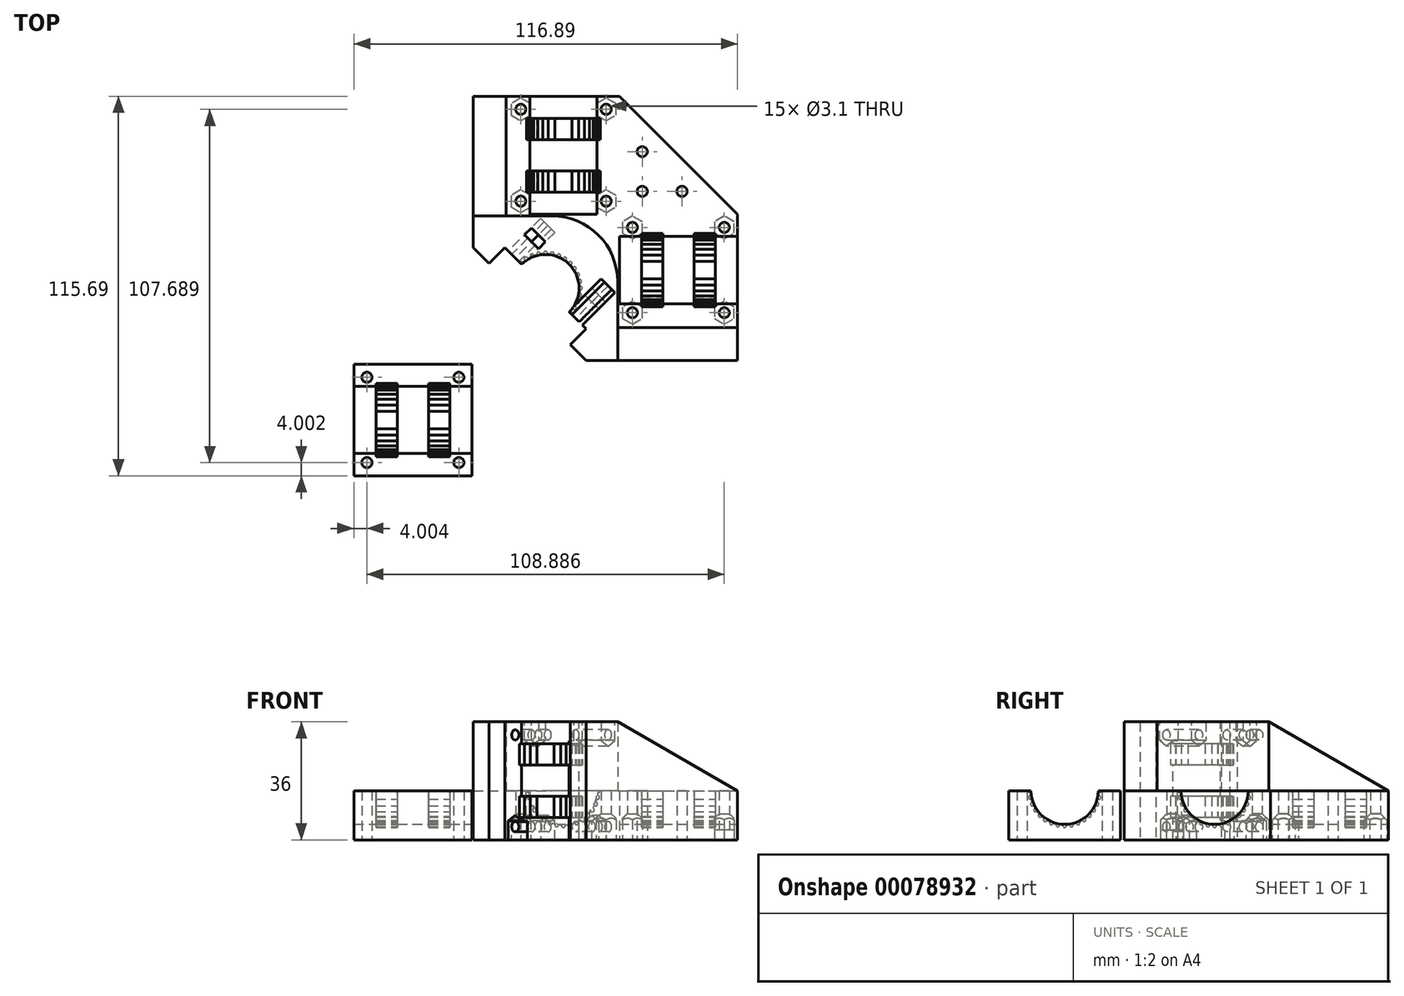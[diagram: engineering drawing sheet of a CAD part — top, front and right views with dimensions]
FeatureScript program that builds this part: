
annotation { "Feature Type Name" : "Feature", "Feature Type Description" : "" }
export const myFeature = defineFeature(function(context is Context, id is Id, definition is map)
    precondition{}
    {
        {
            var Q0;
            Q0=qCreatedBy(makeId("Top.planeOp"),FACE);
            var sketch = newSketch(context, id + "F0", { "sketchPlane" : qUnion([Q0])});
            skLineSegment(sketch, "E0.bottom", {"start": v(34, 0) * mm, "end": v(70, 0) * mm});
            skLineSegment(sketch, "E0.top", {"start": v(34, 34) * mm, "end": v(70, 34) * mm});
            skLineSegment(sketch, "E0.left", {"start": v(34, 0) * mm, "end": v(34, 34) * mm});
            skLineSegment(sketch, "E0.right", {"start": v(70, 0) * mm, "end": v(70, 34) * mm});
            skLineSegment(sketch, "E1", {"start": v(52, 34) * mm, "end": v(52, 0) * mm, "construction": true});
            skLineSegment(sketch, "E2", {"start": v(34, 17) * mm, "end": v(70, 17) * mm, "construction": true});
            skLineSegment(sketch, "E3", {"start": v(34, 34) * mm, "end": v(34, 70) * mm});
            skLineSegment(sketch, "E4", {"start": v(34, 70) * mm, "end": v(0, 70) * mm});
            skLineSegment(sketch, "E5", {"start": v(0, 70) * mm, "end": v(0, 34) * mm});
            skLineSegment(sketch, "E6", {"start": v(0, 34) * mm, "end": v(34, 34) * mm});
            skLineSegment(sketch, "E7", {"start": v(17, 70) * mm, "end": v(17, 34) * mm, "construction": true});
            skLineSegment(sketch, "E8", {"start": v(0, 52) * mm, "end": v(34, 52) * mm, "construction": true});
            skCircle(sketch, "E9", {"center": v(66, 30) * mm, "radius": 1.55 * mm});
            skPoint(sketch, "E10", {"position": v(60, 17) * mm});
            skCircle(sketch, "E11.MirrorC", {"center": v(38, 30) * mm, "radius": 1.55 * mm});
            skPoint(sketch, "E12.MirrorP", {"position": v(44, 17) * mm});
            skCircle(sketch, "E13.MirrorC", {"center": v(38, 4) * mm, "radius": 1.55 * mm});
            skCircle(sketch, "E14.MirrorC", {"center": v(66, 4) * mm, "radius": 1.55 * mm});
            skCircle(sketch, "E15", {"center": v(30, 66) * mm, "radius": 1.55 * mm});
            skPoint(sketch, "E16", {"position": v(17, 60) * mm});
            skCircle(sketch, "E17.MirrorC", {"center": v(4, 66) * mm, "radius": 1.55 * mm});
            skCircle(sketch, "E18.MirrorC", {"center": v(30, 38) * mm, "radius": 1.55 * mm});
            skPoint(sketch, "E19.MirrorP", {"position": v(17, 44) * mm});
            skCircle(sketch, "E20.MirrorC", {"center": v(4, 38) * mm, "radius": 1.55 * mm});
            skLineSegment(sketch, "E21", {"start": v(34, 70) * mm, "end": v(70, 34) * mm});
            skLineSegment(sketch, "E22", {"start": v(0, 70) * mm, "end": v(-0.5, 70) * mm});
            skLineSegment(sketch, "E23", {"start": v(-0.5, 70) * mm, "end": v(-0.5, 34) * mm});
            skLineSegment(sketch, "E24", {"start": v(33.5, -0.5) * mm, "end": v(70, -0.5) * mm});
            skLineSegment(sketch, "E25", {"start": v(70, -0.5) * mm, "end": v(70, 0) * mm});
            skLineSegment(sketch, "E26", {"start": v(-0.5, 34) * mm, "end": v(-0.5, 33.5) * mm});
            skLineSegment(sketch, "E27", {"start": v(-0.5, 33.5) * mm, "end": v(33.5, 33.5) * mm});
            skLineSegment(sketch, "E28", {"start": v(33.5, 33.5) * mm, "end": v(33.5, -0.5) * mm});
            skLineSegment(sketch, "E29", {"start": v(-0.5, 33.5) * mm, "end": v(33.5, -0.5) * mm});
            skLineSegment(sketch, "E30.0", {"start": v(41, 41) * mm, "end": v(41, 53.1) * mm, "construction": true});
            skLineSegment(sketch, "E30.1", {"start": v(41, 41) * mm, "end": v(53.1, 41) * mm, "construction": true});
            skLineSegment(sketch, "E30.2", {"start": v(41, 53.1) * mm, "end": v(53.1, 41) * mm, "construction": true});
            skLineSegment(sketch, "E31", {"start": v(70, -0.5) * mm, "end": v(70, -10.5) * mm});
            skLineSegment(sketch, "E32", {"start": v(70, -10.5) * mm, "end": v(33.5, -10.5) * mm});
            skLineSegment(sketch, "E33", {"start": v(33.5, -10.5) * mm, "end": v(-10.5, 33.5) * mm});
            skLineSegment(sketch, "E34", {"start": v(-10.5, 33.5) * mm, "end": v(-10.5, 70) * mm});
            skLineSegment(sketch, "E35", {"start": v(-10.5, 70) * mm, "end": v(-0.5, 70) * mm});
            skLineSegment(sketch, "E36", {"start": v(34, 34) * mm, "end": v(0, 0) * mm, "construction": true});
            skPoint(sketch, "E37", {"position": v(-0.87, 23.87) * mm});
            skPoint(sketch, "E38.MirrorP", {"position": v(23.87, -0.87) * mm});
            skLineSegment(sketch, "E39", {"start": v(33.5, -10.5) * mm, "end": v(23.87, -10.5) * mm});
            skLineSegment(sketch, "E40", {"start": v(23.87, -10.5) * mm, "end": v(23.87, -0.87) * mm});
            skLineSegment(sketch, "E41", {"start": v(-10.5, 33.5) * mm, "end": v(-10.5, 23.87) * mm});
            skLineSegment(sketch, "E42", {"start": v(-10.5, 23.87) * mm, "end": v(-0.87, 23.87) * mm});
            skLineSegment(sketch, "E43", {"start": v(23.87, -10.5) * mm, "end": v(19.06, -5.69) * mm});
            skLineSegment(sketch, "E44", {"start": v(19.06, -5.69) * mm, "end": v(23.87, -0.87) * mm});
            skLineSegment(sketch, "E45", {"start": v(-10.5, 23.87) * mm, "end": v(-5.69, 19.06) * mm});
            skLineSegment(sketch, "E46", {"start": v(-5.69, 19.06) * mm, "end": v(-0.87, 23.87) * mm});
            skCircle(sketch, "E47", {"center": v(41, 41) * mm, "radius": 1.55 * mm});
            skCircle(sketch, "E48", {"center": v(53.1, 41) * mm, "radius": 1.55 * mm});
            skCircle(sketch, "E49", {"center": v(41, 53.1) * mm, "radius": 1.55 * mm});
            skSolve(sketch);
        }
        {
            var Q0;
            Q0=makeQuery(id+"F0.imprint","IMPRINT",FACE,{"disambiguationData":[TD([[makeQuery(id+"F0.imprint","IMPRINT",EDGE,{"derivedFrom":sQuery(id+"F0.wireOp",EDGE,"E3")}),1.0]])]});
            var Q1;
            Q1=makeQuery(id+"F0.imprint","IMPRINT",FACE,{"disambiguationData":[TD([[makeQuery(id+"F0.imprint","IMPRINT",EDGE,{"derivedFrom":sQuery(id+"F0.wireOp",EDGE,"E0.bottom")}),1.0]])]});
            var Q2;
            Q2=makeQuery(id+"F0.imprint","IMPRINT",FACE,{"disambiguationData":[TD([[makeQuery(id+"F0.imprint","IMPRINT",EDGE,{"derivedFrom":sQuery(id+"F0.wireOp",EDGE,"E0.top")}),1.0]])]});
            var Q3;
            Q3=makeQuery(id+"F0.imprint","IMPRINT",FACE,{"disambiguationData":[TD([[makeQuery(id+"F0.imprint","IMPRINT",EDGE,{"derivedFrom":sQuery(id+"F0.wireOp",EDGE,"E0.bottom")}),-1.0]])]});
            extrude(context, id + "F1", {"entities" : qUnion([Q0, Q1, Q2, Q3]), "depth" : 15 * mm});
        }
        {
            var Q0;
            Q0=makeQuery(id+"F0.imprint","IMPRINT",FACE,{"disambiguationData":[TD([[makeQuery(id+"F0.imprint","IMPRINT",EDGE,{"derivedFrom":sQuery(id+"F0.wireOp",EDGE,"E27")}),-1.0]])]});
            var Q1;
            Q1=makeQuery(id+"F0.imprint","IMPRINT",FACE,{"disambiguationData":[TD([[makeQuery(id+"F0.imprint","IMPRINT",EDGE,{"derivedFrom":sQuery(id+"F0.wireOp",EDGE,"E23")}),-1.0]])]});
            var Q2;
            {var subQ0=sQuery(id+"F0.wireOp",EDGE,"E41");Q2=makeQuery(id+"F0.imprint","IMPRINT",FACE,{"disambiguationData":[TD([[makeQuery(id+"F0.imprint","IMPRINT",EDGE,{"derivedFrom":subQ0}),1.0]])]});}
            var Q3;
            {var subQ0=sQuery(id+"F0.wireOp",EDGE,"E39");Q3=makeQuery(id+"F0.imprint","IMPRINT",FACE,{"disambiguationData":[TD([[makeQuery(id+"F0.imprint","IMPRINT",EDGE,{"derivedFrom":subQ0}),-1.0]])]});}
            var Q4;
            Q4=makeQuery(id+"F0.imprint","IMPRINT",FACE,{"disambiguationData":[TD([[makeQuery(id+"F0.imprint","IMPRINT",EDGE,{"derivedFrom":sQuery(id+"F0.wireOp",EDGE,"E40")}),1.0]])]});
            var Q5;
            Q5=makeQuery(id+"F0.imprint","IMPRINT",FACE,{"disambiguationData":[TD([[makeQuery(id+"F0.imprint","IMPRINT",EDGE,{"derivedFrom":sQuery(id+"F0.wireOp",EDGE,"E42")}),-1.0]])]});
            extrude(context, id + "F2", {"entities" : qUnion([Q0, Q1, Q2, Q3, Q4, Q5]), "operationType" : NewBodyOperationType.ADD, "depth" : 36 * mm});
        }
        {
            var Q0;
            Q0=makeQuery(id+"F1.opExtrude","SWEPT_FACE",FACE,{"disambiguationData":[OSD([sQuery(id+"F0.wireOp",EDGE,"E0.right"),sQuery(id+"F0.wireOp",EDGE,"E25")])]});
            var sketch = newSketch(context, id + "F3", { "sketchPlane" : qUnion([Q0])});
            skLineSegment(sketch, "E50.0", {"start": v(5.55, 15) * mm, "end": v(2.45, 15) * mm});
            skLineSegment(sketch, "E51.0", {"start": v(28.45, 15) * mm, "end": v(31.55, 15) * mm});
            skLineSegment(sketch, "E52", {"start": v(5.55, 15) * mm, "end": v(28.45, 15) * mm});
            skPoint(sketch, "E53", {"position": v(17, 15) * mm});
            skArc(sketch, "E54", {"start": v(6.75, 15) * mm, "mid": v(17, 4.75) * mm, "end": v(27.25, 15) * mm});
            skSolve(sketch);
        }
        {
            var Q0;
            Q0=qSketchRegion(id+"F3",true);
            var Q1;
            Q1=makeQuery(id+"F2.opExtrude","SWEPT_FACE",FACE,{"disambiguationData":[OSD([sQuery(id+"F0.wireOp",EDGE,"E28")])]});
            extrude(context, id + "F4", {"entities" : qUnion([Q0]), "operationType" : NewBodyOperationType.REMOVE, "oppositeDirection" : true, "endBoundEntityFace" : qUnion([Q1]), "depth" : 36 * mm});
        }
        {
            var Q0;
            Q0=makeQuery(id+"F1.opExtrude","SWEPT_FACE",FACE,{"disambiguationData":[OSD([sQuery(id+"F0.wireOp",EDGE,"E4"),sQuery(id+"F0.wireOp",EDGE,"E22")])]});
            var sketch = newSketch(context, id + "F5", { "sketchPlane" : qUnion([Q0])});
            skLineSegment(sketch, "E55", {"start": v(-28.45, 15) * mm, "end": v(-5.55, 15) * mm});
            skPoint(sketch, "E56.0.start.orphan", {"position": v(-31.55, 15) * mm});
            skPoint(sketch, "E57.0.start.orphan", {"position": v(-2.45, 15) * mm});
            skPoint(sketch, "E58", {"position": v(-17, 15) * mm});
            skArc(sketch, "E59", {"start": v(-27.25, 15) * mm, "mid": v(-17, 4.75) * mm, "end": v(-6.75, 15) * mm});
            skSolve(sketch);
        }
        {
            var Q0;
            Q0=qSketchRegion(id+"F5",true);
            var Q1;
            Q1=makeQuery(id+"F2.opExtrude","SWEPT_FACE",FACE,{"disambiguationData":[OSD([sQuery(id+"F0.wireOp",EDGE,"E27")])]});
            extrude(context, id + "F6", {"entities" : qUnion([Q0]), "operationType" : NewBodyOperationType.REMOVE, "oppositeDirection" : true, "endBoundEntityFace" : qUnion([Q1]), "depth" : 36 * mm});
        }
        {
            var Q0;
            Q0=makeQuery(id+"F2.opExtrude","CAP_FACE",FACE,{"disambiguationData":[OSD([sQuery(id+"F0.wireOp",EDGE,"E23"),sQuery(id+"F0.wireOp",EDGE,"E24"),sQuery(id+"F0.wireOp",EDGE,"E26"),sQuery(id+"F0.wireOp",EDGE,"E27"),sQuery(id+"F0.wireOp",EDGE,"E28"),sQuery(id+"F0.wireOp",EDGE,"E31"),sQuery(id+"F0.wireOp",EDGE,"E32"),sQuery(id+"F0.wireOp",EDGE,"E33"),sQuery(id+"F0.wireOp",EDGE,"E34"),sQuery(id+"F0.wireOp",EDGE,"E35")])],"isStart":false});
            var sketch = newSketch(context, id + "F7", { "sketchPlane" : qUnion([Q0])});
            skLineSegment(sketch, "E60.0", {"start": v(-0.87, 23.87) * mm, "end": v(23.87, -0.87) * mm});
            skArc(sketch, "E61", {"start": v(18.75, 4.25) * mm, "mid": v(18.75, 18.75) * mm, "end": v(4.25, 18.75) * mm});
            skSolve(sketch);
        }
        {
            var Q0;
            Q0=qSketchRegion(id+"F7",true);
            var Q1;
            Q1=makeQuery(id+"F2.opExtrude","CAP_FACE",FACE,{"disambiguationData":[OSD([sQuery(id+"F0.wireOp",EDGE,"E27"),sQuery(id+"F0.wireOp",EDGE,"E28"),sQuery(id+"F0.wireOp",EDGE,"E29")])],"isStart":true});
            extrude(context, id + "F8", {"entities" : qUnion([Q0]), "operationType" : NewBodyOperationType.REMOVE, "endBound" : BoundingType.UP_TO_SURFACE, "oppositeDirection" : true, "endBoundEntityFace" : qUnion([Q1]), "depth" : 25 * mm});
        }
        {
            var Q0;
            {var subQ0=sQuery(id+"F0.wireOp",EDGE,"E44");var subQ8=sQuery(id+"F0.wireOp",EDGE,"E33");Q0=makeQuery(id+"F8.boolean.opBoolean","SPLIT",FACE,{"disambiguationData":[TD([makeQuery(id+"F2.opExtrude","SWEPT_FACE",FACE,{"disambiguationData":[OSD([subQ0])]})])],"derivedFrom":makeQuery(id+"F2.opExtrude","SWEPT_FACE",FACE,{"disambiguationData":[OSD([subQ8])]})});}
            cPlane(context, id + "F9", {"entities" : qUnion([Q0]), "cplaneType" : CPlaneType.OFFSET, "offset" : 7 * mm, "oppositeDirection" : true, "width" : 150 * mm, "height" : 150 * mm});
        }
        {
            var Q0;
            Q0=qCreatedBy(id+"F9.planeOp",FACE);
            var sketch = newSketch(context, id + "F10", { "sketchPlane" : qUnion([Q0])});
            skPoint(sketch, "E62.0", {"position": v(-24.04, 36) * mm});
            skPoint(sketch, "E63.0", {"position": v(24.04, 36) * mm});
            skPoint(sketch, "E64.0", {"position": v(24.04, 0) * mm});
            skPoint(sketch, "E65.0", {"position": v(-24.04, 0) * mm});
            skLineSegment(sketch, "E66", {"start": v(-24.04, 0) * mm, "end": v(-24.04, 36) * mm, "construction": true});
            skLineSegment(sketch, "E67", {"start": v(-24.04, 36) * mm, "end": v(24.04, 36) * mm, "construction": true});
            skLineSegment(sketch, "E68", {"start": v(24.04, 36) * mm, "end": v(24.04, 0) * mm, "construction": true});
            skLineSegment(sketch, "E69", {"start": v(24.04, 0) * mm, "end": v(-24.04, 0) * mm, "construction": true});
            skLineSegment(sketch, "E70", {"start": v(0, 0) * mm, "end": v(0, 36) * mm, "construction": true});
            skLineSegment(sketch, "E71", {"start": v(-24.04, 18) * mm, "end": v(24.04, 18) * mm, "construction": true});
            skCircle(sketch, "E72", {"center": v(-13, 32) * mm, "radius": 1.55 * mm});
            skCircle(sketch, "E73.cCircle", {"center": v(-13, 32) * mm, "radius": 3 * mm, "construction": true});
            skLineSegment(sketch, "E73.0", {"start": v(-10, 33.73) * mm, "end": v(-10, 30.27) * mm});
            skLineSegment(sketch, "E73.1", {"start": v(-10, 30.27) * mm, "end": v(-13, 28.54) * mm});
            skLineSegment(sketch, "E73.2", {"start": v(-13, 28.54) * mm, "end": v(-16, 30.27) * mm});
            skLineSegment(sketch, "E73.3", {"start": v(-16, 30.27) * mm, "end": v(-16, 33.73) * mm});
            skLineSegment(sketch, "E73.4", {"start": v(-16, 33.73) * mm, "end": v(-13, 35.46) * mm, "construction": true});
            skLineSegment(sketch, "E73.5", {"start": v(-13, 35.46) * mm, "end": v(-10, 33.73) * mm, "construction": true});
            skPoint(sketch, "E73.0.midPoint", {"position": v(-10, 32) * mm});
            skLineSegment(sketch, "E74", {"start": v(-16, 33.73) * mm, "end": v(-16, 36) * mm});
            skLineSegment(sketch, "E75", {"start": v(-16, 36) * mm, "end": v(-10, 36) * mm});
            skLineSegment(sketch, "E76", {"start": v(-10, 36) * mm, "end": v(-10, 33.73) * mm});
            skCircle(sketch, "E77.MirrorC", {"center": v(-13, 4) * mm, "radius": 1.55 * mm});
            skLineSegment(sketch, "E78.MirrorCS", {"start": v(-16, 2.27) * mm, "end": v(-16, 0) * mm});
            skLineSegment(sketch, "E79.MirrorCS", {"start": v(-16, 5.73) * mm, "end": v(-16, 2.27) * mm});
            skLineSegment(sketch, "E80.MirrorCS", {"start": v(-13, 7.46) * mm, "end": v(-16, 5.73) * mm});
            skLineSegment(sketch, "E81.MirrorCS", {"start": v(-10, 5.73) * mm, "end": v(-13, 7.46) * mm});
            skLineSegment(sketch, "E82.MirrorCS", {"start": v(-10, 2.27) * mm, "end": v(-10, 5.73) * mm});
            skLineSegment(sketch, "E83.MirrorCS", {"start": v(-10, 0) * mm, "end": v(-10, 2.27) * mm});
            skLineSegment(sketch, "E84.MirrorCS", {"start": v(10, 36) * mm, "end": v(10, 33.73) * mm});
            skLineSegment(sketch, "E85.MirrorCS", {"start": v(10, 33.73) * mm, "end": v(10, 30.27) * mm});
            skLineSegment(sketch, "E86.MirrorCS", {"start": v(10, 30.27) * mm, "end": v(13, 28.54) * mm});
            skLineSegment(sketch, "E87.MirrorCS", {"start": v(13, 28.54) * mm, "end": v(16, 30.27) * mm});
            skLineSegment(sketch, "E88.MirrorCS", {"start": v(16, 30.27) * mm, "end": v(16, 33.73) * mm});
            skLineSegment(sketch, "E89.MirrorCS", {"start": v(16, 33.73) * mm, "end": v(16, 36) * mm});
            skCircle(sketch, "E90.MirrorC", {"center": v(13, 32) * mm, "radius": 1.55 * mm});
            skLineSegment(sketch, "E91.MirrorCS", {"start": v(16, 2.27) * mm, "end": v(16, 0) * mm});
            skLineSegment(sketch, "E92.MirrorCS", {"start": v(16, 5.73) * mm, "end": v(16, 2.27) * mm});
            skLineSegment(sketch, "E93.MirrorCS", {"start": v(13, 7.46) * mm, "end": v(16, 5.73) * mm});
            skLineSegment(sketch, "E94.MirrorCS", {"start": v(10, 5.73) * mm, "end": v(13, 7.46) * mm});
            skLineSegment(sketch, "E95.MirrorCS", {"start": v(10, 2.27) * mm, "end": v(10, 5.73) * mm});
            skLineSegment(sketch, "E96.MirrorCS", {"start": v(10, 0) * mm, "end": v(10, 2.27) * mm});
            skCircle(sketch, "E97.MirrorC", {"center": v(13, 4) * mm, "radius": 1.55 * mm});
            skLineSegment(sketch, "E98", {"start": v(-16, 0) * mm, "end": v(-10, 0) * mm});
            skLineSegment(sketch, "E99", {"start": v(10, 0) * mm, "end": v(16, 0) * mm});
            skLineSegment(sketch, "E100", {"start": v(16, 36) * mm, "end": v(10, 36) * mm});
            skLineSegment(sketch, "E101", {"start": v(-13, 32) * mm, "end": v(-13, 36) * mm, "construction": true});
            skLineSegment(sketch, "E102.0", {"start": v(-10.25, 0) * mm, "end": v(-10.25, 36) * mm, "construction": true});
            skLineSegment(sketch, "E103.0", {"start": v(10.25, 0) * mm, "end": v(10.25, 36) * mm, "construction": true});
            skPoint(sketch, "E104", {"position": v(0, 18) * mm});
            skPoint(sketch, "E105", {"position": v(0, 26) * mm});
            skPoint(sketch, "E106.MirrorP", {"position": v(0, 10) * mm});
            skSolve(sketch);
        }
        {
            var Q0;
            Q0=makeQuery(id+"F10.imprint","IMPRINT",FACE,{"disambiguationData":[TD([[makeQuery(id+"F10.imprint","IMPRINT",EDGE,{"derivedFrom":sQuery(id+"F10.wireOp",EDGE,"E72")}),1.0]])]});
            var Q1;
            Q1=makeQuery(id+"F10.imprint","IMPRINT",FACE,{"disambiguationData":[TD([[makeQuery(id+"F10.imprint","IMPRINT",EDGE,{"derivedFrom":sQuery(id+"F10.wireOp",EDGE,"E77.MirrorC")}),-1.0]])]});
            var Q2;
            Q2=makeQuery(id+"F10.imprint","IMPRINT",FACE,{"disambiguationData":[TD([[makeQuery(id+"F10.imprint","IMPRINT",EDGE,{"derivedFrom":sQuery(id+"F10.wireOp",EDGE,"E97.MirrorC")}),1.0]])]});
            var Q3;
            Q3=makeQuery(id+"F10.imprint","IMPRINT",FACE,{"disambiguationData":[TD([[makeQuery(id+"F10.imprint","IMPRINT",EDGE,{"derivedFrom":sQuery(id+"F10.wireOp",EDGE,"E90.MirrorC")}),-1.0]])]});
            extrude(context, id + "F11", {"entities" : qUnion([Q0, Q1, Q2, Q3]), "operationType" : NewBodyOperationType.REMOVE, "oppositeDirection" : true, "depth" : 7 * mm, "hasSecondDirection" : true, "secondDirectionOppositeDirection" : false, "secondDirectionDepth" : 25 * mm});
        }
        {
            var Q0;
            Q0=makeQuery(id+"F10.imprint","IMPRINT",FACE,{"disambiguationData":[TD([[makeQuery(id+"F10.imprint","IMPRINT",EDGE,{"derivedFrom":sQuery(id+"F10.wireOp",EDGE,"E72")}),-1.0]])]});
            var Q1;
            Q1=makeQuery(id+"F10.imprint","IMPRINT",FACE,{"disambiguationData":[TD([[makeQuery(id+"F10.imprint","IMPRINT",EDGE,{"derivedFrom":sQuery(id+"F10.wireOp",EDGE,"E77.MirrorC")}),1.0]])]});
            var Q2;
            Q2=makeQuery(id+"F10.imprint","IMPRINT",FACE,{"disambiguationData":[TD([[makeQuery(id+"F10.imprint","IMPRINT",EDGE,{"derivedFrom":sQuery(id+"F10.wireOp",EDGE,"E91.MirrorCS")}),-1.0]])]});
            var Q3;
            Q3=makeQuery(id+"F10.imprint","IMPRINT",FACE,{"disambiguationData":[TD([[makeQuery(id+"F10.imprint","IMPRINT",EDGE,{"derivedFrom":sQuery(id+"F10.wireOp",EDGE,"E84.MirrorCS")}),1.0]])]});
            extrude(context, id + "F12", {"entities" : qUnion([Q0, Q1, Q2, Q3]), "operationType" : NewBodyOperationType.REMOVE, "oppositeDirection" : true, "depth" : 3 * mm});
        }
        {
            var Q0;
            Q0=makeQuery(id+"F2.opExtrude","SWEPT_FACE",FACE,{"disambiguationData":[OSD([sQuery(id+"F0.wireOp",EDGE,"E24")])]});
            var sketch = newSketch(context, id + "F13", { "sketchPlane" : qUnion([Q0])});
            skLineSegment(sketch, "E107", {"start": v(-33.5, 36) * mm, "end": v(-70, 15) * mm});
            skLineSegment(sketch, "E108.0", {"start": v(-33.5, 36) * mm, "end": v(-70, 36) * mm});
            skLineSegment(sketch, "E109.0", {"start": v(-70, 36) * mm, "end": v(-70, 15) * mm});
            skSolve(sketch);
        }
        {
            var Q0;
            Q0=qSketchRegion(id+"F13",true);
            var Q1;
            Q1=makeQuery(id+"F2.opExtrude","SWEPT_FACE",FACE,{"disambiguationData":[OSD([sQuery(id+"F0.wireOp",EDGE,"E32"),sQuery(id+"F0.wireOp",EDGE,"E39")])]});
            extrude(context, id + "F14", {"entities" : qUnion([Q0]), "operationType" : NewBodyOperationType.REMOVE, "endBound" : BoundingType.UP_TO_SURFACE, "oppositeDirection" : true, "endBoundEntityFace" : qUnion([Q1]), "depth" : 25 * mm});
        }
        {
            var Q0;
            Q0=makeQuery(id+"F2.opExtrude","SWEPT_FACE",FACE,{"disambiguationData":[OSD([sQuery(id+"F0.wireOp",EDGE,"E23"),sQuery(id+"F0.wireOp",EDGE,"E26")])]});
            var sketch = newSketch(context, id + "F15", { "sketchPlane" : qUnion([Q0])});
            skLineSegment(sketch, "E110.0", {"start": v(70, 36) * mm, "end": v(33.5, 36) * mm});
            skLineSegment(sketch, "E111.0", {"start": v(70, 36) * mm, "end": v(70, 15) * mm});
            skLineSegment(sketch, "E112", {"start": v(33.5, 36) * mm, "end": v(70, 15) * mm});
            skSolve(sketch);
        }
        {
            var Q0;
            Q0=qSketchRegion(id+"F15",true);
            var Q1;
            Q1=makeQuery(id+"F2.opExtrude","SWEPT_FACE",FACE,{"disambiguationData":[OSD([sQuery(id+"F0.wireOp",EDGE,"E34"),sQuery(id+"F0.wireOp",EDGE,"E41")])]});
            extrude(context, id + "F16", {"entities" : qUnion([Q0]), "operationType" : NewBodyOperationType.REMOVE, "endBound" : BoundingType.UP_TO_SURFACE, "oppositeDirection" : true, "endBoundEntityFace" : qUnion([Q1]), "depth" : 25 * mm});
        }
        {
            var Q0;
            Q0=makeQuery(id+"F2.opExtrude","SWEPT_EDGE",EDGE,{"disambiguationData":[OSD([sQuery(id+"F0.wireOp",EDGE,"E27"),sQuery(id+"F0.wireOp",EDGE,"E28")])]});
            fillet(context, id + "F17", {"entities" : qUnion([Q0]), "radius" : 20 * mm, "tangentPropagation" : true, "allowEdgeOverflow" : false});
        }
        {
            var Q0;
            {var subQ0=sQuery(id+"F0.wireOp",EDGE,"E28");var subQ1=sQuery(id+"F0.wireOp",EDGE,"E27");var subQ2=sQuery(id+"F0.wireOp",EDGE,"E26");var subQ3=sQuery(id+"F0.wireOp",EDGE,"E24");var subQ4=sQuery(id+"F0.wireOp",EDGE,"E23");Q0=makeQuery(id+"F2.boolean.opBoolean","MERGE",FACE,{"derivedFrom":[makeQuery(id+"F1.opExtrude","CAP_FACE",FACE,{"disambiguationData":[OSD([sQuery(id+"F0.wireOp",EDGE,"E0.right"),sQuery(id+"F0.wireOp",EDGE,"E4"),sQuery(id+"F0.wireOp",EDGE,"E9"),sQuery(id+"F0.wireOp",EDGE,"E11.MirrorC"),sQuery(id+"F0.wireOp",EDGE,"E13.MirrorC"),sQuery(id+"F0.wireOp",EDGE,"E14.MirrorC"),sQuery(id+"F0.wireOp",EDGE,"E15"),sQuery(id+"F0.wireOp",EDGE,"E17.MirrorC"),sQuery(id+"F0.wireOp",EDGE,"E18.MirrorC"),sQuery(id+"F0.wireOp",EDGE,"E20.MirrorC"),sQuery(id+"F0.wireOp",EDGE,"E21"),sQuery(id+"F0.wireOp",EDGE,"E22"),subQ4,subQ3,sQuery(id+"F0.wireOp",EDGE,"E25"),subQ2,subQ1,subQ0,sQuery(id+"F0.wireOp",EDGE,"E30.0"),sQuery(id+"F0.wireOp",EDGE,"E30.1"),sQuery(id+"F0.wireOp",EDGE,"E30.2")])],"isStart":true}),makeQuery(id+"F2.opExtrude","CAP_FACE",FACE,{"disambiguationData":[OSD([subQ4,subQ3,subQ2,subQ1,subQ0,sQuery(id+"F0.wireOp",EDGE,"E31"),sQuery(id+"F0.wireOp",EDGE,"E32"),sQuery(id+"F0.wireOp",EDGE,"E33"),sQuery(id+"F0.wireOp",EDGE,"E34"),sQuery(id+"F0.wireOp",EDGE,"E35"),sQuery(id+"F0.wireOp",EDGE,"E39"),sQuery(id+"F0.wireOp",EDGE,"E41"),sQuery(id+"F0.wireOp",EDGE,"E43"),sQuery(id+"F0.wireOp",EDGE,"E44"),sQuery(id+"F0.wireOp",EDGE,"E45"),sQuery(id+"F0.wireOp",EDGE,"E46")])],"isStart":true})]});}
            var sketch = newSketch(context, id + "F18", { "sketchPlane" : qUnion([Q0])});
            skCircle(sketch, "E113.0", {"center": v(66, -4) * mm, "radius": 1.55 * mm});
            skCircle(sketch, "E114.0", {"center": v(66, -30) * mm, "radius": 1.55 * mm, "construction": true});
            skCircle(sketch, "E115.0", {"center": v(38, -4) * mm, "radius": 1.55 * mm, "construction": true});
            skCircle(sketch, "E116.0", {"center": v(38, -30) * mm, "radius": 1.55 * mm, "construction": true});
            skCircle(sketch, "E117.0", {"center": v(30, -38) * mm, "radius": 1.55 * mm, "construction": true});
            skCircle(sketch, "E118.0", {"center": v(30, -66) * mm, "radius": 1.55 * mm, "construction": true});
            skCircle(sketch, "E119.0", {"center": v(4, -66) * mm, "radius": 1.55 * mm, "construction": true});
            skCircle(sketch, "E120.0", {"center": v(4, -38) * mm, "radius": 1.55 * mm, "construction": true});
            skCircle(sketch, "E121.cCircle", {"center": v(66, -4) * mm, "radius": 3 * mm, "construction": true});
            skLineSegment(sketch, "E121.0", {"start": v(66, -7.46) * mm, "end": v(63, -5.73) * mm});
            skLineSegment(sketch, "E121.1", {"start": v(63, -5.73) * mm, "end": v(63, -2.27) * mm});
            skLineSegment(sketch, "E121.2", {"start": v(63, -2.27) * mm, "end": v(66, -0.54) * mm});
            skLineSegment(sketch, "E121.3", {"start": v(66, -0.54) * mm, "end": v(69, -2.27) * mm});
            skLineSegment(sketch, "E121.4", {"start": v(69, -2.27) * mm, "end": v(69, -5.73) * mm});
            skLineSegment(sketch, "E121.5", {"start": v(69, -5.73) * mm, "end": v(66, -7.46) * mm});
            skPoint(sketch, "E121.0.midPoint", {"position": v(64.5, -6.6) * mm});
            skCircle(sketch, "E122.cCircle", {"center": v(66, -30) * mm, "radius": 3 * mm, "construction": true});
            skLineSegment(sketch, "E122.0", {"start": v(63, -31.73) * mm, "end": v(63, -28.27) * mm});
            skLineSegment(sketch, "E122.1", {"start": v(63, -28.27) * mm, "end": v(66, -26.54) * mm});
            skLineSegment(sketch, "E122.2", {"start": v(66, -26.54) * mm, "end": v(69, -28.27) * mm});
            skLineSegment(sketch, "E122.3", {"start": v(69, -28.27) * mm, "end": v(69, -31.73) * mm});
            skLineSegment(sketch, "E122.4", {"start": v(69, -31.73) * mm, "end": v(66, -33.46) * mm});
            skLineSegment(sketch, "E122.5", {"start": v(66, -33.46) * mm, "end": v(63, -31.73) * mm});
            skPoint(sketch, "E122.0.midPoint", {"position": v(63, -30) * mm});
            skCircle(sketch, "E123.cCircle", {"center": v(38, -4) * mm, "radius": 3 * mm, "construction": true});
            skLineSegment(sketch, "E123.0", {"start": v(35, -5.73) * mm, "end": v(35, -2.27) * mm});
            skLineSegment(sketch, "E123.1", {"start": v(35, -2.27) * mm, "end": v(38, -0.54) * mm});
            skLineSegment(sketch, "E123.2", {"start": v(38, -0.54) * mm, "end": v(41, -2.27) * mm});
            skLineSegment(sketch, "E123.3", {"start": v(41, -2.27) * mm, "end": v(41, -5.73) * mm});
            skLineSegment(sketch, "E123.4", {"start": v(41, -5.73) * mm, "end": v(38, -7.46) * mm});
            skLineSegment(sketch, "E123.5", {"start": v(38, -7.46) * mm, "end": v(35, -5.73) * mm});
            skPoint(sketch, "E123.0.midPoint", {"position": v(35, -4) * mm});
            skCircle(sketch, "E124.cCircle", {"center": v(38, -30) * mm, "radius": 3 * mm, "construction": true});
            skLineSegment(sketch, "E124.0", {"start": v(35, -31.73) * mm, "end": v(35, -28.27) * mm});
            skLineSegment(sketch, "E124.1", {"start": v(35, -28.27) * mm, "end": v(38, -26.54) * mm});
            skLineSegment(sketch, "E124.2", {"start": v(38, -26.54) * mm, "end": v(41, -28.27) * mm});
            skLineSegment(sketch, "E124.3", {"start": v(41, -28.27) * mm, "end": v(41, -31.73) * mm});
            skLineSegment(sketch, "E124.4", {"start": v(41, -31.73) * mm, "end": v(38, -33.46) * mm});
            skLineSegment(sketch, "E124.5", {"start": v(38, -33.46) * mm, "end": v(35, -31.73) * mm});
            skPoint(sketch, "E124.0.midPoint", {"position": v(35, -30) * mm});
            skCircle(sketch, "E125.cCircle", {"center": v(30, -38) * mm, "radius": 3 * mm, "construction": true});
            skLineSegment(sketch, "E125.0", {"start": v(27, -39.73) * mm, "end": v(27, -36.27) * mm});
            skLineSegment(sketch, "E125.1", {"start": v(27, -36.27) * mm, "end": v(30, -34.54) * mm});
            skLineSegment(sketch, "E125.2", {"start": v(30, -34.54) * mm, "end": v(33, -36.27) * mm});
            skLineSegment(sketch, "E125.3", {"start": v(33, -36.27) * mm, "end": v(33, -39.73) * mm});
            skLineSegment(sketch, "E125.4", {"start": v(33, -39.73) * mm, "end": v(30, -41.46) * mm});
            skLineSegment(sketch, "E125.5", {"start": v(30, -41.46) * mm, "end": v(27, -39.73) * mm});
            skPoint(sketch, "E125.0.midPoint", {"position": v(27, -38) * mm});
            skCircle(sketch, "E126.cCircle", {"center": v(4, -38) * mm, "radius": 3 * mm, "construction": true});
            skLineSegment(sketch, "E126.0", {"start": v(1, -39.73) * mm, "end": v(1, -36.27) * mm});
            skLineSegment(sketch, "E126.1", {"start": v(1, -36.27) * mm, "end": v(4, -34.54) * mm});
            skLineSegment(sketch, "E126.2", {"start": v(4, -34.54) * mm, "end": v(7, -36.27) * mm});
            skLineSegment(sketch, "E126.3", {"start": v(7, -36.27) * mm, "end": v(7, -39.73) * mm});
            skLineSegment(sketch, "E126.4", {"start": v(7, -39.73) * mm, "end": v(4, -41.46) * mm});
            skLineSegment(sketch, "E126.5", {"start": v(4, -41.46) * mm, "end": v(1, -39.73) * mm});
            skPoint(sketch, "E126.0.midPoint", {"position": v(1, -38) * mm});
            skCircle(sketch, "E127.cCircle", {"center": v(4, -66) * mm, "radius": 3 * mm, "construction": true});
            skLineSegment(sketch, "E127.0", {"start": v(1, -67.73) * mm, "end": v(1, -64.27) * mm});
            skLineSegment(sketch, "E127.1", {"start": v(1, -64.27) * mm, "end": v(4, -62.54) * mm});
            skLineSegment(sketch, "E127.2", {"start": v(4, -62.54) * mm, "end": v(7, -64.27) * mm});
            skLineSegment(sketch, "E127.3", {"start": v(7, -64.27) * mm, "end": v(7, -67.73) * mm});
            skLineSegment(sketch, "E127.4", {"start": v(7, -67.73) * mm, "end": v(4, -69.46) * mm});
            skLineSegment(sketch, "E127.5", {"start": v(4, -69.46) * mm, "end": v(1, -67.73) * mm});
            skPoint(sketch, "E127.0.midPoint", {"position": v(1, -66) * mm});
            skCircle(sketch, "E128.cCircle", {"center": v(30, -66) * mm, "radius": 3 * mm, "construction": true});
            skLineSegment(sketch, "E128.0", {"start": v(27, -67.73) * mm, "end": v(27, -64.27) * mm});
            skLineSegment(sketch, "E128.1", {"start": v(27, -64.27) * mm, "end": v(30, -62.54) * mm});
            skLineSegment(sketch, "E128.2", {"start": v(30, -62.54) * mm, "end": v(33, -64.27) * mm});
            skLineSegment(sketch, "E128.3", {"start": v(33, -64.27) * mm, "end": v(33, -67.73) * mm});
            skLineSegment(sketch, "E128.4", {"start": v(33, -67.73) * mm, "end": v(30, -69.46) * mm});
            skLineSegment(sketch, "E128.5", {"start": v(30, -69.46) * mm, "end": v(27, -67.73) * mm});
            skPoint(sketch, "E128.0.midPoint", {"position": v(27, -66) * mm});
            skSolve(sketch);
        }
        {
            var Q0;
            Q0=qSketchRegion(id+"F18",true);
            extrude(context, id + "F19", {"entities" : qUnion([Q0]), "operationType" : NewBodyOperationType.REMOVE, "oppositeDirection" : true, "depth" : 3 * mm});
        }
        {
            var Q0;
            Q0=makeQuery(id+"F19.boolean.opBoolean","COPY",EDGE,{"derivedFrom":makeQuery(id+"F19.opExtrude","CAP_EDGE",EDGE,{"disambiguationData":[OSD([sQuery(id+"F18.wireOp",EDGE,"E113.0")])],"isStart":false})});
            var Q1;
            Q1=makeQuery(id+"F19.boolean.opBoolean","INTERSECT",EDGE,{"derivedFrom":[makeQuery(id+"F1.opExtrude","SWEPT_FACE",FACE,{"disambiguationData":[OSD([sQuery(id+"F0.wireOp",EDGE,"E9")])]}),makeQuery(id+"F19.opExtrude","CAP_FACE",FACE,{"disambiguationData":[OSD([sQuery(id+"F18.wireOp",EDGE,"E122.0"),sQuery(id+"F18.wireOp",EDGE,"E122.1"),sQuery(id+"F18.wireOp",EDGE,"E122.2"),sQuery(id+"F18.wireOp",EDGE,"E122.3"),sQuery(id+"F18.wireOp",EDGE,"E122.4"),sQuery(id+"F18.wireOp",EDGE,"E122.5")])],"isStart":false})]});
            var Q2;
            Q2=makeQuery(id+"F19.boolean.opBoolean","INTERSECT",EDGE,{"derivedFrom":[makeQuery(id+"F1.opExtrude","SWEPT_FACE",FACE,{"disambiguationData":[OSD([sQuery(id+"F0.wireOp",EDGE,"E13.MirrorC")])]}),makeQuery(id+"F19.opExtrude","CAP_FACE",FACE,{"disambiguationData":[OSD([sQuery(id+"F18.wireOp",EDGE,"E123.0"),sQuery(id+"F18.wireOp",EDGE,"E123.1"),sQuery(id+"F18.wireOp",EDGE,"E123.2"),sQuery(id+"F18.wireOp",EDGE,"E123.3"),sQuery(id+"F18.wireOp",EDGE,"E123.4"),sQuery(id+"F18.wireOp",EDGE,"E123.5")])],"isStart":false})]});
            var Q3;
            Q3=makeQuery(id+"F19.boolean.opBoolean","INTERSECT",EDGE,{"derivedFrom":[makeQuery(id+"F1.opExtrude","SWEPT_FACE",FACE,{"disambiguationData":[OSD([sQuery(id+"F0.wireOp",EDGE,"E11.MirrorC")])]}),makeQuery(id+"F19.opExtrude","CAP_FACE",FACE,{"disambiguationData":[OSD([sQuery(id+"F18.wireOp",EDGE,"E124.0"),sQuery(id+"F18.wireOp",EDGE,"E124.1"),sQuery(id+"F18.wireOp",EDGE,"E124.2"),sQuery(id+"F18.wireOp",EDGE,"E124.3"),sQuery(id+"F18.wireOp",EDGE,"E124.4"),sQuery(id+"F18.wireOp",EDGE,"E124.5")])],"isStart":false})]});
            var Q4;
            Q4=makeQuery(id+"F19.boolean.opBoolean","INTERSECT",EDGE,{"derivedFrom":[makeQuery(id+"F1.opExtrude","SWEPT_FACE",FACE,{"disambiguationData":[OSD([sQuery(id+"F0.wireOp",EDGE,"E18.MirrorC")])]}),makeQuery(id+"F19.opExtrude","CAP_FACE",FACE,{"disambiguationData":[OSD([sQuery(id+"F18.wireOp",EDGE,"E125.0"),sQuery(id+"F18.wireOp",EDGE,"E125.1"),sQuery(id+"F18.wireOp",EDGE,"E125.2"),sQuery(id+"F18.wireOp",EDGE,"E125.3"),sQuery(id+"F18.wireOp",EDGE,"E125.4"),sQuery(id+"F18.wireOp",EDGE,"E125.5")])],"isStart":false})]});
            var Q5;
            Q5=makeQuery(id+"F19.boolean.opBoolean","INTERSECT",EDGE,{"derivedFrom":[makeQuery(id+"F1.opExtrude","SWEPT_FACE",FACE,{"disambiguationData":[OSD([sQuery(id+"F0.wireOp",EDGE,"E15")])]}),makeQuery(id+"F19.opExtrude","CAP_FACE",FACE,{"disambiguationData":[OSD([sQuery(id+"F18.wireOp",EDGE,"E128.0"),sQuery(id+"F18.wireOp",EDGE,"E128.1"),sQuery(id+"F18.wireOp",EDGE,"E128.2"),sQuery(id+"F18.wireOp",EDGE,"E128.3"),sQuery(id+"F18.wireOp",EDGE,"E128.4"),sQuery(id+"F18.wireOp",EDGE,"E128.5")])],"isStart":false})]});
            var Q6;
            Q6=makeQuery(id+"F19.boolean.opBoolean","INTERSECT",EDGE,{"derivedFrom":[makeQuery(id+"F1.opExtrude","SWEPT_FACE",FACE,{"disambiguationData":[OSD([sQuery(id+"F0.wireOp",EDGE,"E17.MirrorC")])]}),makeQuery(id+"F19.opExtrude","CAP_FACE",FACE,{"disambiguationData":[OSD([sQuery(id+"F18.wireOp",EDGE,"E127.0"),sQuery(id+"F18.wireOp",EDGE,"E127.1"),sQuery(id+"F18.wireOp",EDGE,"E127.2"),sQuery(id+"F18.wireOp",EDGE,"E127.3"),sQuery(id+"F18.wireOp",EDGE,"E127.4"),sQuery(id+"F18.wireOp",EDGE,"E127.5")])],"isStart":false})]});
            var Q7;
            Q7=makeQuery(id+"F19.boolean.opBoolean","INTERSECT",EDGE,{"derivedFrom":[makeQuery(id+"F1.opExtrude","SWEPT_FACE",FACE,{"disambiguationData":[OSD([sQuery(id+"F0.wireOp",EDGE,"E20.MirrorC")])]}),makeQuery(id+"F19.opExtrude","CAP_FACE",FACE,{"disambiguationData":[OSD([sQuery(id+"F18.wireOp",EDGE,"E126.0"),sQuery(id+"F18.wireOp",EDGE,"E126.1"),sQuery(id+"F18.wireOp",EDGE,"E126.2"),sQuery(id+"F18.wireOp",EDGE,"E126.3"),sQuery(id+"F18.wireOp",EDGE,"E126.4"),sQuery(id+"F18.wireOp",EDGE,"E126.5")])],"isStart":false})]});
            chamfer(context, id + "F20", {"entities" : qUnion([Q0, Q1, Q2, Q3, Q4, Q5, Q6, Q7]), "width" : 5 * mm, "tangentPropagation" : true});
        }
        {
            var Q0;
            Q0=qCreatedBy(makeId("Right.planeOp"),FACE);
            var Q1;
            Q1=sQuery(id+"F0.wireOp",VERTEX,"E10");
            cPlane(context, id + "F21", {"entities" : qUnion([Q0, Q1]), "cplaneType" : CPlaneType.PLANE_POINT, "offset" : 150 * mm, "width" : 150 * mm, "height" : 150 * mm});
        }
        {
            var Q0;
            Q0=qCreatedBy(id+"F21.planeOp",FACE);
            var sketch = newSketch(context, id + "F22", { "sketchPlane" : qUnion([Q0])});
            skLineSegment(sketch, "E129", {"start": v(17, 12.16) * mm, "end": v(17, 9.53) * mm, "construction": true});
            skArc(sketch, "E130", {"start": v(17, 26.2) * mm, "mid": v(17.3, 26.12) * mm, "end": v(17.5, 25.9) * mm});
            skArc(sketch, "E131", {"start": v(17.5, 25.9) * mm, "mid": v(17.56, 25.74) * mm, "end": v(17.6, 25.58) * mm});
            skArc(sketch, "E132", {"start": v(17.6, 25.58) * mm, "mid": v(17.64, 25.5) * mm, "end": v(17.73, 25.45) * mm});
            skPoint(sketch, "E133", {"position": v(17, 24.82) * mm});
            skPoint(sketch, "E134", {"position": v(17, 25.45) * mm});
            skPoint(sketch, "E135", {"position": v(17, 25.2) * mm});
            skArc(sketch, "E136", {"start": v(17, 25.2) * mm, "mid": v(17.5, 25.19) * mm, "end": v(18, 25.15) * mm, "construction": true});
            skLineSegment(sketch, "E137", {"start": v(17.96, 24.78) * mm, "end": v(18.03, 25.43) * mm});
            skArc(sketch, "E138", {"start": v(17.73, 25.45) * mm, "mid": v(17.88, 25.44) * mm, "end": v(18.03, 25.43) * mm});
            skArc(sketch, "E139", {"start": v(17, 24.82) * mm, "mid": v(17.48, 24.81) * mm, "end": v(17.96, 24.78) * mm});
            skArc(sketch, "E140.MirrorCS", {"start": v(17, 26.2) * mm, "mid": v(16.7, 26.12) * mm, "end": v(16.5, 25.9) * mm});
            skArc(sketch, "E141.MirrorCS", {"start": v(16.5, 25.9) * mm, "mid": v(16.44, 25.74) * mm, "end": v(16.4, 25.58) * mm});
            skArc(sketch, "E142.MirrorCS", {"start": v(16.4, 25.58) * mm, "mid": v(16.36, 25.5) * mm, "end": v(16.27, 25.45) * mm});
            skArc(sketch, "E143.MirrorCS", {"start": v(16.27, 25.45) * mm, "mid": v(16.12, 25.44) * mm, "end": v(15.97, 25.43) * mm});
            skLineSegment(sketch, "E144.MirrorCS", {"start": v(16.04, 24.78) * mm, "end": v(15.97, 25.43) * mm});
            skArc(sketch, "E145.MirrorCS", {"start": v(17, 24.82) * mm, "mid": v(16.52, 24.81) * mm, "end": v(16.04, 24.78) * mm});
            skArc(sketch, "E146.1.0", {"start": v(14.39, 25.59) * mm, "mid": v(14.36, 25.43) * mm, "end": v(14.36, 25.27) * mm});
            skArc(sketch, "E146.1.1", {"start": v(14.81, 25.99) * mm, "mid": v(14.54, 25.85) * mm, "end": v(14.39, 25.59) * mm});
            skArc(sketch, "E146.1.2", {"start": v(15.08, 24.64) * mm, "mid": v(15.56, 24.72) * mm, "end": v(16.04, 24.78) * mm});
            skPoint(sketch, "E146.1.3", {"position": v(14.96, 25.25) * mm});
            skArc(sketch, "E146.1.4", {"start": v(15.36, 25.78) * mm, "mid": v(15.45, 25.64) * mm, "end": v(15.52, 25.5) * mm});
            skLineSegment(sketch, "E146.1.5", {"start": v(14.15, 24.4) * mm, "end": v(13.96, 25.03) * mm});
            skArc(sketch, "E146.1.6", {"start": v(15.68, 25.4) * mm, "mid": v(15.82, 25.41) * mm, "end": v(15.97, 25.43) * mm});
            skArc(sketch, "E146.1.8", {"start": v(14.81, 25.99) * mm, "mid": v(15.12, 25.96) * mm, "end": v(15.36, 25.78) * mm});
            skPoint(sketch, "E146.1.9", {"position": v(15.08, 24.64) * mm});
            skArc(sketch, "E146.1.10", {"start": v(15.01, 25) * mm, "mid": v(15.5, 25.09) * mm, "end": v(16, 25.15) * mm, "construction": true});
            skArc(sketch, "E146.1.11", {"start": v(15.08, 24.64) * mm, "mid": v(14.61, 24.53) * mm, "end": v(14.15, 24.4) * mm});
            skPoint(sketch, "E146.1.12", {"position": v(15.01, 25) * mm});
            skArc(sketch, "E146.1.13", {"start": v(14.24, 25.11) * mm, "mid": v(14.1, 25.07) * mm, "end": v(13.96, 25.03) * mm});
            skArc(sketch, "E146.1.14", {"start": v(15.52, 25.5) * mm, "mid": v(15.58, 25.42) * mm, "end": v(15.68, 25.4) * mm});
            skArc(sketch, "E146.1.15", {"start": v(14.36, 25.27) * mm, "mid": v(14.33, 25.17) * mm, "end": v(14.24, 25.11) * mm});
            skArc(sketch, "E146.2.0", {"start": v(12.37, 24.87) * mm, "mid": v(12.37, 24.71) * mm, "end": v(12.4, 24.55) * mm});
            skArc(sketch, "E146.2.1", {"start": v(12.71, 25.35) * mm, "mid": v(12.47, 25.16) * mm, "end": v(12.37, 24.87) * mm});
            skArc(sketch, "E146.2.2", {"start": v(13.24, 24.08) * mm, "mid": v(13.7, 24.25) * mm, "end": v(14.15, 24.4) * mm});
            skPoint(sketch, "E146.2.3", {"position": v(13, 24.66) * mm});
            skArc(sketch, "E146.2.4", {"start": v(13.3, 25.25) * mm, "mid": v(13.4, 25.14) * mm, "end": v(13.5, 25) * mm});
            skLineSegment(sketch, "E146.2.5", {"start": v(12.37, 23.66) * mm, "end": v(12.06, 24.24) * mm});
            skArc(sketch, "E146.2.6", {"start": v(13.67, 24.94) * mm, "mid": v(13.82, 24.98) * mm, "end": v(13.96, 25.03) * mm});
            skLineSegment(sketch, "E146.2.7", {"start": v(14.15, 24.4) * mm, "end": v(13.96, 25.03) * mm});
            skArc(sketch, "E146.2.8", {"start": v(12.71, 25.35) * mm, "mid": v(13.02, 25.39) * mm, "end": v(13.3, 25.25) * mm});
            skPoint(sketch, "E146.2.9", {"position": v(13.24, 24.08) * mm});
            skArc(sketch, "E146.2.10", {"start": v(13.1, 24.42) * mm, "mid": v(13.56, 24.6) * mm, "end": v(14.04, 24.76) * mm, "construction": true});
            skArc(sketch, "E146.2.11", {"start": v(13.24, 24.08) * mm, "mid": v(12.8, 23.88) * mm, "end": v(12.37, 23.66) * mm});
            skPoint(sketch, "E146.2.12", {"position": v(13.1, 24.42) * mm});
            skArc(sketch, "E146.2.13", {"start": v(12.33, 24.38) * mm, "mid": v(12.2, 24.31) * mm, "end": v(12.06, 24.24) * mm});
            skArc(sketch, "E146.2.14", {"start": v(13.5, 25) * mm, "mid": v(13.57, 24.94) * mm, "end": v(13.67, 24.94) * mm});
            skArc(sketch, "E146.2.15", {"start": v(12.4, 24.55) * mm, "mid": v(12.4, 24.45) * mm, "end": v(12.33, 24.38) * mm});
            skArc(sketch, "E146.3.0", {"start": v(10.53, 23.78) * mm, "mid": v(10.57, 23.62) * mm, "end": v(10.63, 23.47) * mm});
            skArc(sketch, "E146.3.1", {"start": v(10.78, 24.32) * mm, "mid": v(10.58, 24.08) * mm, "end": v(10.53, 23.78) * mm});
            skArc(sketch, "E146.3.2", {"start": v(11.54, 23.17) * mm, "mid": v(11.95, 23.43) * mm, "end": v(12.37, 23.66) * mm});
            skPoint(sketch, "E146.3.3", {"position": v(11.2, 23.7) * mm});
            skArc(sketch, "E146.3.4", {"start": v(11.36, 24.33) * mm, "mid": v(11.5, 24.24) * mm, "end": v(11.61, 24.13) * mm});
            skLineSegment(sketch, "E146.3.5", {"start": v(10.77, 22.6) * mm, "end": v(10.35, 23.1) * mm});
            skArc(sketch, "E146.3.6", {"start": v(11.8, 24.1) * mm, "mid": v(11.93, 24.17) * mm, "end": v(12.06, 24.24) * mm});
            skLineSegment(sketch, "E146.3.7", {"start": v(12.37, 23.66) * mm, "end": v(12.06, 24.24) * mm});
            skArc(sketch, "E146.3.8", {"start": v(10.78, 24.32) * mm, "mid": v(11.07, 24.4) * mm, "end": v(11.36, 24.33) * mm});
            skPoint(sketch, "E146.3.9", {"position": v(11.54, 23.17) * mm});
            skArc(sketch, "E146.3.10", {"start": v(11.33, 23.48) * mm, "mid": v(11.76, 23.75) * mm, "end": v(12.2, 24) * mm, "construction": true});
            skArc(sketch, "E146.3.11", {"start": v(11.54, 23.17) * mm, "mid": v(11.15, 22.9) * mm, "end": v(10.77, 22.6) * mm});
            skPoint(sketch, "E146.3.12", {"position": v(11.33, 23.48) * mm});
            skArc(sketch, "E146.3.13", {"start": v(10.59, 23.29) * mm, "mid": v(10.47, 23.2) * mm, "end": v(10.35, 23.1) * mm});
            skArc(sketch, "E146.3.14", {"start": v(11.61, 24.13) * mm, "mid": v(11.7, 24.08) * mm, "end": v(11.8, 24.1) * mm});
            skArc(sketch, "E146.3.15", {"start": v(10.63, 23.47) * mm, "mid": v(10.64, 23.37) * mm, "end": v(10.59, 23.29) * mm});
            skArc(sketch, "E146.4.0", {"start": v(8.95, 22.35) * mm, "mid": v(9, 22.2) * mm, "end": v(9.1, 22.07) * mm});
            skArc(sketch, "E146.4.1", {"start": v(9.08, 22.92) * mm, "mid": v(8.93, 22.65) * mm, "end": v(8.95, 22.35) * mm});
            skArc(sketch, "E146.4.2", {"start": v(10.05, 21.95) * mm, "mid": v(10.4, 22.28) * mm, "end": v(10.77, 22.6) * mm});
            skPoint(sketch, "E146.4.3", {"position": v(9.6, 22.4) * mm});
            skArc(sketch, "E146.4.4", {"start": v(9.65, 23.05) * mm, "mid": v(9.8, 23) * mm, "end": v(9.93, 22.9) * mm});
            skLineSegment(sketch, "E146.4.5", {"start": v(9.4, 21.23) * mm, "end": v(8.9, 21.65) * mm});
            skArc(sketch, "E146.4.6", {"start": v(10.12, 22.9) * mm, "mid": v(10.24, 23) * mm, "end": v(10.35, 23.1) * mm});
            skLineSegment(sketch, "E146.4.7", {"start": v(10.77, 22.6) * mm, "end": v(10.35, 23.1) * mm});
            skArc(sketch, "E146.4.8", {"start": v(9.08, 22.92) * mm, "mid": v(9.35, 23.07) * mm, "end": v(9.65, 23.05) * mm});
            skPoint(sketch, "E146.4.9", {"position": v(10.05, 21.95) * mm});
            skArc(sketch, "E146.4.10", {"start": v(9.79, 22.21) * mm, "mid": v(10.15, 22.56) * mm, "end": v(10.53, 22.88) * mm, "construction": true});
            skArc(sketch, "E146.4.11", {"start": v(10.05, 21.95) * mm, "mid": v(9.72, 21.6) * mm, "end": v(9.4, 21.23) * mm});
            skPoint(sketch, "E146.4.12", {"position": v(9.79, 22.21) * mm});
            skArc(sketch, "E146.4.13", {"start": v(9.1, 21.88) * mm, "mid": v(9, 21.76) * mm, "end": v(8.9, 21.65) * mm});
            skArc(sketch, "E146.4.14", {"start": v(9.93, 22.9) * mm, "mid": v(10.03, 22.87) * mm, "end": v(10.12, 22.9) * mm});
            skArc(sketch, "E146.4.15", {"start": v(9.1, 22.07) * mm, "mid": v(9.13, 21.97) * mm, "end": v(9.1, 21.88) * mm});
            skArc(sketch, "E146.5.0", {"start": v(7.67, 20.64) * mm, "mid": v(7.76, 20.5) * mm, "end": v(7.87, 20.39) * mm});
            skArc(sketch, "E146.5.1", {"start": v(7.68, 21.22) * mm, "mid": v(7.6, 20.93) * mm, "end": v(7.67, 20.64) * mm});
            skArc(sketch, "E146.5.2", {"start": v(8.83, 20.46) * mm, "mid": v(9.1, 20.85) * mm, "end": v(9.4, 21.23) * mm});
            skPoint(sketch, "E146.5.3", {"position": v(8.3, 20.8) * mm});
            skArc(sketch, "E146.5.4", {"start": v(8.22, 21.47) * mm, "mid": v(8.38, 21.43) * mm, "end": v(8.53, 21.37) * mm});
            skLineSegment(sketch, "E146.5.5", {"start": v(8.34, 19.63) * mm, "end": v(7.76, 19.94) * mm});
            skArc(sketch, "E146.5.6", {"start": v(8.71, 21.41) * mm, "mid": v(8.8, 21.53) * mm, "end": v(8.9, 21.65) * mm});
            skLineSegment(sketch, "E146.5.7", {"start": v(9.4, 21.23) * mm, "end": v(8.9, 21.65) * mm});
            skArc(sketch, "E146.5.8", {"start": v(7.68, 21.22) * mm, "mid": v(7.92, 21.42) * mm, "end": v(8.22, 21.47) * mm});
            skPoint(sketch, "E146.5.9", {"position": v(8.83, 20.46) * mm});
            skArc(sketch, "E146.5.10", {"start": v(8.52, 20.67) * mm, "mid": v(8.8, 21.08) * mm, "end": v(9.12, 21.47) * mm, "construction": true});
            skArc(sketch, "E146.5.11", {"start": v(8.83, 20.46) * mm, "mid": v(8.57, 20.05) * mm, "end": v(8.34, 19.63) * mm});
            skPoint(sketch, "E146.5.12", {"position": v(8.52, 20.67) * mm});
            skArc(sketch, "E146.5.13", {"start": v(7.9, 20.2) * mm, "mid": v(7.83, 20.07) * mm, "end": v(7.76, 19.94) * mm});
            skArc(sketch, "E146.5.14", {"start": v(8.53, 21.37) * mm, "mid": v(8.63, 21.36) * mm, "end": v(8.71, 21.41) * mm});
            skArc(sketch, "E146.5.15", {"start": v(7.87, 20.39) * mm, "mid": v(7.92, 20.3) * mm, "end": v(7.9, 20.2) * mm});
            skArc(sketch, "E146.6.0", {"start": v(6.75, 18.7) * mm, "mid": v(6.86, 18.6) * mm, "end": v(7, 18.5) * mm});
            skArc(sketch, "E146.6.1", {"start": v(6.65, 19.29) * mm, "mid": v(6.61, 18.98) * mm, "end": v(6.75, 18.7) * mm});
            skArc(sketch, "E146.6.2", {"start": v(7.92, 18.76) * mm, "mid": v(8.12, 19.2) * mm, "end": v(8.34, 19.63) * mm});
            skPoint(sketch, "E146.6.3", {"position": v(7.34, 19) * mm});
            skArc(sketch, "E146.6.4", {"start": v(7.13, 19.63) * mm, "mid": v(7.29, 19.63) * mm, "end": v(7.45, 19.6) * mm});
            skLineSegment(sketch, "E146.6.5", {"start": v(7.6, 17.85) * mm, "end": v(6.97, 18.04) * mm});
            skArc(sketch, "E146.6.6", {"start": v(7.62, 19.67) * mm, "mid": v(7.69, 19.8) * mm, "end": v(7.76, 19.94) * mm});
            skLineSegment(sketch, "E146.6.7", {"start": v(8.34, 19.63) * mm, "end": v(7.76, 19.94) * mm});
            skArc(sketch, "E146.6.8", {"start": v(6.65, 19.29) * mm, "mid": v(6.84, 19.53) * mm, "end": v(7.13, 19.63) * mm});
            skPoint(sketch, "E146.6.9", {"position": v(7.92, 18.76) * mm});
            skArc(sketch, "E146.6.10", {"start": v(7.58, 18.9) * mm, "mid": v(7.78, 19.36) * mm, "end": v(8, 19.8) * mm, "construction": true});
            skArc(sketch, "E146.6.11", {"start": v(7.92, 18.76) * mm, "mid": v(7.75, 18.3) * mm, "end": v(7.6, 17.85) * mm});
            skPoint(sketch, "E146.6.12", {"position": v(7.58, 18.9) * mm});
            skArc(sketch, "E146.6.13", {"start": v(7.06, 18.33) * mm, "mid": v(7.02, 18.18) * mm, "end": v(6.97, 18.04) * mm});
            skArc(sketch, "E146.6.14", {"start": v(7.45, 19.6) * mm, "mid": v(7.55, 19.6) * mm, "end": v(7.62, 19.67) * mm});
            skArc(sketch, "E146.6.15", {"start": v(7, 18.5) * mm, "mid": v(7.06, 18.43) * mm, "end": v(7.06, 18.33) * mm});
            skArc(sketch, "E146.7.0", {"start": v(6.22, 16.64) * mm, "mid": v(6.36, 16.55) * mm, "end": v(6.5, 16.48) * mm});
            skArc(sketch, "E146.7.1", {"start": v(6.01, 17.19) * mm, "mid": v(6.04, 16.88) * mm, "end": v(6.22, 16.64) * mm});
            skArc(sketch, "E146.7.2", {"start": v(7.36, 16.92) * mm, "mid": v(7.47, 17.39) * mm, "end": v(7.6, 17.85) * mm});
            skPoint(sketch, "E146.7.3", {"position": v(6.75, 17.04) * mm});
            skArc(sketch, "E146.7.4", {"start": v(6.41, 17.61) * mm, "mid": v(6.57, 17.64) * mm, "end": v(6.73, 17.64) * mm});
            skLineSegment(sketch, "E146.7.5", {"start": v(7.22, 15.96) * mm, "end": v(6.57, 16.03) * mm});
            skArc(sketch, "E146.7.6", {"start": v(6.89, 17.76) * mm, "mid": v(6.93, 17.9) * mm, "end": v(6.97, 18.04) * mm});
            skLineSegment(sketch, "E146.7.7", {"start": v(7.6, 17.85) * mm, "end": v(6.97, 18.04) * mm});
            skArc(sketch, "E146.7.8", {"start": v(6.01, 17.19) * mm, "mid": v(6.15, 17.46) * mm, "end": v(6.41, 17.61) * mm});
            skPoint(sketch, "E146.7.9", {"position": v(7.36, 16.92) * mm});
            skArc(sketch, "E146.7.10", {"start": v(7, 16.99) * mm, "mid": v(7.1, 17.48) * mm, "end": v(7.24, 17.96) * mm, "construction": true});
            skArc(sketch, "E146.7.11", {"start": v(7.36, 16.92) * mm, "mid": v(7.28, 16.44) * mm, "end": v(7.22, 15.96) * mm});
            skPoint(sketch, "E146.7.12", {"position": v(7, 16.99) * mm});
            skArc(sketch, "E146.7.13", {"start": v(6.6, 16.32) * mm, "mid": v(6.59, 16.18) * mm, "end": v(6.57, 16.03) * mm});
            skArc(sketch, "E146.7.14", {"start": v(6.73, 17.64) * mm, "mid": v(6.83, 17.67) * mm, "end": v(6.89, 17.76) * mm});
            skArc(sketch, "E146.7.15", {"start": v(6.5, 16.48) * mm, "mid": v(6.58, 16.42) * mm, "end": v(6.6, 16.32) * mm});
            skArc(sketch, "E146.8.0", {"start": v(6.1, 14.5) * mm, "mid": v(6.26, 14.44) * mm, "end": v(6.42, 14.4) * mm});
            skArc(sketch, "E146.8.1", {"start": v(5.8, 15) * mm, "mid": v(5.88, 14.7) * mm, "end": v(6.1, 14.5) * mm});
            skArc(sketch, "E146.8.2", {"start": v(7.18, 15) * mm, "mid": v(7.19, 15.48) * mm, "end": v(7.22, 15.96) * mm});
            skPoint(sketch, "E146.8.3", {"position": v(6.55, 15) * mm});
            skArc(sketch, "E146.8.4", {"start": v(6.1, 15.5) * mm, "mid": v(6.26, 15.56) * mm, "end": v(6.42, 15.6) * mm});
            skLineSegment(sketch, "E146.8.5", {"start": v(7.22, 14.04) * mm, "end": v(6.57, 13.97) * mm});
            skArc(sketch, "E146.8.6", {"start": v(6.55, 15.73) * mm, "mid": v(6.56, 15.88) * mm, "end": v(6.57, 16.03) * mm});
            skLineSegment(sketch, "E146.8.7", {"start": v(7.22, 15.96) * mm, "end": v(6.57, 16.03) * mm});
            skArc(sketch, "E146.8.8", {"start": v(5.8, 15) * mm, "mid": v(5.88, 15.3) * mm, "end": v(6.1, 15.5) * mm});
            skPoint(sketch, "E146.8.9", {"position": v(7.18, 15) * mm});
            skArc(sketch, "E146.8.10", {"start": v(6.8, 15) * mm, "mid": v(6.81, 15.5) * mm, "end": v(6.85, 16) * mm, "construction": true});
            skArc(sketch, "E146.8.11", {"start": v(7.18, 15) * mm, "mid": v(7.19, 14.52) * mm, "end": v(7.22, 14.04) * mm});
            skPoint(sketch, "E146.8.12", {"position": v(6.8, 15) * mm});
            skArc(sketch, "E146.8.13", {"start": v(6.55, 14.27) * mm, "mid": v(6.56, 14.12) * mm, "end": v(6.57, 13.97) * mm});
            skArc(sketch, "E146.8.14", {"start": v(6.42, 15.6) * mm, "mid": v(6.5, 15.64) * mm, "end": v(6.55, 15.73) * mm});
            skArc(sketch, "E146.8.15", {"start": v(6.42, 14.4) * mm, "mid": v(6.5, 14.36) * mm, "end": v(6.55, 14.27) * mm});
            skArc(sketch, "E146.9.0", {"start": v(6.41, 12.39) * mm, "mid": v(6.57, 12.36) * mm, "end": v(6.73, 12.36) * mm});
            skArc(sketch, "E146.9.1", {"start": v(6.01, 12.81) * mm, "mid": v(6.15, 12.54) * mm, "end": v(6.41, 12.39) * mm});
            skArc(sketch, "E146.9.2", {"start": v(7.36, 13.08) * mm, "mid": v(7.28, 13.56) * mm, "end": v(7.22, 14.04) * mm});
            skPoint(sketch, "E146.9.3", {"position": v(6.75, 12.96) * mm});
            skArc(sketch, "E146.9.4", {"start": v(6.22, 13.36) * mm, "mid": v(6.36, 13.45) * mm, "end": v(6.5, 13.52) * mm});
            skLineSegment(sketch, "E146.9.5", {"start": v(7.6, 12.15) * mm, "end": v(6.97, 11.96) * mm});
            skArc(sketch, "E146.9.6", {"start": v(6.6, 13.68) * mm, "mid": v(6.59, 13.82) * mm, "end": v(6.57, 13.97) * mm});
            skLineSegment(sketch, "E146.9.7", {"start": v(7.22, 14.04) * mm, "end": v(6.57, 13.97) * mm});
            skArc(sketch, "E146.9.8", {"start": v(6.01, 12.81) * mm, "mid": v(6.04, 13.12) * mm, "end": v(6.22, 13.36) * mm});
            skPoint(sketch, "E146.9.9", {"position": v(7.36, 13.08) * mm});
            skArc(sketch, "E146.9.10", {"start": v(7, 13.01) * mm, "mid": v(6.91, 13.5) * mm, "end": v(6.85, 14) * mm, "construction": true});
            skArc(sketch, "E146.9.11", {"start": v(7.36, 13.08) * mm, "mid": v(7.47, 12.61) * mm, "end": v(7.6, 12.15) * mm});
            skPoint(sketch, "E146.9.12", {"position": v(7, 13.01) * mm});
            skArc(sketch, "E146.9.13", {"start": v(6.89, 12.24) * mm, "mid": v(6.93, 12.1) * mm, "end": v(6.97, 11.96) * mm});
            skArc(sketch, "E146.9.14", {"start": v(6.5, 13.52) * mm, "mid": v(6.58, 13.58) * mm, "end": v(6.6, 13.68) * mm});
            skArc(sketch, "E146.9.15", {"start": v(6.73, 12.36) * mm, "mid": v(6.83, 12.33) * mm, "end": v(6.89, 12.24) * mm});
            skArc(sketch, "E146.10.0", {"start": v(7.13, 10.37) * mm, "mid": v(7.29, 10.37) * mm, "end": v(7.45, 10.4) * mm});
            skArc(sketch, "E146.10.1", {"start": v(6.65, 10.71) * mm, "mid": v(6.84, 10.47) * mm, "end": v(7.13, 10.37) * mm});
            skArc(sketch, "E146.10.2", {"start": v(7.92, 11.24) * mm, "mid": v(7.75, 11.7) * mm, "end": v(7.6, 12.15) * mm});
            skPoint(sketch, "E146.10.3", {"position": v(7.34, 11) * mm});
            skArc(sketch, "E146.10.4", {"start": v(6.75, 11.3) * mm, "mid": v(6.86, 11.4) * mm, "end": v(7, 11.5) * mm});
            skLineSegment(sketch, "E146.10.5", {"start": v(8.34, 10.37) * mm, "end": v(7.76, 10.06) * mm});
            skArc(sketch, "E146.10.6", {"start": v(7.06, 11.67) * mm, "mid": v(7.02, 11.82) * mm, "end": v(6.97, 11.96) * mm});
            skLineSegment(sketch, "E146.10.7", {"start": v(7.6, 12.15) * mm, "end": v(6.97, 11.96) * mm});
            skArc(sketch, "E146.10.8", {"start": v(6.65, 10.71) * mm, "mid": v(6.61, 11.02) * mm, "end": v(6.75, 11.3) * mm});
            skPoint(sketch, "E146.10.9", {"position": v(7.92, 11.24) * mm});
            skArc(sketch, "E146.10.10", {"start": v(7.58, 11.1) * mm, "mid": v(7.4, 11.56) * mm, "end": v(7.24, 12.04) * mm, "construction": true});
            skArc(sketch, "E146.10.11", {"start": v(7.92, 11.24) * mm, "mid": v(8.12, 10.8) * mm, "end": v(8.34, 10.37) * mm});
            skPoint(sketch, "E146.10.12", {"position": v(7.58, 11.1) * mm});
            skArc(sketch, "E146.10.13", {"start": v(7.62, 10.33) * mm, "mid": v(7.69, 10.2) * mm, "end": v(7.76, 10.06) * mm});
            skArc(sketch, "E146.10.14", {"start": v(7, 11.5) * mm, "mid": v(7.06, 11.57) * mm, "end": v(7.06, 11.67) * mm});
            skArc(sketch, "E146.10.15", {"start": v(7.45, 10.4) * mm, "mid": v(7.55, 10.4) * mm, "end": v(7.62, 10.33) * mm});
            skArc(sketch, "E146.11.0", {"start": v(8.22, 8.53) * mm, "mid": v(8.38, 8.57) * mm, "end": v(8.53, 8.63) * mm});
            skArc(sketch, "E146.11.1", {"start": v(7.68, 8.78) * mm, "mid": v(7.92, 8.58) * mm, "end": v(8.22, 8.53) * mm});
            skArc(sketch, "E146.11.2", {"start": v(8.83, 9.54) * mm, "mid": v(8.57, 9.95) * mm, "end": v(8.34, 10.37) * mm});
            skPoint(sketch, "E146.11.3", {"position": v(8.3, 9.2) * mm});
            skArc(sketch, "E146.11.4", {"start": v(7.67, 9.36) * mm, "mid": v(7.76, 9.5) * mm, "end": v(7.87, 9.61) * mm});
            skLineSegment(sketch, "E146.11.5", {"start": v(9.4, 8.77) * mm, "end": v(8.9, 8.35) * mm});
            skArc(sketch, "E146.11.6", {"start": v(7.9, 9.8) * mm, "mid": v(7.83, 9.93) * mm, "end": v(7.76, 10.06) * mm});
            skLineSegment(sketch, "E146.11.7", {"start": v(8.34, 10.37) * mm, "end": v(7.76, 10.06) * mm});
            skArc(sketch, "E146.11.8", {"start": v(7.68, 8.78) * mm, "mid": v(7.6, 9.07) * mm, "end": v(7.67, 9.36) * mm});
            skPoint(sketch, "E146.11.9", {"position": v(8.83, 9.54) * mm});
            skArc(sketch, "E146.11.10", {"start": v(8.52, 9.33) * mm, "mid": v(8.25, 9.76) * mm, "end": v(8, 10.2) * mm, "construction": true});
            skArc(sketch, "E146.11.11", {"start": v(8.83, 9.54) * mm, "mid": v(9.1, 9.15) * mm, "end": v(9.4, 8.77) * mm});
            skPoint(sketch, "E146.11.12", {"position": v(8.52, 9.33) * mm});
            skArc(sketch, "E146.11.13", {"start": v(8.71, 8.59) * mm, "mid": v(8.8, 8.47) * mm, "end": v(8.9, 8.35) * mm});
            skArc(sketch, "E146.11.14", {"start": v(7.87, 9.61) * mm, "mid": v(7.92, 9.7) * mm, "end": v(7.9, 9.8) * mm});
            skArc(sketch, "E146.11.15", {"start": v(8.53, 8.63) * mm, "mid": v(8.63, 8.64) * mm, "end": v(8.71, 8.59) * mm});
            skArc(sketch, "E146.12.0", {"start": v(9.65, 6.95) * mm, "mid": v(9.8, 7) * mm, "end": v(9.93, 7.1) * mm});
            skArc(sketch, "E146.12.1", {"start": v(9.08, 7.08) * mm, "mid": v(9.35, 6.93) * mm, "end": v(9.65, 6.95) * mm});
            skArc(sketch, "E146.12.2", {"start": v(10.05, 8.05) * mm, "mid": v(9.72, 8.4) * mm, "end": v(9.4, 8.77) * mm});
            skPoint(sketch, "E146.12.3", {"position": v(9.6, 7.6) * mm});
            skArc(sketch, "E146.12.4", {"start": v(8.95, 7.65) * mm, "mid": v(9, 7.8) * mm, "end": v(9.1, 7.93) * mm});
            skLineSegment(sketch, "E146.12.5", {"start": v(10.77, 7.4) * mm, "end": v(10.35, 6.9) * mm});
            skArc(sketch, "E146.12.6", {"start": v(9.1, 8.12) * mm, "mid": v(9, 8.24) * mm, "end": v(8.9, 8.35) * mm});
            skLineSegment(sketch, "E146.12.7", {"start": v(9.4, 8.77) * mm, "end": v(8.9, 8.35) * mm});
            skArc(sketch, "E146.12.8", {"start": v(9.08, 7.08) * mm, "mid": v(8.93, 7.35) * mm, "end": v(8.95, 7.65) * mm});
            skPoint(sketch, "E146.12.9", {"position": v(10.05, 8.05) * mm});
            skArc(sketch, "E146.12.10", {"start": v(9.79, 7.79) * mm, "mid": v(9.44, 8.15) * mm, "end": v(9.12, 8.53) * mm, "construction": true});
            skArc(sketch, "E146.12.11", {"start": v(10.05, 8.05) * mm, "mid": v(10.4, 7.72) * mm, "end": v(10.77, 7.4) * mm});
            skPoint(sketch, "E146.12.12", {"position": v(9.79, 7.79) * mm});
            skArc(sketch, "E146.12.13", {"start": v(10.12, 7.1) * mm, "mid": v(10.24, 7) * mm, "end": v(10.35, 6.9) * mm});
            skArc(sketch, "E146.12.14", {"start": v(9.1, 7.93) * mm, "mid": v(9.13, 8.03) * mm, "end": v(9.1, 8.12) * mm});
            skArc(sketch, "E146.12.15", {"start": v(9.93, 7.1) * mm, "mid": v(10.03, 7.13) * mm, "end": v(10.12, 7.1) * mm});
            skArc(sketch, "E146.13.0", {"start": v(11.36, 5.67) * mm, "mid": v(11.5, 5.76) * mm, "end": v(11.61, 5.87) * mm});
            skArc(sketch, "E146.13.1", {"start": v(10.78, 5.68) * mm, "mid": v(11.07, 5.6) * mm, "end": v(11.36, 5.67) * mm});
            skArc(sketch, "E146.13.2", {"start": v(11.54, 6.83) * mm, "mid": v(11.15, 7.1) * mm, "end": v(10.77, 7.4) * mm});
            skPoint(sketch, "E146.13.3", {"position": v(11.2, 6.3) * mm});
            skArc(sketch, "E146.13.4", {"start": v(10.53, 6.22) * mm, "mid": v(10.57, 6.38) * mm, "end": v(10.63, 6.53) * mm});
            skLineSegment(sketch, "E146.13.5", {"start": v(12.37, 6.34) * mm, "end": v(12.06, 5.76) * mm});
            skArc(sketch, "E146.13.6", {"start": v(10.59, 6.71) * mm, "mid": v(10.47, 6.8) * mm, "end": v(10.35, 6.9) * mm});
            skLineSegment(sketch, "E146.13.7", {"start": v(10.77, 7.4) * mm, "end": v(10.35, 6.9) * mm});
            skArc(sketch, "E146.13.8", {"start": v(10.78, 5.68) * mm, "mid": v(10.58, 5.92) * mm, "end": v(10.53, 6.22) * mm});
            skPoint(sketch, "E146.13.9", {"position": v(11.54, 6.83) * mm});
            skArc(sketch, "E146.13.10", {"start": v(11.33, 6.52) * mm, "mid": v(10.92, 6.8) * mm, "end": v(10.53, 7.12) * mm, "construction": true});
            skArc(sketch, "E146.13.11", {"start": v(11.54, 6.83) * mm, "mid": v(11.95, 6.57) * mm, "end": v(12.37, 6.34) * mm});
            skPoint(sketch, "E146.13.12", {"position": v(11.33, 6.52) * mm});
            skArc(sketch, "E146.13.13", {"start": v(11.8, 5.9) * mm, "mid": v(11.93, 5.83) * mm, "end": v(12.06, 5.76) * mm});
            skArc(sketch, "E146.13.14", {"start": v(10.63, 6.53) * mm, "mid": v(10.64, 6.63) * mm, "end": v(10.59, 6.71) * mm});
            skArc(sketch, "E146.13.15", {"start": v(11.61, 5.87) * mm, "mid": v(11.7, 5.92) * mm, "end": v(11.8, 5.9) * mm});
            skArc(sketch, "E146.14.0", {"start": v(13.3, 4.75) * mm, "mid": v(13.4, 4.86) * mm, "end": v(13.5, 5) * mm});
            skArc(sketch, "E146.14.1", {"start": v(12.71, 4.65) * mm, "mid": v(13.02, 4.61) * mm, "end": v(13.3, 4.75) * mm});
            skArc(sketch, "E146.14.2", {"start": v(13.24, 5.92) * mm, "mid": v(12.8, 6.12) * mm, "end": v(12.37, 6.34) * mm});
            skPoint(sketch, "E146.14.3", {"position": v(13, 5.34) * mm});
            skArc(sketch, "E146.14.4", {"start": v(12.37, 5.13) * mm, "mid": v(12.37, 5.29) * mm, "end": v(12.4, 5.45) * mm});
            skLineSegment(sketch, "E146.14.5", {"start": v(14.15, 5.6) * mm, "end": v(13.96, 4.97) * mm});
            skArc(sketch, "E146.14.6", {"start": v(12.33, 5.62) * mm, "mid": v(12.2, 5.69) * mm, "end": v(12.06, 5.76) * mm});
            skLineSegment(sketch, "E146.14.7", {"start": v(12.37, 6.34) * mm, "end": v(12.06, 5.76) * mm});
            skArc(sketch, "E146.14.8", {"start": v(12.71, 4.65) * mm, "mid": v(12.47, 4.84) * mm, "end": v(12.37, 5.13) * mm});
            skPoint(sketch, "E146.14.9", {"position": v(13.24, 5.92) * mm});
            skArc(sketch, "E146.14.10", {"start": v(13.1, 5.58) * mm, "mid": v(12.64, 5.78) * mm, "end": v(12.2, 6) * mm, "construction": true});
            skArc(sketch, "E146.14.11", {"start": v(13.24, 5.92) * mm, "mid": v(13.7, 5.75) * mm, "end": v(14.15, 5.6) * mm});
            skPoint(sketch, "E146.14.12", {"position": v(13.1, 5.58) * mm});
            skArc(sketch, "E146.14.13", {"start": v(13.67, 5.06) * mm, "mid": v(13.82, 5.02) * mm, "end": v(13.96, 4.97) * mm});
            skArc(sketch, "E146.14.14", {"start": v(12.4, 5.45) * mm, "mid": v(12.4, 5.55) * mm, "end": v(12.33, 5.62) * mm});
            skArc(sketch, "E146.14.15", {"start": v(13.5, 5) * mm, "mid": v(13.57, 5.06) * mm, "end": v(13.67, 5.06) * mm});
            skArc(sketch, "E146.15.0", {"start": v(15.36, 4.22) * mm, "mid": v(15.45, 4.36) * mm, "end": v(15.52, 4.5) * mm});
            skArc(sketch, "E146.15.1", {"start": v(14.81, 4.01) * mm, "mid": v(15.12, 4.04) * mm, "end": v(15.36, 4.22) * mm});
            skArc(sketch, "E146.15.2", {"start": v(15.08, 5.36) * mm, "mid": v(14.61, 5.47) * mm, "end": v(14.15, 5.6) * mm});
            skPoint(sketch, "E146.15.3", {"position": v(14.96, 4.75) * mm});
            skArc(sketch, "E146.15.4", {"start": v(14.39, 4.41) * mm, "mid": v(14.36, 4.57) * mm, "end": v(14.36, 4.73) * mm});
            skLineSegment(sketch, "E146.15.5", {"start": v(16.04, 5.22) * mm, "end": v(15.97, 4.57) * mm});
            skArc(sketch, "E146.15.6", {"start": v(14.24, 4.89) * mm, "mid": v(14.1, 4.93) * mm, "end": v(13.96, 4.97) * mm});
            skLineSegment(sketch, "E146.15.7", {"start": v(14.15, 5.6) * mm, "end": v(13.96, 4.97) * mm});
            skArc(sketch, "E146.15.8", {"start": v(14.81, 4.01) * mm, "mid": v(14.54, 4.15) * mm, "end": v(14.39, 4.41) * mm});
            skPoint(sketch, "E146.15.9", {"position": v(15.08, 5.36) * mm});
            skArc(sketch, "E146.15.10", {"start": v(15.01, 5) * mm, "mid": v(14.52, 5.1) * mm, "end": v(14.04, 5.24) * mm, "construction": true});
            skArc(sketch, "E146.15.11", {"start": v(15.08, 5.36) * mm, "mid": v(15.56, 5.28) * mm, "end": v(16.04, 5.22) * mm});
            skPoint(sketch, "E146.15.12", {"position": v(15.01, 5) * mm});
            skArc(sketch, "E146.15.13", {"start": v(15.68, 4.6) * mm, "mid": v(15.82, 4.59) * mm, "end": v(15.97, 4.57) * mm});
            skArc(sketch, "E146.15.14", {"start": v(14.36, 4.73) * mm, "mid": v(14.33, 4.83) * mm, "end": v(14.24, 4.89) * mm});
            skArc(sketch, "E146.15.15", {"start": v(15.52, 4.5) * mm, "mid": v(15.58, 4.58) * mm, "end": v(15.68, 4.6) * mm});
            skArc(sketch, "E146.16.0", {"start": v(17.5, 4.1) * mm, "mid": v(17.56, 4.26) * mm, "end": v(17.6, 4.42) * mm});
            skArc(sketch, "E146.16.1", {"start": v(17, 3.8) * mm, "mid": v(17.3, 3.88) * mm, "end": v(17.5, 4.1) * mm});
            skArc(sketch, "E146.16.2", {"start": v(17, 5.18) * mm, "mid": v(16.52, 5.19) * mm, "end": v(16.04, 5.22) * mm});
            skPoint(sketch, "E146.16.3", {"position": v(17, 4.55) * mm});
            skArc(sketch, "E146.16.4", {"start": v(16.5, 4.1) * mm, "mid": v(16.44, 4.26) * mm, "end": v(16.4, 4.42) * mm});
            skLineSegment(sketch, "E146.16.5", {"start": v(17.96, 5.22) * mm, "end": v(18.03, 4.57) * mm});
            skArc(sketch, "E146.16.6", {"start": v(16.27, 4.55) * mm, "mid": v(16.12, 4.56) * mm, "end": v(15.97, 4.57) * mm});
            skLineSegment(sketch, "E146.16.7", {"start": v(16.04, 5.22) * mm, "end": v(15.97, 4.57) * mm});
            skArc(sketch, "E146.16.8", {"start": v(17, 3.8) * mm, "mid": v(16.7, 3.88) * mm, "end": v(16.5, 4.1) * mm});
            skPoint(sketch, "E146.16.9", {"position": v(17, 5.18) * mm});
            skArc(sketch, "E146.16.10", {"start": v(17, 4.8) * mm, "mid": v(16.5, 4.81) * mm, "end": v(16, 4.85) * mm, "construction": true});
            skArc(sketch, "E146.16.11", {"start": v(17, 5.18) * mm, "mid": v(17.48, 5.19) * mm, "end": v(17.96, 5.22) * mm});
            skPoint(sketch, "E146.16.12", {"position": v(17, 4.8) * mm});
            skArc(sketch, "E146.16.13", {"start": v(17.73, 4.55) * mm, "mid": v(17.88, 4.56) * mm, "end": v(18.03, 4.57) * mm});
            skArc(sketch, "E146.16.14", {"start": v(16.4, 4.42) * mm, "mid": v(16.36, 4.5) * mm, "end": v(16.27, 4.55) * mm});
            skArc(sketch, "E146.16.15", {"start": v(17.6, 4.42) * mm, "mid": v(17.64, 4.5) * mm, "end": v(17.73, 4.55) * mm});
            skArc(sketch, "E146.17.0", {"start": v(19.61, 4.41) * mm, "mid": v(19.64, 4.57) * mm, "end": v(19.64, 4.73) * mm});
            skArc(sketch, "E146.17.1", {"start": v(19.19, 4.01) * mm, "mid": v(19.46, 4.15) * mm, "end": v(19.61, 4.41) * mm});
            skArc(sketch, "E146.17.2", {"start": v(18.92, 5.36) * mm, "mid": v(18.44, 5.28) * mm, "end": v(17.96, 5.22) * mm});
            skPoint(sketch, "E146.17.3", {"position": v(19.04, 4.75) * mm});
            skArc(sketch, "E146.17.4", {"start": v(18.64, 4.22) * mm, "mid": v(18.55, 4.36) * mm, "end": v(18.48, 4.5) * mm});
            skLineSegment(sketch, "E146.17.5", {"start": v(19.85, 5.6) * mm, "end": v(20.04, 4.97) * mm});
            skArc(sketch, "E146.17.6", {"start": v(18.32, 4.6) * mm, "mid": v(18.18, 4.59) * mm, "end": v(18.03, 4.57) * mm});
            skLineSegment(sketch, "E146.17.7", {"start": v(17.96, 5.22) * mm, "end": v(18.03, 4.57) * mm});
            skArc(sketch, "E146.17.8", {"start": v(19.19, 4.01) * mm, "mid": v(18.88, 4.04) * mm, "end": v(18.64, 4.22) * mm});
            skPoint(sketch, "E146.17.9", {"position": v(18.92, 5.36) * mm});
            skArc(sketch, "E146.17.10", {"start": v(18.99, 5) * mm, "mid": v(18.5, 4.91) * mm, "end": v(18, 4.85) * mm, "construction": true});
            skArc(sketch, "E146.17.11", {"start": v(18.92, 5.36) * mm, "mid": v(19.39, 5.47) * mm, "end": v(19.85, 5.6) * mm});
            skPoint(sketch, "E146.17.12", {"position": v(18.99, 5) * mm});
            skArc(sketch, "E146.17.13", {"start": v(19.76, 4.89) * mm, "mid": v(19.9, 4.93) * mm, "end": v(20.04, 4.97) * mm});
            skArc(sketch, "E146.17.14", {"start": v(18.48, 4.5) * mm, "mid": v(18.42, 4.58) * mm, "end": v(18.32, 4.6) * mm});
            skArc(sketch, "E146.17.15", {"start": v(19.64, 4.73) * mm, "mid": v(19.67, 4.83) * mm, "end": v(19.76, 4.89) * mm});
            skArc(sketch, "E146.18.0", {"start": v(21.63, 5.13) * mm, "mid": v(21.63, 5.29) * mm, "end": v(21.6, 5.45) * mm});
            skArc(sketch, "E146.18.1", {"start": v(21.29, 4.65) * mm, "mid": v(21.53, 4.84) * mm, "end": v(21.63, 5.13) * mm});
            skArc(sketch, "E146.18.2", {"start": v(20.76, 5.92) * mm, "mid": v(20.3, 5.75) * mm, "end": v(19.85, 5.6) * mm});
            skPoint(sketch, "E146.18.3", {"position": v(21, 5.34) * mm});
            skArc(sketch, "E146.18.4", {"start": v(20.7, 4.75) * mm, "mid": v(20.6, 4.86) * mm, "end": v(20.5, 5) * mm});
            skLineSegment(sketch, "E146.18.5", {"start": v(21.63, 6.34) * mm, "end": v(21.94, 5.76) * mm});
            skArc(sketch, "E146.18.6", {"start": v(20.33, 5.06) * mm, "mid": v(20.18, 5.02) * mm, "end": v(20.04, 4.97) * mm});
            skLineSegment(sketch, "E146.18.7", {"start": v(19.85, 5.6) * mm, "end": v(20.04, 4.97) * mm});
            skArc(sketch, "E146.18.8", {"start": v(21.29, 4.65) * mm, "mid": v(20.98, 4.61) * mm, "end": v(20.7, 4.75) * mm});
            skPoint(sketch, "E146.18.9", {"position": v(20.76, 5.92) * mm});
            skArc(sketch, "E146.18.10", {"start": v(20.9, 5.58) * mm, "mid": v(20.44, 5.4) * mm, "end": v(19.96, 5.24) * mm, "construction": true});
            skArc(sketch, "E146.18.11", {"start": v(20.76, 5.92) * mm, "mid": v(21.2, 6.12) * mm, "end": v(21.63, 6.34) * mm});
            skPoint(sketch, "E146.18.12", {"position": v(20.9, 5.58) * mm});
            skArc(sketch, "E146.18.13", {"start": v(21.67, 5.62) * mm, "mid": v(21.8, 5.69) * mm, "end": v(21.94, 5.76) * mm});
            skArc(sketch, "E146.18.14", {"start": v(20.5, 5) * mm, "mid": v(20.43, 5.06) * mm, "end": v(20.33, 5.06) * mm});
            skArc(sketch, "E146.18.15", {"start": v(21.6, 5.45) * mm, "mid": v(21.6, 5.55) * mm, "end": v(21.67, 5.62) * mm});
            skArc(sketch, "E146.19.0", {"start": v(23.47, 6.22) * mm, "mid": v(23.43, 6.38) * mm, "end": v(23.37, 6.53) * mm});
            skArc(sketch, "E146.19.1", {"start": v(23.22, 5.68) * mm, "mid": v(23.42, 5.92) * mm, "end": v(23.47, 6.22) * mm});
            skArc(sketch, "E146.19.2", {"start": v(22.46, 6.83) * mm, "mid": v(22.05, 6.57) * mm, "end": v(21.63, 6.34) * mm});
            skPoint(sketch, "E146.19.3", {"position": v(22.8, 6.3) * mm});
            skArc(sketch, "E146.19.4", {"start": v(22.64, 5.67) * mm, "mid": v(22.5, 5.76) * mm, "end": v(22.39, 5.87) * mm});
            skLineSegment(sketch, "E146.19.5", {"start": v(23.23, 7.4) * mm, "end": v(23.65, 6.9) * mm});
            skArc(sketch, "E146.19.6", {"start": v(22.2, 5.9) * mm, "mid": v(22.07, 5.83) * mm, "end": v(21.94, 5.76) * mm});
            skLineSegment(sketch, "E146.19.7", {"start": v(21.63, 6.34) * mm, "end": v(21.94, 5.76) * mm});
            skArc(sketch, "E146.19.8", {"start": v(23.22, 5.68) * mm, "mid": v(22.93, 5.6) * mm, "end": v(22.64, 5.67) * mm});
            skPoint(sketch, "E146.19.9", {"position": v(22.46, 6.83) * mm});
            skArc(sketch, "E146.19.10", {"start": v(22.67, 6.52) * mm, "mid": v(22.24, 6.25) * mm, "end": v(21.8, 6) * mm, "construction": true});
            skArc(sketch, "E146.19.11", {"start": v(22.46, 6.83) * mm, "mid": v(22.85, 7.1) * mm, "end": v(23.23, 7.4) * mm});
            skPoint(sketch, "E146.19.12", {"position": v(22.67, 6.52) * mm});
            skArc(sketch, "E146.19.13", {"start": v(23.41, 6.71) * mm, "mid": v(23.53, 6.8) * mm, "end": v(23.65, 6.9) * mm});
            skArc(sketch, "E146.19.14", {"start": v(22.39, 5.87) * mm, "mid": v(22.3, 5.92) * mm, "end": v(22.2, 5.9) * mm});
            skArc(sketch, "E146.19.15", {"start": v(23.37, 6.53) * mm, "mid": v(23.36, 6.63) * mm, "end": v(23.41, 6.71) * mm});
            skArc(sketch, "E146.20.0", {"start": v(25.05, 7.65) * mm, "mid": v(25, 7.8) * mm, "end": v(24.9, 7.93) * mm});
            skArc(sketch, "E146.20.1", {"start": v(24.92, 7.08) * mm, "mid": v(25.07, 7.35) * mm, "end": v(25.05, 7.65) * mm});
            skArc(sketch, "E146.20.2", {"start": v(23.95, 8.05) * mm, "mid": v(23.6, 7.72) * mm, "end": v(23.23, 7.4) * mm});
            skPoint(sketch, "E146.20.3", {"position": v(24.4, 7.6) * mm});
            skArc(sketch, "E146.20.4", {"start": v(24.35, 6.95) * mm, "mid": v(24.2, 7) * mm, "end": v(24.07, 7.1) * mm});
            skLineSegment(sketch, "E146.20.5", {"start": v(24.6, 8.77) * mm, "end": v(25.1, 8.35) * mm});
            skArc(sketch, "E146.20.6", {"start": v(23.88, 7.1) * mm, "mid": v(23.76, 7) * mm, "end": v(23.65, 6.9) * mm});
            skLineSegment(sketch, "E146.20.7", {"start": v(23.23, 7.4) * mm, "end": v(23.65, 6.9) * mm});
            skArc(sketch, "E146.20.8", {"start": v(24.92, 7.08) * mm, "mid": v(24.65, 6.93) * mm, "end": v(24.35, 6.95) * mm});
            skPoint(sketch, "E146.20.9", {"position": v(23.95, 8.05) * mm});
            skArc(sketch, "E146.20.10", {"start": v(24.21, 7.79) * mm, "mid": v(23.85, 7.44) * mm, "end": v(23.47, 7.12) * mm, "construction": true});
            skArc(sketch, "E146.20.11", {"start": v(23.95, 8.05) * mm, "mid": v(24.28, 8.4) * mm, "end": v(24.6, 8.77) * mm});
            skPoint(sketch, "E146.20.12", {"position": v(24.21, 7.79) * mm});
            skArc(sketch, "E146.20.13", {"start": v(24.9, 8.12) * mm, "mid": v(25, 8.24) * mm, "end": v(25.1, 8.35) * mm});
            skArc(sketch, "E146.20.14", {"start": v(24.07, 7.1) * mm, "mid": v(23.97, 7.13) * mm, "end": v(23.88, 7.1) * mm});
            skArc(sketch, "E146.20.15", {"start": v(24.9, 7.93) * mm, "mid": v(24.87, 8.03) * mm, "end": v(24.9, 8.12) * mm});
            skArc(sketch, "E146.21.0", {"start": v(26.33, 9.36) * mm, "mid": v(26.24, 9.5) * mm, "end": v(26.13, 9.61) * mm});
            skArc(sketch, "E146.21.1", {"start": v(26.32, 8.78) * mm, "mid": v(26.4, 9.07) * mm, "end": v(26.33, 9.36) * mm});
            skArc(sketch, "E146.21.2", {"start": v(25.17, 9.54) * mm, "mid": v(24.9, 9.15) * mm, "end": v(24.6, 8.77) * mm});
            skPoint(sketch, "E146.21.3", {"position": v(25.7, 9.2) * mm});
            skArc(sketch, "E146.21.4", {"start": v(25.78, 8.53) * mm, "mid": v(25.62, 8.57) * mm, "end": v(25.47, 8.63) * mm});
            skLineSegment(sketch, "E146.21.5", {"start": v(25.66, 10.37) * mm, "end": v(26.24, 10.06) * mm});
            skArc(sketch, "E146.21.6", {"start": v(25.29, 8.59) * mm, "mid": v(25.2, 8.47) * mm, "end": v(25.1, 8.35) * mm});
            skLineSegment(sketch, "E146.21.7", {"start": v(24.6, 8.77) * mm, "end": v(25.1, 8.35) * mm});
            skArc(sketch, "E146.21.8", {"start": v(26.32, 8.78) * mm, "mid": v(26.08, 8.58) * mm, "end": v(25.78, 8.53) * mm});
            skPoint(sketch, "E146.21.9", {"position": v(25.17, 9.54) * mm});
            skArc(sketch, "E146.21.10", {"start": v(25.48, 9.33) * mm, "mid": v(25.2, 8.92) * mm, "end": v(24.88, 8.53) * mm, "construction": true});
            skArc(sketch, "E146.21.11", {"start": v(25.17, 9.54) * mm, "mid": v(25.43, 9.95) * mm, "end": v(25.66, 10.37) * mm});
            skPoint(sketch, "E146.21.12", {"position": v(25.48, 9.33) * mm});
            skArc(sketch, "E146.21.13", {"start": v(26.1, 9.8) * mm, "mid": v(26.17, 9.93) * mm, "end": v(26.24, 10.06) * mm});
            skArc(sketch, "E146.21.14", {"start": v(25.47, 8.63) * mm, "mid": v(25.37, 8.64) * mm, "end": v(25.29, 8.59) * mm});
            skArc(sketch, "E146.21.15", {"start": v(26.13, 9.61) * mm, "mid": v(26.08, 9.7) * mm, "end": v(26.1, 9.8) * mm});
            skArc(sketch, "E146.22.0", {"start": v(27.25, 11.3) * mm, "mid": v(27.14, 11.4) * mm, "end": v(27, 11.5) * mm});
            skArc(sketch, "E146.22.1", {"start": v(27.35, 10.71) * mm, "mid": v(27.39, 11.02) * mm, "end": v(27.25, 11.3) * mm});
            skArc(sketch, "E146.22.2", {"start": v(26.08, 11.24) * mm, "mid": v(25.88, 10.8) * mm, "end": v(25.66, 10.37) * mm});
            skPoint(sketch, "E146.22.3", {"position": v(26.66, 11) * mm});
            skArc(sketch, "E146.22.4", {"start": v(26.87, 10.37) * mm, "mid": v(26.71, 10.37) * mm, "end": v(26.55, 10.4) * mm});
            skLineSegment(sketch, "E146.22.5", {"start": v(26.4, 12.15) * mm, "end": v(27.03, 11.96) * mm});
            skArc(sketch, "E146.22.6", {"start": v(26.38, 10.33) * mm, "mid": v(26.31, 10.2) * mm, "end": v(26.24, 10.06) * mm});
            skLineSegment(sketch, "E146.22.7", {"start": v(25.66, 10.37) * mm, "end": v(26.24, 10.06) * mm});
            skArc(sketch, "E146.22.8", {"start": v(27.35, 10.71) * mm, "mid": v(27.16, 10.47) * mm, "end": v(26.87, 10.37) * mm});
            skPoint(sketch, "E146.22.9", {"position": v(26.08, 11.24) * mm});
            skArc(sketch, "E146.22.10", {"start": v(26.42, 11.1) * mm, "mid": v(26.22, 10.64) * mm, "end": v(26, 10.2) * mm, "construction": true});
            skArc(sketch, "E146.22.11", {"start": v(26.08, 11.24) * mm, "mid": v(26.25, 11.7) * mm, "end": v(26.4, 12.15) * mm});
            skPoint(sketch, "E146.22.12", {"position": v(26.42, 11.1) * mm});
            skArc(sketch, "E146.22.13", {"start": v(26.94, 11.67) * mm, "mid": v(26.98, 11.82) * mm, "end": v(27.03, 11.96) * mm});
            skArc(sketch, "E146.22.14", {"start": v(26.55, 10.4) * mm, "mid": v(26.45, 10.4) * mm, "end": v(26.38, 10.33) * mm});
            skArc(sketch, "E146.22.15", {"start": v(27, 11.5) * mm, "mid": v(26.94, 11.57) * mm, "end": v(26.94, 11.67) * mm});
            skArc(sketch, "E146.23.0", {"start": v(27.78, 13.36) * mm, "mid": v(27.64, 13.45) * mm, "end": v(27.5, 13.52) * mm});
            skArc(sketch, "E146.23.1", {"start": v(27.99, 12.81) * mm, "mid": v(27.96, 13.12) * mm, "end": v(27.78, 13.36) * mm});
            skArc(sketch, "E146.23.2", {"start": v(26.64, 13.08) * mm, "mid": v(26.53, 12.61) * mm, "end": v(26.4, 12.15) * mm});
            skPoint(sketch, "E146.23.3", {"position": v(27.25, 12.96) * mm});
            skArc(sketch, "E146.23.4", {"start": v(27.59, 12.39) * mm, "mid": v(27.43, 12.36) * mm, "end": v(27.27, 12.36) * mm});
            skLineSegment(sketch, "E146.23.5", {"start": v(26.78, 14.04) * mm, "end": v(27.43, 13.97) * mm});
            skArc(sketch, "E146.23.6", {"start": v(27.11, 12.24) * mm, "mid": v(27.07, 12.1) * mm, "end": v(27.03, 11.96) * mm});
            skLineSegment(sketch, "E146.23.7", {"start": v(26.4, 12.15) * mm, "end": v(27.03, 11.96) * mm});
            skArc(sketch, "E146.23.8", {"start": v(27.99, 12.81) * mm, "mid": v(27.85, 12.54) * mm, "end": v(27.59, 12.39) * mm});
            skPoint(sketch, "E146.23.9", {"position": v(26.64, 13.08) * mm});
            skArc(sketch, "E146.23.10", {"start": v(27, 13.01) * mm, "mid": v(26.9, 12.52) * mm, "end": v(26.76, 12.04) * mm, "construction": true});
            skArc(sketch, "E146.23.11", {"start": v(26.64, 13.08) * mm, "mid": v(26.72, 13.56) * mm, "end": v(26.78, 14.04) * mm});
            skPoint(sketch, "E146.23.12", {"position": v(27, 13.01) * mm});
            skArc(sketch, "E146.23.13", {"start": v(27.4, 13.68) * mm, "mid": v(27.41, 13.82) * mm, "end": v(27.43, 13.97) * mm});
            skArc(sketch, "E146.23.14", {"start": v(27.27, 12.36) * mm, "mid": v(27.17, 12.33) * mm, "end": v(27.11, 12.24) * mm});
            skArc(sketch, "E146.23.15", {"start": v(27.5, 13.52) * mm, "mid": v(27.42, 13.58) * mm, "end": v(27.4, 13.68) * mm});
            skArc(sketch, "E146.24.0", {"start": v(27.9, 15.5) * mm, "mid": v(27.74, 15.56) * mm, "end": v(27.58, 15.6) * mm});
            skArc(sketch, "E146.24.1", {"start": v(28.2, 15) * mm, "mid": v(28.12, 15.3) * mm, "end": v(27.9, 15.5) * mm});
            skArc(sketch, "E146.24.2", {"start": v(26.82, 15) * mm, "mid": v(26.81, 14.52) * mm, "end": v(26.78, 14.04) * mm});
            skPoint(sketch, "E146.24.3", {"position": v(27.45, 15) * mm});
            skArc(sketch, "E146.24.4", {"start": v(27.9, 14.5) * mm, "mid": v(27.74, 14.44) * mm, "end": v(27.58, 14.4) * mm});
            skLineSegment(sketch, "E146.24.5", {"start": v(26.78, 15.96) * mm, "end": v(27.43, 16.03) * mm});
            skArc(sketch, "E146.24.6", {"start": v(27.45, 14.27) * mm, "mid": v(27.44, 14.12) * mm, "end": v(27.43, 13.97) * mm});
            skLineSegment(sketch, "E146.24.7", {"start": v(26.78, 14.04) * mm, "end": v(27.43, 13.97) * mm});
            skArc(sketch, "E146.24.8", {"start": v(28.2, 15) * mm, "mid": v(28.12, 14.7) * mm, "end": v(27.9, 14.5) * mm});
            skPoint(sketch, "E146.24.9", {"position": v(26.82, 15) * mm});
            skArc(sketch, "E146.24.10", {"start": v(27.2, 15) * mm, "mid": v(27.19, 14.5) * mm, "end": v(27.15, 14) * mm, "construction": true});
            skArc(sketch, "E146.24.11", {"start": v(26.82, 15) * mm, "mid": v(26.81, 15.48) * mm, "end": v(26.78, 15.96) * mm});
            skPoint(sketch, "E146.24.12", {"position": v(27.2, 15) * mm});
            skArc(sketch, "E146.24.13", {"start": v(27.45, 15.73) * mm, "mid": v(27.44, 15.88) * mm, "end": v(27.43, 16.03) * mm});
            skArc(sketch, "E146.24.14", {"start": v(27.58, 14.4) * mm, "mid": v(27.5, 14.36) * mm, "end": v(27.45, 14.27) * mm});
            skArc(sketch, "E146.24.15", {"start": v(27.58, 15.6) * mm, "mid": v(27.5, 15.64) * mm, "end": v(27.45, 15.73) * mm});
            skArc(sketch, "E146.25.0", {"start": v(27.59, 17.61) * mm, "mid": v(27.43, 17.64) * mm, "end": v(27.27, 17.64) * mm});
            skArc(sketch, "E146.25.1", {"start": v(27.99, 17.19) * mm, "mid": v(27.85, 17.46) * mm, "end": v(27.59, 17.61) * mm});
            skArc(sketch, "E146.25.2", {"start": v(26.64, 16.92) * mm, "mid": v(26.72, 16.44) * mm, "end": v(26.78, 15.96) * mm});
            skPoint(sketch, "E146.25.3", {"position": v(27.25, 17.04) * mm});
            skArc(sketch, "E146.25.4", {"start": v(27.78, 16.64) * mm, "mid": v(27.64, 16.55) * mm, "end": v(27.5, 16.48) * mm});
            skLineSegment(sketch, "E146.25.5", {"start": v(26.4, 17.85) * mm, "end": v(27.03, 18.04) * mm});
            skArc(sketch, "E146.25.6", {"start": v(27.4, 16.32) * mm, "mid": v(27.41, 16.18) * mm, "end": v(27.43, 16.03) * mm});
            skLineSegment(sketch, "E146.25.7", {"start": v(26.78, 15.96) * mm, "end": v(27.43, 16.03) * mm});
            skArc(sketch, "E146.25.8", {"start": v(27.99, 17.19) * mm, "mid": v(27.96, 16.88) * mm, "end": v(27.78, 16.64) * mm});
            skPoint(sketch, "E146.25.9", {"position": v(26.64, 16.92) * mm});
            skArc(sketch, "E146.25.10", {"start": v(27, 16.99) * mm, "mid": v(27.09, 16.5) * mm, "end": v(27.15, 16) * mm, "construction": true});
            skArc(sketch, "E146.25.11", {"start": v(26.64, 16.92) * mm, "mid": v(26.53, 17.39) * mm, "end": v(26.4, 17.85) * mm});
            skPoint(sketch, "E146.25.12", {"position": v(27, 16.99) * mm});
            skArc(sketch, "E146.25.13", {"start": v(27.11, 17.76) * mm, "mid": v(27.07, 17.9) * mm, "end": v(27.03, 18.04) * mm});
            skArc(sketch, "E146.25.14", {"start": v(27.5, 16.48) * mm, "mid": v(27.42, 16.42) * mm, "end": v(27.4, 16.32) * mm});
            skArc(sketch, "E146.25.15", {"start": v(27.27, 17.64) * mm, "mid": v(27.17, 17.67) * mm, "end": v(27.11, 17.76) * mm});
            skArc(sketch, "E146.26.0", {"start": v(26.87, 19.63) * mm, "mid": v(26.71, 19.63) * mm, "end": v(26.55, 19.6) * mm});
            skArc(sketch, "E146.26.1", {"start": v(27.35, 19.29) * mm, "mid": v(27.16, 19.53) * mm, "end": v(26.87, 19.63) * mm});
            skArc(sketch, "E146.26.2", {"start": v(26.08, 18.76) * mm, "mid": v(26.25, 18.3) * mm, "end": v(26.4, 17.85) * mm});
            skPoint(sketch, "E146.26.3", {"position": v(26.66, 19) * mm});
            skArc(sketch, "E146.26.4", {"start": v(27.25, 18.7) * mm, "mid": v(27.14, 18.6) * mm, "end": v(27, 18.5) * mm});
            skLineSegment(sketch, "E146.26.5", {"start": v(25.66, 19.63) * mm, "end": v(26.24, 19.94) * mm});
            skArc(sketch, "E146.26.6", {"start": v(26.94, 18.33) * mm, "mid": v(26.98, 18.18) * mm, "end": v(27.03, 18.04) * mm});
            skLineSegment(sketch, "E146.26.7", {"start": v(26.4, 17.85) * mm, "end": v(27.03, 18.04) * mm});
            skArc(sketch, "E146.26.8", {"start": v(27.35, 19.29) * mm, "mid": v(27.39, 18.98) * mm, "end": v(27.25, 18.7) * mm});
            skPoint(sketch, "E146.26.9", {"position": v(26.08, 18.76) * mm});
            skArc(sketch, "E146.26.10", {"start": v(26.42, 18.9) * mm, "mid": v(26.6, 18.44) * mm, "end": v(26.76, 17.96) * mm, "construction": true});
            skArc(sketch, "E146.26.11", {"start": v(26.08, 18.76) * mm, "mid": v(25.88, 19.2) * mm, "end": v(25.66, 19.63) * mm});
            skPoint(sketch, "E146.26.12", {"position": v(26.42, 18.9) * mm});
            skArc(sketch, "E146.26.13", {"start": v(26.38, 19.67) * mm, "mid": v(26.31, 19.8) * mm, "end": v(26.24, 19.94) * mm});
            skArc(sketch, "E146.26.14", {"start": v(27, 18.5) * mm, "mid": v(26.94, 18.43) * mm, "end": v(26.94, 18.33) * mm});
            skArc(sketch, "E146.26.15", {"start": v(26.55, 19.6) * mm, "mid": v(26.45, 19.6) * mm, "end": v(26.38, 19.67) * mm});
            skArc(sketch, "E146.27.0", {"start": v(25.78, 21.47) * mm, "mid": v(25.62, 21.43) * mm, "end": v(25.47, 21.37) * mm});
            skArc(sketch, "E146.27.1", {"start": v(26.32, 21.22) * mm, "mid": v(26.08, 21.42) * mm, "end": v(25.78, 21.47) * mm});
            skArc(sketch, "E146.27.2", {"start": v(25.17, 20.46) * mm, "mid": v(25.43, 20.05) * mm, "end": v(25.66, 19.63) * mm});
            skPoint(sketch, "E146.27.3", {"position": v(25.7, 20.8) * mm});
            skArc(sketch, "E146.27.4", {"start": v(26.33, 20.64) * mm, "mid": v(26.24, 20.5) * mm, "end": v(26.13, 20.39) * mm});
            skLineSegment(sketch, "E146.27.5", {"start": v(24.6, 21.23) * mm, "end": v(25.1, 21.65) * mm});
            skArc(sketch, "E146.27.6", {"start": v(26.1, 20.2) * mm, "mid": v(26.17, 20.07) * mm, "end": v(26.24, 19.94) * mm});
            skLineSegment(sketch, "E146.27.7", {"start": v(25.66, 19.63) * mm, "end": v(26.24, 19.94) * mm});
            skArc(sketch, "E146.27.8", {"start": v(26.32, 21.22) * mm, "mid": v(26.4, 20.93) * mm, "end": v(26.33, 20.64) * mm});
            skPoint(sketch, "E146.27.9", {"position": v(25.17, 20.46) * mm});
            skArc(sketch, "E146.27.10", {"start": v(25.48, 20.67) * mm, "mid": v(25.75, 20.24) * mm, "end": v(26, 19.8) * mm, "construction": true});
            skArc(sketch, "E146.27.11", {"start": v(25.17, 20.46) * mm, "mid": v(24.9, 20.85) * mm, "end": v(24.6, 21.23) * mm});
            skPoint(sketch, "E146.27.12", {"position": v(25.48, 20.67) * mm});
            skArc(sketch, "E146.27.13", {"start": v(25.29, 21.41) * mm, "mid": v(25.2, 21.53) * mm, "end": v(25.1, 21.65) * mm});
            skArc(sketch, "E146.27.14", {"start": v(26.13, 20.39) * mm, "mid": v(26.08, 20.3) * mm, "end": v(26.1, 20.2) * mm});
            skArc(sketch, "E146.27.15", {"start": v(25.47, 21.37) * mm, "mid": v(25.37, 21.36) * mm, "end": v(25.29, 21.41) * mm});
            skArc(sketch, "E146.28.0", {"start": v(24.35, 23.05) * mm, "mid": v(24.2, 23) * mm, "end": v(24.07, 22.9) * mm});
            skArc(sketch, "E146.28.1", {"start": v(24.92, 22.92) * mm, "mid": v(24.65, 23.07) * mm, "end": v(24.35, 23.05) * mm});
            skArc(sketch, "E146.28.2", {"start": v(23.95, 21.95) * mm, "mid": v(24.28, 21.6) * mm, "end": v(24.6, 21.23) * mm});
            skPoint(sketch, "E146.28.3", {"position": v(24.4, 22.4) * mm});
            skArc(sketch, "E146.28.4", {"start": v(25.05, 22.35) * mm, "mid": v(25, 22.2) * mm, "end": v(24.9, 22.07) * mm});
            skLineSegment(sketch, "E146.28.5", {"start": v(23.23, 22.6) * mm, "end": v(23.65, 23.1) * mm});
            skArc(sketch, "E146.28.6", {"start": v(24.9, 21.88) * mm, "mid": v(25, 21.76) * mm, "end": v(25.1, 21.65) * mm});
            skLineSegment(sketch, "E146.28.7", {"start": v(24.6, 21.23) * mm, "end": v(25.1, 21.65) * mm});
            skArc(sketch, "E146.28.8", {"start": v(24.92, 22.92) * mm, "mid": v(25.07, 22.65) * mm, "end": v(25.05, 22.35) * mm});
            skPoint(sketch, "E146.28.9", {"position": v(23.95, 21.95) * mm});
            skArc(sketch, "E146.28.10", {"start": v(24.21, 22.21) * mm, "mid": v(24.56, 21.85) * mm, "end": v(24.88, 21.47) * mm, "construction": true});
            skArc(sketch, "E146.28.11", {"start": v(23.95, 21.95) * mm, "mid": v(23.6, 22.28) * mm, "end": v(23.23, 22.6) * mm});
            skPoint(sketch, "E146.28.12", {"position": v(24.21, 22.21) * mm});
            skArc(sketch, "E146.28.13", {"start": v(23.88, 22.9) * mm, "mid": v(23.76, 23) * mm, "end": v(23.65, 23.1) * mm});
            skArc(sketch, "E146.28.14", {"start": v(24.9, 22.07) * mm, "mid": v(24.87, 21.97) * mm, "end": v(24.9, 21.88) * mm});
            skArc(sketch, "E146.28.15", {"start": v(24.07, 22.9) * mm, "mid": v(23.97, 22.87) * mm, "end": v(23.88, 22.9) * mm});
            skArc(sketch, "E146.29.0", {"start": v(22.64, 24.33) * mm, "mid": v(22.5, 24.24) * mm, "end": v(22.39, 24.13) * mm});
            skArc(sketch, "E146.29.1", {"start": v(23.22, 24.32) * mm, "mid": v(22.93, 24.4) * mm, "end": v(22.64, 24.33) * mm});
            skArc(sketch, "E146.29.2", {"start": v(22.46, 23.17) * mm, "mid": v(22.85, 22.9) * mm, "end": v(23.23, 22.6) * mm});
            skPoint(sketch, "E146.29.3", {"position": v(22.8, 23.7) * mm});
            skArc(sketch, "E146.29.4", {"start": v(23.47, 23.78) * mm, "mid": v(23.43, 23.62) * mm, "end": v(23.37, 23.47) * mm});
            skLineSegment(sketch, "E146.29.5", {"start": v(21.63, 23.66) * mm, "end": v(21.94, 24.24) * mm});
            skArc(sketch, "E146.29.6", {"start": v(23.41, 23.29) * mm, "mid": v(23.53, 23.2) * mm, "end": v(23.65, 23.1) * mm});
            skLineSegment(sketch, "E146.29.7", {"start": v(23.23, 22.6) * mm, "end": v(23.65, 23.1) * mm});
            skArc(sketch, "E146.29.8", {"start": v(23.22, 24.32) * mm, "mid": v(23.42, 24.08) * mm, "end": v(23.47, 23.78) * mm});
            skPoint(sketch, "E146.29.9", {"position": v(22.46, 23.17) * mm});
            skArc(sketch, "E146.29.10", {"start": v(22.67, 23.48) * mm, "mid": v(23.08, 23.2) * mm, "end": v(23.47, 22.88) * mm, "construction": true});
            skArc(sketch, "E146.29.11", {"start": v(22.46, 23.17) * mm, "mid": v(22.05, 23.43) * mm, "end": v(21.63, 23.66) * mm});
            skPoint(sketch, "E146.29.12", {"position": v(22.67, 23.48) * mm});
            skArc(sketch, "E146.29.13", {"start": v(22.2, 24.1) * mm, "mid": v(22.07, 24.17) * mm, "end": v(21.94, 24.24) * mm});
            skArc(sketch, "E146.29.14", {"start": v(23.37, 23.47) * mm, "mid": v(23.36, 23.37) * mm, "end": v(23.41, 23.29) * mm});
            skArc(sketch, "E146.29.15", {"start": v(22.39, 24.13) * mm, "mid": v(22.3, 24.08) * mm, "end": v(22.2, 24.1) * mm});
            skArc(sketch, "E146.30.0", {"start": v(20.7, 25.25) * mm, "mid": v(20.6, 25.14) * mm, "end": v(20.5, 25) * mm});
            skArc(sketch, "E146.30.1", {"start": v(21.29, 25.35) * mm, "mid": v(20.98, 25.39) * mm, "end": v(20.7, 25.25) * mm});
            skArc(sketch, "E146.30.2", {"start": v(20.76, 24.08) * mm, "mid": v(21.2, 23.88) * mm, "end": v(21.63, 23.66) * mm});
            skPoint(sketch, "E146.30.3", {"position": v(21, 24.66) * mm});
            skArc(sketch, "E146.30.4", {"start": v(21.63, 24.87) * mm, "mid": v(21.63, 24.71) * mm, "end": v(21.6, 24.55) * mm});
            skLineSegment(sketch, "E146.30.5", {"start": v(19.85, 24.4) * mm, "end": v(20.04, 25.03) * mm});
            skArc(sketch, "E146.30.6", {"start": v(21.67, 24.38) * mm, "mid": v(21.8, 24.31) * mm, "end": v(21.94, 24.24) * mm});
            skLineSegment(sketch, "E146.30.7", {"start": v(21.63, 23.66) * mm, "end": v(21.94, 24.24) * mm});
            skArc(sketch, "E146.30.8", {"start": v(21.29, 25.35) * mm, "mid": v(21.53, 25.16) * mm, "end": v(21.63, 24.87) * mm});
            skPoint(sketch, "E146.30.9", {"position": v(20.76, 24.08) * mm});
            skArc(sketch, "E146.30.10", {"start": v(20.9, 24.42) * mm, "mid": v(21.36, 24.22) * mm, "end": v(21.8, 24) * mm, "construction": true});
            skArc(sketch, "E146.30.11", {"start": v(20.76, 24.08) * mm, "mid": v(20.3, 24.25) * mm, "end": v(19.85, 24.4) * mm});
            skPoint(sketch, "E146.30.12", {"position": v(20.9, 24.42) * mm});
            skArc(sketch, "E146.30.13", {"start": v(20.33, 24.94) * mm, "mid": v(20.18, 24.98) * mm, "end": v(20.04, 25.03) * mm});
            skArc(sketch, "E146.30.14", {"start": v(21.6, 24.55) * mm, "mid": v(21.6, 24.45) * mm, "end": v(21.67, 24.38) * mm});
            skArc(sketch, "E146.30.15", {"start": v(20.5, 25) * mm, "mid": v(20.43, 24.94) * mm, "end": v(20.33, 24.94) * mm});
            skArc(sketch, "E146.31.0", {"start": v(18.64, 25.78) * mm, "mid": v(18.55, 25.64) * mm, "end": v(18.48, 25.5) * mm});
            skArc(sketch, "E146.31.1", {"start": v(19.19, 25.99) * mm, "mid": v(18.88, 25.96) * mm, "end": v(18.64, 25.78) * mm});
            skArc(sketch, "E146.31.2", {"start": v(18.92, 24.64) * mm, "mid": v(19.39, 24.53) * mm, "end": v(19.85, 24.4) * mm});
            skPoint(sketch, "E146.31.3", {"position": v(19.04, 25.25) * mm});
            skArc(sketch, "E146.31.4", {"start": v(19.61, 25.59) * mm, "mid": v(19.64, 25.43) * mm, "end": v(19.64, 25.27) * mm});
            skArc(sketch, "E146.31.6", {"start": v(19.76, 25.11) * mm, "mid": v(19.9, 25.07) * mm, "end": v(20.04, 25.03) * mm});
            skLineSegment(sketch, "E146.31.7", {"start": v(19.85, 24.4) * mm, "end": v(20.04, 25.03) * mm});
            skArc(sketch, "E146.31.8", {"start": v(19.19, 25.99) * mm, "mid": v(19.46, 25.85) * mm, "end": v(19.61, 25.59) * mm});
            skPoint(sketch, "E146.31.9", {"position": v(18.92, 24.64) * mm});
            skArc(sketch, "E146.31.10", {"start": v(18.99, 25) * mm, "mid": v(19.48, 24.9) * mm, "end": v(19.96, 24.76) * mm, "construction": true});
            skArc(sketch, "E146.31.11", {"start": v(18.92, 24.64) * mm, "mid": v(18.44, 24.72) * mm, "end": v(17.96, 24.78) * mm});
            skPoint(sketch, "E146.31.12", {"position": v(18.99, 25) * mm});
            skArc(sketch, "E146.31.13", {"start": v(18.32, 25.4) * mm, "mid": v(18.18, 25.41) * mm, "end": v(18.03, 25.43) * mm});
            skArc(sketch, "E146.31.14", {"start": v(19.64, 25.27) * mm, "mid": v(19.67, 25.17) * mm, "end": v(19.76, 25.11) * mm});
            skArc(sketch, "E146.31.15", {"start": v(18.48, 25.5) * mm, "mid": v(18.42, 25.42) * mm, "end": v(18.32, 25.4) * mm});
            skLineSegment(sketch, "E147.0", {"start": v(6.75, 15) * mm, "end": v(27.25, 15) * mm, "construction": true});
            skSolve(sketch);
        }
        {
            var Q0;
            Q0=qSketchRegion(id+"F22",true);
            extrude(context, id + "F23", {"entities" : qUnion([Q0]), "operationType" : NewBodyOperationType.REMOVE, "endBound" : BoundingType.SYMMETRIC, "oppositeDirection" : true, "depth" : 6.5 * mm});
        }
        {
            var Q0;
            Q0=makeQuery(id+"F2.boolean.opBoolean","MERGE",FACE,{"derivedFrom":[makeQuery(id+"F1.opExtrude","SWEPT_FACE",FACE,{"disambiguationData":[OSD([sQuery(id+"F0.wireOp",EDGE,"E0.right"),sQuery(id+"F0.wireOp",EDGE,"E25")])]}),makeQuery(id+"F2.opExtrude","SWEPT_FACE",FACE,{"disambiguationData":[OSD([sQuery(id+"F0.wireOp",EDGE,"E31")])]})]});
            var Q1;
            Q1=sQuery(id+"F0.wireOp",VERTEX,"E12.MirrorP");
            cPlane(context, id + "F24", {"entities" : qUnion([Q0, Q1]), "cplaneType" : CPlaneType.PLANE_POINT, "offset" : 150 * mm, "width" : 150 * mm, "height" : 150 * mm});
        }
        {
            var Q0;
            Q0=qCreatedBy(id+"F24.planeOp",FACE);
            var sketch = newSketch(context, id + "F25", { "sketchPlane" : qUnion([Q0])});
            skLineSegment(sketch, "E148", {"start": v(17, 12.16) * mm, "end": v(17, 9.53) * mm, "construction": true});
            skArc(sketch, "E149", {"start": v(17, 26.2) * mm, "mid": v(17.3, 26.12) * mm, "end": v(17.5, 25.9) * mm});
            skArc(sketch, "E150", {"start": v(17.5, 25.9) * mm, "mid": v(17.56, 25.74) * mm, "end": v(17.6, 25.58) * mm});
            skArc(sketch, "E151", {"start": v(17.6, 25.58) * mm, "mid": v(17.64, 25.5) * mm, "end": v(17.73, 25.45) * mm});
            skPoint(sketch, "E152", {"position": v(17, 24.82) * mm});
            skPoint(sketch, "E153", {"position": v(17, 25.45) * mm});
            skPoint(sketch, "E154", {"position": v(17, 25.2) * mm});
            skArc(sketch, "E155", {"start": v(17, 25.2) * mm, "mid": v(17.5, 25.19) * mm, "end": v(18, 25.15) * mm, "construction": true});
            skLineSegment(sketch, "E156", {"start": v(17.96, 24.78) * mm, "end": v(18.03, 25.43) * mm});
            skArc(sketch, "E157", {"start": v(17.73, 25.45) * mm, "mid": v(17.88, 25.44) * mm, "end": v(18.03, 25.43) * mm});
            skArc(sketch, "E158", {"start": v(17, 24.82) * mm, "mid": v(17.48, 24.81) * mm, "end": v(17.96, 24.78) * mm});
            skArc(sketch, "E159.MirrorCS", {"start": v(17, 26.2) * mm, "mid": v(16.7, 26.12) * mm, "end": v(16.5, 25.9) * mm});
            skArc(sketch, "E160.MirrorCS", {"start": v(16.5, 25.9) * mm, "mid": v(16.44, 25.74) * mm, "end": v(16.4, 25.58) * mm});
            skArc(sketch, "E161.MirrorCS", {"start": v(16.4, 25.58) * mm, "mid": v(16.36, 25.5) * mm, "end": v(16.27, 25.45) * mm});
            skArc(sketch, "E162.MirrorCS", {"start": v(16.27, 25.45) * mm, "mid": v(16.12, 25.44) * mm, "end": v(15.97, 25.43) * mm});
            skLineSegment(sketch, "E163.MirrorCS", {"start": v(16.04, 24.78) * mm, "end": v(15.97, 25.43) * mm});
            skArc(sketch, "E164.MirrorCS", {"start": v(17, 24.82) * mm, "mid": v(16.52, 24.81) * mm, "end": v(16.04, 24.78) * mm});
            skArc(sketch, "E165.1.0", {"start": v(14.39, 25.59) * mm, "mid": v(14.36, 25.43) * mm, "end": v(14.36, 25.27) * mm});
            skArc(sketch, "E165.1.1", {"start": v(14.81, 25.99) * mm, "mid": v(14.54, 25.85) * mm, "end": v(14.39, 25.59) * mm});
            skArc(sketch, "E165.1.2", {"start": v(15.08, 24.64) * mm, "mid": v(15.56, 24.72) * mm, "end": v(16.04, 24.78) * mm});
            skPoint(sketch, "E165.1.3", {"position": v(14.96, 25.25) * mm});
            skArc(sketch, "E165.1.4", {"start": v(15.36, 25.78) * mm, "mid": v(15.45, 25.64) * mm, "end": v(15.52, 25.5) * mm});
            skLineSegment(sketch, "E165.1.5", {"start": v(14.15, 24.4) * mm, "end": v(13.96, 25.03) * mm});
            skArc(sketch, "E165.1.6", {"start": v(15.68, 25.4) * mm, "mid": v(15.82, 25.41) * mm, "end": v(15.97, 25.43) * mm});
            skArc(sketch, "E165.1.8", {"start": v(14.81, 25.99) * mm, "mid": v(15.12, 25.96) * mm, "end": v(15.36, 25.78) * mm});
            skPoint(sketch, "E165.1.9", {"position": v(15.08, 24.64) * mm});
            skArc(sketch, "E165.1.10", {"start": v(15.01, 25) * mm, "mid": v(15.5, 25.09) * mm, "end": v(16, 25.15) * mm, "construction": true});
            skArc(sketch, "E165.1.11", {"start": v(15.08, 24.64) * mm, "mid": v(14.61, 24.53) * mm, "end": v(14.15, 24.4) * mm});
            skPoint(sketch, "E165.1.12", {"position": v(15.01, 25) * mm});
            skArc(sketch, "E165.1.13", {"start": v(14.24, 25.11) * mm, "mid": v(14.1, 25.07) * mm, "end": v(13.96, 25.03) * mm});
            skArc(sketch, "E165.1.14", {"start": v(15.52, 25.5) * mm, "mid": v(15.58, 25.42) * mm, "end": v(15.68, 25.4) * mm});
            skArc(sketch, "E165.1.15", {"start": v(14.36, 25.27) * mm, "mid": v(14.33, 25.17) * mm, "end": v(14.24, 25.11) * mm});
            skArc(sketch, "E165.2.0", {"start": v(12.37, 24.87) * mm, "mid": v(12.37, 24.71) * mm, "end": v(12.4, 24.55) * mm});
            skArc(sketch, "E165.2.1", {"start": v(12.71, 25.35) * mm, "mid": v(12.47, 25.16) * mm, "end": v(12.37, 24.87) * mm});
            skArc(sketch, "E165.2.2", {"start": v(13.24, 24.08) * mm, "mid": v(13.7, 24.25) * mm, "end": v(14.15, 24.4) * mm});
            skPoint(sketch, "E165.2.3", {"position": v(13, 24.66) * mm});
            skArc(sketch, "E165.2.4", {"start": v(13.3, 25.25) * mm, "mid": v(13.4, 25.14) * mm, "end": v(13.5, 25) * mm});
            skLineSegment(sketch, "E165.2.5", {"start": v(12.37, 23.66) * mm, "end": v(12.06, 24.24) * mm});
            skArc(sketch, "E165.2.6", {"start": v(13.67, 24.94) * mm, "mid": v(13.82, 24.98) * mm, "end": v(13.96, 25.03) * mm});
            skLineSegment(sketch, "E165.2.7", {"start": v(14.15, 24.4) * mm, "end": v(13.96, 25.03) * mm});
            skArc(sketch, "E165.2.8", {"start": v(12.71, 25.35) * mm, "mid": v(13.02, 25.39) * mm, "end": v(13.3, 25.25) * mm});
            skPoint(sketch, "E165.2.9", {"position": v(13.24, 24.08) * mm});
            skArc(sketch, "E165.2.10", {"start": v(13.1, 24.42) * mm, "mid": v(13.56, 24.6) * mm, "end": v(14.04, 24.76) * mm, "construction": true});
            skArc(sketch, "E165.2.11", {"start": v(13.24, 24.08) * mm, "mid": v(12.8, 23.88) * mm, "end": v(12.37, 23.66) * mm});
            skPoint(sketch, "E165.2.12", {"position": v(13.1, 24.42) * mm});
            skArc(sketch, "E165.2.13", {"start": v(12.33, 24.38) * mm, "mid": v(12.2, 24.31) * mm, "end": v(12.06, 24.24) * mm});
            skArc(sketch, "E165.2.14", {"start": v(13.5, 25) * mm, "mid": v(13.57, 24.94) * mm, "end": v(13.67, 24.94) * mm});
            skArc(sketch, "E165.2.15", {"start": v(12.4, 24.55) * mm, "mid": v(12.4, 24.45) * mm, "end": v(12.33, 24.38) * mm});
            skArc(sketch, "E165.3.0", {"start": v(10.53, 23.78) * mm, "mid": v(10.57, 23.62) * mm, "end": v(10.63, 23.47) * mm});
            skArc(sketch, "E165.3.1", {"start": v(10.78, 24.32) * mm, "mid": v(10.58, 24.08) * mm, "end": v(10.53, 23.78) * mm});
            skArc(sketch, "E165.3.2", {"start": v(11.54, 23.17) * mm, "mid": v(11.95, 23.43) * mm, "end": v(12.37, 23.66) * mm});
            skPoint(sketch, "E165.3.3", {"position": v(11.2, 23.7) * mm});
            skArc(sketch, "E165.3.4", {"start": v(11.36, 24.33) * mm, "mid": v(11.5, 24.24) * mm, "end": v(11.61, 24.13) * mm});
            skLineSegment(sketch, "E165.3.5", {"start": v(10.77, 22.6) * mm, "end": v(10.35, 23.1) * mm});
            skArc(sketch, "E165.3.6", {"start": v(11.8, 24.1) * mm, "mid": v(11.93, 24.17) * mm, "end": v(12.06, 24.24) * mm});
            skLineSegment(sketch, "E165.3.7", {"start": v(12.37, 23.66) * mm, "end": v(12.06, 24.24) * mm});
            skArc(sketch, "E165.3.8", {"start": v(10.78, 24.32) * mm, "mid": v(11.07, 24.4) * mm, "end": v(11.36, 24.33) * mm});
            skPoint(sketch, "E165.3.9", {"position": v(11.54, 23.17) * mm});
            skArc(sketch, "E165.3.10", {"start": v(11.33, 23.48) * mm, "mid": v(11.76, 23.75) * mm, "end": v(12.2, 24) * mm, "construction": true});
            skArc(sketch, "E165.3.11", {"start": v(11.54, 23.17) * mm, "mid": v(11.15, 22.9) * mm, "end": v(10.77, 22.6) * mm});
            skPoint(sketch, "E165.3.12", {"position": v(11.33, 23.48) * mm});
            skArc(sketch, "E165.3.13", {"start": v(10.59, 23.29) * mm, "mid": v(10.47, 23.2) * mm, "end": v(10.35, 23.1) * mm});
            skArc(sketch, "E165.3.14", {"start": v(11.61, 24.13) * mm, "mid": v(11.7, 24.08) * mm, "end": v(11.8, 24.1) * mm});
            skArc(sketch, "E165.3.15", {"start": v(10.63, 23.47) * mm, "mid": v(10.64, 23.37) * mm, "end": v(10.59, 23.29) * mm});
            skArc(sketch, "E165.4.0", {"start": v(8.95, 22.35) * mm, "mid": v(9, 22.2) * mm, "end": v(9.1, 22.07) * mm});
            skArc(sketch, "E165.4.1", {"start": v(9.08, 22.92) * mm, "mid": v(8.93, 22.65) * mm, "end": v(8.95, 22.35) * mm});
            skArc(sketch, "E165.4.2", {"start": v(10.05, 21.95) * mm, "mid": v(10.4, 22.28) * mm, "end": v(10.77, 22.6) * mm});
            skPoint(sketch, "E165.4.3", {"position": v(9.6, 22.4) * mm});
            skArc(sketch, "E165.4.4", {"start": v(9.65, 23.05) * mm, "mid": v(9.8, 23) * mm, "end": v(9.93, 22.9) * mm});
            skLineSegment(sketch, "E165.4.5", {"start": v(9.4, 21.23) * mm, "end": v(8.9, 21.65) * mm});
            skArc(sketch, "E165.4.6", {"start": v(10.12, 22.9) * mm, "mid": v(10.24, 23) * mm, "end": v(10.35, 23.1) * mm});
            skLineSegment(sketch, "E165.4.7", {"start": v(10.77, 22.6) * mm, "end": v(10.35, 23.1) * mm});
            skArc(sketch, "E165.4.8", {"start": v(9.08, 22.92) * mm, "mid": v(9.35, 23.07) * mm, "end": v(9.65, 23.05) * mm});
            skPoint(sketch, "E165.4.9", {"position": v(10.05, 21.95) * mm});
            skArc(sketch, "E165.4.10", {"start": v(9.79, 22.21) * mm, "mid": v(10.15, 22.56) * mm, "end": v(10.53, 22.88) * mm, "construction": true});
            skArc(sketch, "E165.4.11", {"start": v(10.05, 21.95) * mm, "mid": v(9.72, 21.6) * mm, "end": v(9.4, 21.23) * mm});
            skPoint(sketch, "E165.4.12", {"position": v(9.79, 22.21) * mm});
            skArc(sketch, "E165.4.13", {"start": v(9.1, 21.88) * mm, "mid": v(9, 21.76) * mm, "end": v(8.9, 21.65) * mm});
            skArc(sketch, "E165.4.14", {"start": v(9.93, 22.9) * mm, "mid": v(10.03, 22.87) * mm, "end": v(10.12, 22.9) * mm});
            skArc(sketch, "E165.4.15", {"start": v(9.1, 22.07) * mm, "mid": v(9.13, 21.97) * mm, "end": v(9.1, 21.88) * mm});
            skArc(sketch, "E165.5.0", {"start": v(7.67, 20.64) * mm, "mid": v(7.76, 20.5) * mm, "end": v(7.87, 20.39) * mm});
            skArc(sketch, "E165.5.1", {"start": v(7.68, 21.22) * mm, "mid": v(7.6, 20.93) * mm, "end": v(7.67, 20.64) * mm});
            skArc(sketch, "E165.5.2", {"start": v(8.83, 20.46) * mm, "mid": v(9.1, 20.85) * mm, "end": v(9.4, 21.23) * mm});
            skPoint(sketch, "E165.5.3", {"position": v(8.3, 20.8) * mm});
            skArc(sketch, "E165.5.4", {"start": v(8.22, 21.47) * mm, "mid": v(8.38, 21.43) * mm, "end": v(8.53, 21.37) * mm});
            skLineSegment(sketch, "E165.5.5", {"start": v(8.34, 19.63) * mm, "end": v(7.76, 19.94) * mm});
            skArc(sketch, "E165.5.6", {"start": v(8.71, 21.41) * mm, "mid": v(8.8, 21.53) * mm, "end": v(8.9, 21.65) * mm});
            skLineSegment(sketch, "E165.5.7", {"start": v(9.4, 21.23) * mm, "end": v(8.9, 21.65) * mm});
            skArc(sketch, "E165.5.8", {"start": v(7.68, 21.22) * mm, "mid": v(7.92, 21.42) * mm, "end": v(8.22, 21.47) * mm});
            skPoint(sketch, "E165.5.9", {"position": v(8.83, 20.46) * mm});
            skArc(sketch, "E165.5.10", {"start": v(8.52, 20.67) * mm, "mid": v(8.8, 21.08) * mm, "end": v(9.12, 21.47) * mm, "construction": true});
            skArc(sketch, "E165.5.11", {"start": v(8.83, 20.46) * mm, "mid": v(8.57, 20.05) * mm, "end": v(8.34, 19.63) * mm});
            skPoint(sketch, "E165.5.12", {"position": v(8.52, 20.67) * mm});
            skArc(sketch, "E165.5.13", {"start": v(7.9, 20.2) * mm, "mid": v(7.83, 20.07) * mm, "end": v(7.76, 19.94) * mm});
            skArc(sketch, "E165.5.14", {"start": v(8.53, 21.37) * mm, "mid": v(8.63, 21.36) * mm, "end": v(8.71, 21.41) * mm});
            skArc(sketch, "E165.5.15", {"start": v(7.87, 20.39) * mm, "mid": v(7.92, 20.3) * mm, "end": v(7.9, 20.2) * mm});
            skArc(sketch, "E165.6.0", {"start": v(6.75, 18.7) * mm, "mid": v(6.86, 18.6) * mm, "end": v(7, 18.5) * mm});
            skArc(sketch, "E165.6.1", {"start": v(6.65, 19.29) * mm, "mid": v(6.61, 18.98) * mm, "end": v(6.75, 18.7) * mm});
            skArc(sketch, "E165.6.2", {"start": v(7.92, 18.76) * mm, "mid": v(8.12, 19.2) * mm, "end": v(8.34, 19.63) * mm});
            skPoint(sketch, "E165.6.3", {"position": v(7.34, 19) * mm});
            skArc(sketch, "E165.6.4", {"start": v(7.13, 19.63) * mm, "mid": v(7.29, 19.63) * mm, "end": v(7.45, 19.6) * mm});
            skLineSegment(sketch, "E165.6.5", {"start": v(7.6, 17.85) * mm, "end": v(6.97, 18.04) * mm});
            skArc(sketch, "E165.6.6", {"start": v(7.62, 19.67) * mm, "mid": v(7.69, 19.8) * mm, "end": v(7.76, 19.94) * mm});
            skLineSegment(sketch, "E165.6.7", {"start": v(8.34, 19.63) * mm, "end": v(7.76, 19.94) * mm});
            skArc(sketch, "E165.6.8", {"start": v(6.65, 19.29) * mm, "mid": v(6.84, 19.53) * mm, "end": v(7.13, 19.63) * mm});
            skPoint(sketch, "E165.6.9", {"position": v(7.92, 18.76) * mm});
            skArc(sketch, "E165.6.10", {"start": v(7.58, 18.9) * mm, "mid": v(7.78, 19.36) * mm, "end": v(8, 19.8) * mm, "construction": true});
            skArc(sketch, "E165.6.11", {"start": v(7.92, 18.76) * mm, "mid": v(7.75, 18.3) * mm, "end": v(7.6, 17.85) * mm});
            skPoint(sketch, "E165.6.12", {"position": v(7.58, 18.9) * mm});
            skArc(sketch, "E165.6.13", {"start": v(7.06, 18.33) * mm, "mid": v(7.02, 18.18) * mm, "end": v(6.97, 18.04) * mm});
            skArc(sketch, "E165.6.14", {"start": v(7.45, 19.6) * mm, "mid": v(7.55, 19.6) * mm, "end": v(7.62, 19.67) * mm});
            skArc(sketch, "E165.6.15", {"start": v(7, 18.5) * mm, "mid": v(7.06, 18.43) * mm, "end": v(7.06, 18.33) * mm});
            skArc(sketch, "E165.7.0", {"start": v(6.22, 16.64) * mm, "mid": v(6.36, 16.55) * mm, "end": v(6.5, 16.48) * mm});
            skArc(sketch, "E165.7.1", {"start": v(6.01, 17.19) * mm, "mid": v(6.04, 16.88) * mm, "end": v(6.22, 16.64) * mm});
            skArc(sketch, "E165.7.2", {"start": v(7.36, 16.92) * mm, "mid": v(7.47, 17.39) * mm, "end": v(7.6, 17.85) * mm});
            skPoint(sketch, "E165.7.3", {"position": v(6.75, 17.04) * mm});
            skArc(sketch, "E165.7.4", {"start": v(6.41, 17.61) * mm, "mid": v(6.57, 17.64) * mm, "end": v(6.73, 17.64) * mm});
            skLineSegment(sketch, "E165.7.5", {"start": v(7.22, 15.96) * mm, "end": v(6.57, 16.03) * mm});
            skArc(sketch, "E165.7.6", {"start": v(6.89, 17.76) * mm, "mid": v(6.93, 17.9) * mm, "end": v(6.97, 18.04) * mm});
            skLineSegment(sketch, "E165.7.7", {"start": v(7.6, 17.85) * mm, "end": v(6.97, 18.04) * mm});
            skArc(sketch, "E165.7.8", {"start": v(6.01, 17.19) * mm, "mid": v(6.15, 17.46) * mm, "end": v(6.41, 17.61) * mm});
            skPoint(sketch, "E165.7.9", {"position": v(7.36, 16.92) * mm});
            skArc(sketch, "E165.7.10", {"start": v(7, 16.99) * mm, "mid": v(7.1, 17.48) * mm, "end": v(7.24, 17.96) * mm, "construction": true});
            skArc(sketch, "E165.7.11", {"start": v(7.36, 16.92) * mm, "mid": v(7.28, 16.44) * mm, "end": v(7.22, 15.96) * mm});
            skPoint(sketch, "E165.7.12", {"position": v(7, 16.99) * mm});
            skArc(sketch, "E165.7.13", {"start": v(6.6, 16.32) * mm, "mid": v(6.59, 16.18) * mm, "end": v(6.57, 16.03) * mm});
            skArc(sketch, "E165.7.14", {"start": v(6.73, 17.64) * mm, "mid": v(6.83, 17.67) * mm, "end": v(6.89, 17.76) * mm});
            skArc(sketch, "E165.7.15", {"start": v(6.5, 16.48) * mm, "mid": v(6.58, 16.42) * mm, "end": v(6.6, 16.32) * mm});
            skArc(sketch, "E165.8.0", {"start": v(6.1, 14.5) * mm, "mid": v(6.26, 14.44) * mm, "end": v(6.42, 14.4) * mm});
            skArc(sketch, "E165.8.1", {"start": v(5.8, 15) * mm, "mid": v(5.88, 14.7) * mm, "end": v(6.1, 14.5) * mm});
            skArc(sketch, "E165.8.2", {"start": v(7.18, 15) * mm, "mid": v(7.19, 15.48) * mm, "end": v(7.22, 15.96) * mm});
            skPoint(sketch, "E165.8.3", {"position": v(6.55, 15) * mm});
            skArc(sketch, "E165.8.4", {"start": v(6.1, 15.5) * mm, "mid": v(6.26, 15.56) * mm, "end": v(6.42, 15.6) * mm});
            skLineSegment(sketch, "E165.8.5", {"start": v(7.22, 14.04) * mm, "end": v(6.57, 13.97) * mm});
            skArc(sketch, "E165.8.6", {"start": v(6.55, 15.73) * mm, "mid": v(6.56, 15.88) * mm, "end": v(6.57, 16.03) * mm});
            skLineSegment(sketch, "E165.8.7", {"start": v(7.22, 15.96) * mm, "end": v(6.57, 16.03) * mm});
            skArc(sketch, "E165.8.8", {"start": v(5.8, 15) * mm, "mid": v(5.88, 15.3) * mm, "end": v(6.1, 15.5) * mm});
            skPoint(sketch, "E165.8.9", {"position": v(7.18, 15) * mm});
            skArc(sketch, "E165.8.10", {"start": v(6.8, 15) * mm, "mid": v(6.81, 15.5) * mm, "end": v(6.85, 16) * mm, "construction": true});
            skArc(sketch, "E165.8.11", {"start": v(7.18, 15) * mm, "mid": v(7.19, 14.52) * mm, "end": v(7.22, 14.04) * mm});
            skPoint(sketch, "E165.8.12", {"position": v(6.8, 15) * mm});
            skArc(sketch, "E165.8.13", {"start": v(6.55, 14.27) * mm, "mid": v(6.56, 14.12) * mm, "end": v(6.57, 13.97) * mm});
            skArc(sketch, "E165.8.14", {"start": v(6.42, 15.6) * mm, "mid": v(6.5, 15.64) * mm, "end": v(6.55, 15.73) * mm});
            skArc(sketch, "E165.8.15", {"start": v(6.42, 14.4) * mm, "mid": v(6.5, 14.36) * mm, "end": v(6.55, 14.27) * mm});
            skArc(sketch, "E165.9.0", {"start": v(6.41, 12.39) * mm, "mid": v(6.57, 12.36) * mm, "end": v(6.73, 12.36) * mm});
            skArc(sketch, "E165.9.1", {"start": v(6.01, 12.81) * mm, "mid": v(6.15, 12.54) * mm, "end": v(6.41, 12.39) * mm});
            skArc(sketch, "E165.9.2", {"start": v(7.36, 13.08) * mm, "mid": v(7.28, 13.56) * mm, "end": v(7.22, 14.04) * mm});
            skPoint(sketch, "E165.9.3", {"position": v(6.75, 12.96) * mm});
            skArc(sketch, "E165.9.4", {"start": v(6.22, 13.36) * mm, "mid": v(6.36, 13.45) * mm, "end": v(6.5, 13.52) * mm});
            skLineSegment(sketch, "E165.9.5", {"start": v(7.6, 12.15) * mm, "end": v(6.97, 11.96) * mm});
            skArc(sketch, "E165.9.6", {"start": v(6.6, 13.68) * mm, "mid": v(6.59, 13.82) * mm, "end": v(6.57, 13.97) * mm});
            skLineSegment(sketch, "E165.9.7", {"start": v(7.22, 14.04) * mm, "end": v(6.57, 13.97) * mm});
            skArc(sketch, "E165.9.8", {"start": v(6.01, 12.81) * mm, "mid": v(6.04, 13.12) * mm, "end": v(6.22, 13.36) * mm});
            skPoint(sketch, "E165.9.9", {"position": v(7.36, 13.08) * mm});
            skArc(sketch, "E165.9.10", {"start": v(7, 13.01) * mm, "mid": v(6.91, 13.5) * mm, "end": v(6.85, 14) * mm, "construction": true});
            skArc(sketch, "E165.9.11", {"start": v(7.36, 13.08) * mm, "mid": v(7.47, 12.61) * mm, "end": v(7.6, 12.15) * mm});
            skPoint(sketch, "E165.9.12", {"position": v(7, 13.01) * mm});
            skArc(sketch, "E165.9.13", {"start": v(6.89, 12.24) * mm, "mid": v(6.93, 12.1) * mm, "end": v(6.97, 11.96) * mm});
            skArc(sketch, "E165.9.14", {"start": v(6.5, 13.52) * mm, "mid": v(6.58, 13.58) * mm, "end": v(6.6, 13.68) * mm});
            skArc(sketch, "E165.9.15", {"start": v(6.73, 12.36) * mm, "mid": v(6.83, 12.33) * mm, "end": v(6.89, 12.24) * mm});
            skArc(sketch, "E165.10.0", {"start": v(7.13, 10.37) * mm, "mid": v(7.29, 10.37) * mm, "end": v(7.45, 10.4) * mm});
            skArc(sketch, "E165.10.1", {"start": v(6.65, 10.71) * mm, "mid": v(6.84, 10.47) * mm, "end": v(7.13, 10.37) * mm});
            skArc(sketch, "E165.10.2", {"start": v(7.92, 11.24) * mm, "mid": v(7.75, 11.7) * mm, "end": v(7.6, 12.15) * mm});
            skPoint(sketch, "E165.10.3", {"position": v(7.34, 11) * mm});
            skArc(sketch, "E165.10.4", {"start": v(6.75, 11.3) * mm, "mid": v(6.86, 11.4) * mm, "end": v(7, 11.5) * mm});
            skLineSegment(sketch, "E165.10.5", {"start": v(8.34, 10.37) * mm, "end": v(7.76, 10.06) * mm});
            skArc(sketch, "E165.10.6", {"start": v(7.06, 11.67) * mm, "mid": v(7.02, 11.82) * mm, "end": v(6.97, 11.96) * mm});
            skLineSegment(sketch, "E165.10.7", {"start": v(7.6, 12.15) * mm, "end": v(6.97, 11.96) * mm});
            skArc(sketch, "E165.10.8", {"start": v(6.65, 10.71) * mm, "mid": v(6.61, 11.02) * mm, "end": v(6.75, 11.3) * mm});
            skPoint(sketch, "E165.10.9", {"position": v(7.92, 11.24) * mm});
            skArc(sketch, "E165.10.10", {"start": v(7.58, 11.1) * mm, "mid": v(7.4, 11.56) * mm, "end": v(7.24, 12.04) * mm, "construction": true});
            skArc(sketch, "E165.10.11", {"start": v(7.92, 11.24) * mm, "mid": v(8.12, 10.8) * mm, "end": v(8.34, 10.37) * mm});
            skPoint(sketch, "E165.10.12", {"position": v(7.58, 11.1) * mm});
            skArc(sketch, "E165.10.13", {"start": v(7.62, 10.33) * mm, "mid": v(7.69, 10.2) * mm, "end": v(7.76, 10.06) * mm});
            skArc(sketch, "E165.10.14", {"start": v(7, 11.5) * mm, "mid": v(7.06, 11.57) * mm, "end": v(7.06, 11.67) * mm});
            skArc(sketch, "E165.10.15", {"start": v(7.45, 10.4) * mm, "mid": v(7.55, 10.4) * mm, "end": v(7.62, 10.33) * mm});
            skArc(sketch, "E165.11.0", {"start": v(8.22, 8.53) * mm, "mid": v(8.38, 8.57) * mm, "end": v(8.53, 8.63) * mm});
            skArc(sketch, "E165.11.1", {"start": v(7.68, 8.78) * mm, "mid": v(7.92, 8.58) * mm, "end": v(8.22, 8.53) * mm});
            skArc(sketch, "E165.11.2", {"start": v(8.83, 9.54) * mm, "mid": v(8.57, 9.95) * mm, "end": v(8.34, 10.37) * mm});
            skPoint(sketch, "E165.11.3", {"position": v(8.3, 9.2) * mm});
            skArc(sketch, "E165.11.4", {"start": v(7.67, 9.36) * mm, "mid": v(7.76, 9.5) * mm, "end": v(7.87, 9.61) * mm});
            skLineSegment(sketch, "E165.11.5", {"start": v(9.4, 8.77) * mm, "end": v(8.9, 8.35) * mm});
            skArc(sketch, "E165.11.6", {"start": v(7.9, 9.8) * mm, "mid": v(7.83, 9.93) * mm, "end": v(7.76, 10.06) * mm});
            skLineSegment(sketch, "E165.11.7", {"start": v(8.34, 10.37) * mm, "end": v(7.76, 10.06) * mm});
            skArc(sketch, "E165.11.8", {"start": v(7.68, 8.78) * mm, "mid": v(7.6, 9.07) * mm, "end": v(7.67, 9.36) * mm});
            skPoint(sketch, "E165.11.9", {"position": v(8.83, 9.54) * mm});
            skArc(sketch, "E165.11.10", {"start": v(8.52, 9.33) * mm, "mid": v(8.25, 9.76) * mm, "end": v(8, 10.2) * mm, "construction": true});
            skArc(sketch, "E165.11.11", {"start": v(8.83, 9.54) * mm, "mid": v(9.1, 9.15) * mm, "end": v(9.4, 8.77) * mm});
            skPoint(sketch, "E165.11.12", {"position": v(8.52, 9.33) * mm});
            skArc(sketch, "E165.11.13", {"start": v(8.71, 8.59) * mm, "mid": v(8.8, 8.47) * mm, "end": v(8.9, 8.35) * mm});
            skArc(sketch, "E165.11.14", {"start": v(7.87, 9.61) * mm, "mid": v(7.92, 9.7) * mm, "end": v(7.9, 9.8) * mm});
            skArc(sketch, "E165.11.15", {"start": v(8.53, 8.63) * mm, "mid": v(8.63, 8.64) * mm, "end": v(8.71, 8.59) * mm});
            skArc(sketch, "E165.12.0", {"start": v(9.65, 6.95) * mm, "mid": v(9.8, 7) * mm, "end": v(9.93, 7.1) * mm});
            skArc(sketch, "E165.12.1", {"start": v(9.08, 7.08) * mm, "mid": v(9.35, 6.93) * mm, "end": v(9.65, 6.95) * mm});
            skArc(sketch, "E165.12.2", {"start": v(10.05, 8.05) * mm, "mid": v(9.72, 8.4) * mm, "end": v(9.4, 8.77) * mm});
            skPoint(sketch, "E165.12.3", {"position": v(9.6, 7.6) * mm});
            skArc(sketch, "E165.12.4", {"start": v(8.95, 7.65) * mm, "mid": v(9, 7.8) * mm, "end": v(9.1, 7.93) * mm});
            skLineSegment(sketch, "E165.12.5", {"start": v(10.77, 7.4) * mm, "end": v(10.35, 6.9) * mm});
            skArc(sketch, "E165.12.6", {"start": v(9.1, 8.12) * mm, "mid": v(9, 8.24) * mm, "end": v(8.9, 8.35) * mm});
            skLineSegment(sketch, "E165.12.7", {"start": v(9.4, 8.77) * mm, "end": v(8.9, 8.35) * mm});
            skArc(sketch, "E165.12.8", {"start": v(9.08, 7.08) * mm, "mid": v(8.93, 7.35) * mm, "end": v(8.95, 7.65) * mm});
            skPoint(sketch, "E165.12.9", {"position": v(10.05, 8.05) * mm});
            skArc(sketch, "E165.12.10", {"start": v(9.79, 7.79) * mm, "mid": v(9.44, 8.15) * mm, "end": v(9.12, 8.53) * mm, "construction": true});
            skArc(sketch, "E165.12.11", {"start": v(10.05, 8.05) * mm, "mid": v(10.4, 7.72) * mm, "end": v(10.77, 7.4) * mm});
            skPoint(sketch, "E165.12.12", {"position": v(9.79, 7.79) * mm});
            skArc(sketch, "E165.12.13", {"start": v(10.12, 7.1) * mm, "mid": v(10.24, 7) * mm, "end": v(10.35, 6.9) * mm});
            skArc(sketch, "E165.12.14", {"start": v(9.1, 7.93) * mm, "mid": v(9.13, 8.03) * mm, "end": v(9.1, 8.12) * mm});
            skArc(sketch, "E165.12.15", {"start": v(9.93, 7.1) * mm, "mid": v(10.03, 7.13) * mm, "end": v(10.12, 7.1) * mm});
            skArc(sketch, "E165.13.0", {"start": v(11.36, 5.67) * mm, "mid": v(11.5, 5.76) * mm, "end": v(11.61, 5.87) * mm});
            skArc(sketch, "E165.13.1", {"start": v(10.78, 5.68) * mm, "mid": v(11.07, 5.6) * mm, "end": v(11.36, 5.67) * mm});
            skArc(sketch, "E165.13.2", {"start": v(11.54, 6.83) * mm, "mid": v(11.15, 7.1) * mm, "end": v(10.77, 7.4) * mm});
            skPoint(sketch, "E165.13.3", {"position": v(11.2, 6.3) * mm});
            skArc(sketch, "E165.13.4", {"start": v(10.53, 6.22) * mm, "mid": v(10.57, 6.38) * mm, "end": v(10.63, 6.53) * mm});
            skLineSegment(sketch, "E165.13.5", {"start": v(12.37, 6.34) * mm, "end": v(12.06, 5.76) * mm});
            skArc(sketch, "E165.13.6", {"start": v(10.59, 6.71) * mm, "mid": v(10.47, 6.8) * mm, "end": v(10.35, 6.9) * mm});
            skLineSegment(sketch, "E165.13.7", {"start": v(10.77, 7.4) * mm, "end": v(10.35, 6.9) * mm});
            skArc(sketch, "E165.13.8", {"start": v(10.78, 5.68) * mm, "mid": v(10.58, 5.92) * mm, "end": v(10.53, 6.22) * mm});
            skPoint(sketch, "E165.13.9", {"position": v(11.54, 6.83) * mm});
            skArc(sketch, "E165.13.10", {"start": v(11.33, 6.52) * mm, "mid": v(10.92, 6.8) * mm, "end": v(10.53, 7.12) * mm, "construction": true});
            skArc(sketch, "E165.13.11", {"start": v(11.54, 6.83) * mm, "mid": v(11.95, 6.57) * mm, "end": v(12.37, 6.34) * mm});
            skPoint(sketch, "E165.13.12", {"position": v(11.33, 6.52) * mm});
            skArc(sketch, "E165.13.13", {"start": v(11.8, 5.9) * mm, "mid": v(11.93, 5.83) * mm, "end": v(12.06, 5.76) * mm});
            skArc(sketch, "E165.13.14", {"start": v(10.63, 6.53) * mm, "mid": v(10.64, 6.63) * mm, "end": v(10.59, 6.71) * mm});
            skArc(sketch, "E165.13.15", {"start": v(11.61, 5.87) * mm, "mid": v(11.7, 5.92) * mm, "end": v(11.8, 5.9) * mm});
            skArc(sketch, "E165.14.0", {"start": v(13.3, 4.75) * mm, "mid": v(13.4, 4.86) * mm, "end": v(13.5, 5) * mm});
            skArc(sketch, "E165.14.1", {"start": v(12.71, 4.65) * mm, "mid": v(13.02, 4.61) * mm, "end": v(13.3, 4.75) * mm});
            skArc(sketch, "E165.14.2", {"start": v(13.24, 5.92) * mm, "mid": v(12.8, 6.12) * mm, "end": v(12.37, 6.34) * mm});
            skPoint(sketch, "E165.14.3", {"position": v(13, 5.34) * mm});
            skArc(sketch, "E165.14.4", {"start": v(12.37, 5.13) * mm, "mid": v(12.37, 5.29) * mm, "end": v(12.4, 5.45) * mm});
            skLineSegment(sketch, "E165.14.5", {"start": v(14.15, 5.6) * mm, "end": v(13.96, 4.97) * mm});
            skArc(sketch, "E165.14.6", {"start": v(12.33, 5.62) * mm, "mid": v(12.2, 5.69) * mm, "end": v(12.06, 5.76) * mm});
            skLineSegment(sketch, "E165.14.7", {"start": v(12.37, 6.34) * mm, "end": v(12.06, 5.76) * mm});
            skArc(sketch, "E165.14.8", {"start": v(12.71, 4.65) * mm, "mid": v(12.47, 4.84) * mm, "end": v(12.37, 5.13) * mm});
            skPoint(sketch, "E165.14.9", {"position": v(13.24, 5.92) * mm});
            skArc(sketch, "E165.14.10", {"start": v(13.1, 5.58) * mm, "mid": v(12.64, 5.78) * mm, "end": v(12.2, 6) * mm, "construction": true});
            skArc(sketch, "E165.14.11", {"start": v(13.24, 5.92) * mm, "mid": v(13.7, 5.75) * mm, "end": v(14.15, 5.6) * mm});
            skPoint(sketch, "E165.14.12", {"position": v(13.1, 5.58) * mm});
            skArc(sketch, "E165.14.13", {"start": v(13.67, 5.06) * mm, "mid": v(13.82, 5.02) * mm, "end": v(13.96, 4.97) * mm});
            skArc(sketch, "E165.14.14", {"start": v(12.4, 5.45) * mm, "mid": v(12.4, 5.55) * mm, "end": v(12.33, 5.62) * mm});
            skArc(sketch, "E165.14.15", {"start": v(13.5, 5) * mm, "mid": v(13.57, 5.06) * mm, "end": v(13.67, 5.06) * mm});
            skArc(sketch, "E165.15.0", {"start": v(15.36, 4.22) * mm, "mid": v(15.45, 4.36) * mm, "end": v(15.52, 4.5) * mm});
            skArc(sketch, "E165.15.1", {"start": v(14.81, 4.01) * mm, "mid": v(15.12, 4.04) * mm, "end": v(15.36, 4.22) * mm});
            skArc(sketch, "E165.15.2", {"start": v(15.08, 5.36) * mm, "mid": v(14.61, 5.47) * mm, "end": v(14.15, 5.6) * mm});
            skPoint(sketch, "E165.15.3", {"position": v(14.96, 4.75) * mm});
            skArc(sketch, "E165.15.4", {"start": v(14.39, 4.41) * mm, "mid": v(14.36, 4.57) * mm, "end": v(14.36, 4.73) * mm});
            skLineSegment(sketch, "E165.15.5", {"start": v(16.04, 5.22) * mm, "end": v(15.97, 4.57) * mm});
            skArc(sketch, "E165.15.6", {"start": v(14.24, 4.89) * mm, "mid": v(14.1, 4.93) * mm, "end": v(13.96, 4.97) * mm});
            skLineSegment(sketch, "E165.15.7", {"start": v(14.15, 5.6) * mm, "end": v(13.96, 4.97) * mm});
            skArc(sketch, "E165.15.8", {"start": v(14.81, 4.01) * mm, "mid": v(14.54, 4.15) * mm, "end": v(14.39, 4.41) * mm});
            skPoint(sketch, "E165.15.9", {"position": v(15.08, 5.36) * mm});
            skArc(sketch, "E165.15.10", {"start": v(15.01, 5) * mm, "mid": v(14.52, 5.1) * mm, "end": v(14.04, 5.24) * mm, "construction": true});
            skArc(sketch, "E165.15.11", {"start": v(15.08, 5.36) * mm, "mid": v(15.56, 5.28) * mm, "end": v(16.04, 5.22) * mm});
            skPoint(sketch, "E165.15.12", {"position": v(15.01, 5) * mm});
            skArc(sketch, "E165.15.13", {"start": v(15.68, 4.6) * mm, "mid": v(15.82, 4.59) * mm, "end": v(15.97, 4.57) * mm});
            skArc(sketch, "E165.15.14", {"start": v(14.36, 4.73) * mm, "mid": v(14.33, 4.83) * mm, "end": v(14.24, 4.89) * mm});
            skArc(sketch, "E165.15.15", {"start": v(15.52, 4.5) * mm, "mid": v(15.58, 4.58) * mm, "end": v(15.68, 4.6) * mm});
            skArc(sketch, "E165.16.0", {"start": v(17.5, 4.1) * mm, "mid": v(17.56, 4.26) * mm, "end": v(17.6, 4.42) * mm});
            skArc(sketch, "E165.16.1", {"start": v(17, 3.8) * mm, "mid": v(17.3, 3.88) * mm, "end": v(17.5, 4.1) * mm});
            skArc(sketch, "E165.16.2", {"start": v(17, 5.18) * mm, "mid": v(16.52, 5.19) * mm, "end": v(16.04, 5.22) * mm});
            skPoint(sketch, "E165.16.3", {"position": v(17, 4.55) * mm});
            skArc(sketch, "E165.16.4", {"start": v(16.5, 4.1) * mm, "mid": v(16.44, 4.26) * mm, "end": v(16.4, 4.42) * mm});
            skLineSegment(sketch, "E165.16.5", {"start": v(17.96, 5.22) * mm, "end": v(18.03, 4.57) * mm});
            skArc(sketch, "E165.16.6", {"start": v(16.27, 4.55) * mm, "mid": v(16.12, 4.56) * mm, "end": v(15.97, 4.57) * mm});
            skLineSegment(sketch, "E165.16.7", {"start": v(16.04, 5.22) * mm, "end": v(15.97, 4.57) * mm});
            skArc(sketch, "E165.16.8", {"start": v(17, 3.8) * mm, "mid": v(16.7, 3.88) * mm, "end": v(16.5, 4.1) * mm});
            skPoint(sketch, "E165.16.9", {"position": v(17, 5.18) * mm});
            skArc(sketch, "E165.16.10", {"start": v(17, 4.8) * mm, "mid": v(16.5, 4.81) * mm, "end": v(16, 4.85) * mm, "construction": true});
            skArc(sketch, "E165.16.11", {"start": v(17, 5.18) * mm, "mid": v(17.48, 5.19) * mm, "end": v(17.96, 5.22) * mm});
            skPoint(sketch, "E165.16.12", {"position": v(17, 4.8) * mm});
            skArc(sketch, "E165.16.13", {"start": v(17.73, 4.55) * mm, "mid": v(17.88, 4.56) * mm, "end": v(18.03, 4.57) * mm});
            skArc(sketch, "E165.16.14", {"start": v(16.4, 4.42) * mm, "mid": v(16.36, 4.5) * mm, "end": v(16.27, 4.55) * mm});
            skArc(sketch, "E165.16.15", {"start": v(17.6, 4.42) * mm, "mid": v(17.64, 4.5) * mm, "end": v(17.73, 4.55) * mm});
            skArc(sketch, "E165.17.0", {"start": v(19.61, 4.41) * mm, "mid": v(19.64, 4.57) * mm, "end": v(19.64, 4.73) * mm});
            skArc(sketch, "E165.17.1", {"start": v(19.19, 4.01) * mm, "mid": v(19.46, 4.15) * mm, "end": v(19.61, 4.41) * mm});
            skArc(sketch, "E165.17.2", {"start": v(18.92, 5.36) * mm, "mid": v(18.44, 5.28) * mm, "end": v(17.96, 5.22) * mm});
            skPoint(sketch, "E165.17.3", {"position": v(19.04, 4.75) * mm});
            skArc(sketch, "E165.17.4", {"start": v(18.64, 4.22) * mm, "mid": v(18.55, 4.36) * mm, "end": v(18.48, 4.5) * mm});
            skLineSegment(sketch, "E165.17.5", {"start": v(19.85, 5.6) * mm, "end": v(20.04, 4.97) * mm});
            skArc(sketch, "E165.17.6", {"start": v(18.32, 4.6) * mm, "mid": v(18.18, 4.59) * mm, "end": v(18.03, 4.57) * mm});
            skLineSegment(sketch, "E165.17.7", {"start": v(17.96, 5.22) * mm, "end": v(18.03, 4.57) * mm});
            skArc(sketch, "E165.17.8", {"start": v(19.19, 4.01) * mm, "mid": v(18.88, 4.04) * mm, "end": v(18.64, 4.22) * mm});
            skPoint(sketch, "E165.17.9", {"position": v(18.92, 5.36) * mm});
            skArc(sketch, "E165.17.10", {"start": v(18.99, 5) * mm, "mid": v(18.5, 4.91) * mm, "end": v(18, 4.85) * mm, "construction": true});
            skArc(sketch, "E165.17.11", {"start": v(18.92, 5.36) * mm, "mid": v(19.39, 5.47) * mm, "end": v(19.85, 5.6) * mm});
            skPoint(sketch, "E165.17.12", {"position": v(18.99, 5) * mm});
            skArc(sketch, "E165.17.13", {"start": v(19.76, 4.89) * mm, "mid": v(19.9, 4.93) * mm, "end": v(20.04, 4.97) * mm});
            skArc(sketch, "E165.17.14", {"start": v(18.48, 4.5) * mm, "mid": v(18.42, 4.58) * mm, "end": v(18.32, 4.6) * mm});
            skArc(sketch, "E165.17.15", {"start": v(19.64, 4.73) * mm, "mid": v(19.67, 4.83) * mm, "end": v(19.76, 4.89) * mm});
            skArc(sketch, "E165.18.0", {"start": v(21.63, 5.13) * mm, "mid": v(21.63, 5.29) * mm, "end": v(21.6, 5.45) * mm});
            skArc(sketch, "E165.18.1", {"start": v(21.29, 4.65) * mm, "mid": v(21.53, 4.84) * mm, "end": v(21.63, 5.13) * mm});
            skArc(sketch, "E165.18.2", {"start": v(20.76, 5.92) * mm, "mid": v(20.3, 5.75) * mm, "end": v(19.85, 5.6) * mm});
            skPoint(sketch, "E165.18.3", {"position": v(21, 5.34) * mm});
            skArc(sketch, "E165.18.4", {"start": v(20.7, 4.75) * mm, "mid": v(20.6, 4.86) * mm, "end": v(20.5, 5) * mm});
            skLineSegment(sketch, "E165.18.5", {"start": v(21.63, 6.34) * mm, "end": v(21.94, 5.76) * mm});
            skArc(sketch, "E165.18.6", {"start": v(20.33, 5.06) * mm, "mid": v(20.18, 5.02) * mm, "end": v(20.04, 4.97) * mm});
            skLineSegment(sketch, "E165.18.7", {"start": v(19.85, 5.6) * mm, "end": v(20.04, 4.97) * mm});
            skArc(sketch, "E165.18.8", {"start": v(21.29, 4.65) * mm, "mid": v(20.98, 4.61) * mm, "end": v(20.7, 4.75) * mm});
            skPoint(sketch, "E165.18.9", {"position": v(20.76, 5.92) * mm});
            skArc(sketch, "E165.18.10", {"start": v(20.9, 5.58) * mm, "mid": v(20.44, 5.4) * mm, "end": v(19.96, 5.24) * mm, "construction": true});
            skArc(sketch, "E165.18.11", {"start": v(20.76, 5.92) * mm, "mid": v(21.2, 6.12) * mm, "end": v(21.63, 6.34) * mm});
            skPoint(sketch, "E165.18.12", {"position": v(20.9, 5.58) * mm});
            skArc(sketch, "E165.18.13", {"start": v(21.67, 5.62) * mm, "mid": v(21.8, 5.69) * mm, "end": v(21.94, 5.76) * mm});
            skArc(sketch, "E165.18.14", {"start": v(20.5, 5) * mm, "mid": v(20.43, 5.06) * mm, "end": v(20.33, 5.06) * mm});
            skArc(sketch, "E165.18.15", {"start": v(21.6, 5.45) * mm, "mid": v(21.6, 5.55) * mm, "end": v(21.67, 5.62) * mm});
            skArc(sketch, "E165.19.0", {"start": v(23.47, 6.22) * mm, "mid": v(23.43, 6.38) * mm, "end": v(23.37, 6.53) * mm});
            skArc(sketch, "E165.19.1", {"start": v(23.22, 5.68) * mm, "mid": v(23.42, 5.92) * mm, "end": v(23.47, 6.22) * mm});
            skArc(sketch, "E165.19.2", {"start": v(22.46, 6.83) * mm, "mid": v(22.05, 6.57) * mm, "end": v(21.63, 6.34) * mm});
            skPoint(sketch, "E165.19.3", {"position": v(22.8, 6.3) * mm});
            skArc(sketch, "E165.19.4", {"start": v(22.64, 5.67) * mm, "mid": v(22.5, 5.76) * mm, "end": v(22.39, 5.87) * mm});
            skLineSegment(sketch, "E165.19.5", {"start": v(23.23, 7.4) * mm, "end": v(23.65, 6.9) * mm});
            skArc(sketch, "E165.19.6", {"start": v(22.2, 5.9) * mm, "mid": v(22.07, 5.83) * mm, "end": v(21.94, 5.76) * mm});
            skLineSegment(sketch, "E165.19.7", {"start": v(21.63, 6.34) * mm, "end": v(21.94, 5.76) * mm});
            skArc(sketch, "E165.19.8", {"start": v(23.22, 5.68) * mm, "mid": v(22.93, 5.6) * mm, "end": v(22.64, 5.67) * mm});
            skPoint(sketch, "E165.19.9", {"position": v(22.46, 6.83) * mm});
            skArc(sketch, "E165.19.10", {"start": v(22.67, 6.52) * mm, "mid": v(22.24, 6.25) * mm, "end": v(21.8, 6) * mm, "construction": true});
            skArc(sketch, "E165.19.11", {"start": v(22.46, 6.83) * mm, "mid": v(22.85, 7.1) * mm, "end": v(23.23, 7.4) * mm});
            skPoint(sketch, "E165.19.12", {"position": v(22.67, 6.52) * mm});
            skArc(sketch, "E165.19.13", {"start": v(23.41, 6.71) * mm, "mid": v(23.53, 6.8) * mm, "end": v(23.65, 6.9) * mm});
            skArc(sketch, "E165.19.14", {"start": v(22.39, 5.87) * mm, "mid": v(22.3, 5.92) * mm, "end": v(22.2, 5.9) * mm});
            skArc(sketch, "E165.19.15", {"start": v(23.37, 6.53) * mm, "mid": v(23.36, 6.63) * mm, "end": v(23.41, 6.71) * mm});
            skArc(sketch, "E165.20.0", {"start": v(25.05, 7.65) * mm, "mid": v(25, 7.8) * mm, "end": v(24.9, 7.93) * mm});
            skArc(sketch, "E165.20.1", {"start": v(24.92, 7.08) * mm, "mid": v(25.07, 7.35) * mm, "end": v(25.05, 7.65) * mm});
            skArc(sketch, "E165.20.2", {"start": v(23.95, 8.05) * mm, "mid": v(23.6, 7.72) * mm, "end": v(23.23, 7.4) * mm});
            skPoint(sketch, "E165.20.3", {"position": v(24.4, 7.6) * mm});
            skArc(sketch, "E165.20.4", {"start": v(24.35, 6.95) * mm, "mid": v(24.2, 7) * mm, "end": v(24.07, 7.1) * mm});
            skLineSegment(sketch, "E165.20.5", {"start": v(24.6, 8.77) * mm, "end": v(25.1, 8.35) * mm});
            skArc(sketch, "E165.20.6", {"start": v(23.88, 7.1) * mm, "mid": v(23.76, 7) * mm, "end": v(23.65, 6.9) * mm});
            skLineSegment(sketch, "E165.20.7", {"start": v(23.23, 7.4) * mm, "end": v(23.65, 6.9) * mm});
            skArc(sketch, "E165.20.8", {"start": v(24.92, 7.08) * mm, "mid": v(24.65, 6.93) * mm, "end": v(24.35, 6.95) * mm});
            skPoint(sketch, "E165.20.9", {"position": v(23.95, 8.05) * mm});
            skArc(sketch, "E165.20.10", {"start": v(24.21, 7.79) * mm, "mid": v(23.85, 7.44) * mm, "end": v(23.47, 7.12) * mm, "construction": true});
            skArc(sketch, "E165.20.11", {"start": v(23.95, 8.05) * mm, "mid": v(24.28, 8.4) * mm, "end": v(24.6, 8.77) * mm});
            skPoint(sketch, "E165.20.12", {"position": v(24.21, 7.79) * mm});
            skArc(sketch, "E165.20.13", {"start": v(24.9, 8.12) * mm, "mid": v(25, 8.24) * mm, "end": v(25.1, 8.35) * mm});
            skArc(sketch, "E165.20.14", {"start": v(24.07, 7.1) * mm, "mid": v(23.97, 7.13) * mm, "end": v(23.88, 7.1) * mm});
            skArc(sketch, "E165.20.15", {"start": v(24.9, 7.93) * mm, "mid": v(24.87, 8.03) * mm, "end": v(24.9, 8.12) * mm});
            skArc(sketch, "E165.21.0", {"start": v(26.33, 9.36) * mm, "mid": v(26.24, 9.5) * mm, "end": v(26.13, 9.61) * mm});
            skArc(sketch, "E165.21.1", {"start": v(26.32, 8.78) * mm, "mid": v(26.4, 9.07) * mm, "end": v(26.33, 9.36) * mm});
            skArc(sketch, "E165.21.2", {"start": v(25.17, 9.54) * mm, "mid": v(24.9, 9.15) * mm, "end": v(24.6, 8.77) * mm});
            skPoint(sketch, "E165.21.3", {"position": v(25.7, 9.2) * mm});
            skArc(sketch, "E165.21.4", {"start": v(25.78, 8.53) * mm, "mid": v(25.62, 8.57) * mm, "end": v(25.47, 8.63) * mm});
            skLineSegment(sketch, "E165.21.5", {"start": v(25.66, 10.37) * mm, "end": v(26.24, 10.06) * mm});
            skArc(sketch, "E165.21.6", {"start": v(25.29, 8.59) * mm, "mid": v(25.2, 8.47) * mm, "end": v(25.1, 8.35) * mm});
            skLineSegment(sketch, "E165.21.7", {"start": v(24.6, 8.77) * mm, "end": v(25.1, 8.35) * mm});
            skArc(sketch, "E165.21.8", {"start": v(26.32, 8.78) * mm, "mid": v(26.08, 8.58) * mm, "end": v(25.78, 8.53) * mm});
            skPoint(sketch, "E165.21.9", {"position": v(25.17, 9.54) * mm});
            skArc(sketch, "E165.21.10", {"start": v(25.48, 9.33) * mm, "mid": v(25.2, 8.92) * mm, "end": v(24.88, 8.53) * mm, "construction": true});
            skArc(sketch, "E165.21.11", {"start": v(25.17, 9.54) * mm, "mid": v(25.43, 9.95) * mm, "end": v(25.66, 10.37) * mm});
            skPoint(sketch, "E165.21.12", {"position": v(25.48, 9.33) * mm});
            skArc(sketch, "E165.21.13", {"start": v(26.1, 9.8) * mm, "mid": v(26.17, 9.93) * mm, "end": v(26.24, 10.06) * mm});
            skArc(sketch, "E165.21.14", {"start": v(25.47, 8.63) * mm, "mid": v(25.37, 8.64) * mm, "end": v(25.29, 8.59) * mm});
            skArc(sketch, "E165.21.15", {"start": v(26.13, 9.61) * mm, "mid": v(26.08, 9.7) * mm, "end": v(26.1, 9.8) * mm});
            skArc(sketch, "E165.22.0", {"start": v(27.25, 11.3) * mm, "mid": v(27.14, 11.4) * mm, "end": v(27, 11.5) * mm});
            skArc(sketch, "E165.22.1", {"start": v(27.35, 10.71) * mm, "mid": v(27.39, 11.02) * mm, "end": v(27.25, 11.3) * mm});
            skArc(sketch, "E165.22.2", {"start": v(26.08, 11.24) * mm, "mid": v(25.88, 10.8) * mm, "end": v(25.66, 10.37) * mm});
            skPoint(sketch, "E165.22.3", {"position": v(26.66, 11) * mm});
            skArc(sketch, "E165.22.4", {"start": v(26.87, 10.37) * mm, "mid": v(26.71, 10.37) * mm, "end": v(26.55, 10.4) * mm});
            skLineSegment(sketch, "E165.22.5", {"start": v(26.4, 12.15) * mm, "end": v(27.03, 11.96) * mm});
            skArc(sketch, "E165.22.6", {"start": v(26.38, 10.33) * mm, "mid": v(26.31, 10.2) * mm, "end": v(26.24, 10.06) * mm});
            skLineSegment(sketch, "E165.22.7", {"start": v(25.66, 10.37) * mm, "end": v(26.24, 10.06) * mm});
            skArc(sketch, "E165.22.8", {"start": v(27.35, 10.71) * mm, "mid": v(27.16, 10.47) * mm, "end": v(26.87, 10.37) * mm});
            skPoint(sketch, "E165.22.9", {"position": v(26.08, 11.24) * mm});
            skArc(sketch, "E165.22.10", {"start": v(26.42, 11.1) * mm, "mid": v(26.22, 10.64) * mm, "end": v(26, 10.2) * mm, "construction": true});
            skArc(sketch, "E165.22.11", {"start": v(26.08, 11.24) * mm, "mid": v(26.25, 11.7) * mm, "end": v(26.4, 12.15) * mm});
            skPoint(sketch, "E165.22.12", {"position": v(26.42, 11.1) * mm});
            skArc(sketch, "E165.22.13", {"start": v(26.94, 11.67) * mm, "mid": v(26.98, 11.82) * mm, "end": v(27.03, 11.96) * mm});
            skArc(sketch, "E165.22.14", {"start": v(26.55, 10.4) * mm, "mid": v(26.45, 10.4) * mm, "end": v(26.38, 10.33) * mm});
            skArc(sketch, "E165.22.15", {"start": v(27, 11.5) * mm, "mid": v(26.94, 11.57) * mm, "end": v(26.94, 11.67) * mm});
            skArc(sketch, "E165.23.0", {"start": v(27.78, 13.36) * mm, "mid": v(27.64, 13.45) * mm, "end": v(27.5, 13.52) * mm});
            skArc(sketch, "E165.23.1", {"start": v(27.99, 12.81) * mm, "mid": v(27.96, 13.12) * mm, "end": v(27.78, 13.36) * mm});
            skArc(sketch, "E165.23.2", {"start": v(26.64, 13.08) * mm, "mid": v(26.53, 12.61) * mm, "end": v(26.4, 12.15) * mm});
            skPoint(sketch, "E165.23.3", {"position": v(27.25, 12.96) * mm});
            skArc(sketch, "E165.23.4", {"start": v(27.59, 12.39) * mm, "mid": v(27.43, 12.36) * mm, "end": v(27.27, 12.36) * mm});
            skLineSegment(sketch, "E165.23.5", {"start": v(26.78, 14.04) * mm, "end": v(27.43, 13.97) * mm});
            skArc(sketch, "E165.23.6", {"start": v(27.11, 12.24) * mm, "mid": v(27.07, 12.1) * mm, "end": v(27.03, 11.96) * mm});
            skLineSegment(sketch, "E165.23.7", {"start": v(26.4, 12.15) * mm, "end": v(27.03, 11.96) * mm});
            skArc(sketch, "E165.23.8", {"start": v(27.99, 12.81) * mm, "mid": v(27.85, 12.54) * mm, "end": v(27.59, 12.39) * mm});
            skPoint(sketch, "E165.23.9", {"position": v(26.64, 13.08) * mm});
            skArc(sketch, "E165.23.10", {"start": v(27, 13.01) * mm, "mid": v(26.9, 12.52) * mm, "end": v(26.76, 12.04) * mm, "construction": true});
            skArc(sketch, "E165.23.11", {"start": v(26.64, 13.08) * mm, "mid": v(26.72, 13.56) * mm, "end": v(26.78, 14.04) * mm});
            skPoint(sketch, "E165.23.12", {"position": v(27, 13.01) * mm});
            skArc(sketch, "E165.23.13", {"start": v(27.4, 13.68) * mm, "mid": v(27.41, 13.82) * mm, "end": v(27.43, 13.97) * mm});
            skArc(sketch, "E165.23.14", {"start": v(27.27, 12.36) * mm, "mid": v(27.17, 12.33) * mm, "end": v(27.11, 12.24) * mm});
            skArc(sketch, "E165.23.15", {"start": v(27.5, 13.52) * mm, "mid": v(27.42, 13.58) * mm, "end": v(27.4, 13.68) * mm});
            skArc(sketch, "E165.24.0", {"start": v(27.9, 15.5) * mm, "mid": v(27.74, 15.56) * mm, "end": v(27.58, 15.6) * mm});
            skArc(sketch, "E165.24.1", {"start": v(28.2, 15) * mm, "mid": v(28.12, 15.3) * mm, "end": v(27.9, 15.5) * mm});
            skArc(sketch, "E165.24.2", {"start": v(26.82, 15) * mm, "mid": v(26.81, 14.52) * mm, "end": v(26.78, 14.04) * mm});
            skPoint(sketch, "E165.24.3", {"position": v(27.45, 15) * mm});
            skArc(sketch, "E165.24.4", {"start": v(27.9, 14.5) * mm, "mid": v(27.74, 14.44) * mm, "end": v(27.58, 14.4) * mm});
            skLineSegment(sketch, "E165.24.5", {"start": v(26.78, 15.96) * mm, "end": v(27.43, 16.03) * mm});
            skArc(sketch, "E165.24.6", {"start": v(27.45, 14.27) * mm, "mid": v(27.44, 14.12) * mm, "end": v(27.43, 13.97) * mm});
            skLineSegment(sketch, "E165.24.7", {"start": v(26.78, 14.04) * mm, "end": v(27.43, 13.97) * mm});
            skArc(sketch, "E165.24.8", {"start": v(28.2, 15) * mm, "mid": v(28.12, 14.7) * mm, "end": v(27.9, 14.5) * mm});
            skPoint(sketch, "E165.24.9", {"position": v(26.82, 15) * mm});
            skArc(sketch, "E165.24.10", {"start": v(27.2, 15) * mm, "mid": v(27.19, 14.5) * mm, "end": v(27.15, 14) * mm, "construction": true});
            skArc(sketch, "E165.24.11", {"start": v(26.82, 15) * mm, "mid": v(26.81, 15.48) * mm, "end": v(26.78, 15.96) * mm});
            skPoint(sketch, "E165.24.12", {"position": v(27.2, 15) * mm});
            skArc(sketch, "E165.24.13", {"start": v(27.45, 15.73) * mm, "mid": v(27.44, 15.88) * mm, "end": v(27.43, 16.03) * mm});
            skArc(sketch, "E165.24.14", {"start": v(27.58, 14.4) * mm, "mid": v(27.5, 14.36) * mm, "end": v(27.45, 14.27) * mm});
            skArc(sketch, "E165.24.15", {"start": v(27.58, 15.6) * mm, "mid": v(27.5, 15.64) * mm, "end": v(27.45, 15.73) * mm});
            skArc(sketch, "E165.25.0", {"start": v(27.59, 17.61) * mm, "mid": v(27.43, 17.64) * mm, "end": v(27.27, 17.64) * mm});
            skArc(sketch, "E165.25.1", {"start": v(27.99, 17.19) * mm, "mid": v(27.85, 17.46) * mm, "end": v(27.59, 17.61) * mm});
            skArc(sketch, "E165.25.2", {"start": v(26.64, 16.92) * mm, "mid": v(26.72, 16.44) * mm, "end": v(26.78, 15.96) * mm});
            skPoint(sketch, "E165.25.3", {"position": v(27.25, 17.04) * mm});
            skArc(sketch, "E165.25.4", {"start": v(27.78, 16.64) * mm, "mid": v(27.64, 16.55) * mm, "end": v(27.5, 16.48) * mm});
            skLineSegment(sketch, "E165.25.5", {"start": v(26.4, 17.85) * mm, "end": v(27.03, 18.04) * mm});
            skArc(sketch, "E165.25.6", {"start": v(27.4, 16.32) * mm, "mid": v(27.41, 16.18) * mm, "end": v(27.43, 16.03) * mm});
            skLineSegment(sketch, "E165.25.7", {"start": v(26.78, 15.96) * mm, "end": v(27.43, 16.03) * mm});
            skArc(sketch, "E165.25.8", {"start": v(27.99, 17.19) * mm, "mid": v(27.96, 16.88) * mm, "end": v(27.78, 16.64) * mm});
            skPoint(sketch, "E165.25.9", {"position": v(26.64, 16.92) * mm});
            skArc(sketch, "E165.25.10", {"start": v(27, 16.99) * mm, "mid": v(27.09, 16.5) * mm, "end": v(27.15, 16) * mm, "construction": true});
            skArc(sketch, "E165.25.11", {"start": v(26.64, 16.92) * mm, "mid": v(26.53, 17.39) * mm, "end": v(26.4, 17.85) * mm});
            skPoint(sketch, "E165.25.12", {"position": v(27, 16.99) * mm});
            skArc(sketch, "E165.25.13", {"start": v(27.11, 17.76) * mm, "mid": v(27.07, 17.9) * mm, "end": v(27.03, 18.04) * mm});
            skArc(sketch, "E165.25.14", {"start": v(27.5, 16.48) * mm, "mid": v(27.42, 16.42) * mm, "end": v(27.4, 16.32) * mm});
            skArc(sketch, "E165.25.15", {"start": v(27.27, 17.64) * mm, "mid": v(27.17, 17.67) * mm, "end": v(27.11, 17.76) * mm});
            skArc(sketch, "E165.26.0", {"start": v(26.87, 19.63) * mm, "mid": v(26.71, 19.63) * mm, "end": v(26.55, 19.6) * mm});
            skArc(sketch, "E165.26.1", {"start": v(27.35, 19.29) * mm, "mid": v(27.16, 19.53) * mm, "end": v(26.87, 19.63) * mm});
            skArc(sketch, "E165.26.2", {"start": v(26.08, 18.76) * mm, "mid": v(26.25, 18.3) * mm, "end": v(26.4, 17.85) * mm});
            skPoint(sketch, "E165.26.3", {"position": v(26.66, 19) * mm});
            skArc(sketch, "E165.26.4", {"start": v(27.25, 18.7) * mm, "mid": v(27.14, 18.6) * mm, "end": v(27, 18.5) * mm});
            skLineSegment(sketch, "E165.26.5", {"start": v(25.66, 19.63) * mm, "end": v(26.24, 19.94) * mm});
            skArc(sketch, "E165.26.6", {"start": v(26.94, 18.33) * mm, "mid": v(26.98, 18.18) * mm, "end": v(27.03, 18.04) * mm});
            skLineSegment(sketch, "E165.26.7", {"start": v(26.4, 17.85) * mm, "end": v(27.03, 18.04) * mm});
            skArc(sketch, "E165.26.8", {"start": v(27.35, 19.29) * mm, "mid": v(27.39, 18.98) * mm, "end": v(27.25, 18.7) * mm});
            skPoint(sketch, "E165.26.9", {"position": v(26.08, 18.76) * mm});
            skArc(sketch, "E165.26.10", {"start": v(26.42, 18.9) * mm, "mid": v(26.6, 18.44) * mm, "end": v(26.76, 17.96) * mm, "construction": true});
            skArc(sketch, "E165.26.11", {"start": v(26.08, 18.76) * mm, "mid": v(25.88, 19.2) * mm, "end": v(25.66, 19.63) * mm});
            skPoint(sketch, "E165.26.12", {"position": v(26.42, 18.9) * mm});
            skArc(sketch, "E165.26.13", {"start": v(26.38, 19.67) * mm, "mid": v(26.31, 19.8) * mm, "end": v(26.24, 19.94) * mm});
            skArc(sketch, "E165.26.14", {"start": v(27, 18.5) * mm, "mid": v(26.94, 18.43) * mm, "end": v(26.94, 18.33) * mm});
            skArc(sketch, "E165.26.15", {"start": v(26.55, 19.6) * mm, "mid": v(26.45, 19.6) * mm, "end": v(26.38, 19.67) * mm});
            skArc(sketch, "E165.27.0", {"start": v(25.78, 21.47) * mm, "mid": v(25.62, 21.43) * mm, "end": v(25.47, 21.37) * mm});
            skArc(sketch, "E165.27.1", {"start": v(26.32, 21.22) * mm, "mid": v(26.08, 21.42) * mm, "end": v(25.78, 21.47) * mm});
            skArc(sketch, "E165.27.2", {"start": v(25.17, 20.46) * mm, "mid": v(25.43, 20.05) * mm, "end": v(25.66, 19.63) * mm});
            skPoint(sketch, "E165.27.3", {"position": v(25.7, 20.8) * mm});
            skArc(sketch, "E165.27.4", {"start": v(26.33, 20.64) * mm, "mid": v(26.24, 20.5) * mm, "end": v(26.13, 20.39) * mm});
            skLineSegment(sketch, "E165.27.5", {"start": v(24.6, 21.23) * mm, "end": v(25.1, 21.65) * mm});
            skArc(sketch, "E165.27.6", {"start": v(26.1, 20.2) * mm, "mid": v(26.17, 20.07) * mm, "end": v(26.24, 19.94) * mm});
            skLineSegment(sketch, "E165.27.7", {"start": v(25.66, 19.63) * mm, "end": v(26.24, 19.94) * mm});
            skArc(sketch, "E165.27.8", {"start": v(26.32, 21.22) * mm, "mid": v(26.4, 20.93) * mm, "end": v(26.33, 20.64) * mm});
            skPoint(sketch, "E165.27.9", {"position": v(25.17, 20.46) * mm});
            skArc(sketch, "E165.27.10", {"start": v(25.48, 20.67) * mm, "mid": v(25.75, 20.24) * mm, "end": v(26, 19.8) * mm, "construction": true});
            skArc(sketch, "E165.27.11", {"start": v(25.17, 20.46) * mm, "mid": v(24.9, 20.85) * mm, "end": v(24.6, 21.23) * mm});
            skPoint(sketch, "E165.27.12", {"position": v(25.48, 20.67) * mm});
            skArc(sketch, "E165.27.13", {"start": v(25.29, 21.41) * mm, "mid": v(25.2, 21.53) * mm, "end": v(25.1, 21.65) * mm});
            skArc(sketch, "E165.27.14", {"start": v(26.13, 20.39) * mm, "mid": v(26.08, 20.3) * mm, "end": v(26.1, 20.2) * mm});
            skArc(sketch, "E165.27.15", {"start": v(25.47, 21.37) * mm, "mid": v(25.37, 21.36) * mm, "end": v(25.29, 21.41) * mm});
            skArc(sketch, "E165.28.0", {"start": v(24.35, 23.05) * mm, "mid": v(24.2, 23) * mm, "end": v(24.07, 22.9) * mm});
            skArc(sketch, "E165.28.1", {"start": v(24.92, 22.92) * mm, "mid": v(24.65, 23.07) * mm, "end": v(24.35, 23.05) * mm});
            skArc(sketch, "E165.28.2", {"start": v(23.95, 21.95) * mm, "mid": v(24.28, 21.6) * mm, "end": v(24.6, 21.23) * mm});
            skPoint(sketch, "E165.28.3", {"position": v(24.4, 22.4) * mm});
            skArc(sketch, "E165.28.4", {"start": v(25.05, 22.35) * mm, "mid": v(25, 22.2) * mm, "end": v(24.9, 22.07) * mm});
            skLineSegment(sketch, "E165.28.5", {"start": v(23.23, 22.6) * mm, "end": v(23.65, 23.1) * mm});
            skArc(sketch, "E165.28.6", {"start": v(24.9, 21.88) * mm, "mid": v(25, 21.76) * mm, "end": v(25.1, 21.65) * mm});
            skLineSegment(sketch, "E165.28.7", {"start": v(24.6, 21.23) * mm, "end": v(25.1, 21.65) * mm});
            skArc(sketch, "E165.28.8", {"start": v(24.92, 22.92) * mm, "mid": v(25.07, 22.65) * mm, "end": v(25.05, 22.35) * mm});
            skPoint(sketch, "E165.28.9", {"position": v(23.95, 21.95) * mm});
            skArc(sketch, "E165.28.10", {"start": v(24.21, 22.21) * mm, "mid": v(24.56, 21.85) * mm, "end": v(24.88, 21.47) * mm, "construction": true});
            skArc(sketch, "E165.28.11", {"start": v(23.95, 21.95) * mm, "mid": v(23.6, 22.28) * mm, "end": v(23.23, 22.6) * mm});
            skPoint(sketch, "E165.28.12", {"position": v(24.21, 22.21) * mm});
            skArc(sketch, "E165.28.13", {"start": v(23.88, 22.9) * mm, "mid": v(23.76, 23) * mm, "end": v(23.65, 23.1) * mm});
            skArc(sketch, "E165.28.14", {"start": v(24.9, 22.07) * mm, "mid": v(24.87, 21.97) * mm, "end": v(24.9, 21.88) * mm});
            skArc(sketch, "E165.28.15", {"start": v(24.07, 22.9) * mm, "mid": v(23.97, 22.87) * mm, "end": v(23.88, 22.9) * mm});
            skArc(sketch, "E165.29.0", {"start": v(22.64, 24.33) * mm, "mid": v(22.5, 24.24) * mm, "end": v(22.39, 24.13) * mm});
            skArc(sketch, "E165.29.1", {"start": v(23.22, 24.32) * mm, "mid": v(22.93, 24.4) * mm, "end": v(22.64, 24.33) * mm});
            skArc(sketch, "E165.29.2", {"start": v(22.46, 23.17) * mm, "mid": v(22.85, 22.9) * mm, "end": v(23.23, 22.6) * mm});
            skPoint(sketch, "E165.29.3", {"position": v(22.8, 23.7) * mm});
            skArc(sketch, "E165.29.4", {"start": v(23.47, 23.78) * mm, "mid": v(23.43, 23.62) * mm, "end": v(23.37, 23.47) * mm});
            skLineSegment(sketch, "E165.29.5", {"start": v(21.63, 23.66) * mm, "end": v(21.94, 24.24) * mm});
            skArc(sketch, "E165.29.6", {"start": v(23.41, 23.29) * mm, "mid": v(23.53, 23.2) * mm, "end": v(23.65, 23.1) * mm});
            skLineSegment(sketch, "E165.29.7", {"start": v(23.23, 22.6) * mm, "end": v(23.65, 23.1) * mm});
            skArc(sketch, "E165.29.8", {"start": v(23.22, 24.32) * mm, "mid": v(23.42, 24.08) * mm, "end": v(23.47, 23.78) * mm});
            skPoint(sketch, "E165.29.9", {"position": v(22.46, 23.17) * mm});
            skArc(sketch, "E165.29.10", {"start": v(22.67, 23.48) * mm, "mid": v(23.08, 23.2) * mm, "end": v(23.47, 22.88) * mm, "construction": true});
            skArc(sketch, "E165.29.11", {"start": v(22.46, 23.17) * mm, "mid": v(22.05, 23.43) * mm, "end": v(21.63, 23.66) * mm});
            skPoint(sketch, "E165.29.12", {"position": v(22.67, 23.48) * mm});
            skArc(sketch, "E165.29.13", {"start": v(22.2, 24.1) * mm, "mid": v(22.07, 24.17) * mm, "end": v(21.94, 24.24) * mm});
            skArc(sketch, "E165.29.14", {"start": v(23.37, 23.47) * mm, "mid": v(23.36, 23.37) * mm, "end": v(23.41, 23.29) * mm});
            skArc(sketch, "E165.29.15", {"start": v(22.39, 24.13) * mm, "mid": v(22.3, 24.08) * mm, "end": v(22.2, 24.1) * mm});
            skArc(sketch, "E165.30.0", {"start": v(20.7, 25.25) * mm, "mid": v(20.6, 25.14) * mm, "end": v(20.5, 25) * mm});
            skArc(sketch, "E165.30.1", {"start": v(21.29, 25.35) * mm, "mid": v(20.98, 25.39) * mm, "end": v(20.7, 25.25) * mm});
            skArc(sketch, "E165.30.2", {"start": v(20.76, 24.08) * mm, "mid": v(21.2, 23.88) * mm, "end": v(21.63, 23.66) * mm});
            skPoint(sketch, "E165.30.3", {"position": v(21, 24.66) * mm});
            skArc(sketch, "E165.30.4", {"start": v(21.63, 24.87) * mm, "mid": v(21.63, 24.71) * mm, "end": v(21.6, 24.55) * mm});
            skLineSegment(sketch, "E165.30.5", {"start": v(19.85, 24.4) * mm, "end": v(20.04, 25.03) * mm});
            skArc(sketch, "E165.30.6", {"start": v(21.67, 24.38) * mm, "mid": v(21.8, 24.31) * mm, "end": v(21.94, 24.24) * mm});
            skLineSegment(sketch, "E165.30.7", {"start": v(21.63, 23.66) * mm, "end": v(21.94, 24.24) * mm});
            skArc(sketch, "E165.30.8", {"start": v(21.29, 25.35) * mm, "mid": v(21.53, 25.16) * mm, "end": v(21.63, 24.87) * mm});
            skPoint(sketch, "E165.30.9", {"position": v(20.76, 24.08) * mm});
            skArc(sketch, "E165.30.10", {"start": v(20.9, 24.42) * mm, "mid": v(21.36, 24.22) * mm, "end": v(21.8, 24) * mm, "construction": true});
            skArc(sketch, "E165.30.11", {"start": v(20.76, 24.08) * mm, "mid": v(20.3, 24.25) * mm, "end": v(19.85, 24.4) * mm});
            skPoint(sketch, "E165.30.12", {"position": v(20.9, 24.42) * mm});
            skArc(sketch, "E165.30.13", {"start": v(20.33, 24.94) * mm, "mid": v(20.18, 24.98) * mm, "end": v(20.04, 25.03) * mm});
            skArc(sketch, "E165.30.14", {"start": v(21.6, 24.55) * mm, "mid": v(21.6, 24.45) * mm, "end": v(21.67, 24.38) * mm});
            skArc(sketch, "E165.30.15", {"start": v(20.5, 25) * mm, "mid": v(20.43, 24.94) * mm, "end": v(20.33, 24.94) * mm});
            skArc(sketch, "E165.31.0", {"start": v(18.64, 25.78) * mm, "mid": v(18.55, 25.64) * mm, "end": v(18.48, 25.5) * mm});
            skArc(sketch, "E165.31.1", {"start": v(19.19, 25.99) * mm, "mid": v(18.88, 25.96) * mm, "end": v(18.64, 25.78) * mm});
            skArc(sketch, "E165.31.2", {"start": v(18.92, 24.64) * mm, "mid": v(19.39, 24.53) * mm, "end": v(19.85, 24.4) * mm});
            skPoint(sketch, "E165.31.3", {"position": v(19.04, 25.25) * mm});
            skArc(sketch, "E165.31.4", {"start": v(19.61, 25.59) * mm, "mid": v(19.64, 25.43) * mm, "end": v(19.64, 25.27) * mm});
            skArc(sketch, "E165.31.6", {"start": v(19.76, 25.11) * mm, "mid": v(19.9, 25.07) * mm, "end": v(20.04, 25.03) * mm});
            skLineSegment(sketch, "E165.31.7", {"start": v(19.85, 24.4) * mm, "end": v(20.04, 25.03) * mm});
            skArc(sketch, "E165.31.8", {"start": v(19.19, 25.99) * mm, "mid": v(19.46, 25.85) * mm, "end": v(19.61, 25.59) * mm});
            skPoint(sketch, "E165.31.9", {"position": v(18.92, 24.64) * mm});
            skArc(sketch, "E165.31.10", {"start": v(18.99, 25) * mm, "mid": v(19.48, 24.9) * mm, "end": v(19.96, 24.76) * mm, "construction": true});
            skArc(sketch, "E165.31.11", {"start": v(18.92, 24.64) * mm, "mid": v(18.44, 24.72) * mm, "end": v(17.96, 24.78) * mm});
            skPoint(sketch, "E165.31.12", {"position": v(18.99, 25) * mm});
            skArc(sketch, "E165.31.13", {"start": v(18.32, 25.4) * mm, "mid": v(18.18, 25.41) * mm, "end": v(18.03, 25.43) * mm});
            skArc(sketch, "E165.31.14", {"start": v(19.64, 25.27) * mm, "mid": v(19.67, 25.17) * mm, "end": v(19.76, 25.11) * mm});
            skArc(sketch, "E165.31.15", {"start": v(18.48, 25.5) * mm, "mid": v(18.42, 25.42) * mm, "end": v(18.32, 25.4) * mm});
            skLineSegment(sketch, "E166.0", {"start": v(6.75, 15) * mm, "end": v(27.25, 15) * mm, "construction": true});
            skSolve(sketch);
        }
        {
            var Q0;
            Q0=qSketchRegion(id+"F25",true);
            extrude(context, id + "F26", {"entities" : qUnion([Q0]), "operationType" : NewBodyOperationType.REMOVE, "endBound" : BoundingType.SYMMETRIC, "oppositeDirection" : true, "depth" : 6.5 * mm});
        }
        {
            var Q0;
            Q0=makeQuery(id+"F2.boolean.opBoolean","MERGE",FACE,{"derivedFrom":[makeQuery(id+"F1.opExtrude","SWEPT_FACE",FACE,{"disambiguationData":[OSD([sQuery(id+"F0.wireOp",EDGE,"E4"),sQuery(id+"F0.wireOp",EDGE,"E22")])]}),makeQuery(id+"F2.opExtrude","SWEPT_FACE",FACE,{"disambiguationData":[OSD([sQuery(id+"F0.wireOp",EDGE,"E35")])]})]});
            var Q1;
            Q1=sQuery(id+"F0.wireOp",VERTEX,"E16");
            cPlane(context, id + "F27", {"entities" : qUnion([Q0, Q1]), "cplaneType" : CPlaneType.PLANE_POINT, "offset" : 150 * mm, "width" : 150 * mm, "height" : 150 * mm});
        }
        {
            var Q0;
            Q0=qCreatedBy(id+"F27.planeOp",FACE);
            var sketch = newSketch(context, id + "F28", { "sketchPlane" : qUnion([Q0])});
            skLineSegment(sketch, "E167", {"start": v(-17, 12.16) * mm, "end": v(-17, 9.53) * mm, "construction": true});
            skArc(sketch, "E168", {"start": v(-17, 26.2) * mm, "mid": v(-16.7, 26.12) * mm, "end": v(-16.5, 25.9) * mm});
            skArc(sketch, "E169", {"start": v(-16.5, 25.9) * mm, "mid": v(-16.44, 25.74) * mm, "end": v(-16.4, 25.58) * mm});
            skArc(sketch, "E170", {"start": v(-16.4, 25.58) * mm, "mid": v(-16.36, 25.5) * mm, "end": v(-16.27, 25.45) * mm});
            skPoint(sketch, "E171", {"position": v(-17, 24.82) * mm});
            skPoint(sketch, "E172", {"position": v(-17, 25.45) * mm});
            skPoint(sketch, "E173", {"position": v(-17, 25.2) * mm});
            skArc(sketch, "E174", {"start": v(-17, 25.2) * mm, "mid": v(-16.5, 25.19) * mm, "end": v(-16, 25.15) * mm, "construction": true});
            skLineSegment(sketch, "E175", {"start": v(-16.04, 24.78) * mm, "end": v(-15.97, 25.43) * mm});
            skArc(sketch, "E176", {"start": v(-16.27, 25.45) * mm, "mid": v(-16.12, 25.44) * mm, "end": v(-15.97, 25.43) * mm});
            skArc(sketch, "E177", {"start": v(-17, 24.82) * mm, "mid": v(-16.52, 24.81) * mm, "end": v(-16.04, 24.78) * mm});
            skArc(sketch, "E178.MirrorCS", {"start": v(-17, 26.2) * mm, "mid": v(-17.3, 26.12) * mm, "end": v(-17.5, 25.9) * mm});
            skArc(sketch, "E179.MirrorCS", {"start": v(-17.5, 25.9) * mm, "mid": v(-17.56, 25.74) * mm, "end": v(-17.6, 25.58) * mm});
            skArc(sketch, "E180.MirrorCS", {"start": v(-17.6, 25.58) * mm, "mid": v(-17.64, 25.5) * mm, "end": v(-17.73, 25.45) * mm});
            skArc(sketch, "E181.MirrorCS", {"start": v(-17.73, 25.45) * mm, "mid": v(-17.88, 25.44) * mm, "end": v(-18.03, 25.43) * mm});
            skLineSegment(sketch, "E182.MirrorCS", {"start": v(-17.96, 24.78) * mm, "end": v(-18.03, 25.43) * mm});
            skArc(sketch, "E183.MirrorCS", {"start": v(-17, 24.82) * mm, "mid": v(-17.48, 24.81) * mm, "end": v(-17.96, 24.78) * mm});
            skArc(sketch, "E184.1.0", {"start": v(-19.61, 25.59) * mm, "mid": v(-19.64, 25.43) * mm, "end": v(-19.64, 25.27) * mm});
            skArc(sketch, "E184.1.1", {"start": v(-19.19, 25.99) * mm, "mid": v(-19.46, 25.85) * mm, "end": v(-19.61, 25.59) * mm});
            skArc(sketch, "E184.1.2", {"start": v(-18.92, 24.64) * mm, "mid": v(-18.44, 24.72) * mm, "end": v(-17.96, 24.78) * mm});
            skPoint(sketch, "E184.1.3", {"position": v(-19.04, 25.25) * mm});
            skArc(sketch, "E184.1.4", {"start": v(-18.64, 25.78) * mm, "mid": v(-18.55, 25.64) * mm, "end": v(-18.48, 25.5) * mm});
            skLineSegment(sketch, "E184.1.5", {"start": v(-19.85, 24.4) * mm, "end": v(-20.04, 25.03) * mm});
            skArc(sketch, "E184.1.6", {"start": v(-18.32, 25.4) * mm, "mid": v(-18.18, 25.41) * mm, "end": v(-18.03, 25.43) * mm});
            skArc(sketch, "E184.1.8", {"start": v(-19.19, 25.99) * mm, "mid": v(-18.88, 25.96) * mm, "end": v(-18.64, 25.78) * mm});
            skPoint(sketch, "E184.1.9", {"position": v(-18.92, 24.64) * mm});
            skArc(sketch, "E184.1.10", {"start": v(-18.99, 25) * mm, "mid": v(-18.5, 25.09) * mm, "end": v(-18, 25.15) * mm, "construction": true});
            skArc(sketch, "E184.1.11", {"start": v(-18.92, 24.64) * mm, "mid": v(-19.39, 24.53) * mm, "end": v(-19.85, 24.4) * mm});
            skPoint(sketch, "E184.1.12", {"position": v(-18.99, 25) * mm});
            skArc(sketch, "E184.1.13", {"start": v(-19.76, 25.11) * mm, "mid": v(-19.9, 25.07) * mm, "end": v(-20.04, 25.03) * mm});
            skArc(sketch, "E184.1.14", {"start": v(-18.48, 25.5) * mm, "mid": v(-18.42, 25.42) * mm, "end": v(-18.32, 25.4) * mm});
            skArc(sketch, "E184.1.15", {"start": v(-19.64, 25.27) * mm, "mid": v(-19.67, 25.17) * mm, "end": v(-19.76, 25.11) * mm});
            skArc(sketch, "E184.2.0", {"start": v(-21.63, 24.87) * mm, "mid": v(-21.63, 24.71) * mm, "end": v(-21.6, 24.55) * mm});
            skArc(sketch, "E184.2.1", {"start": v(-21.29, 25.35) * mm, "mid": v(-21.53, 25.16) * mm, "end": v(-21.63, 24.87) * mm});
            skArc(sketch, "E184.2.2", {"start": v(-20.76, 24.08) * mm, "mid": v(-20.3, 24.25) * mm, "end": v(-19.85, 24.4) * mm});
            skPoint(sketch, "E184.2.3", {"position": v(-21, 24.66) * mm});
            skArc(sketch, "E184.2.4", {"start": v(-20.7, 25.25) * mm, "mid": v(-20.6, 25.14) * mm, "end": v(-20.5, 25) * mm});
            skLineSegment(sketch, "E184.2.5", {"start": v(-21.63, 23.66) * mm, "end": v(-21.94, 24.24) * mm});
            skArc(sketch, "E184.2.6", {"start": v(-20.33, 24.94) * mm, "mid": v(-20.18, 24.98) * mm, "end": v(-20.04, 25.03) * mm});
            skLineSegment(sketch, "E184.2.7", {"start": v(-19.85, 24.4) * mm, "end": v(-20.04, 25.03) * mm});
            skArc(sketch, "E184.2.8", {"start": v(-21.29, 25.35) * mm, "mid": v(-20.98, 25.39) * mm, "end": v(-20.7, 25.25) * mm});
            skPoint(sketch, "E184.2.9", {"position": v(-20.76, 24.08) * mm});
            skArc(sketch, "E184.2.10", {"start": v(-20.9, 24.42) * mm, "mid": v(-20.44, 24.6) * mm, "end": v(-19.96, 24.76) * mm, "construction": true});
            skArc(sketch, "E184.2.11", {"start": v(-20.76, 24.08) * mm, "mid": v(-21.2, 23.88) * mm, "end": v(-21.63, 23.66) * mm});
            skPoint(sketch, "E184.2.12", {"position": v(-20.9, 24.42) * mm});
            skArc(sketch, "E184.2.13", {"start": v(-21.67, 24.38) * mm, "mid": v(-21.8, 24.31) * mm, "end": v(-21.94, 24.24) * mm});
            skArc(sketch, "E184.2.14", {"start": v(-20.5, 25) * mm, "mid": v(-20.43, 24.94) * mm, "end": v(-20.33, 24.94) * mm});
            skArc(sketch, "E184.2.15", {"start": v(-21.6, 24.55) * mm, "mid": v(-21.6, 24.45) * mm, "end": v(-21.67, 24.38) * mm});
            skArc(sketch, "E184.3.0", {"start": v(-23.47, 23.78) * mm, "mid": v(-23.43, 23.62) * mm, "end": v(-23.37, 23.47) * mm});
            skArc(sketch, "E184.3.1", {"start": v(-23.22, 24.32) * mm, "mid": v(-23.42, 24.08) * mm, "end": v(-23.47, 23.78) * mm});
            skArc(sketch, "E184.3.2", {"start": v(-22.46, 23.17) * mm, "mid": v(-22.05, 23.43) * mm, "end": v(-21.63, 23.66) * mm});
            skPoint(sketch, "E184.3.3", {"position": v(-22.8, 23.7) * mm});
            skArc(sketch, "E184.3.4", {"start": v(-22.64, 24.33) * mm, "mid": v(-22.5, 24.24) * mm, "end": v(-22.39, 24.13) * mm});
            skLineSegment(sketch, "E184.3.5", {"start": v(-23.23, 22.6) * mm, "end": v(-23.65, 23.1) * mm});
            skArc(sketch, "E184.3.6", {"start": v(-22.2, 24.1) * mm, "mid": v(-22.07, 24.17) * mm, "end": v(-21.94, 24.24) * mm});
            skLineSegment(sketch, "E184.3.7", {"start": v(-21.63, 23.66) * mm, "end": v(-21.94, 24.24) * mm});
            skArc(sketch, "E184.3.8", {"start": v(-23.22, 24.32) * mm, "mid": v(-22.93, 24.4) * mm, "end": v(-22.64, 24.33) * mm});
            skPoint(sketch, "E184.3.9", {"position": v(-22.46, 23.17) * mm});
            skArc(sketch, "E184.3.10", {"start": v(-22.67, 23.48) * mm, "mid": v(-22.24, 23.75) * mm, "end": v(-21.8, 24) * mm, "construction": true});
            skArc(sketch, "E184.3.11", {"start": v(-22.46, 23.17) * mm, "mid": v(-22.85, 22.9) * mm, "end": v(-23.23, 22.6) * mm});
            skPoint(sketch, "E184.3.12", {"position": v(-22.67, 23.48) * mm});
            skArc(sketch, "E184.3.13", {"start": v(-23.41, 23.29) * mm, "mid": v(-23.53, 23.2) * mm, "end": v(-23.65, 23.1) * mm});
            skArc(sketch, "E184.3.14", {"start": v(-22.39, 24.13) * mm, "mid": v(-22.3, 24.08) * mm, "end": v(-22.2, 24.1) * mm});
            skArc(sketch, "E184.3.15", {"start": v(-23.37, 23.47) * mm, "mid": v(-23.36, 23.37) * mm, "end": v(-23.41, 23.29) * mm});
            skArc(sketch, "E184.4.0", {"start": v(-25.05, 22.35) * mm, "mid": v(-25, 22.2) * mm, "end": v(-24.9, 22.07) * mm});
            skArc(sketch, "E184.4.1", {"start": v(-24.92, 22.92) * mm, "mid": v(-25.07, 22.65) * mm, "end": v(-25.05, 22.35) * mm});
            skArc(sketch, "E184.4.2", {"start": v(-23.95, 21.95) * mm, "mid": v(-23.6, 22.28) * mm, "end": v(-23.23, 22.6) * mm});
            skPoint(sketch, "E184.4.3", {"position": v(-24.4, 22.4) * mm});
            skArc(sketch, "E184.4.4", {"start": v(-24.35, 23.05) * mm, "mid": v(-24.2, 23) * mm, "end": v(-24.07, 22.9) * mm});
            skLineSegment(sketch, "E184.4.5", {"start": v(-24.6, 21.23) * mm, "end": v(-25.1, 21.65) * mm});
            skArc(sketch, "E184.4.6", {"start": v(-23.88, 22.9) * mm, "mid": v(-23.76, 23) * mm, "end": v(-23.65, 23.1) * mm});
            skLineSegment(sketch, "E184.4.7", {"start": v(-23.23, 22.6) * mm, "end": v(-23.65, 23.1) * mm});
            skArc(sketch, "E184.4.8", {"start": v(-24.92, 22.92) * mm, "mid": v(-24.65, 23.07) * mm, "end": v(-24.35, 23.05) * mm});
            skPoint(sketch, "E184.4.9", {"position": v(-23.95, 21.95) * mm});
            skArc(sketch, "E184.4.10", {"start": v(-24.21, 22.21) * mm, "mid": v(-23.85, 22.56) * mm, "end": v(-23.47, 22.88) * mm, "construction": true});
            skArc(sketch, "E184.4.11", {"start": v(-23.95, 21.95) * mm, "mid": v(-24.28, 21.6) * mm, "end": v(-24.6, 21.23) * mm});
            skPoint(sketch, "E184.4.12", {"position": v(-24.21, 22.21) * mm});
            skArc(sketch, "E184.4.13", {"start": v(-24.9, 21.88) * mm, "mid": v(-25, 21.76) * mm, "end": v(-25.1, 21.65) * mm});
            skArc(sketch, "E184.4.14", {"start": v(-24.07, 22.9) * mm, "mid": v(-23.97, 22.87) * mm, "end": v(-23.88, 22.9) * mm});
            skArc(sketch, "E184.4.15", {"start": v(-24.9, 22.07) * mm, "mid": v(-24.87, 21.97) * mm, "end": v(-24.9, 21.88) * mm});
            skArc(sketch, "E184.5.0", {"start": v(-26.33, 20.64) * mm, "mid": v(-26.24, 20.5) * mm, "end": v(-26.13, 20.39) * mm});
            skArc(sketch, "E184.5.1", {"start": v(-26.32, 21.22) * mm, "mid": v(-26.4, 20.93) * mm, "end": v(-26.33, 20.64) * mm});
            skArc(sketch, "E184.5.2", {"start": v(-25.17, 20.46) * mm, "mid": v(-24.9, 20.85) * mm, "end": v(-24.6, 21.23) * mm});
            skPoint(sketch, "E184.5.3", {"position": v(-25.7, 20.8) * mm});
            skArc(sketch, "E184.5.4", {"start": v(-25.78, 21.47) * mm, "mid": v(-25.62, 21.43) * mm, "end": v(-25.47, 21.37) * mm});
            skLineSegment(sketch, "E184.5.5", {"start": v(-25.66, 19.63) * mm, "end": v(-26.24, 19.94) * mm});
            skArc(sketch, "E184.5.6", {"start": v(-25.29, 21.41) * mm, "mid": v(-25.2, 21.53) * mm, "end": v(-25.1, 21.65) * mm});
            skLineSegment(sketch, "E184.5.7", {"start": v(-24.6, 21.23) * mm, "end": v(-25.1, 21.65) * mm});
            skArc(sketch, "E184.5.8", {"start": v(-26.32, 21.22) * mm, "mid": v(-26.08, 21.42) * mm, "end": v(-25.78, 21.47) * mm});
            skPoint(sketch, "E184.5.9", {"position": v(-25.17, 20.46) * mm});
            skArc(sketch, "E184.5.10", {"start": v(-25.48, 20.67) * mm, "mid": v(-25.2, 21.08) * mm, "end": v(-24.88, 21.47) * mm, "construction": true});
            skArc(sketch, "E184.5.11", {"start": v(-25.17, 20.46) * mm, "mid": v(-25.43, 20.05) * mm, "end": v(-25.66, 19.63) * mm});
            skPoint(sketch, "E184.5.12", {"position": v(-25.48, 20.67) * mm});
            skArc(sketch, "E184.5.13", {"start": v(-26.1, 20.2) * mm, "mid": v(-26.17, 20.07) * mm, "end": v(-26.24, 19.94) * mm});
            skArc(sketch, "E184.5.14", {"start": v(-25.47, 21.37) * mm, "mid": v(-25.37, 21.36) * mm, "end": v(-25.29, 21.41) * mm});
            skArc(sketch, "E184.5.15", {"start": v(-26.13, 20.39) * mm, "mid": v(-26.08, 20.3) * mm, "end": v(-26.1, 20.2) * mm});
            skArc(sketch, "E184.6.0", {"start": v(-27.25, 18.7) * mm, "mid": v(-27.14, 18.6) * mm, "end": v(-27, 18.5) * mm});
            skArc(sketch, "E184.6.1", {"start": v(-27.35, 19.29) * mm, "mid": v(-27.39, 18.98) * mm, "end": v(-27.25, 18.7) * mm});
            skArc(sketch, "E184.6.2", {"start": v(-26.08, 18.76) * mm, "mid": v(-25.88, 19.2) * mm, "end": v(-25.66, 19.63) * mm});
            skPoint(sketch, "E184.6.3", {"position": v(-26.66, 19) * mm});
            skArc(sketch, "E184.6.4", {"start": v(-26.87, 19.63) * mm, "mid": v(-26.71, 19.63) * mm, "end": v(-26.55, 19.6) * mm});
            skLineSegment(sketch, "E184.6.5", {"start": v(-26.4, 17.85) * mm, "end": v(-27.03, 18.04) * mm});
            skArc(sketch, "E184.6.6", {"start": v(-26.38, 19.67) * mm, "mid": v(-26.31, 19.8) * mm, "end": v(-26.24, 19.94) * mm});
            skLineSegment(sketch, "E184.6.7", {"start": v(-25.66, 19.63) * mm, "end": v(-26.24, 19.94) * mm});
            skArc(sketch, "E184.6.8", {"start": v(-27.35, 19.29) * mm, "mid": v(-27.16, 19.53) * mm, "end": v(-26.87, 19.63) * mm});
            skPoint(sketch, "E184.6.9", {"position": v(-26.08, 18.76) * mm});
            skArc(sketch, "E184.6.10", {"start": v(-26.42, 18.9) * mm, "mid": v(-26.22, 19.36) * mm, "end": v(-26, 19.8) * mm, "construction": true});
            skArc(sketch, "E184.6.11", {"start": v(-26.08, 18.76) * mm, "mid": v(-26.25, 18.3) * mm, "end": v(-26.4, 17.85) * mm});
            skPoint(sketch, "E184.6.12", {"position": v(-26.42, 18.9) * mm});
            skArc(sketch, "E184.6.13", {"start": v(-26.94, 18.33) * mm, "mid": v(-26.98, 18.18) * mm, "end": v(-27.03, 18.04) * mm});
            skArc(sketch, "E184.6.14", {"start": v(-26.55, 19.6) * mm, "mid": v(-26.45, 19.6) * mm, "end": v(-26.38, 19.67) * mm});
            skArc(sketch, "E184.6.15", {"start": v(-27, 18.5) * mm, "mid": v(-26.94, 18.43) * mm, "end": v(-26.94, 18.33) * mm});
            skArc(sketch, "E184.7.0", {"start": v(-27.78, 16.64) * mm, "mid": v(-27.64, 16.55) * mm, "end": v(-27.5, 16.48) * mm});
            skArc(sketch, "E184.7.1", {"start": v(-27.99, 17.19) * mm, "mid": v(-27.96, 16.88) * mm, "end": v(-27.78, 16.64) * mm});
            skArc(sketch, "E184.7.2", {"start": v(-26.64, 16.92) * mm, "mid": v(-26.53, 17.39) * mm, "end": v(-26.4, 17.85) * mm});
            skPoint(sketch, "E184.7.3", {"position": v(-27.25, 17.04) * mm});
            skArc(sketch, "E184.7.4", {"start": v(-27.59, 17.61) * mm, "mid": v(-27.43, 17.64) * mm, "end": v(-27.27, 17.64) * mm});
            skLineSegment(sketch, "E184.7.5", {"start": v(-26.78, 15.96) * mm, "end": v(-27.43, 16.03) * mm});
            skArc(sketch, "E184.7.6", {"start": v(-27.11, 17.76) * mm, "mid": v(-27.07, 17.9) * mm, "end": v(-27.03, 18.04) * mm});
            skLineSegment(sketch, "E184.7.7", {"start": v(-26.4, 17.85) * mm, "end": v(-27.03, 18.04) * mm});
            skArc(sketch, "E184.7.8", {"start": v(-27.99, 17.19) * mm, "mid": v(-27.85, 17.46) * mm, "end": v(-27.59, 17.61) * mm});
            skPoint(sketch, "E184.7.9", {"position": v(-26.64, 16.92) * mm});
            skArc(sketch, "E184.7.10", {"start": v(-27, 16.99) * mm, "mid": v(-26.9, 17.48) * mm, "end": v(-26.76, 17.96) * mm, "construction": true});
            skArc(sketch, "E184.7.11", {"start": v(-26.64, 16.92) * mm, "mid": v(-26.72, 16.44) * mm, "end": v(-26.78, 15.96) * mm});
            skPoint(sketch, "E184.7.12", {"position": v(-27, 16.99) * mm});
            skArc(sketch, "E184.7.13", {"start": v(-27.4, 16.32) * mm, "mid": v(-27.41, 16.18) * mm, "end": v(-27.43, 16.03) * mm});
            skArc(sketch, "E184.7.14", {"start": v(-27.27, 17.64) * mm, "mid": v(-27.17, 17.67) * mm, "end": v(-27.11, 17.76) * mm});
            skArc(sketch, "E184.7.15", {"start": v(-27.5, 16.48) * mm, "mid": v(-27.42, 16.42) * mm, "end": v(-27.4, 16.32) * mm});
            skArc(sketch, "E184.8.0", {"start": v(-27.9, 14.5) * mm, "mid": v(-27.74, 14.44) * mm, "end": v(-27.58, 14.4) * mm});
            skArc(sketch, "E184.8.1", {"start": v(-28.2, 15) * mm, "mid": v(-28.12, 14.7) * mm, "end": v(-27.9, 14.5) * mm});
            skArc(sketch, "E184.8.2", {"start": v(-26.82, 15) * mm, "mid": v(-26.81, 15.48) * mm, "end": v(-26.78, 15.96) * mm});
            skPoint(sketch, "E184.8.3", {"position": v(-27.45, 15) * mm});
            skArc(sketch, "E184.8.4", {"start": v(-27.9, 15.5) * mm, "mid": v(-27.74, 15.56) * mm, "end": v(-27.58, 15.6) * mm});
            skLineSegment(sketch, "E184.8.5", {"start": v(-26.78, 14.04) * mm, "end": v(-27.43, 13.97) * mm});
            skArc(sketch, "E184.8.6", {"start": v(-27.45, 15.73) * mm, "mid": v(-27.44, 15.88) * mm, "end": v(-27.43, 16.03) * mm});
            skLineSegment(sketch, "E184.8.7", {"start": v(-26.78, 15.96) * mm, "end": v(-27.43, 16.03) * mm});
            skArc(sketch, "E184.8.8", {"start": v(-28.2, 15) * mm, "mid": v(-28.12, 15.3) * mm, "end": v(-27.9, 15.5) * mm});
            skPoint(sketch, "E184.8.9", {"position": v(-26.82, 15) * mm});
            skArc(sketch, "E184.8.10", {"start": v(-27.2, 15) * mm, "mid": v(-27.19, 15.5) * mm, "end": v(-27.15, 16) * mm, "construction": true});
            skArc(sketch, "E184.8.11", {"start": v(-26.82, 15) * mm, "mid": v(-26.81, 14.52) * mm, "end": v(-26.78, 14.04) * mm});
            skPoint(sketch, "E184.8.12", {"position": v(-27.2, 15) * mm});
            skArc(sketch, "E184.8.13", {"start": v(-27.45, 14.27) * mm, "mid": v(-27.44, 14.12) * mm, "end": v(-27.43, 13.97) * mm});
            skArc(sketch, "E184.8.14", {"start": v(-27.58, 15.6) * mm, "mid": v(-27.5, 15.64) * mm, "end": v(-27.45, 15.73) * mm});
            skArc(sketch, "E184.8.15", {"start": v(-27.58, 14.4) * mm, "mid": v(-27.5, 14.36) * mm, "end": v(-27.45, 14.27) * mm});
            skArc(sketch, "E184.9.0", {"start": v(-27.59, 12.39) * mm, "mid": v(-27.43, 12.36) * mm, "end": v(-27.27, 12.36) * mm});
            skArc(sketch, "E184.9.1", {"start": v(-27.99, 12.81) * mm, "mid": v(-27.85, 12.54) * mm, "end": v(-27.59, 12.39) * mm});
            skArc(sketch, "E184.9.2", {"start": v(-26.64, 13.08) * mm, "mid": v(-26.72, 13.56) * mm, "end": v(-26.78, 14.04) * mm});
            skPoint(sketch, "E184.9.3", {"position": v(-27.25, 12.96) * mm});
            skArc(sketch, "E184.9.4", {"start": v(-27.78, 13.36) * mm, "mid": v(-27.64, 13.45) * mm, "end": v(-27.5, 13.52) * mm});
            skLineSegment(sketch, "E184.9.5", {"start": v(-26.4, 12.15) * mm, "end": v(-27.03, 11.96) * mm});
            skArc(sketch, "E184.9.6", {"start": v(-27.4, 13.68) * mm, "mid": v(-27.41, 13.82) * mm, "end": v(-27.43, 13.97) * mm});
            skLineSegment(sketch, "E184.9.7", {"start": v(-26.78, 14.04) * mm, "end": v(-27.43, 13.97) * mm});
            skArc(sketch, "E184.9.8", {"start": v(-27.99, 12.81) * mm, "mid": v(-27.96, 13.12) * mm, "end": v(-27.78, 13.36) * mm});
            skPoint(sketch, "E184.9.9", {"position": v(-26.64, 13.08) * mm});
            skArc(sketch, "E184.9.10", {"start": v(-27, 13.01) * mm, "mid": v(-27.09, 13.5) * mm, "end": v(-27.15, 14) * mm, "construction": true});
            skArc(sketch, "E184.9.11", {"start": v(-26.64, 13.08) * mm, "mid": v(-26.53, 12.61) * mm, "end": v(-26.4, 12.15) * mm});
            skPoint(sketch, "E184.9.12", {"position": v(-27, 13.01) * mm});
            skArc(sketch, "E184.9.13", {"start": v(-27.11, 12.24) * mm, "mid": v(-27.07, 12.1) * mm, "end": v(-27.03, 11.96) * mm});
            skArc(sketch, "E184.9.14", {"start": v(-27.5, 13.52) * mm, "mid": v(-27.42, 13.58) * mm, "end": v(-27.4, 13.68) * mm});
            skArc(sketch, "E184.9.15", {"start": v(-27.27, 12.36) * mm, "mid": v(-27.17, 12.33) * mm, "end": v(-27.11, 12.24) * mm});
            skArc(sketch, "E184.10.0", {"start": v(-26.87, 10.37) * mm, "mid": v(-26.71, 10.37) * mm, "end": v(-26.55, 10.4) * mm});
            skArc(sketch, "E184.10.1", {"start": v(-27.35, 10.71) * mm, "mid": v(-27.16, 10.47) * mm, "end": v(-26.87, 10.37) * mm});
            skArc(sketch, "E184.10.2", {"start": v(-26.08, 11.24) * mm, "mid": v(-26.25, 11.7) * mm, "end": v(-26.4, 12.15) * mm});
            skPoint(sketch, "E184.10.3", {"position": v(-26.66, 11) * mm});
            skArc(sketch, "E184.10.4", {"start": v(-27.25, 11.3) * mm, "mid": v(-27.14, 11.4) * mm, "end": v(-27, 11.5) * mm});
            skLineSegment(sketch, "E184.10.5", {"start": v(-25.66, 10.37) * mm, "end": v(-26.24, 10.06) * mm});
            skArc(sketch, "E184.10.6", {"start": v(-26.94, 11.67) * mm, "mid": v(-26.98, 11.82) * mm, "end": v(-27.03, 11.96) * mm});
            skLineSegment(sketch, "E184.10.7", {"start": v(-26.4, 12.15) * mm, "end": v(-27.03, 11.96) * mm});
            skArc(sketch, "E184.10.8", {"start": v(-27.35, 10.71) * mm, "mid": v(-27.39, 11.02) * mm, "end": v(-27.25, 11.3) * mm});
            skPoint(sketch, "E184.10.9", {"position": v(-26.08, 11.24) * mm});
            skArc(sketch, "E184.10.10", {"start": v(-26.42, 11.1) * mm, "mid": v(-26.6, 11.56) * mm, "end": v(-26.76, 12.04) * mm, "construction": true});
            skArc(sketch, "E184.10.11", {"start": v(-26.08, 11.24) * mm, "mid": v(-25.88, 10.8) * mm, "end": v(-25.66, 10.37) * mm});
            skPoint(sketch, "E184.10.12", {"position": v(-26.42, 11.1) * mm});
            skArc(sketch, "E184.10.13", {"start": v(-26.38, 10.33) * mm, "mid": v(-26.31, 10.2) * mm, "end": v(-26.24, 10.06) * mm});
            skArc(sketch, "E184.10.14", {"start": v(-27, 11.5) * mm, "mid": v(-26.94, 11.57) * mm, "end": v(-26.94, 11.67) * mm});
            skArc(sketch, "E184.10.15", {"start": v(-26.55, 10.4) * mm, "mid": v(-26.45, 10.4) * mm, "end": v(-26.38, 10.33) * mm});
            skArc(sketch, "E184.11.0", {"start": v(-25.78, 8.53) * mm, "mid": v(-25.62, 8.57) * mm, "end": v(-25.47, 8.63) * mm});
            skArc(sketch, "E184.11.1", {"start": v(-26.32, 8.78) * mm, "mid": v(-26.08, 8.58) * mm, "end": v(-25.78, 8.53) * mm});
            skArc(sketch, "E184.11.2", {"start": v(-25.17, 9.54) * mm, "mid": v(-25.43, 9.95) * mm, "end": v(-25.66, 10.37) * mm});
            skPoint(sketch, "E184.11.3", {"position": v(-25.7, 9.2) * mm});
            skArc(sketch, "E184.11.4", {"start": v(-26.33, 9.36) * mm, "mid": v(-26.24, 9.5) * mm, "end": v(-26.13, 9.61) * mm});
            skLineSegment(sketch, "E184.11.5", {"start": v(-24.6, 8.77) * mm, "end": v(-25.1, 8.35) * mm});
            skArc(sketch, "E184.11.6", {"start": v(-26.1, 9.8) * mm, "mid": v(-26.17, 9.93) * mm, "end": v(-26.24, 10.06) * mm});
            skLineSegment(sketch, "E184.11.7", {"start": v(-25.66, 10.37) * mm, "end": v(-26.24, 10.06) * mm});
            skArc(sketch, "E184.11.8", {"start": v(-26.32, 8.78) * mm, "mid": v(-26.4, 9.07) * mm, "end": v(-26.33, 9.36) * mm});
            skPoint(sketch, "E184.11.9", {"position": v(-25.17, 9.54) * mm});
            skArc(sketch, "E184.11.10", {"start": v(-25.48, 9.33) * mm, "mid": v(-25.75, 9.76) * mm, "end": v(-26, 10.2) * mm, "construction": true});
            skArc(sketch, "E184.11.11", {"start": v(-25.17, 9.54) * mm, "mid": v(-24.9, 9.15) * mm, "end": v(-24.6, 8.77) * mm});
            skPoint(sketch, "E184.11.12", {"position": v(-25.48, 9.33) * mm});
            skArc(sketch, "E184.11.13", {"start": v(-25.29, 8.59) * mm, "mid": v(-25.2, 8.47) * mm, "end": v(-25.1, 8.35) * mm});
            skArc(sketch, "E184.11.14", {"start": v(-26.13, 9.61) * mm, "mid": v(-26.08, 9.7) * mm, "end": v(-26.1, 9.8) * mm});
            skArc(sketch, "E184.11.15", {"start": v(-25.47, 8.63) * mm, "mid": v(-25.37, 8.64) * mm, "end": v(-25.29, 8.59) * mm});
            skArc(sketch, "E184.12.0", {"start": v(-24.35, 6.95) * mm, "mid": v(-24.2, 7) * mm, "end": v(-24.07, 7.1) * mm});
            skArc(sketch, "E184.12.1", {"start": v(-24.92, 7.08) * mm, "mid": v(-24.65, 6.93) * mm, "end": v(-24.35, 6.95) * mm});
            skArc(sketch, "E184.12.2", {"start": v(-23.95, 8.05) * mm, "mid": v(-24.28, 8.4) * mm, "end": v(-24.6, 8.77) * mm});
            skPoint(sketch, "E184.12.3", {"position": v(-24.4, 7.6) * mm});
            skArc(sketch, "E184.12.4", {"start": v(-25.05, 7.65) * mm, "mid": v(-25, 7.8) * mm, "end": v(-24.9, 7.93) * mm});
            skLineSegment(sketch, "E184.12.5", {"start": v(-23.23, 7.4) * mm, "end": v(-23.65, 6.9) * mm});
            skArc(sketch, "E184.12.6", {"start": v(-24.9, 8.12) * mm, "mid": v(-25, 8.24) * mm, "end": v(-25.1, 8.35) * mm});
            skLineSegment(sketch, "E184.12.7", {"start": v(-24.6, 8.77) * mm, "end": v(-25.1, 8.35) * mm});
            skArc(sketch, "E184.12.8", {"start": v(-24.92, 7.08) * mm, "mid": v(-25.07, 7.35) * mm, "end": v(-25.05, 7.65) * mm});
            skPoint(sketch, "E184.12.9", {"position": v(-23.95, 8.05) * mm});
            skArc(sketch, "E184.12.10", {"start": v(-24.21, 7.79) * mm, "mid": v(-24.56, 8.15) * mm, "end": v(-24.88, 8.53) * mm, "construction": true});
            skArc(sketch, "E184.12.11", {"start": v(-23.95, 8.05) * mm, "mid": v(-23.6, 7.72) * mm, "end": v(-23.23, 7.4) * mm});
            skPoint(sketch, "E184.12.12", {"position": v(-24.21, 7.79) * mm});
            skArc(sketch, "E184.12.13", {"start": v(-23.88, 7.1) * mm, "mid": v(-23.76, 7) * mm, "end": v(-23.65, 6.9) * mm});
            skArc(sketch, "E184.12.14", {"start": v(-24.9, 7.93) * mm, "mid": v(-24.87, 8.03) * mm, "end": v(-24.9, 8.12) * mm});
            skArc(sketch, "E184.12.15", {"start": v(-24.07, 7.1) * mm, "mid": v(-23.97, 7.13) * mm, "end": v(-23.88, 7.1) * mm});
            skArc(sketch, "E184.13.0", {"start": v(-22.64, 5.67) * mm, "mid": v(-22.5, 5.76) * mm, "end": v(-22.39, 5.87) * mm});
            skArc(sketch, "E184.13.1", {"start": v(-23.22, 5.68) * mm, "mid": v(-22.93, 5.6) * mm, "end": v(-22.64, 5.67) * mm});
            skArc(sketch, "E184.13.2", {"start": v(-22.46, 6.83) * mm, "mid": v(-22.85, 7.1) * mm, "end": v(-23.23, 7.4) * mm});
            skPoint(sketch, "E184.13.3", {"position": v(-22.8, 6.3) * mm});
            skArc(sketch, "E184.13.4", {"start": v(-23.47, 6.22) * mm, "mid": v(-23.43, 6.38) * mm, "end": v(-23.37, 6.53) * mm});
            skLineSegment(sketch, "E184.13.5", {"start": v(-21.63, 6.34) * mm, "end": v(-21.94, 5.76) * mm});
            skArc(sketch, "E184.13.6", {"start": v(-23.41, 6.71) * mm, "mid": v(-23.53, 6.8) * mm, "end": v(-23.65, 6.9) * mm});
            skLineSegment(sketch, "E184.13.7", {"start": v(-23.23, 7.4) * mm, "end": v(-23.65, 6.9) * mm});
            skArc(sketch, "E184.13.8", {"start": v(-23.22, 5.68) * mm, "mid": v(-23.42, 5.92) * mm, "end": v(-23.47, 6.22) * mm});
            skPoint(sketch, "E184.13.9", {"position": v(-22.46, 6.83) * mm});
            skArc(sketch, "E184.13.10", {"start": v(-22.67, 6.52) * mm, "mid": v(-23.08, 6.8) * mm, "end": v(-23.47, 7.12) * mm, "construction": true});
            skArc(sketch, "E184.13.11", {"start": v(-22.46, 6.83) * mm, "mid": v(-22.05, 6.57) * mm, "end": v(-21.63, 6.34) * mm});
            skPoint(sketch, "E184.13.12", {"position": v(-22.67, 6.52) * mm});
            skArc(sketch, "E184.13.13", {"start": v(-22.2, 5.9) * mm, "mid": v(-22.07, 5.83) * mm, "end": v(-21.94, 5.76) * mm});
            skArc(sketch, "E184.13.14", {"start": v(-23.37, 6.53) * mm, "mid": v(-23.36, 6.63) * mm, "end": v(-23.41, 6.71) * mm});
            skArc(sketch, "E184.13.15", {"start": v(-22.39, 5.87) * mm, "mid": v(-22.3, 5.92) * mm, "end": v(-22.2, 5.9) * mm});
            skArc(sketch, "E184.14.0", {"start": v(-20.7, 4.75) * mm, "mid": v(-20.6, 4.86) * mm, "end": v(-20.5, 5) * mm});
            skArc(sketch, "E184.14.1", {"start": v(-21.29, 4.65) * mm, "mid": v(-20.98, 4.61) * mm, "end": v(-20.7, 4.75) * mm});
            skArc(sketch, "E184.14.2", {"start": v(-20.76, 5.92) * mm, "mid": v(-21.2, 6.12) * mm, "end": v(-21.63, 6.34) * mm});
            skPoint(sketch, "E184.14.3", {"position": v(-21, 5.34) * mm});
            skArc(sketch, "E184.14.4", {"start": v(-21.63, 5.13) * mm, "mid": v(-21.63, 5.29) * mm, "end": v(-21.6, 5.45) * mm});
            skLineSegment(sketch, "E184.14.5", {"start": v(-19.85, 5.6) * mm, "end": v(-20.04, 4.97) * mm});
            skArc(sketch, "E184.14.6", {"start": v(-21.67, 5.62) * mm, "mid": v(-21.8, 5.69) * mm, "end": v(-21.94, 5.76) * mm});
            skLineSegment(sketch, "E184.14.7", {"start": v(-21.63, 6.34) * mm, "end": v(-21.94, 5.76) * mm});
            skArc(sketch, "E184.14.8", {"start": v(-21.29, 4.65) * mm, "mid": v(-21.53, 4.84) * mm, "end": v(-21.63, 5.13) * mm});
            skPoint(sketch, "E184.14.9", {"position": v(-20.76, 5.92) * mm});
            skArc(sketch, "E184.14.10", {"start": v(-20.9, 5.58) * mm, "mid": v(-21.36, 5.78) * mm, "end": v(-21.8, 6) * mm, "construction": true});
            skArc(sketch, "E184.14.11", {"start": v(-20.76, 5.92) * mm, "mid": v(-20.3, 5.75) * mm, "end": v(-19.85, 5.6) * mm});
            skPoint(sketch, "E184.14.12", {"position": v(-20.9, 5.58) * mm});
            skArc(sketch, "E184.14.13", {"start": v(-20.33, 5.06) * mm, "mid": v(-20.18, 5.02) * mm, "end": v(-20.04, 4.97) * mm});
            skArc(sketch, "E184.14.14", {"start": v(-21.6, 5.45) * mm, "mid": v(-21.6, 5.55) * mm, "end": v(-21.67, 5.62) * mm});
            skArc(sketch, "E184.14.15", {"start": v(-20.5, 5) * mm, "mid": v(-20.43, 5.06) * mm, "end": v(-20.33, 5.06) * mm});
            skArc(sketch, "E184.15.0", {"start": v(-18.64, 4.22) * mm, "mid": v(-18.55, 4.36) * mm, "end": v(-18.48, 4.5) * mm});
            skArc(sketch, "E184.15.1", {"start": v(-19.19, 4.01) * mm, "mid": v(-18.88, 4.04) * mm, "end": v(-18.64, 4.22) * mm});
            skArc(sketch, "E184.15.2", {"start": v(-18.92, 5.36) * mm, "mid": v(-19.39, 5.47) * mm, "end": v(-19.85, 5.6) * mm});
            skPoint(sketch, "E184.15.3", {"position": v(-19.04, 4.75) * mm});
            skArc(sketch, "E184.15.4", {"start": v(-19.61, 4.41) * mm, "mid": v(-19.64, 4.57) * mm, "end": v(-19.64, 4.73) * mm});
            skLineSegment(sketch, "E184.15.5", {"start": v(-17.96, 5.22) * mm, "end": v(-18.03, 4.57) * mm});
            skArc(sketch, "E184.15.6", {"start": v(-19.76, 4.89) * mm, "mid": v(-19.9, 4.93) * mm, "end": v(-20.04, 4.97) * mm});
            skLineSegment(sketch, "E184.15.7", {"start": v(-19.85, 5.6) * mm, "end": v(-20.04, 4.97) * mm});
            skArc(sketch, "E184.15.8", {"start": v(-19.19, 4.01) * mm, "mid": v(-19.46, 4.15) * mm, "end": v(-19.61, 4.41) * mm});
            skPoint(sketch, "E184.15.9", {"position": v(-18.92, 5.36) * mm});
            skArc(sketch, "E184.15.10", {"start": v(-18.99, 5) * mm, "mid": v(-19.48, 5.1) * mm, "end": v(-19.96, 5.24) * mm, "construction": true});
            skArc(sketch, "E184.15.11", {"start": v(-18.92, 5.36) * mm, "mid": v(-18.44, 5.28) * mm, "end": v(-17.96, 5.22) * mm});
            skPoint(sketch, "E184.15.12", {"position": v(-18.99, 5) * mm});
            skArc(sketch, "E184.15.13", {"start": v(-18.32, 4.6) * mm, "mid": v(-18.18, 4.59) * mm, "end": v(-18.03, 4.57) * mm});
            skArc(sketch, "E184.15.14", {"start": v(-19.64, 4.73) * mm, "mid": v(-19.67, 4.83) * mm, "end": v(-19.76, 4.89) * mm});
            skArc(sketch, "E184.15.15", {"start": v(-18.48, 4.5) * mm, "mid": v(-18.42, 4.58) * mm, "end": v(-18.32, 4.6) * mm});
            skArc(sketch, "E184.16.0", {"start": v(-16.5, 4.1) * mm, "mid": v(-16.44, 4.26) * mm, "end": v(-16.4, 4.42) * mm});
            skArc(sketch, "E184.16.1", {"start": v(-17, 3.8) * mm, "mid": v(-16.7, 3.88) * mm, "end": v(-16.5, 4.1) * mm});
            skArc(sketch, "E184.16.2", {"start": v(-17, 5.18) * mm, "mid": v(-17.48, 5.19) * mm, "end": v(-17.96, 5.22) * mm});
            skPoint(sketch, "E184.16.3", {"position": v(-17, 4.55) * mm});
            skArc(sketch, "E184.16.4", {"start": v(-17.5, 4.1) * mm, "mid": v(-17.56, 4.26) * mm, "end": v(-17.6, 4.42) * mm});
            skLineSegment(sketch, "E184.16.5", {"start": v(-16.04, 5.22) * mm, "end": v(-15.97, 4.57) * mm});
            skArc(sketch, "E184.16.6", {"start": v(-17.73, 4.55) * mm, "mid": v(-17.88, 4.56) * mm, "end": v(-18.03, 4.57) * mm});
            skLineSegment(sketch, "E184.16.7", {"start": v(-17.96, 5.22) * mm, "end": v(-18.03, 4.57) * mm});
            skArc(sketch, "E184.16.8", {"start": v(-17, 3.8) * mm, "mid": v(-17.3, 3.88) * mm, "end": v(-17.5, 4.1) * mm});
            skPoint(sketch, "E184.16.9", {"position": v(-17, 5.18) * mm});
            skArc(sketch, "E184.16.10", {"start": v(-17, 4.8) * mm, "mid": v(-17.5, 4.81) * mm, "end": v(-18, 4.85) * mm, "construction": true});
            skArc(sketch, "E184.16.11", {"start": v(-17, 5.18) * mm, "mid": v(-16.52, 5.19) * mm, "end": v(-16.04, 5.22) * mm});
            skPoint(sketch, "E184.16.12", {"position": v(-17, 4.8) * mm});
            skArc(sketch, "E184.16.13", {"start": v(-16.27, 4.55) * mm, "mid": v(-16.12, 4.56) * mm, "end": v(-15.97, 4.57) * mm});
            skArc(sketch, "E184.16.14", {"start": v(-17.6, 4.42) * mm, "mid": v(-17.64, 4.5) * mm, "end": v(-17.73, 4.55) * mm});
            skArc(sketch, "E184.16.15", {"start": v(-16.4, 4.42) * mm, "mid": v(-16.36, 4.5) * mm, "end": v(-16.27, 4.55) * mm});
            skArc(sketch, "E184.17.0", {"start": v(-14.39, 4.41) * mm, "mid": v(-14.36, 4.57) * mm, "end": v(-14.36, 4.73) * mm});
            skArc(sketch, "E184.17.1", {"start": v(-14.81, 4.01) * mm, "mid": v(-14.54, 4.15) * mm, "end": v(-14.39, 4.41) * mm});
            skArc(sketch, "E184.17.2", {"start": v(-15.08, 5.36) * mm, "mid": v(-15.56, 5.28) * mm, "end": v(-16.04, 5.22) * mm});
            skPoint(sketch, "E184.17.3", {"position": v(-14.96, 4.75) * mm});
            skArc(sketch, "E184.17.4", {"start": v(-15.36, 4.22) * mm, "mid": v(-15.45, 4.36) * mm, "end": v(-15.52, 4.5) * mm});
            skLineSegment(sketch, "E184.17.5", {"start": v(-14.15, 5.6) * mm, "end": v(-13.96, 4.97) * mm});
            skArc(sketch, "E184.17.6", {"start": v(-15.68, 4.6) * mm, "mid": v(-15.82, 4.59) * mm, "end": v(-15.97, 4.57) * mm});
            skLineSegment(sketch, "E184.17.7", {"start": v(-16.04, 5.22) * mm, "end": v(-15.97, 4.57) * mm});
            skArc(sketch, "E184.17.8", {"start": v(-14.81, 4.01) * mm, "mid": v(-15.12, 4.04) * mm, "end": v(-15.36, 4.22) * mm});
            skPoint(sketch, "E184.17.9", {"position": v(-15.08, 5.36) * mm});
            skArc(sketch, "E184.17.10", {"start": v(-15.01, 5) * mm, "mid": v(-15.5, 4.91) * mm, "end": v(-16, 4.85) * mm, "construction": true});
            skArc(sketch, "E184.17.11", {"start": v(-15.08, 5.36) * mm, "mid": v(-14.61, 5.47) * mm, "end": v(-14.15, 5.6) * mm});
            skPoint(sketch, "E184.17.12", {"position": v(-15.01, 5) * mm});
            skArc(sketch, "E184.17.13", {"start": v(-14.24, 4.89) * mm, "mid": v(-14.1, 4.93) * mm, "end": v(-13.96, 4.97) * mm});
            skArc(sketch, "E184.17.14", {"start": v(-15.52, 4.5) * mm, "mid": v(-15.58, 4.58) * mm, "end": v(-15.68, 4.6) * mm});
            skArc(sketch, "E184.17.15", {"start": v(-14.36, 4.73) * mm, "mid": v(-14.33, 4.83) * mm, "end": v(-14.24, 4.89) * mm});
            skArc(sketch, "E184.18.0", {"start": v(-12.37, 5.13) * mm, "mid": v(-12.37, 5.29) * mm, "end": v(-12.4, 5.45) * mm});
            skArc(sketch, "E184.18.1", {"start": v(-12.71, 4.65) * mm, "mid": v(-12.47, 4.84) * mm, "end": v(-12.37, 5.13) * mm});
            skArc(sketch, "E184.18.2", {"start": v(-13.24, 5.92) * mm, "mid": v(-13.7, 5.75) * mm, "end": v(-14.15, 5.6) * mm});
            skPoint(sketch, "E184.18.3", {"position": v(-13, 5.34) * mm});
            skArc(sketch, "E184.18.4", {"start": v(-13.3, 4.75) * mm, "mid": v(-13.4, 4.86) * mm, "end": v(-13.5, 5) * mm});
            skLineSegment(sketch, "E184.18.5", {"start": v(-12.37, 6.34) * mm, "end": v(-12.06, 5.76) * mm});
            skArc(sketch, "E184.18.6", {"start": v(-13.67, 5.06) * mm, "mid": v(-13.82, 5.02) * mm, "end": v(-13.96, 4.97) * mm});
            skLineSegment(sketch, "E184.18.7", {"start": v(-14.15, 5.6) * mm, "end": v(-13.96, 4.97) * mm});
            skArc(sketch, "E184.18.8", {"start": v(-12.71, 4.65) * mm, "mid": v(-13.02, 4.61) * mm, "end": v(-13.3, 4.75) * mm});
            skPoint(sketch, "E184.18.9", {"position": v(-13.24, 5.92) * mm});
            skArc(sketch, "E184.18.10", {"start": v(-13.1, 5.58) * mm, "mid": v(-13.56, 5.4) * mm, "end": v(-14.04, 5.24) * mm, "construction": true});
            skArc(sketch, "E184.18.11", {"start": v(-13.24, 5.92) * mm, "mid": v(-12.8, 6.12) * mm, "end": v(-12.37, 6.34) * mm});
            skPoint(sketch, "E184.18.12", {"position": v(-13.1, 5.58) * mm});
            skArc(sketch, "E184.18.13", {"start": v(-12.33, 5.62) * mm, "mid": v(-12.2, 5.69) * mm, "end": v(-12.06, 5.76) * mm});
            skArc(sketch, "E184.18.14", {"start": v(-13.5, 5) * mm, "mid": v(-13.57, 5.06) * mm, "end": v(-13.67, 5.06) * mm});
            skArc(sketch, "E184.18.15", {"start": v(-12.4, 5.45) * mm, "mid": v(-12.4, 5.55) * mm, "end": v(-12.33, 5.62) * mm});
            skArc(sketch, "E184.19.0", {"start": v(-10.53, 6.22) * mm, "mid": v(-10.57, 6.38) * mm, "end": v(-10.63, 6.53) * mm});
            skArc(sketch, "E184.19.1", {"start": v(-10.78, 5.68) * mm, "mid": v(-10.58, 5.92) * mm, "end": v(-10.53, 6.22) * mm});
            skArc(sketch, "E184.19.2", {"start": v(-11.54, 6.83) * mm, "mid": v(-11.95, 6.57) * mm, "end": v(-12.37, 6.34) * mm});
            skPoint(sketch, "E184.19.3", {"position": v(-11.2, 6.3) * mm});
            skArc(sketch, "E184.19.4", {"start": v(-11.36, 5.67) * mm, "mid": v(-11.5, 5.76) * mm, "end": v(-11.61, 5.87) * mm});
            skLineSegment(sketch, "E184.19.5", {"start": v(-10.77, 7.4) * mm, "end": v(-10.35, 6.9) * mm});
            skArc(sketch, "E184.19.6", {"start": v(-11.8, 5.9) * mm, "mid": v(-11.93, 5.83) * mm, "end": v(-12.06, 5.76) * mm});
            skLineSegment(sketch, "E184.19.7", {"start": v(-12.37, 6.34) * mm, "end": v(-12.06, 5.76) * mm});
            skArc(sketch, "E184.19.8", {"start": v(-10.78, 5.68) * mm, "mid": v(-11.07, 5.6) * mm, "end": v(-11.36, 5.67) * mm});
            skPoint(sketch, "E184.19.9", {"position": v(-11.54, 6.83) * mm});
            skArc(sketch, "E184.19.10", {"start": v(-11.33, 6.52) * mm, "mid": v(-11.76, 6.25) * mm, "end": v(-12.2, 6) * mm, "construction": true});
            skArc(sketch, "E184.19.11", {"start": v(-11.54, 6.83) * mm, "mid": v(-11.15, 7.1) * mm, "end": v(-10.77, 7.4) * mm});
            skPoint(sketch, "E184.19.12", {"position": v(-11.33, 6.52) * mm});
            skArc(sketch, "E184.19.13", {"start": v(-10.59, 6.71) * mm, "mid": v(-10.47, 6.8) * mm, "end": v(-10.35, 6.9) * mm});
            skArc(sketch, "E184.19.14", {"start": v(-11.61, 5.87) * mm, "mid": v(-11.7, 5.92) * mm, "end": v(-11.8, 5.9) * mm});
            skArc(sketch, "E184.19.15", {"start": v(-10.63, 6.53) * mm, "mid": v(-10.64, 6.63) * mm, "end": v(-10.59, 6.71) * mm});
            skArc(sketch, "E184.20.0", {"start": v(-8.95, 7.65) * mm, "mid": v(-9, 7.8) * mm, "end": v(-9.1, 7.93) * mm});
            skArc(sketch, "E184.20.1", {"start": v(-9.08, 7.08) * mm, "mid": v(-8.93, 7.35) * mm, "end": v(-8.95, 7.65) * mm});
            skArc(sketch, "E184.20.2", {"start": v(-10.05, 8.05) * mm, "mid": v(-10.4, 7.72) * mm, "end": v(-10.77, 7.4) * mm});
            skPoint(sketch, "E184.20.3", {"position": v(-9.6, 7.6) * mm});
            skArc(sketch, "E184.20.4", {"start": v(-9.65, 6.95) * mm, "mid": v(-9.8, 7) * mm, "end": v(-9.93, 7.1) * mm});
            skLineSegment(sketch, "E184.20.5", {"start": v(-9.4, 8.77) * mm, "end": v(-8.9, 8.35) * mm});
            skArc(sketch, "E184.20.6", {"start": v(-10.12, 7.1) * mm, "mid": v(-10.24, 7) * mm, "end": v(-10.35, 6.9) * mm});
            skLineSegment(sketch, "E184.20.7", {"start": v(-10.77, 7.4) * mm, "end": v(-10.35, 6.9) * mm});
            skArc(sketch, "E184.20.8", {"start": v(-9.08, 7.08) * mm, "mid": v(-9.35, 6.93) * mm, "end": v(-9.65, 6.95) * mm});
            skPoint(sketch, "E184.20.9", {"position": v(-10.05, 8.05) * mm});
            skArc(sketch, "E184.20.10", {"start": v(-9.79, 7.79) * mm, "mid": v(-10.15, 7.44) * mm, "end": v(-10.53, 7.12) * mm, "construction": true});
            skArc(sketch, "E184.20.11", {"start": v(-10.05, 8.05) * mm, "mid": v(-9.72, 8.4) * mm, "end": v(-9.4, 8.77) * mm});
            skPoint(sketch, "E184.20.12", {"position": v(-9.79, 7.79) * mm});
            skArc(sketch, "E184.20.13", {"start": v(-9.1, 8.12) * mm, "mid": v(-9, 8.24) * mm, "end": v(-8.9, 8.35) * mm});
            skArc(sketch, "E184.20.14", {"start": v(-9.93, 7.1) * mm, "mid": v(-10.03, 7.13) * mm, "end": v(-10.12, 7.1) * mm});
            skArc(sketch, "E184.20.15", {"start": v(-9.1, 7.93) * mm, "mid": v(-9.13, 8.03) * mm, "end": v(-9.1, 8.12) * mm});
            skArc(sketch, "E184.21.0", {"start": v(-7.67, 9.36) * mm, "mid": v(-7.76, 9.5) * mm, "end": v(-7.87, 9.61) * mm});
            skArc(sketch, "E184.21.1", {"start": v(-7.68, 8.78) * mm, "mid": v(-7.6, 9.07) * mm, "end": v(-7.67, 9.36) * mm});
            skArc(sketch, "E184.21.2", {"start": v(-8.83, 9.54) * mm, "mid": v(-9.1, 9.15) * mm, "end": v(-9.4, 8.77) * mm});
            skPoint(sketch, "E184.21.3", {"position": v(-8.3, 9.2) * mm});
            skArc(sketch, "E184.21.4", {"start": v(-8.22, 8.53) * mm, "mid": v(-8.38, 8.57) * mm, "end": v(-8.53, 8.63) * mm});
            skLineSegment(sketch, "E184.21.5", {"start": v(-8.34, 10.37) * mm, "end": v(-7.76, 10.06) * mm});
            skArc(sketch, "E184.21.6", {"start": v(-8.71, 8.59) * mm, "mid": v(-8.8, 8.47) * mm, "end": v(-8.9, 8.35) * mm});
            skLineSegment(sketch, "E184.21.7", {"start": v(-9.4, 8.77) * mm, "end": v(-8.9, 8.35) * mm});
            skArc(sketch, "E184.21.8", {"start": v(-7.68, 8.78) * mm, "mid": v(-7.92, 8.58) * mm, "end": v(-8.22, 8.53) * mm});
            skPoint(sketch, "E184.21.9", {"position": v(-8.83, 9.54) * mm});
            skArc(sketch, "E184.21.10", {"start": v(-8.52, 9.33) * mm, "mid": v(-8.8, 8.92) * mm, "end": v(-9.12, 8.53) * mm, "construction": true});
            skArc(sketch, "E184.21.11", {"start": v(-8.83, 9.54) * mm, "mid": v(-8.57, 9.95) * mm, "end": v(-8.34, 10.37) * mm});
            skPoint(sketch, "E184.21.12", {"position": v(-8.52, 9.33) * mm});
            skArc(sketch, "E184.21.13", {"start": v(-7.9, 9.8) * mm, "mid": v(-7.83, 9.93) * mm, "end": v(-7.76, 10.06) * mm});
            skArc(sketch, "E184.21.14", {"start": v(-8.53, 8.63) * mm, "mid": v(-8.63, 8.64) * mm, "end": v(-8.71, 8.59) * mm});
            skArc(sketch, "E184.21.15", {"start": v(-7.87, 9.61) * mm, "mid": v(-7.92, 9.7) * mm, "end": v(-7.9, 9.8) * mm});
            skArc(sketch, "E184.22.0", {"start": v(-6.75, 11.3) * mm, "mid": v(-6.86, 11.4) * mm, "end": v(-7, 11.5) * mm});
            skArc(sketch, "E184.22.1", {"start": v(-6.65, 10.71) * mm, "mid": v(-6.61, 11.02) * mm, "end": v(-6.75, 11.3) * mm});
            skArc(sketch, "E184.22.2", {"start": v(-7.92, 11.24) * mm, "mid": v(-8.12, 10.8) * mm, "end": v(-8.34, 10.37) * mm});
            skPoint(sketch, "E184.22.3", {"position": v(-7.34, 11) * mm});
            skArc(sketch, "E184.22.4", {"start": v(-7.13, 10.37) * mm, "mid": v(-7.29, 10.37) * mm, "end": v(-7.45, 10.4) * mm});
            skLineSegment(sketch, "E184.22.5", {"start": v(-7.6, 12.15) * mm, "end": v(-6.97, 11.96) * mm});
            skArc(sketch, "E184.22.6", {"start": v(-7.62, 10.33) * mm, "mid": v(-7.69, 10.2) * mm, "end": v(-7.76, 10.06) * mm});
            skLineSegment(sketch, "E184.22.7", {"start": v(-8.34, 10.37) * mm, "end": v(-7.76, 10.06) * mm});
            skArc(sketch, "E184.22.8", {"start": v(-6.65, 10.71) * mm, "mid": v(-6.84, 10.47) * mm, "end": v(-7.13, 10.37) * mm});
            skPoint(sketch, "E184.22.9", {"position": v(-7.92, 11.24) * mm});
            skArc(sketch, "E184.22.10", {"start": v(-7.58, 11.1) * mm, "mid": v(-7.78, 10.64) * mm, "end": v(-8, 10.2) * mm, "construction": true});
            skArc(sketch, "E184.22.11", {"start": v(-7.92, 11.24) * mm, "mid": v(-7.75, 11.7) * mm, "end": v(-7.6, 12.15) * mm});
            skPoint(sketch, "E184.22.12", {"position": v(-7.58, 11.1) * mm});
            skArc(sketch, "E184.22.13", {"start": v(-7.06, 11.67) * mm, "mid": v(-7.02, 11.82) * mm, "end": v(-6.97, 11.96) * mm});
            skArc(sketch, "E184.22.14", {"start": v(-7.45, 10.4) * mm, "mid": v(-7.55, 10.4) * mm, "end": v(-7.62, 10.33) * mm});
            skArc(sketch, "E184.22.15", {"start": v(-7, 11.5) * mm, "mid": v(-7.06, 11.57) * mm, "end": v(-7.06, 11.67) * mm});
            skArc(sketch, "E184.23.0", {"start": v(-6.22, 13.36) * mm, "mid": v(-6.36, 13.45) * mm, "end": v(-6.5, 13.52) * mm});
            skArc(sketch, "E184.23.1", {"start": v(-6.01, 12.81) * mm, "mid": v(-6.04, 13.12) * mm, "end": v(-6.22, 13.36) * mm});
            skArc(sketch, "E184.23.2", {"start": v(-7.36, 13.08) * mm, "mid": v(-7.47, 12.61) * mm, "end": v(-7.6, 12.15) * mm});
            skPoint(sketch, "E184.23.3", {"position": v(-6.75, 12.96) * mm});
            skArc(sketch, "E184.23.4", {"start": v(-6.41, 12.39) * mm, "mid": v(-6.57, 12.36) * mm, "end": v(-6.73, 12.36) * mm});
            skLineSegment(sketch, "E184.23.5", {"start": v(-7.22, 14.04) * mm, "end": v(-6.57, 13.97) * mm});
            skArc(sketch, "E184.23.6", {"start": v(-6.89, 12.24) * mm, "mid": v(-6.93, 12.1) * mm, "end": v(-6.97, 11.96) * mm});
            skLineSegment(sketch, "E184.23.7", {"start": v(-7.6, 12.15) * mm, "end": v(-6.97, 11.96) * mm});
            skArc(sketch, "E184.23.8", {"start": v(-6.01, 12.81) * mm, "mid": v(-6.15, 12.54) * mm, "end": v(-6.41, 12.39) * mm});
            skPoint(sketch, "E184.23.9", {"position": v(-7.36, 13.08) * mm});
            skArc(sketch, "E184.23.10", {"start": v(-7, 13.01) * mm, "mid": v(-7.1, 12.52) * mm, "end": v(-7.24, 12.04) * mm, "construction": true});
            skArc(sketch, "E184.23.11", {"start": v(-7.36, 13.08) * mm, "mid": v(-7.28, 13.56) * mm, "end": v(-7.22, 14.04) * mm});
            skPoint(sketch, "E184.23.12", {"position": v(-7, 13.01) * mm});
            skArc(sketch, "E184.23.13", {"start": v(-6.6, 13.68) * mm, "mid": v(-6.59, 13.82) * mm, "end": v(-6.57, 13.97) * mm});
            skArc(sketch, "E184.23.14", {"start": v(-6.73, 12.36) * mm, "mid": v(-6.83, 12.33) * mm, "end": v(-6.89, 12.24) * mm});
            skArc(sketch, "E184.23.15", {"start": v(-6.5, 13.52) * mm, "mid": v(-6.58, 13.58) * mm, "end": v(-6.6, 13.68) * mm});
            skArc(sketch, "E184.24.0", {"start": v(-6.1, 15.5) * mm, "mid": v(-6.26, 15.56) * mm, "end": v(-6.42, 15.6) * mm});
            skArc(sketch, "E184.24.1", {"start": v(-5.8, 15) * mm, "mid": v(-5.88, 15.3) * mm, "end": v(-6.1, 15.5) * mm});
            skArc(sketch, "E184.24.2", {"start": v(-7.18, 15) * mm, "mid": v(-7.19, 14.52) * mm, "end": v(-7.22, 14.04) * mm});
            skPoint(sketch, "E184.24.3", {"position": v(-6.55, 15) * mm});
            skArc(sketch, "E184.24.4", {"start": v(-6.1, 14.5) * mm, "mid": v(-6.26, 14.44) * mm, "end": v(-6.42, 14.4) * mm});
            skLineSegment(sketch, "E184.24.5", {"start": v(-7.22, 15.96) * mm, "end": v(-6.57, 16.03) * mm});
            skArc(sketch, "E184.24.6", {"start": v(-6.55, 14.27) * mm, "mid": v(-6.56, 14.12) * mm, "end": v(-6.57, 13.97) * mm});
            skLineSegment(sketch, "E184.24.7", {"start": v(-7.22, 14.04) * mm, "end": v(-6.57, 13.97) * mm});
            skArc(sketch, "E184.24.8", {"start": v(-5.8, 15) * mm, "mid": v(-5.88, 14.7) * mm, "end": v(-6.1, 14.5) * mm});
            skPoint(sketch, "E184.24.9", {"position": v(-7.18, 15) * mm});
            skArc(sketch, "E184.24.10", {"start": v(-6.8, 15) * mm, "mid": v(-6.81, 14.5) * mm, "end": v(-6.85, 14) * mm, "construction": true});
            skArc(sketch, "E184.24.11", {"start": v(-7.18, 15) * mm, "mid": v(-7.19, 15.48) * mm, "end": v(-7.22, 15.96) * mm});
            skPoint(sketch, "E184.24.12", {"position": v(-6.8, 15) * mm});
            skArc(sketch, "E184.24.13", {"start": v(-6.55, 15.73) * mm, "mid": v(-6.56, 15.88) * mm, "end": v(-6.57, 16.03) * mm});
            skArc(sketch, "E184.24.14", {"start": v(-6.42, 14.4) * mm, "mid": v(-6.5, 14.36) * mm, "end": v(-6.55, 14.27) * mm});
            skArc(sketch, "E184.24.15", {"start": v(-6.42, 15.6) * mm, "mid": v(-6.5, 15.64) * mm, "end": v(-6.55, 15.73) * mm});
            skArc(sketch, "E184.25.0", {"start": v(-6.41, 17.61) * mm, "mid": v(-6.57, 17.64) * mm, "end": v(-6.73, 17.64) * mm});
            skArc(sketch, "E184.25.1", {"start": v(-6.01, 17.19) * mm, "mid": v(-6.15, 17.46) * mm, "end": v(-6.41, 17.61) * mm});
            skArc(sketch, "E184.25.2", {"start": v(-7.36, 16.92) * mm, "mid": v(-7.28, 16.44) * mm, "end": v(-7.22, 15.96) * mm});
            skPoint(sketch, "E184.25.3", {"position": v(-6.75, 17.04) * mm});
            skArc(sketch, "E184.25.4", {"start": v(-6.22, 16.64) * mm, "mid": v(-6.36, 16.55) * mm, "end": v(-6.5, 16.48) * mm});
            skLineSegment(sketch, "E184.25.5", {"start": v(-7.6, 17.85) * mm, "end": v(-6.97, 18.04) * mm});
            skArc(sketch, "E184.25.6", {"start": v(-6.6, 16.32) * mm, "mid": v(-6.59, 16.18) * mm, "end": v(-6.57, 16.03) * mm});
            skLineSegment(sketch, "E184.25.7", {"start": v(-7.22, 15.96) * mm, "end": v(-6.57, 16.03) * mm});
            skArc(sketch, "E184.25.8", {"start": v(-6.01, 17.19) * mm, "mid": v(-6.04, 16.88) * mm, "end": v(-6.22, 16.64) * mm});
            skPoint(sketch, "E184.25.9", {"position": v(-7.36, 16.92) * mm});
            skArc(sketch, "E184.25.10", {"start": v(-7, 16.99) * mm, "mid": v(-6.91, 16.5) * mm, "end": v(-6.85, 16) * mm, "construction": true});
            skArc(sketch, "E184.25.11", {"start": v(-7.36, 16.92) * mm, "mid": v(-7.47, 17.39) * mm, "end": v(-7.6, 17.85) * mm});
            skPoint(sketch, "E184.25.12", {"position": v(-7, 16.99) * mm});
            skArc(sketch, "E184.25.13", {"start": v(-6.89, 17.76) * mm, "mid": v(-6.93, 17.9) * mm, "end": v(-6.97, 18.04) * mm});
            skArc(sketch, "E184.25.14", {"start": v(-6.5, 16.48) * mm, "mid": v(-6.58, 16.42) * mm, "end": v(-6.6, 16.32) * mm});
            skArc(sketch, "E184.25.15", {"start": v(-6.73, 17.64) * mm, "mid": v(-6.83, 17.67) * mm, "end": v(-6.89, 17.76) * mm});
            skArc(sketch, "E184.26.0", {"start": v(-7.13, 19.63) * mm, "mid": v(-7.29, 19.63) * mm, "end": v(-7.45, 19.6) * mm});
            skArc(sketch, "E184.26.1", {"start": v(-6.65, 19.29) * mm, "mid": v(-6.84, 19.53) * mm, "end": v(-7.13, 19.63) * mm});
            skArc(sketch, "E184.26.2", {"start": v(-7.92, 18.76) * mm, "mid": v(-7.75, 18.3) * mm, "end": v(-7.6, 17.85) * mm});
            skPoint(sketch, "E184.26.3", {"position": v(-7.34, 19) * mm});
            skArc(sketch, "E184.26.4", {"start": v(-6.75, 18.7) * mm, "mid": v(-6.86, 18.6) * mm, "end": v(-7, 18.5) * mm});
            skLineSegment(sketch, "E184.26.5", {"start": v(-8.34, 19.63) * mm, "end": v(-7.76, 19.94) * mm});
            skArc(sketch, "E184.26.6", {"start": v(-7.06, 18.33) * mm, "mid": v(-7.02, 18.18) * mm, "end": v(-6.97, 18.04) * mm});
            skLineSegment(sketch, "E184.26.7", {"start": v(-7.6, 17.85) * mm, "end": v(-6.97, 18.04) * mm});
            skArc(sketch, "E184.26.8", {"start": v(-6.65, 19.29) * mm, "mid": v(-6.61, 18.98) * mm, "end": v(-6.75, 18.7) * mm});
            skPoint(sketch, "E184.26.9", {"position": v(-7.92, 18.76) * mm});
            skArc(sketch, "E184.26.10", {"start": v(-7.58, 18.9) * mm, "mid": v(-7.4, 18.44) * mm, "end": v(-7.24, 17.96) * mm, "construction": true});
            skArc(sketch, "E184.26.11", {"start": v(-7.92, 18.76) * mm, "mid": v(-8.12, 19.2) * mm, "end": v(-8.34, 19.63) * mm});
            skPoint(sketch, "E184.26.12", {"position": v(-7.58, 18.9) * mm});
            skArc(sketch, "E184.26.13", {"start": v(-7.62, 19.67) * mm, "mid": v(-7.69, 19.8) * mm, "end": v(-7.76, 19.94) * mm});
            skArc(sketch, "E184.26.14", {"start": v(-7, 18.5) * mm, "mid": v(-7.06, 18.43) * mm, "end": v(-7.06, 18.33) * mm});
            skArc(sketch, "E184.26.15", {"start": v(-7.45, 19.6) * mm, "mid": v(-7.55, 19.6) * mm, "end": v(-7.62, 19.67) * mm});
            skArc(sketch, "E184.27.0", {"start": v(-8.22, 21.47) * mm, "mid": v(-8.38, 21.43) * mm, "end": v(-8.53, 21.37) * mm});
            skArc(sketch, "E184.27.1", {"start": v(-7.68, 21.22) * mm, "mid": v(-7.92, 21.42) * mm, "end": v(-8.22, 21.47) * mm});
            skArc(sketch, "E184.27.2", {"start": v(-8.83, 20.46) * mm, "mid": v(-8.57, 20.05) * mm, "end": v(-8.34, 19.63) * mm});
            skPoint(sketch, "E184.27.3", {"position": v(-8.3, 20.8) * mm});
            skArc(sketch, "E184.27.4", {"start": v(-7.67, 20.64) * mm, "mid": v(-7.76, 20.5) * mm, "end": v(-7.87, 20.39) * mm});
            skLineSegment(sketch, "E184.27.5", {"start": v(-9.4, 21.23) * mm, "end": v(-8.9, 21.65) * mm});
            skArc(sketch, "E184.27.6", {"start": v(-7.9, 20.2) * mm, "mid": v(-7.83, 20.07) * mm, "end": v(-7.76, 19.94) * mm});
            skLineSegment(sketch, "E184.27.7", {"start": v(-8.34, 19.63) * mm, "end": v(-7.76, 19.94) * mm});
            skArc(sketch, "E184.27.8", {"start": v(-7.68, 21.22) * mm, "mid": v(-7.6, 20.93) * mm, "end": v(-7.67, 20.64) * mm});
            skPoint(sketch, "E184.27.9", {"position": v(-8.83, 20.46) * mm});
            skArc(sketch, "E184.27.10", {"start": v(-8.52, 20.67) * mm, "mid": v(-8.25, 20.24) * mm, "end": v(-8, 19.8) * mm, "construction": true});
            skArc(sketch, "E184.27.11", {"start": v(-8.83, 20.46) * mm, "mid": v(-9.1, 20.85) * mm, "end": v(-9.4, 21.23) * mm});
            skPoint(sketch, "E184.27.12", {"position": v(-8.52, 20.67) * mm});
            skArc(sketch, "E184.27.13", {"start": v(-8.71, 21.41) * mm, "mid": v(-8.8, 21.53) * mm, "end": v(-8.9, 21.65) * mm});
            skArc(sketch, "E184.27.14", {"start": v(-7.87, 20.39) * mm, "mid": v(-7.92, 20.3) * mm, "end": v(-7.9, 20.2) * mm});
            skArc(sketch, "E184.27.15", {"start": v(-8.53, 21.37) * mm, "mid": v(-8.63, 21.36) * mm, "end": v(-8.71, 21.41) * mm});
            skArc(sketch, "E184.28.0", {"start": v(-9.65, 23.05) * mm, "mid": v(-9.8, 23) * mm, "end": v(-9.93, 22.9) * mm});
            skArc(sketch, "E184.28.1", {"start": v(-9.08, 22.92) * mm, "mid": v(-9.35, 23.07) * mm, "end": v(-9.65, 23.05) * mm});
            skArc(sketch, "E184.28.2", {"start": v(-10.05, 21.95) * mm, "mid": v(-9.72, 21.6) * mm, "end": v(-9.4, 21.23) * mm});
            skPoint(sketch, "E184.28.3", {"position": v(-9.6, 22.4) * mm});
            skArc(sketch, "E184.28.4", {"start": v(-8.95, 22.35) * mm, "mid": v(-9, 22.2) * mm, "end": v(-9.1, 22.07) * mm});
            skLineSegment(sketch, "E184.28.5", {"start": v(-10.77, 22.6) * mm, "end": v(-10.35, 23.1) * mm});
            skArc(sketch, "E184.28.6", {"start": v(-9.1, 21.88) * mm, "mid": v(-9, 21.76) * mm, "end": v(-8.9, 21.65) * mm});
            skLineSegment(sketch, "E184.28.7", {"start": v(-9.4, 21.23) * mm, "end": v(-8.9, 21.65) * mm});
            skArc(sketch, "E184.28.8", {"start": v(-9.08, 22.92) * mm, "mid": v(-8.93, 22.65) * mm, "end": v(-8.95, 22.35) * mm});
            skPoint(sketch, "E184.28.9", {"position": v(-10.05, 21.95) * mm});
            skArc(sketch, "E184.28.10", {"start": v(-9.79, 22.21) * mm, "mid": v(-9.44, 21.85) * mm, "end": v(-9.12, 21.47) * mm, "construction": true});
            skArc(sketch, "E184.28.11", {"start": v(-10.05, 21.95) * mm, "mid": v(-10.4, 22.28) * mm, "end": v(-10.77, 22.6) * mm});
            skPoint(sketch, "E184.28.12", {"position": v(-9.79, 22.21) * mm});
            skArc(sketch, "E184.28.13", {"start": v(-10.12, 22.9) * mm, "mid": v(-10.24, 23) * mm, "end": v(-10.35, 23.1) * mm});
            skArc(sketch, "E184.28.14", {"start": v(-9.1, 22.07) * mm, "mid": v(-9.13, 21.97) * mm, "end": v(-9.1, 21.88) * mm});
            skArc(sketch, "E184.28.15", {"start": v(-9.93, 22.9) * mm, "mid": v(-10.03, 22.87) * mm, "end": v(-10.12, 22.9) * mm});
            skArc(sketch, "E184.29.0", {"start": v(-11.36, 24.33) * mm, "mid": v(-11.5, 24.24) * mm, "end": v(-11.61, 24.13) * mm});
            skArc(sketch, "E184.29.1", {"start": v(-10.78, 24.32) * mm, "mid": v(-11.07, 24.4) * mm, "end": v(-11.36, 24.33) * mm});
            skArc(sketch, "E184.29.2", {"start": v(-11.54, 23.17) * mm, "mid": v(-11.15, 22.9) * mm, "end": v(-10.77, 22.6) * mm});
            skPoint(sketch, "E184.29.3", {"position": v(-11.2, 23.7) * mm});
            skArc(sketch, "E184.29.4", {"start": v(-10.53, 23.78) * mm, "mid": v(-10.57, 23.62) * mm, "end": v(-10.63, 23.47) * mm});
            skLineSegment(sketch, "E184.29.5", {"start": v(-12.37, 23.66) * mm, "end": v(-12.06, 24.24) * mm});
            skArc(sketch, "E184.29.6", {"start": v(-10.59, 23.29) * mm, "mid": v(-10.47, 23.2) * mm, "end": v(-10.35, 23.1) * mm});
            skLineSegment(sketch, "E184.29.7", {"start": v(-10.77, 22.6) * mm, "end": v(-10.35, 23.1) * mm});
            skArc(sketch, "E184.29.8", {"start": v(-10.78, 24.32) * mm, "mid": v(-10.58, 24.08) * mm, "end": v(-10.53, 23.78) * mm});
            skPoint(sketch, "E184.29.9", {"position": v(-11.54, 23.17) * mm});
            skArc(sketch, "E184.29.10", {"start": v(-11.33, 23.48) * mm, "mid": v(-10.92, 23.2) * mm, "end": v(-10.53, 22.88) * mm, "construction": true});
            skArc(sketch, "E184.29.11", {"start": v(-11.54, 23.17) * mm, "mid": v(-11.95, 23.43) * mm, "end": v(-12.37, 23.66) * mm});
            skPoint(sketch, "E184.29.12", {"position": v(-11.33, 23.48) * mm});
            skArc(sketch, "E184.29.13", {"start": v(-11.8, 24.1) * mm, "mid": v(-11.93, 24.17) * mm, "end": v(-12.06, 24.24) * mm});
            skArc(sketch, "E184.29.14", {"start": v(-10.63, 23.47) * mm, "mid": v(-10.64, 23.37) * mm, "end": v(-10.59, 23.29) * mm});
            skArc(sketch, "E184.29.15", {"start": v(-11.61, 24.13) * mm, "mid": v(-11.7, 24.08) * mm, "end": v(-11.8, 24.1) * mm});
            skArc(sketch, "E184.30.0", {"start": v(-13.3, 25.25) * mm, "mid": v(-13.4, 25.14) * mm, "end": v(-13.5, 25) * mm});
            skArc(sketch, "E184.30.1", {"start": v(-12.71, 25.35) * mm, "mid": v(-13.02, 25.39) * mm, "end": v(-13.3, 25.25) * mm});
            skArc(sketch, "E184.30.2", {"start": v(-13.24, 24.08) * mm, "mid": v(-12.8, 23.88) * mm, "end": v(-12.37, 23.66) * mm});
            skPoint(sketch, "E184.30.3", {"position": v(-13, 24.66) * mm});
            skArc(sketch, "E184.30.4", {"start": v(-12.37, 24.87) * mm, "mid": v(-12.37, 24.71) * mm, "end": v(-12.4, 24.55) * mm});
            skLineSegment(sketch, "E184.30.5", {"start": v(-14.15, 24.4) * mm, "end": v(-13.96, 25.03) * mm});
            skArc(sketch, "E184.30.6", {"start": v(-12.33, 24.38) * mm, "mid": v(-12.2, 24.31) * mm, "end": v(-12.06, 24.24) * mm});
            skLineSegment(sketch, "E184.30.7", {"start": v(-12.37, 23.66) * mm, "end": v(-12.06, 24.24) * mm});
            skArc(sketch, "E184.30.8", {"start": v(-12.71, 25.35) * mm, "mid": v(-12.47, 25.16) * mm, "end": v(-12.37, 24.87) * mm});
            skPoint(sketch, "E184.30.9", {"position": v(-13.24, 24.08) * mm});
            skArc(sketch, "E184.30.10", {"start": v(-13.1, 24.42) * mm, "mid": v(-12.64, 24.22) * mm, "end": v(-12.2, 24) * mm, "construction": true});
            skArc(sketch, "E184.30.11", {"start": v(-13.24, 24.08) * mm, "mid": v(-13.7, 24.25) * mm, "end": v(-14.15, 24.4) * mm});
            skPoint(sketch, "E184.30.12", {"position": v(-13.1, 24.42) * mm});
            skArc(sketch, "E184.30.13", {"start": v(-13.67, 24.94) * mm, "mid": v(-13.82, 24.98) * mm, "end": v(-13.96, 25.03) * mm});
            skArc(sketch, "E184.30.14", {"start": v(-12.4, 24.55) * mm, "mid": v(-12.4, 24.45) * mm, "end": v(-12.33, 24.38) * mm});
            skArc(sketch, "E184.30.15", {"start": v(-13.5, 25) * mm, "mid": v(-13.57, 24.94) * mm, "end": v(-13.67, 24.94) * mm});
            skArc(sketch, "E184.31.0", {"start": v(-15.36, 25.78) * mm, "mid": v(-15.45, 25.64) * mm, "end": v(-15.52, 25.5) * mm});
            skArc(sketch, "E184.31.1", {"start": v(-14.81, 25.99) * mm, "mid": v(-15.12, 25.96) * mm, "end": v(-15.36, 25.78) * mm});
            skArc(sketch, "E184.31.2", {"start": v(-15.08, 24.64) * mm, "mid": v(-14.61, 24.53) * mm, "end": v(-14.15, 24.4) * mm});
            skPoint(sketch, "E184.31.3", {"position": v(-14.96, 25.25) * mm});
            skArc(sketch, "E184.31.4", {"start": v(-14.39, 25.59) * mm, "mid": v(-14.36, 25.43) * mm, "end": v(-14.36, 25.27) * mm});
            skArc(sketch, "E184.31.6", {"start": v(-14.24, 25.11) * mm, "mid": v(-14.1, 25.07) * mm, "end": v(-13.96, 25.03) * mm});
            skLineSegment(sketch, "E184.31.7", {"start": v(-14.15, 24.4) * mm, "end": v(-13.96, 25.03) * mm});
            skArc(sketch, "E184.31.8", {"start": v(-14.81, 25.99) * mm, "mid": v(-14.54, 25.85) * mm, "end": v(-14.39, 25.59) * mm});
            skPoint(sketch, "E184.31.9", {"position": v(-15.08, 24.64) * mm});
            skArc(sketch, "E184.31.10", {"start": v(-15.01, 25) * mm, "mid": v(-14.52, 24.9) * mm, "end": v(-14.04, 24.76) * mm, "construction": true});
            skArc(sketch, "E184.31.11", {"start": v(-15.08, 24.64) * mm, "mid": v(-15.56, 24.72) * mm, "end": v(-16.04, 24.78) * mm});
            skPoint(sketch, "E184.31.12", {"position": v(-15.01, 25) * mm});
            skArc(sketch, "E184.31.13", {"start": v(-15.68, 25.4) * mm, "mid": v(-15.82, 25.41) * mm, "end": v(-15.97, 25.43) * mm});
            skArc(sketch, "E184.31.14", {"start": v(-14.36, 25.27) * mm, "mid": v(-14.33, 25.17) * mm, "end": v(-14.24, 25.11) * mm});
            skArc(sketch, "E184.31.15", {"start": v(-15.52, 25.5) * mm, "mid": v(-15.58, 25.42) * mm, "end": v(-15.68, 25.4) * mm});
            skLineSegment(sketch, "E185.0", {"start": v(-27.25, 15) * mm, "end": v(-6.75, 15) * mm});
            skSolve(sketch);
        }
        {
            var Q0;
            Q0=qSketchRegion(id+"F28",true);
            extrude(context, id + "F29", {"entities" : qUnion([Q0]), "operationType" : NewBodyOperationType.REMOVE, "endBound" : BoundingType.SYMMETRIC, "oppositeDirection" : true, "depth" : 6.5 * mm});
        }
        {
            var Q0;
            Q0=makeQuery(id+"F2.boolean.opBoolean","MERGE",FACE,{"derivedFrom":[makeQuery(id+"F1.opExtrude","SWEPT_FACE",FACE,{"disambiguationData":[OSD([sQuery(id+"F0.wireOp",EDGE,"E4"),sQuery(id+"F0.wireOp",EDGE,"E22")])]}),makeQuery(id+"F2.opExtrude","SWEPT_FACE",FACE,{"disambiguationData":[OSD([sQuery(id+"F0.wireOp",EDGE,"E35")])]})]});
            var Q1;
            Q1=sQuery(id+"F0.wireOp",VERTEX,"E19.MirrorP");
            cPlane(context, id + "F30", {"entities" : qUnion([Q0, Q1]), "cplaneType" : CPlaneType.PLANE_POINT, "offset" : 150 * mm, "width" : 150 * mm, "height" : 150 * mm});
        }
        {
            var Q0;
            Q0=qCreatedBy(id+"F30.planeOp",FACE);
            var sketch = newSketch(context, id + "F31", { "sketchPlane" : qUnion([Q0])});
            skLineSegment(sketch, "E186", {"start": v(-17, 12.16) * mm, "end": v(-17, 9.53) * mm, "construction": true});
            skArc(sketch, "E187", {"start": v(-17, 26.2) * mm, "mid": v(-16.7, 26.12) * mm, "end": v(-16.5, 25.9) * mm});
            skArc(sketch, "E188", {"start": v(-16.5, 25.9) * mm, "mid": v(-16.44, 25.74) * mm, "end": v(-16.4, 25.58) * mm});
            skArc(sketch, "E189", {"start": v(-16.4, 25.58) * mm, "mid": v(-16.36, 25.5) * mm, "end": v(-16.27, 25.45) * mm});
            skPoint(sketch, "E190", {"position": v(-17, 24.82) * mm});
            skPoint(sketch, "E191", {"position": v(-17, 25.45) * mm});
            skPoint(sketch, "E192", {"position": v(-17, 25.2) * mm});
            skArc(sketch, "E193", {"start": v(-17, 25.2) * mm, "mid": v(-16.5, 25.19) * mm, "end": v(-16, 25.15) * mm, "construction": true});
            skLineSegment(sketch, "E194", {"start": v(-16.04, 24.78) * mm, "end": v(-15.97, 25.43) * mm});
            skArc(sketch, "E195", {"start": v(-16.27, 25.45) * mm, "mid": v(-16.12, 25.44) * mm, "end": v(-15.97, 25.43) * mm});
            skArc(sketch, "E196", {"start": v(-17, 24.82) * mm, "mid": v(-16.52, 24.81) * mm, "end": v(-16.04, 24.78) * mm});
            skArc(sketch, "E197.MirrorCS", {"start": v(-17, 26.2) * mm, "mid": v(-17.3, 26.12) * mm, "end": v(-17.5, 25.9) * mm});
            skArc(sketch, "E198.MirrorCS", {"start": v(-17.5, 25.9) * mm, "mid": v(-17.56, 25.74) * mm, "end": v(-17.6, 25.58) * mm});
            skArc(sketch, "E199.MirrorCS", {"start": v(-17.6, 25.58) * mm, "mid": v(-17.64, 25.5) * mm, "end": v(-17.73, 25.45) * mm});
            skArc(sketch, "E200.MirrorCS", {"start": v(-17.73, 25.45) * mm, "mid": v(-17.88, 25.44) * mm, "end": v(-18.03, 25.43) * mm});
            skLineSegment(sketch, "E201.MirrorCS", {"start": v(-17.96, 24.78) * mm, "end": v(-18.03, 25.43) * mm});
            skArc(sketch, "E202.MirrorCS", {"start": v(-17, 24.82) * mm, "mid": v(-17.48, 24.81) * mm, "end": v(-17.96, 24.78) * mm});
            skArc(sketch, "E203.1.0", {"start": v(-19.61, 25.59) * mm, "mid": v(-19.64, 25.43) * mm, "end": v(-19.64, 25.27) * mm});
            skArc(sketch, "E203.1.1", {"start": v(-19.19, 25.99) * mm, "mid": v(-19.46, 25.85) * mm, "end": v(-19.61, 25.59) * mm});
            skArc(sketch, "E203.1.2", {"start": v(-18.92, 24.64) * mm, "mid": v(-18.44, 24.72) * mm, "end": v(-17.96, 24.78) * mm});
            skPoint(sketch, "E203.1.3", {"position": v(-19.04, 25.25) * mm});
            skArc(sketch, "E203.1.4", {"start": v(-18.64, 25.78) * mm, "mid": v(-18.55, 25.64) * mm, "end": v(-18.48, 25.5) * mm});
            skLineSegment(sketch, "E203.1.5", {"start": v(-19.85, 24.4) * mm, "end": v(-20.04, 25.03) * mm});
            skArc(sketch, "E203.1.6", {"start": v(-18.32, 25.4) * mm, "mid": v(-18.18, 25.41) * mm, "end": v(-18.03, 25.43) * mm});
            skArc(sketch, "E203.1.8", {"start": v(-19.19, 25.99) * mm, "mid": v(-18.88, 25.96) * mm, "end": v(-18.64, 25.78) * mm});
            skPoint(sketch, "E203.1.9", {"position": v(-18.92, 24.64) * mm});
            skArc(sketch, "E203.1.10", {"start": v(-18.99, 25) * mm, "mid": v(-18.5, 25.09) * mm, "end": v(-18, 25.15) * mm, "construction": true});
            skArc(sketch, "E203.1.11", {"start": v(-18.92, 24.64) * mm, "mid": v(-19.39, 24.53) * mm, "end": v(-19.85, 24.4) * mm});
            skPoint(sketch, "E203.1.12", {"position": v(-18.99, 25) * mm});
            skArc(sketch, "E203.1.13", {"start": v(-19.76, 25.11) * mm, "mid": v(-19.9, 25.07) * mm, "end": v(-20.04, 25.03) * mm});
            skArc(sketch, "E203.1.14", {"start": v(-18.48, 25.5) * mm, "mid": v(-18.42, 25.42) * mm, "end": v(-18.32, 25.4) * mm});
            skArc(sketch, "E203.1.15", {"start": v(-19.64, 25.27) * mm, "mid": v(-19.67, 25.17) * mm, "end": v(-19.76, 25.11) * mm});
            skArc(sketch, "E203.2.0", {"start": v(-21.63, 24.87) * mm, "mid": v(-21.63, 24.71) * mm, "end": v(-21.6, 24.55) * mm});
            skArc(sketch, "E203.2.1", {"start": v(-21.29, 25.35) * mm, "mid": v(-21.53, 25.16) * mm, "end": v(-21.63, 24.87) * mm});
            skArc(sketch, "E203.2.2", {"start": v(-20.76, 24.08) * mm, "mid": v(-20.3, 24.25) * mm, "end": v(-19.85, 24.4) * mm});
            skPoint(sketch, "E203.2.3", {"position": v(-21, 24.66) * mm});
            skArc(sketch, "E203.2.4", {"start": v(-20.7, 25.25) * mm, "mid": v(-20.6, 25.14) * mm, "end": v(-20.5, 25) * mm});
            skLineSegment(sketch, "E203.2.5", {"start": v(-21.63, 23.66) * mm, "end": v(-21.94, 24.24) * mm});
            skArc(sketch, "E203.2.6", {"start": v(-20.33, 24.94) * mm, "mid": v(-20.18, 24.98) * mm, "end": v(-20.04, 25.03) * mm});
            skLineSegment(sketch, "E203.2.7", {"start": v(-19.85, 24.4) * mm, "end": v(-20.04, 25.03) * mm});
            skArc(sketch, "E203.2.8", {"start": v(-21.29, 25.35) * mm, "mid": v(-20.98, 25.39) * mm, "end": v(-20.7, 25.25) * mm});
            skPoint(sketch, "E203.2.9", {"position": v(-20.76, 24.08) * mm});
            skArc(sketch, "E203.2.10", {"start": v(-20.9, 24.42) * mm, "mid": v(-20.44, 24.6) * mm, "end": v(-19.96, 24.76) * mm, "construction": true});
            skArc(sketch, "E203.2.11", {"start": v(-20.76, 24.08) * mm, "mid": v(-21.2, 23.88) * mm, "end": v(-21.63, 23.66) * mm});
            skPoint(sketch, "E203.2.12", {"position": v(-20.9, 24.42) * mm});
            skArc(sketch, "E203.2.13", {"start": v(-21.67, 24.38) * mm, "mid": v(-21.8, 24.31) * mm, "end": v(-21.94, 24.24) * mm});
            skArc(sketch, "E203.2.14", {"start": v(-20.5, 25) * mm, "mid": v(-20.43, 24.94) * mm, "end": v(-20.33, 24.94) * mm});
            skArc(sketch, "E203.2.15", {"start": v(-21.6, 24.55) * mm, "mid": v(-21.6, 24.45) * mm, "end": v(-21.67, 24.38) * mm});
            skArc(sketch, "E203.3.0", {"start": v(-23.47, 23.78) * mm, "mid": v(-23.43, 23.62) * mm, "end": v(-23.37, 23.47) * mm});
            skArc(sketch, "E203.3.1", {"start": v(-23.22, 24.32) * mm, "mid": v(-23.42, 24.08) * mm, "end": v(-23.47, 23.78) * mm});
            skArc(sketch, "E203.3.2", {"start": v(-22.46, 23.17) * mm, "mid": v(-22.05, 23.43) * mm, "end": v(-21.63, 23.66) * mm});
            skPoint(sketch, "E203.3.3", {"position": v(-22.8, 23.7) * mm});
            skArc(sketch, "E203.3.4", {"start": v(-22.64, 24.33) * mm, "mid": v(-22.5, 24.24) * mm, "end": v(-22.39, 24.13) * mm});
            skLineSegment(sketch, "E203.3.5", {"start": v(-23.23, 22.6) * mm, "end": v(-23.65, 23.1) * mm});
            skArc(sketch, "E203.3.6", {"start": v(-22.2, 24.1) * mm, "mid": v(-22.07, 24.17) * mm, "end": v(-21.94, 24.24) * mm});
            skLineSegment(sketch, "E203.3.7", {"start": v(-21.63, 23.66) * mm, "end": v(-21.94, 24.24) * mm});
            skArc(sketch, "E203.3.8", {"start": v(-23.22, 24.32) * mm, "mid": v(-22.93, 24.4) * mm, "end": v(-22.64, 24.33) * mm});
            skPoint(sketch, "E203.3.9", {"position": v(-22.46, 23.17) * mm});
            skArc(sketch, "E203.3.10", {"start": v(-22.67, 23.48) * mm, "mid": v(-22.24, 23.75) * mm, "end": v(-21.8, 24) * mm, "construction": true});
            skArc(sketch, "E203.3.11", {"start": v(-22.46, 23.17) * mm, "mid": v(-22.85, 22.9) * mm, "end": v(-23.23, 22.6) * mm});
            skPoint(sketch, "E203.3.12", {"position": v(-22.67, 23.48) * mm});
            skArc(sketch, "E203.3.13", {"start": v(-23.41, 23.29) * mm, "mid": v(-23.53, 23.2) * mm, "end": v(-23.65, 23.1) * mm});
            skArc(sketch, "E203.3.14", {"start": v(-22.39, 24.13) * mm, "mid": v(-22.3, 24.08) * mm, "end": v(-22.2, 24.1) * mm});
            skArc(sketch, "E203.3.15", {"start": v(-23.37, 23.47) * mm, "mid": v(-23.36, 23.37) * mm, "end": v(-23.41, 23.29) * mm});
            skArc(sketch, "E203.4.0", {"start": v(-25.05, 22.35) * mm, "mid": v(-25, 22.2) * mm, "end": v(-24.9, 22.07) * mm});
            skArc(sketch, "E203.4.1", {"start": v(-24.92, 22.92) * mm, "mid": v(-25.07, 22.65) * mm, "end": v(-25.05, 22.35) * mm});
            skArc(sketch, "E203.4.2", {"start": v(-23.95, 21.95) * mm, "mid": v(-23.6, 22.28) * mm, "end": v(-23.23, 22.6) * mm});
            skPoint(sketch, "E203.4.3", {"position": v(-24.4, 22.4) * mm});
            skArc(sketch, "E203.4.4", {"start": v(-24.35, 23.05) * mm, "mid": v(-24.2, 23) * mm, "end": v(-24.07, 22.9) * mm});
            skLineSegment(sketch, "E203.4.5", {"start": v(-24.6, 21.23) * mm, "end": v(-25.1, 21.65) * mm});
            skArc(sketch, "E203.4.6", {"start": v(-23.88, 22.9) * mm, "mid": v(-23.76, 23) * mm, "end": v(-23.65, 23.1) * mm});
            skLineSegment(sketch, "E203.4.7", {"start": v(-23.23, 22.6) * mm, "end": v(-23.65, 23.1) * mm});
            skArc(sketch, "E203.4.8", {"start": v(-24.92, 22.92) * mm, "mid": v(-24.65, 23.07) * mm, "end": v(-24.35, 23.05) * mm});
            skPoint(sketch, "E203.4.9", {"position": v(-23.95, 21.95) * mm});
            skArc(sketch, "E203.4.10", {"start": v(-24.21, 22.21) * mm, "mid": v(-23.85, 22.56) * mm, "end": v(-23.47, 22.88) * mm, "construction": true});
            skArc(sketch, "E203.4.11", {"start": v(-23.95, 21.95) * mm, "mid": v(-24.28, 21.6) * mm, "end": v(-24.6, 21.23) * mm});
            skPoint(sketch, "E203.4.12", {"position": v(-24.21, 22.21) * mm});
            skArc(sketch, "E203.4.13", {"start": v(-24.9, 21.88) * mm, "mid": v(-25, 21.76) * mm, "end": v(-25.1, 21.65) * mm});
            skArc(sketch, "E203.4.14", {"start": v(-24.07, 22.9) * mm, "mid": v(-23.97, 22.87) * mm, "end": v(-23.88, 22.9) * mm});
            skArc(sketch, "E203.4.15", {"start": v(-24.9, 22.07) * mm, "mid": v(-24.87, 21.97) * mm, "end": v(-24.9, 21.88) * mm});
            skArc(sketch, "E203.5.0", {"start": v(-26.33, 20.64) * mm, "mid": v(-26.24, 20.5) * mm, "end": v(-26.13, 20.39) * mm});
            skArc(sketch, "E203.5.1", {"start": v(-26.32, 21.22) * mm, "mid": v(-26.4, 20.93) * mm, "end": v(-26.33, 20.64) * mm});
            skArc(sketch, "E203.5.2", {"start": v(-25.17, 20.46) * mm, "mid": v(-24.9, 20.85) * mm, "end": v(-24.6, 21.23) * mm});
            skPoint(sketch, "E203.5.3", {"position": v(-25.7, 20.8) * mm});
            skArc(sketch, "E203.5.4", {"start": v(-25.78, 21.47) * mm, "mid": v(-25.62, 21.43) * mm, "end": v(-25.47, 21.37) * mm});
            skLineSegment(sketch, "E203.5.5", {"start": v(-25.66, 19.63) * mm, "end": v(-26.24, 19.94) * mm});
            skArc(sketch, "E203.5.6", {"start": v(-25.29, 21.41) * mm, "mid": v(-25.2, 21.53) * mm, "end": v(-25.1, 21.65) * mm});
            skLineSegment(sketch, "E203.5.7", {"start": v(-24.6, 21.23) * mm, "end": v(-25.1, 21.65) * mm});
            skArc(sketch, "E203.5.8", {"start": v(-26.32, 21.22) * mm, "mid": v(-26.08, 21.42) * mm, "end": v(-25.78, 21.47) * mm});
            skPoint(sketch, "E203.5.9", {"position": v(-25.17, 20.46) * mm});
            skArc(sketch, "E203.5.10", {"start": v(-25.48, 20.67) * mm, "mid": v(-25.2, 21.08) * mm, "end": v(-24.88, 21.47) * mm, "construction": true});
            skArc(sketch, "E203.5.11", {"start": v(-25.17, 20.46) * mm, "mid": v(-25.43, 20.05) * mm, "end": v(-25.66, 19.63) * mm});
            skPoint(sketch, "E203.5.12", {"position": v(-25.48, 20.67) * mm});
            skArc(sketch, "E203.5.13", {"start": v(-26.1, 20.2) * mm, "mid": v(-26.17, 20.07) * mm, "end": v(-26.24, 19.94) * mm});
            skArc(sketch, "E203.5.14", {"start": v(-25.47, 21.37) * mm, "mid": v(-25.37, 21.36) * mm, "end": v(-25.29, 21.41) * mm});
            skArc(sketch, "E203.5.15", {"start": v(-26.13, 20.39) * mm, "mid": v(-26.08, 20.3) * mm, "end": v(-26.1, 20.2) * mm});
            skArc(sketch, "E203.6.0", {"start": v(-27.25, 18.7) * mm, "mid": v(-27.14, 18.6) * mm, "end": v(-27, 18.5) * mm});
            skArc(sketch, "E203.6.1", {"start": v(-27.35, 19.29) * mm, "mid": v(-27.39, 18.98) * mm, "end": v(-27.25, 18.7) * mm});
            skArc(sketch, "E203.6.2", {"start": v(-26.08, 18.76) * mm, "mid": v(-25.88, 19.2) * mm, "end": v(-25.66, 19.63) * mm});
            skPoint(sketch, "E203.6.3", {"position": v(-26.66, 19) * mm});
            skArc(sketch, "E203.6.4", {"start": v(-26.87, 19.63) * mm, "mid": v(-26.71, 19.63) * mm, "end": v(-26.55, 19.6) * mm});
            skLineSegment(sketch, "E203.6.5", {"start": v(-26.4, 17.85) * mm, "end": v(-27.03, 18.04) * mm});
            skArc(sketch, "E203.6.6", {"start": v(-26.38, 19.67) * mm, "mid": v(-26.31, 19.8) * mm, "end": v(-26.24, 19.94) * mm});
            skLineSegment(sketch, "E203.6.7", {"start": v(-25.66, 19.63) * mm, "end": v(-26.24, 19.94) * mm});
            skArc(sketch, "E203.6.8", {"start": v(-27.35, 19.29) * mm, "mid": v(-27.16, 19.53) * mm, "end": v(-26.87, 19.63) * mm});
            skPoint(sketch, "E203.6.9", {"position": v(-26.08, 18.76) * mm});
            skArc(sketch, "E203.6.10", {"start": v(-26.42, 18.9) * mm, "mid": v(-26.22, 19.36) * mm, "end": v(-26, 19.8) * mm, "construction": true});
            skArc(sketch, "E203.6.11", {"start": v(-26.08, 18.76) * mm, "mid": v(-26.25, 18.3) * mm, "end": v(-26.4, 17.85) * mm});
            skPoint(sketch, "E203.6.12", {"position": v(-26.42, 18.9) * mm});
            skArc(sketch, "E203.6.13", {"start": v(-26.94, 18.33) * mm, "mid": v(-26.98, 18.18) * mm, "end": v(-27.03, 18.04) * mm});
            skArc(sketch, "E203.6.14", {"start": v(-26.55, 19.6) * mm, "mid": v(-26.45, 19.6) * mm, "end": v(-26.38, 19.67) * mm});
            skArc(sketch, "E203.6.15", {"start": v(-27, 18.5) * mm, "mid": v(-26.94, 18.43) * mm, "end": v(-26.94, 18.33) * mm});
            skArc(sketch, "E203.7.0", {"start": v(-27.78, 16.64) * mm, "mid": v(-27.64, 16.55) * mm, "end": v(-27.5, 16.48) * mm});
            skArc(sketch, "E203.7.1", {"start": v(-27.99, 17.19) * mm, "mid": v(-27.96, 16.88) * mm, "end": v(-27.78, 16.64) * mm});
            skArc(sketch, "E203.7.2", {"start": v(-26.64, 16.92) * mm, "mid": v(-26.53, 17.39) * mm, "end": v(-26.4, 17.85) * mm});
            skPoint(sketch, "E203.7.3", {"position": v(-27.25, 17.04) * mm});
            skArc(sketch, "E203.7.4", {"start": v(-27.59, 17.61) * mm, "mid": v(-27.43, 17.64) * mm, "end": v(-27.27, 17.64) * mm});
            skLineSegment(sketch, "E203.7.5", {"start": v(-26.78, 15.96) * mm, "end": v(-27.43, 16.03) * mm});
            skArc(sketch, "E203.7.6", {"start": v(-27.11, 17.76) * mm, "mid": v(-27.07, 17.9) * mm, "end": v(-27.03, 18.04) * mm});
            skLineSegment(sketch, "E203.7.7", {"start": v(-26.4, 17.85) * mm, "end": v(-27.03, 18.04) * mm});
            skArc(sketch, "E203.7.8", {"start": v(-27.99, 17.19) * mm, "mid": v(-27.85, 17.46) * mm, "end": v(-27.59, 17.61) * mm});
            skPoint(sketch, "E203.7.9", {"position": v(-26.64, 16.92) * mm});
            skArc(sketch, "E203.7.10", {"start": v(-27, 16.99) * mm, "mid": v(-26.9, 17.48) * mm, "end": v(-26.76, 17.96) * mm, "construction": true});
            skArc(sketch, "E203.7.11", {"start": v(-26.64, 16.92) * mm, "mid": v(-26.72, 16.44) * mm, "end": v(-26.78, 15.96) * mm});
            skPoint(sketch, "E203.7.12", {"position": v(-27, 16.99) * mm});
            skArc(sketch, "E203.7.13", {"start": v(-27.4, 16.32) * mm, "mid": v(-27.41, 16.18) * mm, "end": v(-27.43, 16.03) * mm});
            skArc(sketch, "E203.7.14", {"start": v(-27.27, 17.64) * mm, "mid": v(-27.17, 17.67) * mm, "end": v(-27.11, 17.76) * mm});
            skArc(sketch, "E203.7.15", {"start": v(-27.5, 16.48) * mm, "mid": v(-27.42, 16.42) * mm, "end": v(-27.4, 16.32) * mm});
            skArc(sketch, "E203.8.0", {"start": v(-27.9, 14.5) * mm, "mid": v(-27.74, 14.44) * mm, "end": v(-27.58, 14.4) * mm});
            skArc(sketch, "E203.8.1", {"start": v(-28.2, 15) * mm, "mid": v(-28.12, 14.7) * mm, "end": v(-27.9, 14.5) * mm});
            skArc(sketch, "E203.8.2", {"start": v(-26.82, 15) * mm, "mid": v(-26.81, 15.48) * mm, "end": v(-26.78, 15.96) * mm});
            skPoint(sketch, "E203.8.3", {"position": v(-27.45, 15) * mm});
            skArc(sketch, "E203.8.4", {"start": v(-27.9, 15.5) * mm, "mid": v(-27.74, 15.56) * mm, "end": v(-27.58, 15.6) * mm});
            skLineSegment(sketch, "E203.8.5", {"start": v(-26.78, 14.04) * mm, "end": v(-27.43, 13.97) * mm});
            skArc(sketch, "E203.8.6", {"start": v(-27.45, 15.73) * mm, "mid": v(-27.44, 15.88) * mm, "end": v(-27.43, 16.03) * mm});
            skLineSegment(sketch, "E203.8.7", {"start": v(-26.78, 15.96) * mm, "end": v(-27.43, 16.03) * mm});
            skArc(sketch, "E203.8.8", {"start": v(-28.2, 15) * mm, "mid": v(-28.12, 15.3) * mm, "end": v(-27.9, 15.5) * mm});
            skPoint(sketch, "E203.8.9", {"position": v(-26.82, 15) * mm});
            skArc(sketch, "E203.8.10", {"start": v(-27.2, 15) * mm, "mid": v(-27.19, 15.5) * mm, "end": v(-27.15, 16) * mm, "construction": true});
            skArc(sketch, "E203.8.11", {"start": v(-26.82, 15) * mm, "mid": v(-26.81, 14.52) * mm, "end": v(-26.78, 14.04) * mm});
            skPoint(sketch, "E203.8.12", {"position": v(-27.2, 15) * mm});
            skArc(sketch, "E203.8.13", {"start": v(-27.45, 14.27) * mm, "mid": v(-27.44, 14.12) * mm, "end": v(-27.43, 13.97) * mm});
            skArc(sketch, "E203.8.14", {"start": v(-27.58, 15.6) * mm, "mid": v(-27.5, 15.64) * mm, "end": v(-27.45, 15.73) * mm});
            skArc(sketch, "E203.8.15", {"start": v(-27.58, 14.4) * mm, "mid": v(-27.5, 14.36) * mm, "end": v(-27.45, 14.27) * mm});
            skArc(sketch, "E203.9.0", {"start": v(-27.59, 12.39) * mm, "mid": v(-27.43, 12.36) * mm, "end": v(-27.27, 12.36) * mm});
            skArc(sketch, "E203.9.1", {"start": v(-27.99, 12.81) * mm, "mid": v(-27.85, 12.54) * mm, "end": v(-27.59, 12.39) * mm});
            skArc(sketch, "E203.9.2", {"start": v(-26.64, 13.08) * mm, "mid": v(-26.72, 13.56) * mm, "end": v(-26.78, 14.04) * mm});
            skPoint(sketch, "E203.9.3", {"position": v(-27.25, 12.96) * mm});
            skArc(sketch, "E203.9.4", {"start": v(-27.78, 13.36) * mm, "mid": v(-27.64, 13.45) * mm, "end": v(-27.5, 13.52) * mm});
            skLineSegment(sketch, "E203.9.5", {"start": v(-26.4, 12.15) * mm, "end": v(-27.03, 11.96) * mm});
            skArc(sketch, "E203.9.6", {"start": v(-27.4, 13.68) * mm, "mid": v(-27.41, 13.82) * mm, "end": v(-27.43, 13.97) * mm});
            skLineSegment(sketch, "E203.9.7", {"start": v(-26.78, 14.04) * mm, "end": v(-27.43, 13.97) * mm});
            skArc(sketch, "E203.9.8", {"start": v(-27.99, 12.81) * mm, "mid": v(-27.96, 13.12) * mm, "end": v(-27.78, 13.36) * mm});
            skPoint(sketch, "E203.9.9", {"position": v(-26.64, 13.08) * mm});
            skArc(sketch, "E203.9.10", {"start": v(-27, 13.01) * mm, "mid": v(-27.09, 13.5) * mm, "end": v(-27.15, 14) * mm, "construction": true});
            skArc(sketch, "E203.9.11", {"start": v(-26.64, 13.08) * mm, "mid": v(-26.53, 12.61) * mm, "end": v(-26.4, 12.15) * mm});
            skPoint(sketch, "E203.9.12", {"position": v(-27, 13.01) * mm});
            skArc(sketch, "E203.9.13", {"start": v(-27.11, 12.24) * mm, "mid": v(-27.07, 12.1) * mm, "end": v(-27.03, 11.96) * mm});
            skArc(sketch, "E203.9.14", {"start": v(-27.5, 13.52) * mm, "mid": v(-27.42, 13.58) * mm, "end": v(-27.4, 13.68) * mm});
            skArc(sketch, "E203.9.15", {"start": v(-27.27, 12.36) * mm, "mid": v(-27.17, 12.33) * mm, "end": v(-27.11, 12.24) * mm});
            skArc(sketch, "E203.10.0", {"start": v(-26.87, 10.37) * mm, "mid": v(-26.71, 10.37) * mm, "end": v(-26.55, 10.4) * mm});
            skArc(sketch, "E203.10.1", {"start": v(-27.35, 10.71) * mm, "mid": v(-27.16, 10.47) * mm, "end": v(-26.87, 10.37) * mm});
            skArc(sketch, "E203.10.2", {"start": v(-26.08, 11.24) * mm, "mid": v(-26.25, 11.7) * mm, "end": v(-26.4, 12.15) * mm});
            skPoint(sketch, "E203.10.3", {"position": v(-26.66, 11) * mm});
            skArc(sketch, "E203.10.4", {"start": v(-27.25, 11.3) * mm, "mid": v(-27.14, 11.4) * mm, "end": v(-27, 11.5) * mm});
            skLineSegment(sketch, "E203.10.5", {"start": v(-25.66, 10.37) * mm, "end": v(-26.24, 10.06) * mm});
            skArc(sketch, "E203.10.6", {"start": v(-26.94, 11.67) * mm, "mid": v(-26.98, 11.82) * mm, "end": v(-27.03, 11.96) * mm});
            skLineSegment(sketch, "E203.10.7", {"start": v(-26.4, 12.15) * mm, "end": v(-27.03, 11.96) * mm});
            skArc(sketch, "E203.10.8", {"start": v(-27.35, 10.71) * mm, "mid": v(-27.39, 11.02) * mm, "end": v(-27.25, 11.3) * mm});
            skPoint(sketch, "E203.10.9", {"position": v(-26.08, 11.24) * mm});
            skArc(sketch, "E203.10.10", {"start": v(-26.42, 11.1) * mm, "mid": v(-26.6, 11.56) * mm, "end": v(-26.76, 12.04) * mm, "construction": true});
            skArc(sketch, "E203.10.11", {"start": v(-26.08, 11.24) * mm, "mid": v(-25.88, 10.8) * mm, "end": v(-25.66, 10.37) * mm});
            skPoint(sketch, "E203.10.12", {"position": v(-26.42, 11.1) * mm});
            skArc(sketch, "E203.10.13", {"start": v(-26.38, 10.33) * mm, "mid": v(-26.31, 10.2) * mm, "end": v(-26.24, 10.06) * mm});
            skArc(sketch, "E203.10.14", {"start": v(-27, 11.5) * mm, "mid": v(-26.94, 11.57) * mm, "end": v(-26.94, 11.67) * mm});
            skArc(sketch, "E203.10.15", {"start": v(-26.55, 10.4) * mm, "mid": v(-26.45, 10.4) * mm, "end": v(-26.38, 10.33) * mm});
            skArc(sketch, "E203.11.0", {"start": v(-25.78, 8.53) * mm, "mid": v(-25.62, 8.57) * mm, "end": v(-25.47, 8.63) * mm});
            skArc(sketch, "E203.11.1", {"start": v(-26.32, 8.78) * mm, "mid": v(-26.08, 8.58) * mm, "end": v(-25.78, 8.53) * mm});
            skArc(sketch, "E203.11.2", {"start": v(-25.17, 9.54) * mm, "mid": v(-25.43, 9.95) * mm, "end": v(-25.66, 10.37) * mm});
            skPoint(sketch, "E203.11.3", {"position": v(-25.7, 9.2) * mm});
            skArc(sketch, "E203.11.4", {"start": v(-26.33, 9.36) * mm, "mid": v(-26.24, 9.5) * mm, "end": v(-26.13, 9.61) * mm});
            skLineSegment(sketch, "E203.11.5", {"start": v(-24.6, 8.77) * mm, "end": v(-25.1, 8.35) * mm});
            skArc(sketch, "E203.11.6", {"start": v(-26.1, 9.8) * mm, "mid": v(-26.17, 9.93) * mm, "end": v(-26.24, 10.06) * mm});
            skLineSegment(sketch, "E203.11.7", {"start": v(-25.66, 10.37) * mm, "end": v(-26.24, 10.06) * mm});
            skArc(sketch, "E203.11.8", {"start": v(-26.32, 8.78) * mm, "mid": v(-26.4, 9.07) * mm, "end": v(-26.33, 9.36) * mm});
            skPoint(sketch, "E203.11.9", {"position": v(-25.17, 9.54) * mm});
            skArc(sketch, "E203.11.10", {"start": v(-25.48, 9.33) * mm, "mid": v(-25.75, 9.76) * mm, "end": v(-26, 10.2) * mm, "construction": true});
            skArc(sketch, "E203.11.11", {"start": v(-25.17, 9.54) * mm, "mid": v(-24.9, 9.15) * mm, "end": v(-24.6, 8.77) * mm});
            skPoint(sketch, "E203.11.12", {"position": v(-25.48, 9.33) * mm});
            skArc(sketch, "E203.11.13", {"start": v(-25.29, 8.59) * mm, "mid": v(-25.2, 8.47) * mm, "end": v(-25.1, 8.35) * mm});
            skArc(sketch, "E203.11.14", {"start": v(-26.13, 9.61) * mm, "mid": v(-26.08, 9.7) * mm, "end": v(-26.1, 9.8) * mm});
            skArc(sketch, "E203.11.15", {"start": v(-25.47, 8.63) * mm, "mid": v(-25.37, 8.64) * mm, "end": v(-25.29, 8.59) * mm});
            skArc(sketch, "E203.12.0", {"start": v(-24.35, 6.95) * mm, "mid": v(-24.2, 7) * mm, "end": v(-24.07, 7.1) * mm});
            skArc(sketch, "E203.12.1", {"start": v(-24.92, 7.08) * mm, "mid": v(-24.65, 6.93) * mm, "end": v(-24.35, 6.95) * mm});
            skArc(sketch, "E203.12.2", {"start": v(-23.95, 8.05) * mm, "mid": v(-24.28, 8.4) * mm, "end": v(-24.6, 8.77) * mm});
            skPoint(sketch, "E203.12.3", {"position": v(-24.4, 7.6) * mm});
            skArc(sketch, "E203.12.4", {"start": v(-25.05, 7.65) * mm, "mid": v(-25, 7.8) * mm, "end": v(-24.9, 7.93) * mm});
            skLineSegment(sketch, "E203.12.5", {"start": v(-23.23, 7.4) * mm, "end": v(-23.65, 6.9) * mm});
            skArc(sketch, "E203.12.6", {"start": v(-24.9, 8.12) * mm, "mid": v(-25, 8.24) * mm, "end": v(-25.1, 8.35) * mm});
            skLineSegment(sketch, "E203.12.7", {"start": v(-24.6, 8.77) * mm, "end": v(-25.1, 8.35) * mm});
            skArc(sketch, "E203.12.8", {"start": v(-24.92, 7.08) * mm, "mid": v(-25.07, 7.35) * mm, "end": v(-25.05, 7.65) * mm});
            skPoint(sketch, "E203.12.9", {"position": v(-23.95, 8.05) * mm});
            skArc(sketch, "E203.12.10", {"start": v(-24.21, 7.79) * mm, "mid": v(-24.56, 8.15) * mm, "end": v(-24.88, 8.53) * mm, "construction": true});
            skArc(sketch, "E203.12.11", {"start": v(-23.95, 8.05) * mm, "mid": v(-23.6, 7.72) * mm, "end": v(-23.23, 7.4) * mm});
            skPoint(sketch, "E203.12.12", {"position": v(-24.21, 7.79) * mm});
            skArc(sketch, "E203.12.13", {"start": v(-23.88, 7.1) * mm, "mid": v(-23.76, 7) * mm, "end": v(-23.65, 6.9) * mm});
            skArc(sketch, "E203.12.14", {"start": v(-24.9, 7.93) * mm, "mid": v(-24.87, 8.03) * mm, "end": v(-24.9, 8.12) * mm});
            skArc(sketch, "E203.12.15", {"start": v(-24.07, 7.1) * mm, "mid": v(-23.97, 7.13) * mm, "end": v(-23.88, 7.1) * mm});
            skArc(sketch, "E203.13.0", {"start": v(-22.64, 5.67) * mm, "mid": v(-22.5, 5.76) * mm, "end": v(-22.39, 5.87) * mm});
            skArc(sketch, "E203.13.1", {"start": v(-23.22, 5.68) * mm, "mid": v(-22.93, 5.6) * mm, "end": v(-22.64, 5.67) * mm});
            skArc(sketch, "E203.13.2", {"start": v(-22.46, 6.83) * mm, "mid": v(-22.85, 7.1) * mm, "end": v(-23.23, 7.4) * mm});
            skPoint(sketch, "E203.13.3", {"position": v(-22.8, 6.3) * mm});
            skArc(sketch, "E203.13.4", {"start": v(-23.47, 6.22) * mm, "mid": v(-23.43, 6.38) * mm, "end": v(-23.37, 6.53) * mm});
            skLineSegment(sketch, "E203.13.5", {"start": v(-21.63, 6.34) * mm, "end": v(-21.94, 5.76) * mm});
            skArc(sketch, "E203.13.6", {"start": v(-23.41, 6.71) * mm, "mid": v(-23.53, 6.8) * mm, "end": v(-23.65, 6.9) * mm});
            skLineSegment(sketch, "E203.13.7", {"start": v(-23.23, 7.4) * mm, "end": v(-23.65, 6.9) * mm});
            skArc(sketch, "E203.13.8", {"start": v(-23.22, 5.68) * mm, "mid": v(-23.42, 5.92) * mm, "end": v(-23.47, 6.22) * mm});
            skPoint(sketch, "E203.13.9", {"position": v(-22.46, 6.83) * mm});
            skArc(sketch, "E203.13.10", {"start": v(-22.67, 6.52) * mm, "mid": v(-23.08, 6.8) * mm, "end": v(-23.47, 7.12) * mm, "construction": true});
            skArc(sketch, "E203.13.11", {"start": v(-22.46, 6.83) * mm, "mid": v(-22.05, 6.57) * mm, "end": v(-21.63, 6.34) * mm});
            skPoint(sketch, "E203.13.12", {"position": v(-22.67, 6.52) * mm});
            skArc(sketch, "E203.13.13", {"start": v(-22.2, 5.9) * mm, "mid": v(-22.07, 5.83) * mm, "end": v(-21.94, 5.76) * mm});
            skArc(sketch, "E203.13.14", {"start": v(-23.37, 6.53) * mm, "mid": v(-23.36, 6.63) * mm, "end": v(-23.41, 6.71) * mm});
            skArc(sketch, "E203.13.15", {"start": v(-22.39, 5.87) * mm, "mid": v(-22.3, 5.92) * mm, "end": v(-22.2, 5.9) * mm});
            skArc(sketch, "E203.14.0", {"start": v(-20.7, 4.75) * mm, "mid": v(-20.6, 4.86) * mm, "end": v(-20.5, 5) * mm});
            skArc(sketch, "E203.14.1", {"start": v(-21.29, 4.65) * mm, "mid": v(-20.98, 4.61) * mm, "end": v(-20.7, 4.75) * mm});
            skArc(sketch, "E203.14.2", {"start": v(-20.76, 5.92) * mm, "mid": v(-21.2, 6.12) * mm, "end": v(-21.63, 6.34) * mm});
            skPoint(sketch, "E203.14.3", {"position": v(-21, 5.34) * mm});
            skArc(sketch, "E203.14.4", {"start": v(-21.63, 5.13) * mm, "mid": v(-21.63, 5.29) * mm, "end": v(-21.6, 5.45) * mm});
            skLineSegment(sketch, "E203.14.5", {"start": v(-19.85, 5.6) * mm, "end": v(-20.04, 4.97) * mm});
            skArc(sketch, "E203.14.6", {"start": v(-21.67, 5.62) * mm, "mid": v(-21.8, 5.69) * mm, "end": v(-21.94, 5.76) * mm});
            skLineSegment(sketch, "E203.14.7", {"start": v(-21.63, 6.34) * mm, "end": v(-21.94, 5.76) * mm});
            skArc(sketch, "E203.14.8", {"start": v(-21.29, 4.65) * mm, "mid": v(-21.53, 4.84) * mm, "end": v(-21.63, 5.13) * mm});
            skPoint(sketch, "E203.14.9", {"position": v(-20.76, 5.92) * mm});
            skArc(sketch, "E203.14.10", {"start": v(-20.9, 5.58) * mm, "mid": v(-21.36, 5.78) * mm, "end": v(-21.8, 6) * mm, "construction": true});
            skArc(sketch, "E203.14.11", {"start": v(-20.76, 5.92) * mm, "mid": v(-20.3, 5.75) * mm, "end": v(-19.85, 5.6) * mm});
            skPoint(sketch, "E203.14.12", {"position": v(-20.9, 5.58) * mm});
            skArc(sketch, "E203.14.13", {"start": v(-20.33, 5.06) * mm, "mid": v(-20.18, 5.02) * mm, "end": v(-20.04, 4.97) * mm});
            skArc(sketch, "E203.14.14", {"start": v(-21.6, 5.45) * mm, "mid": v(-21.6, 5.55) * mm, "end": v(-21.67, 5.62) * mm});
            skArc(sketch, "E203.14.15", {"start": v(-20.5, 5) * mm, "mid": v(-20.43, 5.06) * mm, "end": v(-20.33, 5.06) * mm});
            skArc(sketch, "E203.15.0", {"start": v(-18.64, 4.22) * mm, "mid": v(-18.55, 4.36) * mm, "end": v(-18.48, 4.5) * mm});
            skArc(sketch, "E203.15.1", {"start": v(-19.19, 4.01) * mm, "mid": v(-18.88, 4.04) * mm, "end": v(-18.64, 4.22) * mm});
            skArc(sketch, "E203.15.2", {"start": v(-18.92, 5.36) * mm, "mid": v(-19.39, 5.47) * mm, "end": v(-19.85, 5.6) * mm});
            skPoint(sketch, "E203.15.3", {"position": v(-19.04, 4.75) * mm});
            skArc(sketch, "E203.15.4", {"start": v(-19.61, 4.41) * mm, "mid": v(-19.64, 4.57) * mm, "end": v(-19.64, 4.73) * mm});
            skLineSegment(sketch, "E203.15.5", {"start": v(-17.96, 5.22) * mm, "end": v(-18.03, 4.57) * mm});
            skArc(sketch, "E203.15.6", {"start": v(-19.76, 4.89) * mm, "mid": v(-19.9, 4.93) * mm, "end": v(-20.04, 4.97) * mm});
            skLineSegment(sketch, "E203.15.7", {"start": v(-19.85, 5.6) * mm, "end": v(-20.04, 4.97) * mm});
            skArc(sketch, "E203.15.8", {"start": v(-19.19, 4.01) * mm, "mid": v(-19.46, 4.15) * mm, "end": v(-19.61, 4.41) * mm});
            skPoint(sketch, "E203.15.9", {"position": v(-18.92, 5.36) * mm});
            skArc(sketch, "E203.15.10", {"start": v(-18.99, 5) * mm, "mid": v(-19.48, 5.1) * mm, "end": v(-19.96, 5.24) * mm, "construction": true});
            skArc(sketch, "E203.15.11", {"start": v(-18.92, 5.36) * mm, "mid": v(-18.44, 5.28) * mm, "end": v(-17.96, 5.22) * mm});
            skPoint(sketch, "E203.15.12", {"position": v(-18.99, 5) * mm});
            skArc(sketch, "E203.15.13", {"start": v(-18.32, 4.6) * mm, "mid": v(-18.18, 4.59) * mm, "end": v(-18.03, 4.57) * mm});
            skArc(sketch, "E203.15.14", {"start": v(-19.64, 4.73) * mm, "mid": v(-19.67, 4.83) * mm, "end": v(-19.76, 4.89) * mm});
            skArc(sketch, "E203.15.15", {"start": v(-18.48, 4.5) * mm, "mid": v(-18.42, 4.58) * mm, "end": v(-18.32, 4.6) * mm});
            skArc(sketch, "E203.16.0", {"start": v(-16.5, 4.1) * mm, "mid": v(-16.44, 4.26) * mm, "end": v(-16.4, 4.42) * mm});
            skArc(sketch, "E203.16.1", {"start": v(-17, 3.8) * mm, "mid": v(-16.7, 3.88) * mm, "end": v(-16.5, 4.1) * mm});
            skArc(sketch, "E203.16.2", {"start": v(-17, 5.18) * mm, "mid": v(-17.48, 5.19) * mm, "end": v(-17.96, 5.22) * mm});
            skPoint(sketch, "E203.16.3", {"position": v(-17, 4.55) * mm});
            skArc(sketch, "E203.16.4", {"start": v(-17.5, 4.1) * mm, "mid": v(-17.56, 4.26) * mm, "end": v(-17.6, 4.42) * mm});
            skLineSegment(sketch, "E203.16.5", {"start": v(-16.04, 5.22) * mm, "end": v(-15.97, 4.57) * mm});
            skArc(sketch, "E203.16.6", {"start": v(-17.73, 4.55) * mm, "mid": v(-17.88, 4.56) * mm, "end": v(-18.03, 4.57) * mm});
            skLineSegment(sketch, "E203.16.7", {"start": v(-17.96, 5.22) * mm, "end": v(-18.03, 4.57) * mm});
            skArc(sketch, "E203.16.8", {"start": v(-17, 3.8) * mm, "mid": v(-17.3, 3.88) * mm, "end": v(-17.5, 4.1) * mm});
            skPoint(sketch, "E203.16.9", {"position": v(-17, 5.18) * mm});
            skArc(sketch, "E203.16.10", {"start": v(-17, 4.8) * mm, "mid": v(-17.5, 4.81) * mm, "end": v(-18, 4.85) * mm, "construction": true});
            skArc(sketch, "E203.16.11", {"start": v(-17, 5.18) * mm, "mid": v(-16.52, 5.19) * mm, "end": v(-16.04, 5.22) * mm});
            skPoint(sketch, "E203.16.12", {"position": v(-17, 4.8) * mm});
            skArc(sketch, "E203.16.13", {"start": v(-16.27, 4.55) * mm, "mid": v(-16.12, 4.56) * mm, "end": v(-15.97, 4.57) * mm});
            skArc(sketch, "E203.16.14", {"start": v(-17.6, 4.42) * mm, "mid": v(-17.64, 4.5) * mm, "end": v(-17.73, 4.55) * mm});
            skArc(sketch, "E203.16.15", {"start": v(-16.4, 4.42) * mm, "mid": v(-16.36, 4.5) * mm, "end": v(-16.27, 4.55) * mm});
            skArc(sketch, "E203.17.0", {"start": v(-14.39, 4.41) * mm, "mid": v(-14.36, 4.57) * mm, "end": v(-14.36, 4.73) * mm});
            skArc(sketch, "E203.17.1", {"start": v(-14.81, 4.01) * mm, "mid": v(-14.54, 4.15) * mm, "end": v(-14.39, 4.41) * mm});
            skArc(sketch, "E203.17.2", {"start": v(-15.08, 5.36) * mm, "mid": v(-15.56, 5.28) * mm, "end": v(-16.04, 5.22) * mm});
            skPoint(sketch, "E203.17.3", {"position": v(-14.96, 4.75) * mm});
            skArc(sketch, "E203.17.4", {"start": v(-15.36, 4.22) * mm, "mid": v(-15.45, 4.36) * mm, "end": v(-15.52, 4.5) * mm});
            skLineSegment(sketch, "E203.17.5", {"start": v(-14.15, 5.6) * mm, "end": v(-13.96, 4.97) * mm});
            skArc(sketch, "E203.17.6", {"start": v(-15.68, 4.6) * mm, "mid": v(-15.82, 4.59) * mm, "end": v(-15.97, 4.57) * mm});
            skLineSegment(sketch, "E203.17.7", {"start": v(-16.04, 5.22) * mm, "end": v(-15.97, 4.57) * mm});
            skArc(sketch, "E203.17.8", {"start": v(-14.81, 4.01) * mm, "mid": v(-15.12, 4.04) * mm, "end": v(-15.36, 4.22) * mm});
            skPoint(sketch, "E203.17.9", {"position": v(-15.08, 5.36) * mm});
            skArc(sketch, "E203.17.10", {"start": v(-15.01, 5) * mm, "mid": v(-15.5, 4.91) * mm, "end": v(-16, 4.85) * mm, "construction": true});
            skArc(sketch, "E203.17.11", {"start": v(-15.08, 5.36) * mm, "mid": v(-14.61, 5.47) * mm, "end": v(-14.15, 5.6) * mm});
            skPoint(sketch, "E203.17.12", {"position": v(-15.01, 5) * mm});
            skArc(sketch, "E203.17.13", {"start": v(-14.24, 4.89) * mm, "mid": v(-14.1, 4.93) * mm, "end": v(-13.96, 4.97) * mm});
            skArc(sketch, "E203.17.14", {"start": v(-15.52, 4.5) * mm, "mid": v(-15.58, 4.58) * mm, "end": v(-15.68, 4.6) * mm});
            skArc(sketch, "E203.17.15", {"start": v(-14.36, 4.73) * mm, "mid": v(-14.33, 4.83) * mm, "end": v(-14.24, 4.89) * mm});
            skArc(sketch, "E203.18.0", {"start": v(-12.37, 5.13) * mm, "mid": v(-12.37, 5.29) * mm, "end": v(-12.4, 5.45) * mm});
            skArc(sketch, "E203.18.1", {"start": v(-12.71, 4.65) * mm, "mid": v(-12.47, 4.84) * mm, "end": v(-12.37, 5.13) * mm});
            skArc(sketch, "E203.18.2", {"start": v(-13.24, 5.92) * mm, "mid": v(-13.7, 5.75) * mm, "end": v(-14.15, 5.6) * mm});
            skPoint(sketch, "E203.18.3", {"position": v(-13, 5.34) * mm});
            skArc(sketch, "E203.18.4", {"start": v(-13.3, 4.75) * mm, "mid": v(-13.4, 4.86) * mm, "end": v(-13.5, 5) * mm});
            skLineSegment(sketch, "E203.18.5", {"start": v(-12.37, 6.34) * mm, "end": v(-12.06, 5.76) * mm});
            skArc(sketch, "E203.18.6", {"start": v(-13.67, 5.06) * mm, "mid": v(-13.82, 5.02) * mm, "end": v(-13.96, 4.97) * mm});
            skLineSegment(sketch, "E203.18.7", {"start": v(-14.15, 5.6) * mm, "end": v(-13.96, 4.97) * mm});
            skArc(sketch, "E203.18.8", {"start": v(-12.71, 4.65) * mm, "mid": v(-13.02, 4.61) * mm, "end": v(-13.3, 4.75) * mm});
            skPoint(sketch, "E203.18.9", {"position": v(-13.24, 5.92) * mm});
            skArc(sketch, "E203.18.10", {"start": v(-13.1, 5.58) * mm, "mid": v(-13.56, 5.4) * mm, "end": v(-14.04, 5.24) * mm, "construction": true});
            skArc(sketch, "E203.18.11", {"start": v(-13.24, 5.92) * mm, "mid": v(-12.8, 6.12) * mm, "end": v(-12.37, 6.34) * mm});
            skPoint(sketch, "E203.18.12", {"position": v(-13.1, 5.58) * mm});
            skArc(sketch, "E203.18.13", {"start": v(-12.33, 5.62) * mm, "mid": v(-12.2, 5.69) * mm, "end": v(-12.06, 5.76) * mm});
            skArc(sketch, "E203.18.14", {"start": v(-13.5, 5) * mm, "mid": v(-13.57, 5.06) * mm, "end": v(-13.67, 5.06) * mm});
            skArc(sketch, "E203.18.15", {"start": v(-12.4, 5.45) * mm, "mid": v(-12.4, 5.55) * mm, "end": v(-12.33, 5.62) * mm});
            skArc(sketch, "E203.19.0", {"start": v(-10.53, 6.22) * mm, "mid": v(-10.57, 6.38) * mm, "end": v(-10.63, 6.53) * mm});
            skArc(sketch, "E203.19.1", {"start": v(-10.78, 5.68) * mm, "mid": v(-10.58, 5.92) * mm, "end": v(-10.53, 6.22) * mm});
            skArc(sketch, "E203.19.2", {"start": v(-11.54, 6.83) * mm, "mid": v(-11.95, 6.57) * mm, "end": v(-12.37, 6.34) * mm});
            skPoint(sketch, "E203.19.3", {"position": v(-11.2, 6.3) * mm});
            skArc(sketch, "E203.19.4", {"start": v(-11.36, 5.67) * mm, "mid": v(-11.5, 5.76) * mm, "end": v(-11.61, 5.87) * mm});
            skLineSegment(sketch, "E203.19.5", {"start": v(-10.77, 7.4) * mm, "end": v(-10.35, 6.9) * mm});
            skArc(sketch, "E203.19.6", {"start": v(-11.8, 5.9) * mm, "mid": v(-11.93, 5.83) * mm, "end": v(-12.06, 5.76) * mm});
            skLineSegment(sketch, "E203.19.7", {"start": v(-12.37, 6.34) * mm, "end": v(-12.06, 5.76) * mm});
            skArc(sketch, "E203.19.8", {"start": v(-10.78, 5.68) * mm, "mid": v(-11.07, 5.6) * mm, "end": v(-11.36, 5.67) * mm});
            skPoint(sketch, "E203.19.9", {"position": v(-11.54, 6.83) * mm});
            skArc(sketch, "E203.19.10", {"start": v(-11.33, 6.52) * mm, "mid": v(-11.76, 6.25) * mm, "end": v(-12.2, 6) * mm, "construction": true});
            skArc(sketch, "E203.19.11", {"start": v(-11.54, 6.83) * mm, "mid": v(-11.15, 7.1) * mm, "end": v(-10.77, 7.4) * mm});
            skPoint(sketch, "E203.19.12", {"position": v(-11.33, 6.52) * mm});
            skArc(sketch, "E203.19.13", {"start": v(-10.59, 6.71) * mm, "mid": v(-10.47, 6.8) * mm, "end": v(-10.35, 6.9) * mm});
            skArc(sketch, "E203.19.14", {"start": v(-11.61, 5.87) * mm, "mid": v(-11.7, 5.92) * mm, "end": v(-11.8, 5.9) * mm});
            skArc(sketch, "E203.19.15", {"start": v(-10.63, 6.53) * mm, "mid": v(-10.64, 6.63) * mm, "end": v(-10.59, 6.71) * mm});
            skArc(sketch, "E203.20.0", {"start": v(-8.95, 7.65) * mm, "mid": v(-9, 7.8) * mm, "end": v(-9.1, 7.93) * mm});
            skArc(sketch, "E203.20.1", {"start": v(-9.08, 7.08) * mm, "mid": v(-8.93, 7.35) * mm, "end": v(-8.95, 7.65) * mm});
            skArc(sketch, "E203.20.2", {"start": v(-10.05, 8.05) * mm, "mid": v(-10.4, 7.72) * mm, "end": v(-10.77, 7.4) * mm});
            skPoint(sketch, "E203.20.3", {"position": v(-9.6, 7.6) * mm});
            skArc(sketch, "E203.20.4", {"start": v(-9.65, 6.95) * mm, "mid": v(-9.8, 7) * mm, "end": v(-9.93, 7.1) * mm});
            skLineSegment(sketch, "E203.20.5", {"start": v(-9.4, 8.77) * mm, "end": v(-8.9, 8.35) * mm});
            skArc(sketch, "E203.20.6", {"start": v(-10.12, 7.1) * mm, "mid": v(-10.24, 7) * mm, "end": v(-10.35, 6.9) * mm});
            skLineSegment(sketch, "E203.20.7", {"start": v(-10.77, 7.4) * mm, "end": v(-10.35, 6.9) * mm});
            skArc(sketch, "E203.20.8", {"start": v(-9.08, 7.08) * mm, "mid": v(-9.35, 6.93) * mm, "end": v(-9.65, 6.95) * mm});
            skPoint(sketch, "E203.20.9", {"position": v(-10.05, 8.05) * mm});
            skArc(sketch, "E203.20.10", {"start": v(-9.79, 7.79) * mm, "mid": v(-10.15, 7.44) * mm, "end": v(-10.53, 7.12) * mm, "construction": true});
            skArc(sketch, "E203.20.11", {"start": v(-10.05, 8.05) * mm, "mid": v(-9.72, 8.4) * mm, "end": v(-9.4, 8.77) * mm});
            skPoint(sketch, "E203.20.12", {"position": v(-9.79, 7.79) * mm});
            skArc(sketch, "E203.20.13", {"start": v(-9.1, 8.12) * mm, "mid": v(-9, 8.24) * mm, "end": v(-8.9, 8.35) * mm});
            skArc(sketch, "E203.20.14", {"start": v(-9.93, 7.1) * mm, "mid": v(-10.03, 7.13) * mm, "end": v(-10.12, 7.1) * mm});
            skArc(sketch, "E203.20.15", {"start": v(-9.1, 7.93) * mm, "mid": v(-9.13, 8.03) * mm, "end": v(-9.1, 8.12) * mm});
            skArc(sketch, "E203.21.0", {"start": v(-7.67, 9.36) * mm, "mid": v(-7.76, 9.5) * mm, "end": v(-7.87, 9.61) * mm});
            skArc(sketch, "E203.21.1", {"start": v(-7.68, 8.78) * mm, "mid": v(-7.6, 9.07) * mm, "end": v(-7.67, 9.36) * mm});
            skArc(sketch, "E203.21.2", {"start": v(-8.83, 9.54) * mm, "mid": v(-9.1, 9.15) * mm, "end": v(-9.4, 8.77) * mm});
            skPoint(sketch, "E203.21.3", {"position": v(-8.3, 9.2) * mm});
            skArc(sketch, "E203.21.4", {"start": v(-8.22, 8.53) * mm, "mid": v(-8.38, 8.57) * mm, "end": v(-8.53, 8.63) * mm});
            skLineSegment(sketch, "E203.21.5", {"start": v(-8.34, 10.37) * mm, "end": v(-7.76, 10.06) * mm});
            skArc(sketch, "E203.21.6", {"start": v(-8.71, 8.59) * mm, "mid": v(-8.8, 8.47) * mm, "end": v(-8.9, 8.35) * mm});
            skLineSegment(sketch, "E203.21.7", {"start": v(-9.4, 8.77) * mm, "end": v(-8.9, 8.35) * mm});
            skArc(sketch, "E203.21.8", {"start": v(-7.68, 8.78) * mm, "mid": v(-7.92, 8.58) * mm, "end": v(-8.22, 8.53) * mm});
            skPoint(sketch, "E203.21.9", {"position": v(-8.83, 9.54) * mm});
            skArc(sketch, "E203.21.10", {"start": v(-8.52, 9.33) * mm, "mid": v(-8.8, 8.92) * mm, "end": v(-9.12, 8.53) * mm, "construction": true});
            skArc(sketch, "E203.21.11", {"start": v(-8.83, 9.54) * mm, "mid": v(-8.57, 9.95) * mm, "end": v(-8.34, 10.37) * mm});
            skPoint(sketch, "E203.21.12", {"position": v(-8.52, 9.33) * mm});
            skArc(sketch, "E203.21.13", {"start": v(-7.9, 9.8) * mm, "mid": v(-7.83, 9.93) * mm, "end": v(-7.76, 10.06) * mm});
            skArc(sketch, "E203.21.14", {"start": v(-8.53, 8.63) * mm, "mid": v(-8.63, 8.64) * mm, "end": v(-8.71, 8.59) * mm});
            skArc(sketch, "E203.21.15", {"start": v(-7.87, 9.61) * mm, "mid": v(-7.92, 9.7) * mm, "end": v(-7.9, 9.8) * mm});
            skArc(sketch, "E203.22.0", {"start": v(-6.75, 11.3) * mm, "mid": v(-6.86, 11.4) * mm, "end": v(-7, 11.5) * mm});
            skArc(sketch, "E203.22.1", {"start": v(-6.65, 10.71) * mm, "mid": v(-6.61, 11.02) * mm, "end": v(-6.75, 11.3) * mm});
            skArc(sketch, "E203.22.2", {"start": v(-7.92, 11.24) * mm, "mid": v(-8.12, 10.8) * mm, "end": v(-8.34, 10.37) * mm});
            skPoint(sketch, "E203.22.3", {"position": v(-7.34, 11) * mm});
            skArc(sketch, "E203.22.4", {"start": v(-7.13, 10.37) * mm, "mid": v(-7.29, 10.37) * mm, "end": v(-7.45, 10.4) * mm});
            skLineSegment(sketch, "E203.22.5", {"start": v(-7.6, 12.15) * mm, "end": v(-6.97, 11.96) * mm});
            skArc(sketch, "E203.22.6", {"start": v(-7.62, 10.33) * mm, "mid": v(-7.69, 10.2) * mm, "end": v(-7.76, 10.06) * mm});
            skLineSegment(sketch, "E203.22.7", {"start": v(-8.34, 10.37) * mm, "end": v(-7.76, 10.06) * mm});
            skArc(sketch, "E203.22.8", {"start": v(-6.65, 10.71) * mm, "mid": v(-6.84, 10.47) * mm, "end": v(-7.13, 10.37) * mm});
            skPoint(sketch, "E203.22.9", {"position": v(-7.92, 11.24) * mm});
            skArc(sketch, "E203.22.10", {"start": v(-7.58, 11.1) * mm, "mid": v(-7.78, 10.64) * mm, "end": v(-8, 10.2) * mm, "construction": true});
            skArc(sketch, "E203.22.11", {"start": v(-7.92, 11.24) * mm, "mid": v(-7.75, 11.7) * mm, "end": v(-7.6, 12.15) * mm});
            skPoint(sketch, "E203.22.12", {"position": v(-7.58, 11.1) * mm});
            skArc(sketch, "E203.22.13", {"start": v(-7.06, 11.67) * mm, "mid": v(-7.02, 11.82) * mm, "end": v(-6.97, 11.96) * mm});
            skArc(sketch, "E203.22.14", {"start": v(-7.45, 10.4) * mm, "mid": v(-7.55, 10.4) * mm, "end": v(-7.62, 10.33) * mm});
            skArc(sketch, "E203.22.15", {"start": v(-7, 11.5) * mm, "mid": v(-7.06, 11.57) * mm, "end": v(-7.06, 11.67) * mm});
            skArc(sketch, "E203.23.0", {"start": v(-6.22, 13.36) * mm, "mid": v(-6.36, 13.45) * mm, "end": v(-6.5, 13.52) * mm});
            skArc(sketch, "E203.23.1", {"start": v(-6.01, 12.81) * mm, "mid": v(-6.04, 13.12) * mm, "end": v(-6.22, 13.36) * mm});
            skArc(sketch, "E203.23.2", {"start": v(-7.36, 13.08) * mm, "mid": v(-7.47, 12.61) * mm, "end": v(-7.6, 12.15) * mm});
            skPoint(sketch, "E203.23.3", {"position": v(-6.75, 12.96) * mm});
            skArc(sketch, "E203.23.4", {"start": v(-6.41, 12.39) * mm, "mid": v(-6.57, 12.36) * mm, "end": v(-6.73, 12.36) * mm});
            skLineSegment(sketch, "E203.23.5", {"start": v(-7.22, 14.04) * mm, "end": v(-6.57, 13.97) * mm});
            skArc(sketch, "E203.23.6", {"start": v(-6.89, 12.24) * mm, "mid": v(-6.93, 12.1) * mm, "end": v(-6.97, 11.96) * mm});
            skLineSegment(sketch, "E203.23.7", {"start": v(-7.6, 12.15) * mm, "end": v(-6.97, 11.96) * mm});
            skArc(sketch, "E203.23.8", {"start": v(-6.01, 12.81) * mm, "mid": v(-6.15, 12.54) * mm, "end": v(-6.41, 12.39) * mm});
            skPoint(sketch, "E203.23.9", {"position": v(-7.36, 13.08) * mm});
            skArc(sketch, "E203.23.10", {"start": v(-7, 13.01) * mm, "mid": v(-7.1, 12.52) * mm, "end": v(-7.24, 12.04) * mm, "construction": true});
            skArc(sketch, "E203.23.11", {"start": v(-7.36, 13.08) * mm, "mid": v(-7.28, 13.56) * mm, "end": v(-7.22, 14.04) * mm});
            skPoint(sketch, "E203.23.12", {"position": v(-7, 13.01) * mm});
            skArc(sketch, "E203.23.13", {"start": v(-6.6, 13.68) * mm, "mid": v(-6.59, 13.82) * mm, "end": v(-6.57, 13.97) * mm});
            skArc(sketch, "E203.23.14", {"start": v(-6.73, 12.36) * mm, "mid": v(-6.83, 12.33) * mm, "end": v(-6.89, 12.24) * mm});
            skArc(sketch, "E203.23.15", {"start": v(-6.5, 13.52) * mm, "mid": v(-6.58, 13.58) * mm, "end": v(-6.6, 13.68) * mm});
            skArc(sketch, "E203.24.0", {"start": v(-6.1, 15.5) * mm, "mid": v(-6.26, 15.56) * mm, "end": v(-6.42, 15.6) * mm});
            skArc(sketch, "E203.24.1", {"start": v(-5.8, 15) * mm, "mid": v(-5.88, 15.3) * mm, "end": v(-6.1, 15.5) * mm});
            skArc(sketch, "E203.24.2", {"start": v(-7.18, 15) * mm, "mid": v(-7.19, 14.52) * mm, "end": v(-7.22, 14.04) * mm});
            skPoint(sketch, "E203.24.3", {"position": v(-6.55, 15) * mm});
            skArc(sketch, "E203.24.4", {"start": v(-6.1, 14.5) * mm, "mid": v(-6.26, 14.44) * mm, "end": v(-6.42, 14.4) * mm});
            skLineSegment(sketch, "E203.24.5", {"start": v(-7.22, 15.96) * mm, "end": v(-6.57, 16.03) * mm});
            skArc(sketch, "E203.24.6", {"start": v(-6.55, 14.27) * mm, "mid": v(-6.56, 14.12) * mm, "end": v(-6.57, 13.97) * mm});
            skLineSegment(sketch, "E203.24.7", {"start": v(-7.22, 14.04) * mm, "end": v(-6.57, 13.97) * mm});
            skArc(sketch, "E203.24.8", {"start": v(-5.8, 15) * mm, "mid": v(-5.88, 14.7) * mm, "end": v(-6.1, 14.5) * mm});
            skPoint(sketch, "E203.24.9", {"position": v(-7.18, 15) * mm});
            skArc(sketch, "E203.24.10", {"start": v(-6.8, 15) * mm, "mid": v(-6.81, 14.5) * mm, "end": v(-6.85, 14) * mm, "construction": true});
            skArc(sketch, "E203.24.11", {"start": v(-7.18, 15) * mm, "mid": v(-7.19, 15.48) * mm, "end": v(-7.22, 15.96) * mm});
            skPoint(sketch, "E203.24.12", {"position": v(-6.8, 15) * mm});
            skArc(sketch, "E203.24.13", {"start": v(-6.55, 15.73) * mm, "mid": v(-6.56, 15.88) * mm, "end": v(-6.57, 16.03) * mm});
            skArc(sketch, "E203.24.14", {"start": v(-6.42, 14.4) * mm, "mid": v(-6.5, 14.36) * mm, "end": v(-6.55, 14.27) * mm});
            skArc(sketch, "E203.24.15", {"start": v(-6.42, 15.6) * mm, "mid": v(-6.5, 15.64) * mm, "end": v(-6.55, 15.73) * mm});
            skArc(sketch, "E203.25.0", {"start": v(-6.41, 17.61) * mm, "mid": v(-6.57, 17.64) * mm, "end": v(-6.73, 17.64) * mm});
            skArc(sketch, "E203.25.1", {"start": v(-6.01, 17.19) * mm, "mid": v(-6.15, 17.46) * mm, "end": v(-6.41, 17.61) * mm});
            skArc(sketch, "E203.25.2", {"start": v(-7.36, 16.92) * mm, "mid": v(-7.28, 16.44) * mm, "end": v(-7.22, 15.96) * mm});
            skPoint(sketch, "E203.25.3", {"position": v(-6.75, 17.04) * mm});
            skArc(sketch, "E203.25.4", {"start": v(-6.22, 16.64) * mm, "mid": v(-6.36, 16.55) * mm, "end": v(-6.5, 16.48) * mm});
            skLineSegment(sketch, "E203.25.5", {"start": v(-7.6, 17.85) * mm, "end": v(-6.97, 18.04) * mm});
            skArc(sketch, "E203.25.6", {"start": v(-6.6, 16.32) * mm, "mid": v(-6.59, 16.18) * mm, "end": v(-6.57, 16.03) * mm});
            skLineSegment(sketch, "E203.25.7", {"start": v(-7.22, 15.96) * mm, "end": v(-6.57, 16.03) * mm});
            skArc(sketch, "E203.25.8", {"start": v(-6.01, 17.19) * mm, "mid": v(-6.04, 16.88) * mm, "end": v(-6.22, 16.64) * mm});
            skPoint(sketch, "E203.25.9", {"position": v(-7.36, 16.92) * mm});
            skArc(sketch, "E203.25.10", {"start": v(-7, 16.99) * mm, "mid": v(-6.91, 16.5) * mm, "end": v(-6.85, 16) * mm, "construction": true});
            skArc(sketch, "E203.25.11", {"start": v(-7.36, 16.92) * mm, "mid": v(-7.47, 17.39) * mm, "end": v(-7.6, 17.85) * mm});
            skPoint(sketch, "E203.25.12", {"position": v(-7, 16.99) * mm});
            skArc(sketch, "E203.25.13", {"start": v(-6.89, 17.76) * mm, "mid": v(-6.93, 17.9) * mm, "end": v(-6.97, 18.04) * mm});
            skArc(sketch, "E203.25.14", {"start": v(-6.5, 16.48) * mm, "mid": v(-6.58, 16.42) * mm, "end": v(-6.6, 16.32) * mm});
            skArc(sketch, "E203.25.15", {"start": v(-6.73, 17.64) * mm, "mid": v(-6.83, 17.67) * mm, "end": v(-6.89, 17.76) * mm});
            skArc(sketch, "E203.26.0", {"start": v(-7.13, 19.63) * mm, "mid": v(-7.29, 19.63) * mm, "end": v(-7.45, 19.6) * mm});
            skArc(sketch, "E203.26.1", {"start": v(-6.65, 19.29) * mm, "mid": v(-6.84, 19.53) * mm, "end": v(-7.13, 19.63) * mm});
            skArc(sketch, "E203.26.2", {"start": v(-7.92, 18.76) * mm, "mid": v(-7.75, 18.3) * mm, "end": v(-7.6, 17.85) * mm});
            skPoint(sketch, "E203.26.3", {"position": v(-7.34, 19) * mm});
            skArc(sketch, "E203.26.4", {"start": v(-6.75, 18.7) * mm, "mid": v(-6.86, 18.6) * mm, "end": v(-7, 18.5) * mm});
            skLineSegment(sketch, "E203.26.5", {"start": v(-8.34, 19.63) * mm, "end": v(-7.76, 19.94) * mm});
            skArc(sketch, "E203.26.6", {"start": v(-7.06, 18.33) * mm, "mid": v(-7.02, 18.18) * mm, "end": v(-6.97, 18.04) * mm});
            skLineSegment(sketch, "E203.26.7", {"start": v(-7.6, 17.85) * mm, "end": v(-6.97, 18.04) * mm});
            skArc(sketch, "E203.26.8", {"start": v(-6.65, 19.29) * mm, "mid": v(-6.61, 18.98) * mm, "end": v(-6.75, 18.7) * mm});
            skPoint(sketch, "E203.26.9", {"position": v(-7.92, 18.76) * mm});
            skArc(sketch, "E203.26.10", {"start": v(-7.58, 18.9) * mm, "mid": v(-7.4, 18.44) * mm, "end": v(-7.24, 17.96) * mm, "construction": true});
            skArc(sketch, "E203.26.11", {"start": v(-7.92, 18.76) * mm, "mid": v(-8.12, 19.2) * mm, "end": v(-8.34, 19.63) * mm});
            skPoint(sketch, "E203.26.12", {"position": v(-7.58, 18.9) * mm});
            skArc(sketch, "E203.26.13", {"start": v(-7.62, 19.67) * mm, "mid": v(-7.69, 19.8) * mm, "end": v(-7.76, 19.94) * mm});
            skArc(sketch, "E203.26.14", {"start": v(-7, 18.5) * mm, "mid": v(-7.06, 18.43) * mm, "end": v(-7.06, 18.33) * mm});
            skArc(sketch, "E203.26.15", {"start": v(-7.45, 19.6) * mm, "mid": v(-7.55, 19.6) * mm, "end": v(-7.62, 19.67) * mm});
            skArc(sketch, "E203.27.0", {"start": v(-8.22, 21.47) * mm, "mid": v(-8.38, 21.43) * mm, "end": v(-8.53, 21.37) * mm});
            skArc(sketch, "E203.27.1", {"start": v(-7.68, 21.22) * mm, "mid": v(-7.92, 21.42) * mm, "end": v(-8.22, 21.47) * mm});
            skArc(sketch, "E203.27.2", {"start": v(-8.83, 20.46) * mm, "mid": v(-8.57, 20.05) * mm, "end": v(-8.34, 19.63) * mm});
            skPoint(sketch, "E203.27.3", {"position": v(-8.3, 20.8) * mm});
            skArc(sketch, "E203.27.4", {"start": v(-7.67, 20.64) * mm, "mid": v(-7.76, 20.5) * mm, "end": v(-7.87, 20.39) * mm});
            skLineSegment(sketch, "E203.27.5", {"start": v(-9.4, 21.23) * mm, "end": v(-8.9, 21.65) * mm});
            skArc(sketch, "E203.27.6", {"start": v(-7.9, 20.2) * mm, "mid": v(-7.83, 20.07) * mm, "end": v(-7.76, 19.94) * mm});
            skLineSegment(sketch, "E203.27.7", {"start": v(-8.34, 19.63) * mm, "end": v(-7.76, 19.94) * mm});
            skArc(sketch, "E203.27.8", {"start": v(-7.68, 21.22) * mm, "mid": v(-7.6, 20.93) * mm, "end": v(-7.67, 20.64) * mm});
            skPoint(sketch, "E203.27.9", {"position": v(-8.83, 20.46) * mm});
            skArc(sketch, "E203.27.10", {"start": v(-8.52, 20.67) * mm, "mid": v(-8.25, 20.24) * mm, "end": v(-8, 19.8) * mm, "construction": true});
            skArc(sketch, "E203.27.11", {"start": v(-8.83, 20.46) * mm, "mid": v(-9.1, 20.85) * mm, "end": v(-9.4, 21.23) * mm});
            skPoint(sketch, "E203.27.12", {"position": v(-8.52, 20.67) * mm});
            skArc(sketch, "E203.27.13", {"start": v(-8.71, 21.41) * mm, "mid": v(-8.8, 21.53) * mm, "end": v(-8.9, 21.65) * mm});
            skArc(sketch, "E203.27.14", {"start": v(-7.87, 20.39) * mm, "mid": v(-7.92, 20.3) * mm, "end": v(-7.9, 20.2) * mm});
            skArc(sketch, "E203.27.15", {"start": v(-8.53, 21.37) * mm, "mid": v(-8.63, 21.36) * mm, "end": v(-8.71, 21.41) * mm});
            skArc(sketch, "E203.28.0", {"start": v(-9.65, 23.05) * mm, "mid": v(-9.8, 23) * mm, "end": v(-9.93, 22.9) * mm});
            skArc(sketch, "E203.28.1", {"start": v(-9.08, 22.92) * mm, "mid": v(-9.35, 23.07) * mm, "end": v(-9.65, 23.05) * mm});
            skArc(sketch, "E203.28.2", {"start": v(-10.05, 21.95) * mm, "mid": v(-9.72, 21.6) * mm, "end": v(-9.4, 21.23) * mm});
            skPoint(sketch, "E203.28.3", {"position": v(-9.6, 22.4) * mm});
            skArc(sketch, "E203.28.4", {"start": v(-8.95, 22.35) * mm, "mid": v(-9, 22.2) * mm, "end": v(-9.1, 22.07) * mm});
            skLineSegment(sketch, "E203.28.5", {"start": v(-10.77, 22.6) * mm, "end": v(-10.35, 23.1) * mm});
            skArc(sketch, "E203.28.6", {"start": v(-9.1, 21.88) * mm, "mid": v(-9, 21.76) * mm, "end": v(-8.9, 21.65) * mm});
            skLineSegment(sketch, "E203.28.7", {"start": v(-9.4, 21.23) * mm, "end": v(-8.9, 21.65) * mm});
            skArc(sketch, "E203.28.8", {"start": v(-9.08, 22.92) * mm, "mid": v(-8.93, 22.65) * mm, "end": v(-8.95, 22.35) * mm});
            skPoint(sketch, "E203.28.9", {"position": v(-10.05, 21.95) * mm});
            skArc(sketch, "E203.28.10", {"start": v(-9.79, 22.21) * mm, "mid": v(-9.44, 21.85) * mm, "end": v(-9.12, 21.47) * mm, "construction": true});
            skArc(sketch, "E203.28.11", {"start": v(-10.05, 21.95) * mm, "mid": v(-10.4, 22.28) * mm, "end": v(-10.77, 22.6) * mm});
            skPoint(sketch, "E203.28.12", {"position": v(-9.79, 22.21) * mm});
            skArc(sketch, "E203.28.13", {"start": v(-10.12, 22.9) * mm, "mid": v(-10.24, 23) * mm, "end": v(-10.35, 23.1) * mm});
            skArc(sketch, "E203.28.14", {"start": v(-9.1, 22.07) * mm, "mid": v(-9.13, 21.97) * mm, "end": v(-9.1, 21.88) * mm});
            skArc(sketch, "E203.28.15", {"start": v(-9.93, 22.9) * mm, "mid": v(-10.03, 22.87) * mm, "end": v(-10.12, 22.9) * mm});
            skArc(sketch, "E203.29.0", {"start": v(-11.36, 24.33) * mm, "mid": v(-11.5, 24.24) * mm, "end": v(-11.61, 24.13) * mm});
            skArc(sketch, "E203.29.1", {"start": v(-10.78, 24.32) * mm, "mid": v(-11.07, 24.4) * mm, "end": v(-11.36, 24.33) * mm});
            skArc(sketch, "E203.29.2", {"start": v(-11.54, 23.17) * mm, "mid": v(-11.15, 22.9) * mm, "end": v(-10.77, 22.6) * mm});
            skPoint(sketch, "E203.29.3", {"position": v(-11.2, 23.7) * mm});
            skArc(sketch, "E203.29.4", {"start": v(-10.53, 23.78) * mm, "mid": v(-10.57, 23.62) * mm, "end": v(-10.63, 23.47) * mm});
            skLineSegment(sketch, "E203.29.5", {"start": v(-12.37, 23.66) * mm, "end": v(-12.06, 24.24) * mm});
            skArc(sketch, "E203.29.6", {"start": v(-10.59, 23.29) * mm, "mid": v(-10.47, 23.2) * mm, "end": v(-10.35, 23.1) * mm});
            skLineSegment(sketch, "E203.29.7", {"start": v(-10.77, 22.6) * mm, "end": v(-10.35, 23.1) * mm});
            skArc(sketch, "E203.29.8", {"start": v(-10.78, 24.32) * mm, "mid": v(-10.58, 24.08) * mm, "end": v(-10.53, 23.78) * mm});
            skPoint(sketch, "E203.29.9", {"position": v(-11.54, 23.17) * mm});
            skArc(sketch, "E203.29.10", {"start": v(-11.33, 23.48) * mm, "mid": v(-10.92, 23.2) * mm, "end": v(-10.53, 22.88) * mm, "construction": true});
            skArc(sketch, "E203.29.11", {"start": v(-11.54, 23.17) * mm, "mid": v(-11.95, 23.43) * mm, "end": v(-12.37, 23.66) * mm});
            skPoint(sketch, "E203.29.12", {"position": v(-11.33, 23.48) * mm});
            skArc(sketch, "E203.29.13", {"start": v(-11.8, 24.1) * mm, "mid": v(-11.93, 24.17) * mm, "end": v(-12.06, 24.24) * mm});
            skArc(sketch, "E203.29.14", {"start": v(-10.63, 23.47) * mm, "mid": v(-10.64, 23.37) * mm, "end": v(-10.59, 23.29) * mm});
            skArc(sketch, "E203.29.15", {"start": v(-11.61, 24.13) * mm, "mid": v(-11.7, 24.08) * mm, "end": v(-11.8, 24.1) * mm});
            skArc(sketch, "E203.30.0", {"start": v(-13.3, 25.25) * mm, "mid": v(-13.4, 25.14) * mm, "end": v(-13.5, 25) * mm});
            skArc(sketch, "E203.30.1", {"start": v(-12.71, 25.35) * mm, "mid": v(-13.02, 25.39) * mm, "end": v(-13.3, 25.25) * mm});
            skArc(sketch, "E203.30.2", {"start": v(-13.24, 24.08) * mm, "mid": v(-12.8, 23.88) * mm, "end": v(-12.37, 23.66) * mm});
            skPoint(sketch, "E203.30.3", {"position": v(-13, 24.66) * mm});
            skArc(sketch, "E203.30.4", {"start": v(-12.37, 24.87) * mm, "mid": v(-12.37, 24.71) * mm, "end": v(-12.4, 24.55) * mm});
            skLineSegment(sketch, "E203.30.5", {"start": v(-14.15, 24.4) * mm, "end": v(-13.96, 25.03) * mm});
            skArc(sketch, "E203.30.6", {"start": v(-12.33, 24.38) * mm, "mid": v(-12.2, 24.31) * mm, "end": v(-12.06, 24.24) * mm});
            skLineSegment(sketch, "E203.30.7", {"start": v(-12.37, 23.66) * mm, "end": v(-12.06, 24.24) * mm});
            skArc(sketch, "E203.30.8", {"start": v(-12.71, 25.35) * mm, "mid": v(-12.47, 25.16) * mm, "end": v(-12.37, 24.87) * mm});
            skPoint(sketch, "E203.30.9", {"position": v(-13.24, 24.08) * mm});
            skArc(sketch, "E203.30.10", {"start": v(-13.1, 24.42) * mm, "mid": v(-12.64, 24.22) * mm, "end": v(-12.2, 24) * mm, "construction": true});
            skArc(sketch, "E203.30.11", {"start": v(-13.24, 24.08) * mm, "mid": v(-13.7, 24.25) * mm, "end": v(-14.15, 24.4) * mm});
            skPoint(sketch, "E203.30.12", {"position": v(-13.1, 24.42) * mm});
            skArc(sketch, "E203.30.13", {"start": v(-13.67, 24.94) * mm, "mid": v(-13.82, 24.98) * mm, "end": v(-13.96, 25.03) * mm});
            skArc(sketch, "E203.30.14", {"start": v(-12.4, 24.55) * mm, "mid": v(-12.4, 24.45) * mm, "end": v(-12.33, 24.38) * mm});
            skArc(sketch, "E203.30.15", {"start": v(-13.5, 25) * mm, "mid": v(-13.57, 24.94) * mm, "end": v(-13.67, 24.94) * mm});
            skArc(sketch, "E203.31.0", {"start": v(-15.36, 25.78) * mm, "mid": v(-15.45, 25.64) * mm, "end": v(-15.52, 25.5) * mm});
            skArc(sketch, "E203.31.1", {"start": v(-14.81, 25.99) * mm, "mid": v(-15.12, 25.96) * mm, "end": v(-15.36, 25.78) * mm});
            skArc(sketch, "E203.31.2", {"start": v(-15.08, 24.64) * mm, "mid": v(-14.61, 24.53) * mm, "end": v(-14.15, 24.4) * mm});
            skPoint(sketch, "E203.31.3", {"position": v(-14.96, 25.25) * mm});
            skArc(sketch, "E203.31.4", {"start": v(-14.39, 25.59) * mm, "mid": v(-14.36, 25.43) * mm, "end": v(-14.36, 25.27) * mm});
            skArc(sketch, "E203.31.6", {"start": v(-14.24, 25.11) * mm, "mid": v(-14.1, 25.07) * mm, "end": v(-13.96, 25.03) * mm});
            skLineSegment(sketch, "E203.31.7", {"start": v(-14.15, 24.4) * mm, "end": v(-13.96, 25.03) * mm});
            skArc(sketch, "E203.31.8", {"start": v(-14.81, 25.99) * mm, "mid": v(-14.54, 25.85) * mm, "end": v(-14.39, 25.59) * mm});
            skPoint(sketch, "E203.31.9", {"position": v(-15.08, 24.64) * mm});
            skArc(sketch, "E203.31.10", {"start": v(-15.01, 25) * mm, "mid": v(-14.52, 24.9) * mm, "end": v(-14.04, 24.76) * mm, "construction": true});
            skArc(sketch, "E203.31.11", {"start": v(-15.08, 24.64) * mm, "mid": v(-15.56, 24.72) * mm, "end": v(-16.04, 24.78) * mm});
            skPoint(sketch, "E203.31.12", {"position": v(-15.01, 25) * mm});
            skArc(sketch, "E203.31.13", {"start": v(-15.68, 25.4) * mm, "mid": v(-15.82, 25.41) * mm, "end": v(-15.97, 25.43) * mm});
            skArc(sketch, "E203.31.14", {"start": v(-14.36, 25.27) * mm, "mid": v(-14.33, 25.17) * mm, "end": v(-14.24, 25.11) * mm});
            skArc(sketch, "E203.31.15", {"start": v(-15.52, 25.5) * mm, "mid": v(-15.58, 25.42) * mm, "end": v(-15.68, 25.4) * mm});
            skLineSegment(sketch, "E204.0", {"start": v(-27.25, 15) * mm, "end": v(-6.75, 15) * mm});
            skSolve(sketch);
        }
        {
            var Q0;
            Q0=qSketchRegion(id+"F31",true);
            extrude(context, id + "F32", {"entities" : qUnion([Q0]), "operationType" : NewBodyOperationType.REMOVE, "endBound" : BoundingType.SYMMETRIC, "oppositeDirection" : true, "depth" : 6.5 * mm});
        }
        {
            var Q0;
            {var subQ0=sQuery(id+"F0.wireOp",EDGE,"E28");var subQ1=sQuery(id+"F0.wireOp",EDGE,"E27");var subQ2=sQuery(id+"F0.wireOp",EDGE,"E26");var subQ3=sQuery(id+"F0.wireOp",EDGE,"E24");var subQ4=sQuery(id+"F0.wireOp",EDGE,"E23");Q0=makeQuery(id+"F2.boolean.opBoolean","MERGE",FACE,{"derivedFrom":[makeQuery(id+"F1.opExtrude","CAP_FACE",FACE,{"disambiguationData":[OSD([sQuery(id+"F0.wireOp",EDGE,"E0.right"),sQuery(id+"F0.wireOp",EDGE,"E4"),sQuery(id+"F0.wireOp",EDGE,"E9"),sQuery(id+"F0.wireOp",EDGE,"E11.MirrorC"),sQuery(id+"F0.wireOp",EDGE,"E13.MirrorC"),sQuery(id+"F0.wireOp",EDGE,"E14.MirrorC"),sQuery(id+"F0.wireOp",EDGE,"E15"),sQuery(id+"F0.wireOp",EDGE,"E17.MirrorC"),sQuery(id+"F0.wireOp",EDGE,"E18.MirrorC"),sQuery(id+"F0.wireOp",EDGE,"E20.MirrorC"),sQuery(id+"F0.wireOp",EDGE,"E21"),sQuery(id+"F0.wireOp",EDGE,"E22"),subQ4,subQ3,sQuery(id+"F0.wireOp",EDGE,"E25"),subQ2,subQ1,subQ0,sQuery(id+"F0.wireOp",EDGE,"E30.0"),sQuery(id+"F0.wireOp",EDGE,"E30.1"),sQuery(id+"F0.wireOp",EDGE,"E30.2")])],"isStart":true}),makeQuery(id+"F2.opExtrude","CAP_FACE",FACE,{"disambiguationData":[OSD([subQ4,subQ3,subQ2,subQ1,subQ0,sQuery(id+"F0.wireOp",EDGE,"E31"),sQuery(id+"F0.wireOp",EDGE,"E32"),sQuery(id+"F0.wireOp",EDGE,"E33"),sQuery(id+"F0.wireOp",EDGE,"E34"),sQuery(id+"F0.wireOp",EDGE,"E35"),sQuery(id+"F0.wireOp",EDGE,"E39"),sQuery(id+"F0.wireOp",EDGE,"E41"),sQuery(id+"F0.wireOp",EDGE,"E43"),sQuery(id+"F0.wireOp",EDGE,"E44"),sQuery(id+"F0.wireOp",EDGE,"E45"),sQuery(id+"F0.wireOp",EDGE,"E46")])],"isStart":true})]});}
            var Q1;
            Q1=sQuery(id+"F10.wireOp",VERTEX,"E106.MirrorP");
            cPlane(context, id + "F33", {"entities" : qUnion([Q0, Q1]), "cplaneType" : CPlaneType.PLANE_POINT, "offset" : 150 * mm, "width" : 150 * mm, "height" : 150 * mm});
        }
        {
            var Q0;
            Q0=qCreatedBy(id+"F33.planeOp",FACE);
            var sketch = newSketch(context, id + "F34", { "sketchPlane" : qUnion([Q0])});
            skLineSegment(sketch, "E205", {"start": v(11.5, -0.3) * mm, "end": v(11.5, -1.68) * mm, "construction": true});
            skArc(sketch, "E206", {"start": v(11.5, -0.3) * mm, "mid": v(11.8, -0.38) * mm, "end": v(12, -0.6) * mm});
            skArc(sketch, "E207", {"start": v(12, -0.6) * mm, "mid": v(12.06, -0.76) * mm, "end": v(12.1, -0.92) * mm});
            skArc(sketch, "E208", {"start": v(12.1, -0.92) * mm, "mid": v(12.14, -1) * mm, "end": v(12.23, -1.05) * mm});
            skPoint(sketch, "E209", {"position": v(11.5, -1.68) * mm});
            skPoint(sketch, "E210", {"position": v(11.5, -1.05) * mm});
            skPoint(sketch, "E211", {"position": v(11.5, -1.3) * mm});
            skArc(sketch, "E212", {"start": v(11.5, -1.3) * mm, "mid": v(12, -1.31) * mm, "end": v(12.5, -1.35) * mm, "construction": true});
            skLineSegment(sketch, "E213", {"start": v(10.54, -21.28) * mm, "end": v(12.53, -1.07) * mm});
            skArc(sketch, "E214", {"start": v(12.23, -1.05) * mm, "mid": v(12.38, -1.06) * mm, "end": v(12.53, -1.07) * mm});
            skArc(sketch, "E215", {"start": v(11.5, -1.68) * mm, "mid": v(21.31, -11.98) * mm, "end": v(10.54, -21.28) * mm});
            skArc(sketch, "E216.MirrorCS", {"start": v(11.5, -0.3) * mm, "mid": v(11.2, -0.38) * mm, "end": v(11, -0.6) * mm});
            skArc(sketch, "E217.MirrorCS", {"start": v(11, -0.6) * mm, "mid": v(10.94, -0.76) * mm, "end": v(10.9, -0.92) * mm});
            skArc(sketch, "E218.MirrorCS", {"start": v(10.9, -0.92) * mm, "mid": v(10.86, -1) * mm, "end": v(10.77, -1.05) * mm});
            skArc(sketch, "E219.MirrorCS", {"start": v(10.77, -1.05) * mm, "mid": v(10.62, -1.06) * mm, "end": v(10.47, -1.07) * mm});
            skLineSegment(sketch, "E220.MirrorCS", {"start": v(12.46, -21.28) * mm, "end": v(10.47, -1.07) * mm});
            skArc(sketch, "E221.MirrorCS", {"start": v(11.5, -1.68) * mm, "mid": v(1.69, -11.98) * mm, "end": v(12.46, -21.28) * mm});
            skArc(sketch, "E222.1.0", {"start": v(8.89, -0.91) * mm, "mid": v(8.86, -1.07) * mm, "end": v(8.86, -1.23) * mm});
            skArc(sketch, "E222.1.1", {"start": v(9.31, -0.51) * mm, "mid": v(9.04, -0.65) * mm, "end": v(8.89, -0.91) * mm});
            skArc(sketch, "E222.1.2", {"start": v(9.58, -1.86) * mm, "mid": v(21.22, -10.06) * mm, "end": v(12.46, -21.28) * mm});
            skPoint(sketch, "E222.1.3", {"position": v(9.46, -1.25) * mm});
            skArc(sketch, "E222.1.4", {"start": v(9.86, -0.72) * mm, "mid": v(9.95, -0.86) * mm, "end": v(10.02, -1) * mm});
            skLineSegment(sketch, "E222.1.5", {"start": v(14.35, -20.9) * mm, "end": v(8.46, -1.47) * mm});
            skArc(sketch, "E222.1.6", {"start": v(10.18, -1.1) * mm, "mid": v(10.32, -1.09) * mm, "end": v(10.47, -1.07) * mm});
            skArc(sketch, "E222.1.8", {"start": v(9.31, -0.51) * mm, "mid": v(9.62, -0.54) * mm, "end": v(9.86, -0.72) * mm});
            skPoint(sketch, "E222.1.9", {"position": v(9.58, -1.86) * mm});
            skArc(sketch, "E222.1.10", {"start": v(9.51, -1.5) * mm, "mid": v(10, -1.41) * mm, "end": v(10.5, -1.35) * mm, "construction": true});
            skArc(sketch, "E222.1.11", {"start": v(9.58, -1.86) * mm, "mid": v(1.97, -13.89) * mm, "end": v(14.35, -20.9) * mm});
            skPoint(sketch, "E222.1.12", {"position": v(9.51, -1.5) * mm});
            skArc(sketch, "E222.1.13", {"start": v(8.74, -1.39) * mm, "mid": v(8.6, -1.43) * mm, "end": v(8.46, -1.47) * mm});
            skArc(sketch, "E222.1.14", {"start": v(10.02, -1) * mm, "mid": v(10.08, -1.08) * mm, "end": v(10.18, -1.1) * mm});
            skArc(sketch, "E222.1.15", {"start": v(8.86, -1.23) * mm, "mid": v(8.83, -1.33) * mm, "end": v(8.74, -1.39) * mm});
            skArc(sketch, "E222.2.0", {"start": v(6.87, -1.63) * mm, "mid": v(6.87, -1.79) * mm, "end": v(6.9, -1.95) * mm});
            skArc(sketch, "E222.2.1", {"start": v(7.21, -1.15) * mm, "mid": v(6.97, -1.34) * mm, "end": v(6.87, -1.63) * mm});
            skArc(sketch, "E222.2.2", {"start": v(7.74, -2.42) * mm, "mid": v(20.75, -8.2) * mm, "end": v(14.35, -20.9) * mm});
            skPoint(sketch, "E222.2.3", {"position": v(7.5, -1.84) * mm});
            skArc(sketch, "E222.2.4", {"start": v(7.8, -1.25) * mm, "mid": v(7.9, -1.36) * mm, "end": v(8, -1.5) * mm});
            skLineSegment(sketch, "E222.2.5", {"start": v(16.13, -20.16) * mm, "end": v(6.56, -2.26) * mm});
            skArc(sketch, "E222.2.6", {"start": v(8.17, -1.56) * mm, "mid": v(8.32, -1.52) * mm, "end": v(8.46, -1.47) * mm});
            skLineSegment(sketch, "E222.2.7", {"start": v(14.35, -20.9) * mm, "end": v(8.46, -1.47) * mm});
            skArc(sketch, "E222.2.8", {"start": v(7.21, -1.15) * mm, "mid": v(7.52, -1.11) * mm, "end": v(7.8, -1.25) * mm});
            skPoint(sketch, "E222.2.9", {"position": v(7.74, -2.42) * mm});
            skArc(sketch, "E222.2.10", {"start": v(7.6, -2.08) * mm, "mid": v(8.06, -1.9) * mm, "end": v(8.54, -1.74) * mm, "construction": true});
            skArc(sketch, "E222.2.11", {"start": v(7.74, -2.42) * mm, "mid": v(2.62, -15.7) * mm, "end": v(16.13, -20.16) * mm});
            skPoint(sketch, "E222.2.12", {"position": v(7.6, -2.08) * mm});
            skArc(sketch, "E222.2.13", {"start": v(6.83, -2.12) * mm, "mid": v(6.7, -2.19) * mm, "end": v(6.56, -2.26) * mm});
            skArc(sketch, "E222.2.14", {"start": v(8, -1.5) * mm, "mid": v(8.07, -1.56) * mm, "end": v(8.17, -1.56) * mm});
            skArc(sketch, "E222.2.15", {"start": v(6.9, -1.95) * mm, "mid": v(6.9, -2.05) * mm, "end": v(6.83, -2.12) * mm});
            skArc(sketch, "E222.3.0", {"start": v(5.03, -2.72) * mm, "mid": v(5.07, -2.88) * mm, "end": v(5.13, -3.03) * mm});
            skArc(sketch, "E222.3.1", {"start": v(5.28, -2.18) * mm, "mid": v(5.08, -2.42) * mm, "end": v(5.03, -2.72) * mm});
            skArc(sketch, "E222.3.2", {"start": v(6.04, -3.33) * mm, "mid": v(19.93, -6.45) * mm, "end": v(16.13, -20.16) * mm});
            skPoint(sketch, "E222.3.3", {"position": v(5.7, -2.8) * mm});
            skArc(sketch, "E222.3.4", {"start": v(5.86, -2.17) * mm, "mid": v(6, -2.26) * mm, "end": v(6.11, -2.37) * mm});
            skLineSegment(sketch, "E222.3.5", {"start": v(17.73, -19.1) * mm, "end": v(4.85, -3.4) * mm});
            skArc(sketch, "E222.3.6", {"start": v(6.3, -2.4) * mm, "mid": v(6.43, -2.33) * mm, "end": v(6.56, -2.26) * mm});
            skLineSegment(sketch, "E222.3.7", {"start": v(16.13, -20.16) * mm, "end": v(6.56, -2.26) * mm});
            skArc(sketch, "E222.3.8", {"start": v(5.28, -2.18) * mm, "mid": v(5.57, -2.1) * mm, "end": v(5.86, -2.17) * mm});
            skPoint(sketch, "E222.3.9", {"position": v(6.04, -3.33) * mm});
            skArc(sketch, "E222.3.10", {"start": v(5.83, -3.02) * mm, "mid": v(6.26, -2.75) * mm, "end": v(6.7, -2.5) * mm, "construction": true});
            skArc(sketch, "E222.3.11", {"start": v(6.04, -3.33) * mm, "mid": v(3.6, -17.35) * mm, "end": v(17.73, -19.1) * mm});
            skPoint(sketch, "E222.3.12", {"position": v(5.83, -3.02) * mm});
            skArc(sketch, "E222.3.13", {"start": v(5.09, -3.21) * mm, "mid": v(4.97, -3.3) * mm, "end": v(4.85, -3.4) * mm});
            skArc(sketch, "E222.3.14", {"start": v(6.11, -2.37) * mm, "mid": v(6.2, -2.42) * mm, "end": v(6.3, -2.4) * mm});
            skArc(sketch, "E222.3.15", {"start": v(5.13, -3.03) * mm, "mid": v(5.14, -3.13) * mm, "end": v(5.09, -3.21) * mm});
            skArc(sketch, "E222.4.0", {"start": v(3.45, -4.15) * mm, "mid": v(3.5, -4.3) * mm, "end": v(3.6, -4.43) * mm});
            skArc(sketch, "E222.4.1", {"start": v(3.58, -3.58) * mm, "mid": v(3.43, -3.85) * mm, "end": v(3.45, -4.15) * mm});
            skArc(sketch, "E222.4.2", {"start": v(4.55, -4.55) * mm, "mid": v(18.78, -4.9) * mm, "end": v(17.73, -19.1) * mm});
            skPoint(sketch, "E222.4.3", {"position": v(4.1, -4.1) * mm});
            skArc(sketch, "E222.4.4", {"start": v(4.15, -3.45) * mm, "mid": v(4.3, -3.5) * mm, "end": v(4.43, -3.6) * mm});
            skLineSegment(sketch, "E222.4.5", {"start": v(19.1, -17.73) * mm, "end": v(3.4, -4.85) * mm});
            skArc(sketch, "E222.4.6", {"start": v(4.62, -3.6) * mm, "mid": v(4.74, -3.5) * mm, "end": v(4.85, -3.4) * mm});
            skLineSegment(sketch, "E222.4.7", {"start": v(17.73, -19.1) * mm, "end": v(4.85, -3.4) * mm});
            skArc(sketch, "E222.4.8", {"start": v(3.58, -3.58) * mm, "mid": v(3.85, -3.43) * mm, "end": v(4.15, -3.45) * mm});
            skPoint(sketch, "E222.4.9", {"position": v(4.55, -4.55) * mm});
            skArc(sketch, "E222.4.10", {"start": v(4.29, -4.29) * mm, "mid": v(4.65, -3.94) * mm, "end": v(5.03, -3.62) * mm, "construction": true});
            skArc(sketch, "E222.4.11", {"start": v(4.55, -4.55) * mm, "mid": v(4.9, -18.78) * mm, "end": v(19.1, -17.73) * mm});
            skPoint(sketch, "E222.4.12", {"position": v(4.29, -4.29) * mm});
            skArc(sketch, "E222.4.13", {"start": v(3.6, -4.62) * mm, "mid": v(3.5, -4.74) * mm, "end": v(3.4, -4.85) * mm});
            skArc(sketch, "E222.4.14", {"start": v(4.43, -3.6) * mm, "mid": v(4.53, -3.63) * mm, "end": v(4.62, -3.6) * mm});
            skArc(sketch, "E222.4.15", {"start": v(3.6, -4.43) * mm, "mid": v(3.63, -4.53) * mm, "end": v(3.6, -4.62) * mm});
            skArc(sketch, "E222.5.0", {"start": v(2.17, -5.86) * mm, "mid": v(2.26, -6) * mm, "end": v(2.37, -6.11) * mm});
            skArc(sketch, "E222.5.1", {"start": v(2.18, -5.28) * mm, "mid": v(2.1, -5.57) * mm, "end": v(2.17, -5.86) * mm});
            skArc(sketch, "E222.5.2", {"start": v(3.33, -6.04) * mm, "mid": v(17.35, -3.6) * mm, "end": v(19.1, -17.73) * mm});
            skPoint(sketch, "E222.5.3", {"position": v(2.8, -5.7) * mm});
            skArc(sketch, "E222.5.4", {"start": v(2.72, -5.03) * mm, "mid": v(2.88, -5.07) * mm, "end": v(3.03, -5.13) * mm});
            skLineSegment(sketch, "E222.5.5", {"start": v(20.16, -16.13) * mm, "end": v(2.26, -6.56) * mm});
            skArc(sketch, "E222.5.6", {"start": v(3.21, -5.09) * mm, "mid": v(3.3, -4.97) * mm, "end": v(3.4, -4.85) * mm});
            skLineSegment(sketch, "E222.5.7", {"start": v(19.1, -17.73) * mm, "end": v(3.4, -4.85) * mm});
            skArc(sketch, "E222.5.8", {"start": v(2.18, -5.28) * mm, "mid": v(2.42, -5.08) * mm, "end": v(2.72, -5.03) * mm});
            skPoint(sketch, "E222.5.9", {"position": v(3.33, -6.04) * mm});
            skArc(sketch, "E222.5.10", {"start": v(3.02, -5.83) * mm, "mid": v(3.3, -5.42) * mm, "end": v(3.62, -5.03) * mm, "construction": true});
            skArc(sketch, "E222.5.11", {"start": v(3.33, -6.04) * mm, "mid": v(6.45, -19.93) * mm, "end": v(20.16, -16.13) * mm});
            skPoint(sketch, "E222.5.12", {"position": v(3.02, -5.83) * mm});
            skArc(sketch, "E222.5.13", {"start": v(2.4, -6.3) * mm, "mid": v(2.33, -6.43) * mm, "end": v(2.26, -6.56) * mm});
            skArc(sketch, "E222.5.14", {"start": v(3.03, -5.13) * mm, "mid": v(3.13, -5.14) * mm, "end": v(3.21, -5.09) * mm});
            skArc(sketch, "E222.5.15", {"start": v(2.37, -6.11) * mm, "mid": v(2.42, -6.2) * mm, "end": v(2.4, -6.3) * mm});
            skArc(sketch, "E222.6.0", {"start": v(1.25, -7.8) * mm, "mid": v(1.36, -7.9) * mm, "end": v(1.5, -8) * mm});
            skArc(sketch, "E222.6.1", {"start": v(1.15, -7.21) * mm, "mid": v(1.11, -7.52) * mm, "end": v(1.25, -7.8) * mm});
            skArc(sketch, "E222.6.2", {"start": v(2.42, -7.74) * mm, "mid": v(15.7, -2.62) * mm, "end": v(20.16, -16.13) * mm});
            skPoint(sketch, "E222.6.3", {"position": v(1.84, -7.5) * mm});
            skArc(sketch, "E222.6.4", {"start": v(1.63, -6.87) * mm, "mid": v(1.79, -6.87) * mm, "end": v(1.95, -6.9) * mm});
            skLineSegment(sketch, "E222.6.5", {"start": v(20.9, -14.35) * mm, "end": v(1.47, -8.46) * mm});
            skArc(sketch, "E222.6.6", {"start": v(2.12, -6.83) * mm, "mid": v(2.19, -6.7) * mm, "end": v(2.26, -6.56) * mm});
            skLineSegment(sketch, "E222.6.7", {"start": v(20.16, -16.13) * mm, "end": v(2.26, -6.56) * mm});
            skArc(sketch, "E222.6.8", {"start": v(1.15, -7.21) * mm, "mid": v(1.34, -6.97) * mm, "end": v(1.63, -6.87) * mm});
            skPoint(sketch, "E222.6.9", {"position": v(2.42, -7.74) * mm});
            skArc(sketch, "E222.6.10", {"start": v(2.08, -7.6) * mm, "mid": v(2.28, -7.14) * mm, "end": v(2.5, -6.7) * mm, "construction": true});
            skArc(sketch, "E222.6.11", {"start": v(2.42, -7.74) * mm, "mid": v(8.2, -20.75) * mm, "end": v(20.9, -14.35) * mm});
            skPoint(sketch, "E222.6.12", {"position": v(2.08, -7.6) * mm});
            skArc(sketch, "E222.6.13", {"start": v(1.56, -8.17) * mm, "mid": v(1.52, -8.32) * mm, "end": v(1.47, -8.46) * mm});
            skArc(sketch, "E222.6.14", {"start": v(1.95, -6.9) * mm, "mid": v(2.05, -6.9) * mm, "end": v(2.12, -6.83) * mm});
            skArc(sketch, "E222.6.15", {"start": v(1.5, -8) * mm, "mid": v(1.56, -8.07) * mm, "end": v(1.56, -8.17) * mm});
            skArc(sketch, "E222.7.0", {"start": v(0.72, -9.86) * mm, "mid": v(0.86, -9.95) * mm, "end": v(1, -10.02) * mm});
            skArc(sketch, "E222.7.1", {"start": v(0.51, -9.31) * mm, "mid": v(0.54, -9.62) * mm, "end": v(0.72, -9.86) * mm});
            skArc(sketch, "E222.7.2", {"start": v(1.86, -9.58) * mm, "mid": v(13.89, -1.97) * mm, "end": v(20.9, -14.35) * mm});
            skPoint(sketch, "E222.7.3", {"position": v(1.25, -9.46) * mm});
            skArc(sketch, "E222.7.4", {"start": v(0.91, -8.89) * mm, "mid": v(1.07, -8.86) * mm, "end": v(1.23, -8.86) * mm});
            skLineSegment(sketch, "E222.7.5", {"start": v(21.28, -12.46) * mm, "end": v(1.07, -10.47) * mm});
            skArc(sketch, "E222.7.6", {"start": v(1.39, -8.74) * mm, "mid": v(1.43, -8.6) * mm, "end": v(1.47, -8.46) * mm});
            skLineSegment(sketch, "E222.7.7", {"start": v(20.9, -14.35) * mm, "end": v(1.47, -8.46) * mm});
            skArc(sketch, "E222.7.8", {"start": v(0.51, -9.31) * mm, "mid": v(0.65, -9.04) * mm, "end": v(0.91, -8.89) * mm});
            skPoint(sketch, "E222.7.9", {"position": v(1.86, -9.58) * mm});
            skArc(sketch, "E222.7.10", {"start": v(1.5, -9.51) * mm, "mid": v(1.6, -9.02) * mm, "end": v(1.74, -8.54) * mm, "construction": true});
            skArc(sketch, "E222.7.11", {"start": v(1.86, -9.58) * mm, "mid": v(10.06, -21.22) * mm, "end": v(21.28, -12.46) * mm});
            skPoint(sketch, "E222.7.12", {"position": v(1.5, -9.51) * mm});
            skArc(sketch, "E222.7.13", {"start": v(1.1, -10.18) * mm, "mid": v(1.09, -10.32) * mm, "end": v(1.07, -10.47) * mm});
            skArc(sketch, "E222.7.14", {"start": v(1.23, -8.86) * mm, "mid": v(1.33, -8.83) * mm, "end": v(1.39, -8.74) * mm});
            skArc(sketch, "E222.7.15", {"start": v(1, -10.02) * mm, "mid": v(1.08, -10.08) * mm, "end": v(1.1, -10.18) * mm});
            skArc(sketch, "E222.8.0", {"start": v(0.6, -12) * mm, "mid": v(0.76, -12.06) * mm, "end": v(0.92, -12.1) * mm});
            skArc(sketch, "E222.8.1", {"start": v(0.3, -11.5) * mm, "mid": v(0.38, -11.8) * mm, "end": v(0.6, -12) * mm});
            skArc(sketch, "E222.8.2", {"start": v(1.68, -11.5) * mm, "mid": v(11.98, -1.69) * mm, "end": v(21.28, -12.46) * mm});
            skPoint(sketch, "E222.8.3", {"position": v(1.05, -11.5) * mm});
            skArc(sketch, "E222.8.4", {"start": v(0.6, -11) * mm, "mid": v(0.76, -10.94) * mm, "end": v(0.92, -10.9) * mm});
            skLineSegment(sketch, "E222.8.5", {"start": v(21.28, -10.54) * mm, "end": v(1.07, -12.53) * mm});
            skArc(sketch, "E222.8.6", {"start": v(1.05, -10.77) * mm, "mid": v(1.06, -10.62) * mm, "end": v(1.07, -10.47) * mm});
            skLineSegment(sketch, "E222.8.7", {"start": v(21.28, -12.46) * mm, "end": v(1.07, -10.47) * mm});
            skArc(sketch, "E222.8.8", {"start": v(0.3, -11.5) * mm, "mid": v(0.38, -11.2) * mm, "end": v(0.6, -11) * mm});
            skPoint(sketch, "E222.8.9", {"position": v(1.68, -11.5) * mm});
            skArc(sketch, "E222.8.10", {"start": v(1.3, -11.5) * mm, "mid": v(1.31, -11) * mm, "end": v(1.35, -10.5) * mm, "construction": true});
            skArc(sketch, "E222.8.11", {"start": v(1.68, -11.5) * mm, "mid": v(11.98, -21.31) * mm, "end": v(21.28, -10.54) * mm});
            skPoint(sketch, "E222.8.12", {"position": v(1.3, -11.5) * mm});
            skArc(sketch, "E222.8.13", {"start": v(1.05, -12.23) * mm, "mid": v(1.06, -12.38) * mm, "end": v(1.07, -12.53) * mm});
            skArc(sketch, "E222.8.14", {"start": v(0.92, -10.9) * mm, "mid": v(1, -10.86) * mm, "end": v(1.05, -10.77) * mm});
            skArc(sketch, "E222.8.15", {"start": v(0.92, -12.1) * mm, "mid": v(1, -12.14) * mm, "end": v(1.05, -12.23) * mm});
            skArc(sketch, "E222.9.0", {"start": v(0.91, -14.11) * mm, "mid": v(1.07, -14.14) * mm, "end": v(1.23, -14.14) * mm});
            skArc(sketch, "E222.9.1", {"start": v(0.51, -13.69) * mm, "mid": v(0.65, -13.96) * mm, "end": v(0.91, -14.11) * mm});
            skArc(sketch, "E222.9.2", {"start": v(1.86, -13.42) * mm, "mid": v(10.06, -1.78) * mm, "end": v(21.28, -10.54) * mm});
            skPoint(sketch, "E222.9.3", {"position": v(1.25, -13.54) * mm});
            skArc(sketch, "E222.9.4", {"start": v(0.72, -13.14) * mm, "mid": v(0.86, -13.05) * mm, "end": v(1, -12.98) * mm});
            skLineSegment(sketch, "E222.9.5", {"start": v(20.9, -8.65) * mm, "end": v(1.47, -14.54) * mm});
            skArc(sketch, "E222.9.6", {"start": v(1.1, -12.82) * mm, "mid": v(1.09, -12.68) * mm, "end": v(1.07, -12.53) * mm});
            skLineSegment(sketch, "E222.9.7", {"start": v(21.28, -10.54) * mm, "end": v(1.07, -12.53) * mm});
            skArc(sketch, "E222.9.8", {"start": v(0.51, -13.69) * mm, "mid": v(0.54, -13.38) * mm, "end": v(0.72, -13.14) * mm});
            skPoint(sketch, "E222.9.9", {"position": v(1.86, -13.42) * mm});
            skArc(sketch, "E222.9.10", {"start": v(1.5, -13.49) * mm, "mid": v(1.41, -13) * mm, "end": v(1.35, -12.5) * mm, "construction": true});
            skArc(sketch, "E222.9.11", {"start": v(1.86, -13.42) * mm, "mid": v(13.89, -21.03) * mm, "end": v(20.9, -8.65) * mm});
            skPoint(sketch, "E222.9.12", {"position": v(1.5, -13.49) * mm});
            skArc(sketch, "E222.9.13", {"start": v(1.39, -14.26) * mm, "mid": v(1.43, -14.4) * mm, "end": v(1.47, -14.54) * mm});
            skArc(sketch, "E222.9.14", {"start": v(1, -12.98) * mm, "mid": v(1.08, -12.92) * mm, "end": v(1.1, -12.82) * mm});
            skArc(sketch, "E222.9.15", {"start": v(1.23, -14.14) * mm, "mid": v(1.33, -14.17) * mm, "end": v(1.39, -14.26) * mm});
            skArc(sketch, "E222.10.0", {"start": v(1.63, -16.13) * mm, "mid": v(1.79, -16.13) * mm, "end": v(1.95, -16.1) * mm});
            skArc(sketch, "E222.10.1", {"start": v(1.15, -15.79) * mm, "mid": v(1.34, -16.03) * mm, "end": v(1.63, -16.13) * mm});
            skArc(sketch, "E222.10.2", {"start": v(2.42, -15.26) * mm, "mid": v(8.2, -2.25) * mm, "end": v(20.9, -8.65) * mm});
            skPoint(sketch, "E222.10.3", {"position": v(1.84, -15.5) * mm});
            skArc(sketch, "E222.10.4", {"start": v(1.25, -15.2) * mm, "mid": v(1.36, -15.1) * mm, "end": v(1.5, -15) * mm});
            skLineSegment(sketch, "E222.10.5", {"start": v(20.16, -6.87) * mm, "end": v(2.26, -16.44) * mm});
            skArc(sketch, "E222.10.6", {"start": v(1.56, -14.83) * mm, "mid": v(1.52, -14.68) * mm, "end": v(1.47, -14.54) * mm});
            skLineSegment(sketch, "E222.10.7", {"start": v(20.9, -8.65) * mm, "end": v(1.47, -14.54) * mm});
            skArc(sketch, "E222.10.8", {"start": v(1.15, -15.79) * mm, "mid": v(1.11, -15.48) * mm, "end": v(1.25, -15.2) * mm});
            skPoint(sketch, "E222.10.9", {"position": v(2.42, -15.26) * mm});
            skArc(sketch, "E222.10.10", {"start": v(2.08, -15.4) * mm, "mid": v(1.9, -14.94) * mm, "end": v(1.74, -14.46) * mm, "construction": true});
            skArc(sketch, "E222.10.11", {"start": v(2.42, -15.26) * mm, "mid": v(15.7, -20.38) * mm, "end": v(20.16, -6.87) * mm});
            skPoint(sketch, "E222.10.12", {"position": v(2.08, -15.4) * mm});
            skArc(sketch, "E222.10.13", {"start": v(2.12, -16.17) * mm, "mid": v(2.19, -16.3) * mm, "end": v(2.26, -16.44) * mm});
            skArc(sketch, "E222.10.14", {"start": v(1.5, -15) * mm, "mid": v(1.56, -14.93) * mm, "end": v(1.56, -14.83) * mm});
            skArc(sketch, "E222.10.15", {"start": v(1.95, -16.1) * mm, "mid": v(2.05, -16.1) * mm, "end": v(2.12, -16.17) * mm});
            skArc(sketch, "E222.11.0", {"start": v(2.72, -17.97) * mm, "mid": v(2.88, -17.93) * mm, "end": v(3.03, -17.87) * mm});
            skArc(sketch, "E222.11.1", {"start": v(2.18, -17.72) * mm, "mid": v(2.42, -17.92) * mm, "end": v(2.72, -17.97) * mm});
            skArc(sketch, "E222.11.2", {"start": v(3.33, -16.96) * mm, "mid": v(6.45, -3.07) * mm, "end": v(20.16, -6.87) * mm});
            skPoint(sketch, "E222.11.3", {"position": v(2.8, -17.3) * mm});
            skArc(sketch, "E222.11.4", {"start": v(2.17, -17.14) * mm, "mid": v(2.26, -17) * mm, "end": v(2.37, -16.89) * mm});
            skLineSegment(sketch, "E222.11.5", {"start": v(19.1, -5.27) * mm, "end": v(3.4, -18.15) * mm});
            skArc(sketch, "E222.11.6", {"start": v(2.4, -16.7) * mm, "mid": v(2.33, -16.57) * mm, "end": v(2.26, -16.44) * mm});
            skLineSegment(sketch, "E222.11.7", {"start": v(20.16, -6.87) * mm, "end": v(2.26, -16.44) * mm});
            skArc(sketch, "E222.11.8", {"start": v(2.18, -17.72) * mm, "mid": v(2.1, -17.43) * mm, "end": v(2.17, -17.14) * mm});
            skPoint(sketch, "E222.11.9", {"position": v(3.33, -16.96) * mm});
            skArc(sketch, "E222.11.10", {"start": v(3.02, -17.17) * mm, "mid": v(2.75, -16.74) * mm, "end": v(2.5, -16.3) * mm, "construction": true});
            skArc(sketch, "E222.11.11", {"start": v(3.33, -16.96) * mm, "mid": v(17.35, -19.4) * mm, "end": v(19.1, -5.27) * mm});
            skPoint(sketch, "E222.11.12", {"position": v(3.02, -17.17) * mm});
            skArc(sketch, "E222.11.13", {"start": v(3.21, -17.91) * mm, "mid": v(3.3, -18.03) * mm, "end": v(3.4, -18.15) * mm});
            skArc(sketch, "E222.11.14", {"start": v(2.37, -16.89) * mm, "mid": v(2.42, -16.8) * mm, "end": v(2.4, -16.7) * mm});
            skArc(sketch, "E222.11.15", {"start": v(3.03, -17.87) * mm, "mid": v(3.13, -17.86) * mm, "end": v(3.21, -17.91) * mm});
            skArc(sketch, "E222.12.0", {"start": v(4.15, -19.55) * mm, "mid": v(4.3, -19.5) * mm, "end": v(4.43, -19.4) * mm});
            skArc(sketch, "E222.12.1", {"start": v(3.58, -19.42) * mm, "mid": v(3.85, -19.57) * mm, "end": v(4.15, -19.55) * mm});
            skArc(sketch, "E222.12.2", {"start": v(4.55, -18.45) * mm, "mid": v(4.9, -4.22) * mm, "end": v(19.1, -5.27) * mm});
            skPoint(sketch, "E222.12.3", {"position": v(4.1, -18.9) * mm});
            skArc(sketch, "E222.12.4", {"start": v(3.45, -18.85) * mm, "mid": v(3.5, -18.7) * mm, "end": v(3.6, -18.57) * mm});
            skLineSegment(sketch, "E222.12.5", {"start": v(17.73, -3.9) * mm, "end": v(4.85, -19.6) * mm});
            skArc(sketch, "E222.12.6", {"start": v(3.6, -18.38) * mm, "mid": v(3.5, -18.26) * mm, "end": v(3.4, -18.15) * mm});
            skLineSegment(sketch, "E222.12.7", {"start": v(19.1, -5.27) * mm, "end": v(3.4, -18.15) * mm});
            skArc(sketch, "E222.12.8", {"start": v(3.58, -19.42) * mm, "mid": v(3.43, -19.15) * mm, "end": v(3.45, -18.85) * mm});
            skPoint(sketch, "E222.12.9", {"position": v(4.55, -18.45) * mm});
            skArc(sketch, "E222.12.10", {"start": v(4.29, -18.71) * mm, "mid": v(3.94, -18.35) * mm, "end": v(3.62, -17.97) * mm, "construction": true});
            skArc(sketch, "E222.12.11", {"start": v(4.55, -18.45) * mm, "mid": v(18.78, -18.1) * mm, "end": v(17.73, -3.9) * mm});
            skPoint(sketch, "E222.12.12", {"position": v(4.29, -18.71) * mm});
            skArc(sketch, "E222.12.13", {"start": v(4.62, -19.4) * mm, "mid": v(4.74, -19.5) * mm, "end": v(4.85, -19.6) * mm});
            skArc(sketch, "E222.12.14", {"start": v(3.6, -18.57) * mm, "mid": v(3.63, -18.47) * mm, "end": v(3.6, -18.38) * mm});
            skArc(sketch, "E222.12.15", {"start": v(4.43, -19.4) * mm, "mid": v(4.53, -19.37) * mm, "end": v(4.62, -19.4) * mm});
            skArc(sketch, "E222.13.0", {"start": v(5.86, -20.83) * mm, "mid": v(6, -20.74) * mm, "end": v(6.11, -20.63) * mm});
            skArc(sketch, "E222.13.1", {"start": v(5.28, -20.82) * mm, "mid": v(5.57, -20.9) * mm, "end": v(5.86, -20.83) * mm});
            skArc(sketch, "E222.13.2", {"start": v(6.04, -19.67) * mm, "mid": v(3.6, -5.65) * mm, "end": v(17.73, -3.9) * mm});
            skPoint(sketch, "E222.13.3", {"position": v(5.7, -20.2) * mm});
            skArc(sketch, "E222.13.4", {"start": v(5.03, -20.28) * mm, "mid": v(5.07, -20.12) * mm, "end": v(5.13, -19.97) * mm});
            skLineSegment(sketch, "E222.13.5", {"start": v(16.13, -2.84) * mm, "end": v(6.56, -20.74) * mm});
            skArc(sketch, "E222.13.6", {"start": v(5.09, -19.79) * mm, "mid": v(4.97, -19.7) * mm, "end": v(4.85, -19.6) * mm});
            skLineSegment(sketch, "E222.13.7", {"start": v(17.73, -3.9) * mm, "end": v(4.85, -19.6) * mm});
            skArc(sketch, "E222.13.8", {"start": v(5.28, -20.82) * mm, "mid": v(5.08, -20.58) * mm, "end": v(5.03, -20.28) * mm});
            skPoint(sketch, "E222.13.9", {"position": v(6.04, -19.67) * mm});
            skArc(sketch, "E222.13.10", {"start": v(5.83, -19.98) * mm, "mid": v(5.42, -19.7) * mm, "end": v(5.03, -19.38) * mm, "construction": true});
            skArc(sketch, "E222.13.11", {"start": v(6.04, -19.67) * mm, "mid": v(19.93, -16.55) * mm, "end": v(16.13, -2.84) * mm});
            skPoint(sketch, "E222.13.12", {"position": v(5.83, -19.98) * mm});
            skArc(sketch, "E222.13.13", {"start": v(6.3, -20.6) * mm, "mid": v(6.43, -20.67) * mm, "end": v(6.56, -20.74) * mm});
            skArc(sketch, "E222.13.14", {"start": v(5.13, -19.97) * mm, "mid": v(5.14, -19.87) * mm, "end": v(5.09, -19.79) * mm});
            skArc(sketch, "E222.13.15", {"start": v(6.11, -20.63) * mm, "mid": v(6.2, -20.58) * mm, "end": v(6.3, -20.6) * mm});
            skArc(sketch, "E222.14.0", {"start": v(7.8, -21.75) * mm, "mid": v(7.9, -21.64) * mm, "end": v(8, -21.5) * mm});
            skArc(sketch, "E222.14.1", {"start": v(7.21, -21.85) * mm, "mid": v(7.52, -21.89) * mm, "end": v(7.8, -21.75) * mm});
            skArc(sketch, "E222.14.2", {"start": v(7.74, -20.58) * mm, "mid": v(2.62, -7.3) * mm, "end": v(16.13, -2.84) * mm});
            skPoint(sketch, "E222.14.3", {"position": v(7.5, -21.16) * mm});
            skArc(sketch, "E222.14.4", {"start": v(6.87, -21.37) * mm, "mid": v(6.87, -21.21) * mm, "end": v(6.9, -21.05) * mm});
            skLineSegment(sketch, "E222.14.5", {"start": v(14.35, -2.1) * mm, "end": v(8.46, -21.53) * mm});
            skArc(sketch, "E222.14.6", {"start": v(6.83, -20.88) * mm, "mid": v(6.7, -20.81) * mm, "end": v(6.56, -20.74) * mm});
            skLineSegment(sketch, "E222.14.7", {"start": v(16.13, -2.84) * mm, "end": v(6.56, -20.74) * mm});
            skArc(sketch, "E222.14.8", {"start": v(7.21, -21.85) * mm, "mid": v(6.97, -21.66) * mm, "end": v(6.87, -21.37) * mm});
            skPoint(sketch, "E222.14.9", {"position": v(7.74, -20.58) * mm});
            skArc(sketch, "E222.14.10", {"start": v(7.6, -20.92) * mm, "mid": v(7.14, -20.72) * mm, "end": v(6.7, -20.5) * mm, "construction": true});
            skArc(sketch, "E222.14.11", {"start": v(7.74, -20.58) * mm, "mid": v(20.75, -14.8) * mm, "end": v(14.35, -2.1) * mm});
            skPoint(sketch, "E222.14.12", {"position": v(7.6, -20.92) * mm});
            skArc(sketch, "E222.14.13", {"start": v(8.17, -21.44) * mm, "mid": v(8.32, -21.48) * mm, "end": v(8.46, -21.53) * mm});
            skArc(sketch, "E222.14.14", {"start": v(6.9, -21.05) * mm, "mid": v(6.9, -20.95) * mm, "end": v(6.83, -20.88) * mm});
            skArc(sketch, "E222.14.15", {"start": v(8, -21.5) * mm, "mid": v(8.07, -21.44) * mm, "end": v(8.17, -21.44) * mm});
            skArc(sketch, "E222.15.0", {"start": v(9.86, -22.28) * mm, "mid": v(9.95, -22.14) * mm, "end": v(10.02, -22) * mm});
            skArc(sketch, "E222.15.1", {"start": v(9.31, -22.49) * mm, "mid": v(9.62, -22.46) * mm, "end": v(9.86, -22.28) * mm});
            skArc(sketch, "E222.15.2", {"start": v(9.58, -21.14) * mm, "mid": v(1.97, -9.11) * mm, "end": v(14.35, -2.1) * mm});
            skPoint(sketch, "E222.15.3", {"position": v(9.46, -21.75) * mm});
            skArc(sketch, "E222.15.4", {"start": v(8.89, -22.09) * mm, "mid": v(8.86, -21.93) * mm, "end": v(8.86, -21.77) * mm});
            skLineSegment(sketch, "E222.15.5", {"start": v(12.46, -1.72) * mm, "end": v(10.47, -21.93) * mm});
            skArc(sketch, "E222.15.6", {"start": v(8.74, -21.61) * mm, "mid": v(8.6, -21.57) * mm, "end": v(8.46, -21.53) * mm});
            skLineSegment(sketch, "E222.15.7", {"start": v(14.35, -2.1) * mm, "end": v(8.46, -21.53) * mm});
            skArc(sketch, "E222.15.8", {"start": v(9.31, -22.49) * mm, "mid": v(9.04, -22.35) * mm, "end": v(8.89, -22.09) * mm});
            skPoint(sketch, "E222.15.9", {"position": v(9.58, -21.14) * mm});
            skArc(sketch, "E222.15.10", {"start": v(9.51, -21.5) * mm, "mid": v(9.02, -21.4) * mm, "end": v(8.54, -21.26) * mm, "construction": true});
            skArc(sketch, "E222.15.11", {"start": v(9.58, -21.14) * mm, "mid": v(21.22, -12.94) * mm, "end": v(12.46, -1.72) * mm});
            skPoint(sketch, "E222.15.12", {"position": v(9.51, -21.5) * mm});
            skArc(sketch, "E222.15.13", {"start": v(10.18, -21.9) * mm, "mid": v(10.32, -21.91) * mm, "end": v(10.47, -21.93) * mm});
            skArc(sketch, "E222.15.14", {"start": v(8.86, -21.77) * mm, "mid": v(8.83, -21.67) * mm, "end": v(8.74, -21.61) * mm});
            skArc(sketch, "E222.15.15", {"start": v(10.02, -22) * mm, "mid": v(10.08, -21.92) * mm, "end": v(10.18, -21.9) * mm});
            skArc(sketch, "E222.16.0", {"start": v(12, -22.4) * mm, "mid": v(12.06, -22.24) * mm, "end": v(12.1, -22.08) * mm});
            skArc(sketch, "E222.16.1", {"start": v(11.5, -22.7) * mm, "mid": v(11.8, -22.62) * mm, "end": v(12, -22.4) * mm});
            skArc(sketch, "E222.16.2", {"start": v(11.5, -21.32) * mm, "mid": v(1.69, -11.02) * mm, "end": v(12.46, -1.72) * mm});
            skPoint(sketch, "E222.16.3", {"position": v(11.5, -21.95) * mm});
            skArc(sketch, "E222.16.4", {"start": v(11, -22.4) * mm, "mid": v(10.94, -22.24) * mm, "end": v(10.9, -22.08) * mm});
            skLineSegment(sketch, "E222.16.5", {"start": v(10.54, -1.72) * mm, "end": v(12.53, -21.93) * mm});
            skArc(sketch, "E222.16.6", {"start": v(10.77, -21.95) * mm, "mid": v(10.62, -21.94) * mm, "end": v(10.47, -21.93) * mm});
            skLineSegment(sketch, "E222.16.7", {"start": v(12.46, -1.72) * mm, "end": v(10.47, -21.93) * mm});
            skArc(sketch, "E222.16.8", {"start": v(11.5, -22.7) * mm, "mid": v(11.2, -22.62) * mm, "end": v(11, -22.4) * mm});
            skPoint(sketch, "E222.16.9", {"position": v(11.5, -21.32) * mm});
            skArc(sketch, "E222.16.10", {"start": v(11.5, -21.7) * mm, "mid": v(11, -21.69) * mm, "end": v(10.5, -21.65) * mm, "construction": true});
            skArc(sketch, "E222.16.11", {"start": v(11.5, -21.32) * mm, "mid": v(21.31, -11.02) * mm, "end": v(10.54, -1.72) * mm});
            skPoint(sketch, "E222.16.12", {"position": v(11.5, -21.7) * mm});
            skArc(sketch, "E222.16.13", {"start": v(12.23, -21.95) * mm, "mid": v(12.38, -21.94) * mm, "end": v(12.53, -21.93) * mm});
            skArc(sketch, "E222.16.14", {"start": v(10.9, -22.08) * mm, "mid": v(10.86, -22) * mm, "end": v(10.77, -21.95) * mm});
            skArc(sketch, "E222.16.15", {"start": v(12.1, -22.08) * mm, "mid": v(12.14, -22) * mm, "end": v(12.23, -21.95) * mm});
            skArc(sketch, "E222.17.0", {"start": v(14.11, -22.09) * mm, "mid": v(14.14, -21.93) * mm, "end": v(14.14, -21.77) * mm});
            skArc(sketch, "E222.17.1", {"start": v(13.69, -22.49) * mm, "mid": v(13.96, -22.35) * mm, "end": v(14.11, -22.09) * mm});
            skArc(sketch, "E222.17.2", {"start": v(13.42, -21.14) * mm, "mid": v(1.78, -12.94) * mm, "end": v(10.54, -1.72) * mm});
            skPoint(sketch, "E222.17.3", {"position": v(13.54, -21.75) * mm});
            skArc(sketch, "E222.17.4", {"start": v(13.14, -22.28) * mm, "mid": v(13.05, -22.14) * mm, "end": v(12.98, -22) * mm});
            skLineSegment(sketch, "E222.17.5", {"start": v(8.65, -2.1) * mm, "end": v(14.54, -21.53) * mm});
            skArc(sketch, "E222.17.6", {"start": v(12.82, -21.9) * mm, "mid": v(12.68, -21.91) * mm, "end": v(12.53, -21.93) * mm});
            skLineSegment(sketch, "E222.17.7", {"start": v(10.54, -1.72) * mm, "end": v(12.53, -21.93) * mm});
            skArc(sketch, "E222.17.8", {"start": v(13.69, -22.49) * mm, "mid": v(13.38, -22.46) * mm, "end": v(13.14, -22.28) * mm});
            skPoint(sketch, "E222.17.9", {"position": v(13.42, -21.14) * mm});
            skArc(sketch, "E222.17.10", {"start": v(13.49, -21.5) * mm, "mid": v(13, -21.59) * mm, "end": v(12.5, -21.65) * mm, "construction": true});
            skArc(sketch, "E222.17.11", {"start": v(13.42, -21.14) * mm, "mid": v(21.03, -9.11) * mm, "end": v(8.65, -2.1) * mm});
            skPoint(sketch, "E222.17.12", {"position": v(13.49, -21.5) * mm});
            skArc(sketch, "E222.17.13", {"start": v(14.26, -21.61) * mm, "mid": v(14.4, -21.57) * mm, "end": v(14.54, -21.53) * mm});
            skArc(sketch, "E222.17.14", {"start": v(12.98, -22) * mm, "mid": v(12.92, -21.92) * mm, "end": v(12.82, -21.9) * mm});
            skArc(sketch, "E222.17.15", {"start": v(14.14, -21.77) * mm, "mid": v(14.17, -21.67) * mm, "end": v(14.26, -21.61) * mm});
            skArc(sketch, "E222.18.0", {"start": v(16.13, -21.37) * mm, "mid": v(16.13, -21.21) * mm, "end": v(16.1, -21.05) * mm});
            skArc(sketch, "E222.18.1", {"start": v(15.79, -21.85) * mm, "mid": v(16.03, -21.66) * mm, "end": v(16.13, -21.37) * mm});
            skArc(sketch, "E222.18.2", {"start": v(15.26, -20.58) * mm, "mid": v(2.25, -14.8) * mm, "end": v(8.65, -2.1) * mm});
            skPoint(sketch, "E222.18.3", {"position": v(15.5, -21.16) * mm});
            skArc(sketch, "E222.18.4", {"start": v(15.2, -21.75) * mm, "mid": v(15.1, -21.64) * mm, "end": v(15, -21.5) * mm});
            skLineSegment(sketch, "E222.18.5", {"start": v(6.87, -2.84) * mm, "end": v(16.44, -20.74) * mm});
            skArc(sketch, "E222.18.6", {"start": v(14.83, -21.44) * mm, "mid": v(14.68, -21.48) * mm, "end": v(14.54, -21.53) * mm});
            skLineSegment(sketch, "E222.18.7", {"start": v(8.65, -2.1) * mm, "end": v(14.54, -21.53) * mm});
            skArc(sketch, "E222.18.8", {"start": v(15.79, -21.85) * mm, "mid": v(15.48, -21.89) * mm, "end": v(15.2, -21.75) * mm});
            skPoint(sketch, "E222.18.9", {"position": v(15.26, -20.58) * mm});
            skArc(sketch, "E222.18.10", {"start": v(15.4, -20.92) * mm, "mid": v(14.94, -21.1) * mm, "end": v(14.46, -21.26) * mm, "construction": true});
            skArc(sketch, "E222.18.11", {"start": v(15.26, -20.58) * mm, "mid": v(20.38, -7.3) * mm, "end": v(6.87, -2.84) * mm});
            skPoint(sketch, "E222.18.12", {"position": v(15.4, -20.92) * mm});
            skArc(sketch, "E222.18.13", {"start": v(16.17, -20.88) * mm, "mid": v(16.3, -20.81) * mm, "end": v(16.44, -20.74) * mm});
            skArc(sketch, "E222.18.14", {"start": v(15, -21.5) * mm, "mid": v(14.93, -21.44) * mm, "end": v(14.83, -21.44) * mm});
            skArc(sketch, "E222.18.15", {"start": v(16.1, -21.05) * mm, "mid": v(16.1, -20.95) * mm, "end": v(16.17, -20.88) * mm});
            skArc(sketch, "E222.19.0", {"start": v(17.97, -20.28) * mm, "mid": v(17.93, -20.12) * mm, "end": v(17.87, -19.97) * mm});
            skArc(sketch, "E222.19.1", {"start": v(17.72, -20.82) * mm, "mid": v(17.92, -20.58) * mm, "end": v(17.97, -20.28) * mm});
            skArc(sketch, "E222.19.2", {"start": v(16.96, -19.67) * mm, "mid": v(3.07, -16.55) * mm, "end": v(6.87, -2.84) * mm});
            skPoint(sketch, "E222.19.3", {"position": v(17.3, -20.2) * mm});
            skArc(sketch, "E222.19.4", {"start": v(17.14, -20.83) * mm, "mid": v(17, -20.74) * mm, "end": v(16.89, -20.63) * mm});
            skLineSegment(sketch, "E222.19.5", {"start": v(5.27, -3.9) * mm, "end": v(18.15, -19.6) * mm});
            skArc(sketch, "E222.19.6", {"start": v(16.7, -20.6) * mm, "mid": v(16.57, -20.67) * mm, "end": v(16.44, -20.74) * mm});
            skLineSegment(sketch, "E222.19.7", {"start": v(6.87, -2.84) * mm, "end": v(16.44, -20.74) * mm});
            skArc(sketch, "E222.19.8", {"start": v(17.72, -20.82) * mm, "mid": v(17.43, -20.9) * mm, "end": v(17.14, -20.83) * mm});
            skPoint(sketch, "E222.19.9", {"position": v(16.96, -19.67) * mm});
            skArc(sketch, "E222.19.10", {"start": v(17.17, -19.98) * mm, "mid": v(16.74, -20.25) * mm, "end": v(16.3, -20.5) * mm, "construction": true});
            skArc(sketch, "E222.19.11", {"start": v(16.96, -19.67) * mm, "mid": v(19.4, -5.65) * mm, "end": v(5.27, -3.9) * mm});
            skPoint(sketch, "E222.19.12", {"position": v(17.17, -19.98) * mm});
            skArc(sketch, "E222.19.13", {"start": v(17.91, -19.79) * mm, "mid": v(18.03, -19.7) * mm, "end": v(18.15, -19.6) * mm});
            skArc(sketch, "E222.19.14", {"start": v(16.89, -20.63) * mm, "mid": v(16.8, -20.58) * mm, "end": v(16.7, -20.6) * mm});
            skArc(sketch, "E222.19.15", {"start": v(17.87, -19.97) * mm, "mid": v(17.86, -19.87) * mm, "end": v(17.91, -19.79) * mm});
            skArc(sketch, "E222.20.0", {"start": v(19.55, -18.85) * mm, "mid": v(19.5, -18.7) * mm, "end": v(19.4, -18.57) * mm});
            skArc(sketch, "E222.20.1", {"start": v(19.42, -19.42) * mm, "mid": v(19.57, -19.15) * mm, "end": v(19.55, -18.85) * mm});
            skArc(sketch, "E222.20.2", {"start": v(18.45, -18.45) * mm, "mid": v(4.22, -18.1) * mm, "end": v(5.27, -3.9) * mm});
            skPoint(sketch, "E222.20.3", {"position": v(18.9, -18.9) * mm});
            skArc(sketch, "E222.20.4", {"start": v(18.85, -19.55) * mm, "mid": v(18.7, -19.5) * mm, "end": v(18.57, -19.4) * mm});
            skLineSegment(sketch, "E222.20.5", {"start": v(3.9, -5.27) * mm, "end": v(19.6, -18.15) * mm});
            skArc(sketch, "E222.20.6", {"start": v(18.38, -19.4) * mm, "mid": v(18.26, -19.5) * mm, "end": v(18.15, -19.6) * mm});
            skLineSegment(sketch, "E222.20.7", {"start": v(5.27, -3.9) * mm, "end": v(18.15, -19.6) * mm});
            skArc(sketch, "E222.20.8", {"start": v(19.42, -19.42) * mm, "mid": v(19.15, -19.57) * mm, "end": v(18.85, -19.55) * mm});
            skPoint(sketch, "E222.20.9", {"position": v(18.45, -18.45) * mm});
            skArc(sketch, "E222.20.10", {"start": v(18.71, -18.71) * mm, "mid": v(18.35, -19.06) * mm, "end": v(17.97, -19.38) * mm, "construction": true});
            skArc(sketch, "E222.20.11", {"start": v(18.45, -18.45) * mm, "mid": v(18.1, -4.22) * mm, "end": v(3.9, -5.27) * mm});
            skPoint(sketch, "E222.20.12", {"position": v(18.71, -18.71) * mm});
            skArc(sketch, "E222.20.13", {"start": v(19.4, -18.38) * mm, "mid": v(19.5, -18.26) * mm, "end": v(19.6, -18.15) * mm});
            skArc(sketch, "E222.20.14", {"start": v(18.57, -19.4) * mm, "mid": v(18.47, -19.37) * mm, "end": v(18.38, -19.4) * mm});
            skArc(sketch, "E222.20.15", {"start": v(19.4, -18.57) * mm, "mid": v(19.37, -18.47) * mm, "end": v(19.4, -18.38) * mm});
            skArc(sketch, "E222.21.0", {"start": v(20.83, -17.14) * mm, "mid": v(20.74, -17) * mm, "end": v(20.63, -16.89) * mm});
            skArc(sketch, "E222.21.1", {"start": v(20.82, -17.72) * mm, "mid": v(20.9, -17.43) * mm, "end": v(20.83, -17.14) * mm});
            skArc(sketch, "E222.21.2", {"start": v(19.67, -16.96) * mm, "mid": v(5.65, -19.4) * mm, "end": v(3.9, -5.27) * mm});
            skPoint(sketch, "E222.21.3", {"position": v(20.2, -17.3) * mm});
            skArc(sketch, "E222.21.4", {"start": v(20.28, -17.97) * mm, "mid": v(20.12, -17.93) * mm, "end": v(19.97, -17.87) * mm});
            skLineSegment(sketch, "E222.21.5", {"start": v(2.84, -6.87) * mm, "end": v(20.74, -16.44) * mm});
            skArc(sketch, "E222.21.6", {"start": v(19.79, -17.91) * mm, "mid": v(19.7, -18.03) * mm, "end": v(19.6, -18.15) * mm});
            skLineSegment(sketch, "E222.21.7", {"start": v(3.9, -5.27) * mm, "end": v(19.6, -18.15) * mm});
            skArc(sketch, "E222.21.8", {"start": v(20.82, -17.72) * mm, "mid": v(20.58, -17.92) * mm, "end": v(20.28, -17.97) * mm});
            skPoint(sketch, "E222.21.9", {"position": v(19.67, -16.96) * mm});
            skArc(sketch, "E222.21.10", {"start": v(19.98, -17.17) * mm, "mid": v(19.7, -17.58) * mm, "end": v(19.38, -17.97) * mm, "construction": true});
            skArc(sketch, "E222.21.11", {"start": v(19.67, -16.96) * mm, "mid": v(16.55, -3.07) * mm, "end": v(2.84, -6.87) * mm});
            skPoint(sketch, "E222.21.12", {"position": v(19.98, -17.17) * mm});
            skArc(sketch, "E222.21.13", {"start": v(20.6, -16.7) * mm, "mid": v(20.67, -16.57) * mm, "end": v(20.74, -16.44) * mm});
            skArc(sketch, "E222.21.14", {"start": v(19.97, -17.87) * mm, "mid": v(19.87, -17.86) * mm, "end": v(19.79, -17.91) * mm});
            skArc(sketch, "E222.21.15", {"start": v(20.63, -16.89) * mm, "mid": v(20.58, -16.8) * mm, "end": v(20.6, -16.7) * mm});
            skArc(sketch, "E222.22.0", {"start": v(21.75, -15.2) * mm, "mid": v(21.64, -15.1) * mm, "end": v(21.5, -15) * mm});
            skArc(sketch, "E222.22.1", {"start": v(21.85, -15.79) * mm, "mid": v(21.89, -15.48) * mm, "end": v(21.75, -15.2) * mm});
            skArc(sketch, "E222.22.2", {"start": v(20.58, -15.26) * mm, "mid": v(7.3, -20.38) * mm, "end": v(2.84, -6.87) * mm});
            skPoint(sketch, "E222.22.3", {"position": v(21.16, -15.5) * mm});
            skArc(sketch, "E222.22.4", {"start": v(21.37, -16.13) * mm, "mid": v(21.21, -16.13) * mm, "end": v(21.05, -16.1) * mm});
            skLineSegment(sketch, "E222.22.5", {"start": v(2.1, -8.65) * mm, "end": v(21.53, -14.54) * mm});
            skArc(sketch, "E222.22.6", {"start": v(20.88, -16.17) * mm, "mid": v(20.81, -16.3) * mm, "end": v(20.74, -16.44) * mm});
            skLineSegment(sketch, "E222.22.7", {"start": v(2.84, -6.87) * mm, "end": v(20.74, -16.44) * mm});
            skArc(sketch, "E222.22.8", {"start": v(21.85, -15.79) * mm, "mid": v(21.66, -16.03) * mm, "end": v(21.37, -16.13) * mm});
            skPoint(sketch, "E222.22.9", {"position": v(20.58, -15.26) * mm});
            skArc(sketch, "E222.22.10", {"start": v(20.92, -15.4) * mm, "mid": v(20.72, -15.86) * mm, "end": v(20.5, -16.3) * mm, "construction": true});
            skArc(sketch, "E222.22.11", {"start": v(20.58, -15.26) * mm, "mid": v(14.8, -2.25) * mm, "end": v(2.1, -8.65) * mm});
            skPoint(sketch, "E222.22.12", {"position": v(20.92, -15.4) * mm});
            skArc(sketch, "E222.22.13", {"start": v(21.44, -14.83) * mm, "mid": v(21.48, -14.68) * mm, "end": v(21.53, -14.54) * mm});
            skArc(sketch, "E222.22.14", {"start": v(21.05, -16.1) * mm, "mid": v(20.95, -16.1) * mm, "end": v(20.88, -16.17) * mm});
            skArc(sketch, "E222.22.15", {"start": v(21.5, -15) * mm, "mid": v(21.44, -14.93) * mm, "end": v(21.44, -14.83) * mm});
            skArc(sketch, "E222.23.0", {"start": v(22.28, -13.14) * mm, "mid": v(22.14, -13.05) * mm, "end": v(22, -12.98) * mm});
            skArc(sketch, "E222.23.1", {"start": v(22.49, -13.69) * mm, "mid": v(22.46, -13.38) * mm, "end": v(22.28, -13.14) * mm});
            skArc(sketch, "E222.23.2", {"start": v(21.14, -13.42) * mm, "mid": v(9.11, -21.03) * mm, "end": v(2.1, -8.65) * mm});
            skPoint(sketch, "E222.23.3", {"position": v(21.75, -13.54) * mm});
            skArc(sketch, "E222.23.4", {"start": v(22.09, -14.11) * mm, "mid": v(21.93, -14.14) * mm, "end": v(21.77, -14.14) * mm});
            skLineSegment(sketch, "E222.23.5", {"start": v(1.72, -10.54) * mm, "end": v(21.93, -12.53) * mm});
            skArc(sketch, "E222.23.6", {"start": v(21.61, -14.26) * mm, "mid": v(21.57, -14.4) * mm, "end": v(21.53, -14.54) * mm});
            skLineSegment(sketch, "E222.23.7", {"start": v(2.1, -8.65) * mm, "end": v(21.53, -14.54) * mm});
            skArc(sketch, "E222.23.8", {"start": v(22.49, -13.69) * mm, "mid": v(22.35, -13.96) * mm, "end": v(22.09, -14.11) * mm});
            skPoint(sketch, "E222.23.9", {"position": v(21.14, -13.42) * mm});
            skArc(sketch, "E222.23.10", {"start": v(21.5, -13.49) * mm, "mid": v(21.4, -13.98) * mm, "end": v(21.26, -14.46) * mm, "construction": true});
            skArc(sketch, "E222.23.11", {"start": v(21.14, -13.42) * mm, "mid": v(12.94, -1.78) * mm, "end": v(1.72, -10.54) * mm});
            skPoint(sketch, "E222.23.12", {"position": v(21.5, -13.49) * mm});
            skArc(sketch, "E222.23.13", {"start": v(21.9, -12.82) * mm, "mid": v(21.91, -12.68) * mm, "end": v(21.93, -12.53) * mm});
            skArc(sketch, "E222.23.14", {"start": v(21.77, -14.14) * mm, "mid": v(21.67, -14.17) * mm, "end": v(21.61, -14.26) * mm});
            skArc(sketch, "E222.23.15", {"start": v(22, -12.98) * mm, "mid": v(21.92, -12.92) * mm, "end": v(21.9, -12.82) * mm});
            skArc(sketch, "E222.24.0", {"start": v(22.4, -11) * mm, "mid": v(22.24, -10.94) * mm, "end": v(22.08, -10.9) * mm});
            skArc(sketch, "E222.24.1", {"start": v(22.7, -11.5) * mm, "mid": v(22.62, -11.2) * mm, "end": v(22.4, -11) * mm});
            skArc(sketch, "E222.24.2", {"start": v(21.32, -11.5) * mm, "mid": v(11.02, -21.31) * mm, "end": v(1.72, -10.54) * mm});
            skPoint(sketch, "E222.24.3", {"position": v(21.95, -11.5) * mm});
            skArc(sketch, "E222.24.4", {"start": v(22.4, -12) * mm, "mid": v(22.24, -12.06) * mm, "end": v(22.08, -12.1) * mm});
            skLineSegment(sketch, "E222.24.5", {"start": v(1.72, -12.46) * mm, "end": v(21.93, -10.47) * mm});
            skArc(sketch, "E222.24.6", {"start": v(21.95, -12.23) * mm, "mid": v(21.94, -12.38) * mm, "end": v(21.93, -12.53) * mm});
            skLineSegment(sketch, "E222.24.7", {"start": v(1.72, -10.54) * mm, "end": v(21.93, -12.53) * mm});
            skArc(sketch, "E222.24.8", {"start": v(22.7, -11.5) * mm, "mid": v(22.62, -11.8) * mm, "end": v(22.4, -12) * mm});
            skPoint(sketch, "E222.24.9", {"position": v(21.32, -11.5) * mm});
            skArc(sketch, "E222.24.10", {"start": v(21.7, -11.5) * mm, "mid": v(21.69, -12) * mm, "end": v(21.65, -12.5) * mm, "construction": true});
            skArc(sketch, "E222.24.11", {"start": v(21.32, -11.5) * mm, "mid": v(11.02, -1.69) * mm, "end": v(1.72, -12.46) * mm});
            skPoint(sketch, "E222.24.12", {"position": v(21.7, -11.5) * mm});
            skArc(sketch, "E222.24.13", {"start": v(21.95, -10.77) * mm, "mid": v(21.94, -10.62) * mm, "end": v(21.93, -10.47) * mm});
            skArc(sketch, "E222.24.14", {"start": v(22.08, -12.1) * mm, "mid": v(22, -12.14) * mm, "end": v(21.95, -12.23) * mm});
            skArc(sketch, "E222.24.15", {"start": v(22.08, -10.9) * mm, "mid": v(22, -10.86) * mm, "end": v(21.95, -10.77) * mm});
            skArc(sketch, "E222.25.0", {"start": v(22.09, -8.89) * mm, "mid": v(21.93, -8.86) * mm, "end": v(21.77, -8.86) * mm});
            skArc(sketch, "E222.25.1", {"start": v(22.49, -9.31) * mm, "mid": v(22.35, -9.04) * mm, "end": v(22.09, -8.89) * mm});
            skArc(sketch, "E222.25.2", {"start": v(21.14, -9.58) * mm, "mid": v(12.94, -21.22) * mm, "end": v(1.72, -12.46) * mm});
            skPoint(sketch, "E222.25.3", {"position": v(21.75, -9.46) * mm});
            skArc(sketch, "E222.25.4", {"start": v(22.28, -9.86) * mm, "mid": v(22.14, -9.95) * mm, "end": v(22, -10.02) * mm});
            skLineSegment(sketch, "E222.25.5", {"start": v(2.1, -14.35) * mm, "end": v(21.53, -8.46) * mm});
            skArc(sketch, "E222.25.6", {"start": v(21.9, -10.18) * mm, "mid": v(21.91, -10.32) * mm, "end": v(21.93, -10.47) * mm});
            skLineSegment(sketch, "E222.25.7", {"start": v(1.72, -12.46) * mm, "end": v(21.93, -10.47) * mm});
            skArc(sketch, "E222.25.8", {"start": v(22.49, -9.31) * mm, "mid": v(22.46, -9.62) * mm, "end": v(22.28, -9.86) * mm});
            skPoint(sketch, "E222.25.9", {"position": v(21.14, -9.58) * mm});
            skArc(sketch, "E222.25.10", {"start": v(21.5, -9.51) * mm, "mid": v(21.59, -10) * mm, "end": v(21.65, -10.5) * mm, "construction": true});
            skArc(sketch, "E222.25.11", {"start": v(21.14, -9.58) * mm, "mid": v(9.11, -1.97) * mm, "end": v(2.1, -14.35) * mm});
            skPoint(sketch, "E222.25.12", {"position": v(21.5, -9.51) * mm});
            skArc(sketch, "E222.25.13", {"start": v(21.61, -8.74) * mm, "mid": v(21.57, -8.6) * mm, "end": v(21.53, -8.46) * mm});
            skArc(sketch, "E222.25.14", {"start": v(22, -10.02) * mm, "mid": v(21.92, -10.08) * mm, "end": v(21.9, -10.18) * mm});
            skArc(sketch, "E222.25.15", {"start": v(21.77, -8.86) * mm, "mid": v(21.67, -8.83) * mm, "end": v(21.61, -8.74) * mm});
            skArc(sketch, "E222.26.0", {"start": v(21.37, -6.87) * mm, "mid": v(21.21, -6.87) * mm, "end": v(21.05, -6.9) * mm});
            skArc(sketch, "E222.26.1", {"start": v(21.85, -7.21) * mm, "mid": v(21.66, -6.97) * mm, "end": v(21.37, -6.87) * mm});
            skArc(sketch, "E222.26.2", {"start": v(20.58, -7.74) * mm, "mid": v(14.8, -20.75) * mm, "end": v(2.1, -14.35) * mm});
            skPoint(sketch, "E222.26.3", {"position": v(21.16, -7.5) * mm});
            skArc(sketch, "E222.26.4", {"start": v(21.75, -7.8) * mm, "mid": v(21.64, -7.9) * mm, "end": v(21.5, -8) * mm});
            skLineSegment(sketch, "E222.26.5", {"start": v(2.84, -16.13) * mm, "end": v(20.74, -6.56) * mm});
            skArc(sketch, "E222.26.6", {"start": v(21.44, -8.17) * mm, "mid": v(21.48, -8.32) * mm, "end": v(21.53, -8.46) * mm});
            skLineSegment(sketch, "E222.26.7", {"start": v(2.1, -14.35) * mm, "end": v(21.53, -8.46) * mm});
            skArc(sketch, "E222.26.8", {"start": v(21.85, -7.21) * mm, "mid": v(21.89, -7.52) * mm, "end": v(21.75, -7.8) * mm});
            skPoint(sketch, "E222.26.9", {"position": v(20.58, -7.74) * mm});
            skArc(sketch, "E222.26.10", {"start": v(20.92, -7.6) * mm, "mid": v(21.1, -8.06) * mm, "end": v(21.26, -8.54) * mm, "construction": true});
            skArc(sketch, "E222.26.11", {"start": v(20.58, -7.74) * mm, "mid": v(7.3, -2.62) * mm, "end": v(2.84, -16.13) * mm});
            skPoint(sketch, "E222.26.12", {"position": v(20.92, -7.6) * mm});
            skArc(sketch, "E222.26.13", {"start": v(20.88, -6.83) * mm, "mid": v(20.81, -6.7) * mm, "end": v(20.74, -6.56) * mm});
            skArc(sketch, "E222.26.14", {"start": v(21.5, -8) * mm, "mid": v(21.44, -8.07) * mm, "end": v(21.44, -8.17) * mm});
            skArc(sketch, "E222.26.15", {"start": v(21.05, -6.9) * mm, "mid": v(20.95, -6.9) * mm, "end": v(20.88, -6.83) * mm});
            skArc(sketch, "E222.27.0", {"start": v(20.28, -5.03) * mm, "mid": v(20.12, -5.07) * mm, "end": v(19.97, -5.13) * mm});
            skArc(sketch, "E222.27.1", {"start": v(20.82, -5.28) * mm, "mid": v(20.58, -5.08) * mm, "end": v(20.28, -5.03) * mm});
            skArc(sketch, "E222.27.2", {"start": v(19.67, -6.04) * mm, "mid": v(16.55, -19.93) * mm, "end": v(2.84, -16.13) * mm});
            skPoint(sketch, "E222.27.3", {"position": v(20.2, -5.7) * mm});
            skArc(sketch, "E222.27.4", {"start": v(20.83, -5.86) * mm, "mid": v(20.74, -6) * mm, "end": v(20.63, -6.11) * mm});
            skLineSegment(sketch, "E222.27.5", {"start": v(3.9, -17.73) * mm, "end": v(19.6, -4.85) * mm});
            skArc(sketch, "E222.27.6", {"start": v(20.6, -6.3) * mm, "mid": v(20.67, -6.43) * mm, "end": v(20.74, -6.56) * mm});
            skLineSegment(sketch, "E222.27.7", {"start": v(2.84, -16.13) * mm, "end": v(20.74, -6.56) * mm});
            skArc(sketch, "E222.27.8", {"start": v(20.82, -5.28) * mm, "mid": v(20.9, -5.57) * mm, "end": v(20.83, -5.86) * mm});
            skPoint(sketch, "E222.27.9", {"position": v(19.67, -6.04) * mm});
            skArc(sketch, "E222.27.10", {"start": v(19.98, -5.83) * mm, "mid": v(20.25, -6.26) * mm, "end": v(20.5, -6.7) * mm, "construction": true});
            skArc(sketch, "E222.27.11", {"start": v(19.67, -6.04) * mm, "mid": v(5.65, -3.6) * mm, "end": v(3.9, -17.73) * mm});
            skPoint(sketch, "E222.27.12", {"position": v(19.98, -5.83) * mm});
            skArc(sketch, "E222.27.13", {"start": v(19.79, -5.09) * mm, "mid": v(19.7, -4.97) * mm, "end": v(19.6, -4.85) * mm});
            skArc(sketch, "E222.27.14", {"start": v(20.63, -6.11) * mm, "mid": v(20.58, -6.2) * mm, "end": v(20.6, -6.3) * mm});
            skArc(sketch, "E222.27.15", {"start": v(19.97, -5.13) * mm, "mid": v(19.87, -5.14) * mm, "end": v(19.79, -5.09) * mm});
            skArc(sketch, "E222.28.0", {"start": v(18.85, -3.45) * mm, "mid": v(18.7, -3.5) * mm, "end": v(18.57, -3.6) * mm});
            skArc(sketch, "E222.28.1", {"start": v(19.42, -3.58) * mm, "mid": v(19.15, -3.43) * mm, "end": v(18.85, -3.45) * mm});
            skArc(sketch, "E222.28.2", {"start": v(18.45, -4.55) * mm, "mid": v(18.1, -18.78) * mm, "end": v(3.9, -17.73) * mm});
            skPoint(sketch, "E222.28.3", {"position": v(18.9, -4.1) * mm});
            skArc(sketch, "E222.28.4", {"start": v(19.55, -4.15) * mm, "mid": v(19.5, -4.3) * mm, "end": v(19.4, -4.43) * mm});
            skLineSegment(sketch, "E222.28.5", {"start": v(5.27, -19.1) * mm, "end": v(18.15, -3.4) * mm});
            skArc(sketch, "E222.28.6", {"start": v(19.4, -4.62) * mm, "mid": v(19.5, -4.74) * mm, "end": v(19.6, -4.85) * mm});
            skLineSegment(sketch, "E222.28.7", {"start": v(3.9, -17.73) * mm, "end": v(19.6, -4.85) * mm});
            skArc(sketch, "E222.28.8", {"start": v(19.42, -3.58) * mm, "mid": v(19.57, -3.85) * mm, "end": v(19.55, -4.15) * mm});
            skPoint(sketch, "E222.28.9", {"position": v(18.45, -4.55) * mm});
            skArc(sketch, "E222.28.10", {"start": v(18.71, -4.29) * mm, "mid": v(19.06, -4.65) * mm, "end": v(19.38, -5.03) * mm, "construction": true});
            skArc(sketch, "E222.28.11", {"start": v(18.45, -4.55) * mm, "mid": v(4.22, -4.9) * mm, "end": v(5.27, -19.1) * mm});
            skPoint(sketch, "E222.28.12", {"position": v(18.71, -4.29) * mm});
            skArc(sketch, "E222.28.13", {"start": v(18.38, -3.6) * mm, "mid": v(18.26, -3.5) * mm, "end": v(18.15, -3.4) * mm});
            skArc(sketch, "E222.28.14", {"start": v(19.4, -4.43) * mm, "mid": v(19.37, -4.53) * mm, "end": v(19.4, -4.62) * mm});
            skArc(sketch, "E222.28.15", {"start": v(18.57, -3.6) * mm, "mid": v(18.47, -3.63) * mm, "end": v(18.38, -3.6) * mm});
            skArc(sketch, "E222.29.0", {"start": v(17.14, -2.17) * mm, "mid": v(17, -2.26) * mm, "end": v(16.89, -2.37) * mm});
            skArc(sketch, "E222.29.1", {"start": v(17.72, -2.18) * mm, "mid": v(17.43, -2.1) * mm, "end": v(17.14, -2.17) * mm});
            skArc(sketch, "E222.29.2", {"start": v(16.96, -3.33) * mm, "mid": v(19.4, -17.35) * mm, "end": v(5.27, -19.1) * mm});
            skPoint(sketch, "E222.29.3", {"position": v(17.3, -2.8) * mm});
            skArc(sketch, "E222.29.4", {"start": v(17.97, -2.72) * mm, "mid": v(17.93, -2.88) * mm, "end": v(17.87, -3.03) * mm});
            skLineSegment(sketch, "E222.29.5", {"start": v(6.87, -20.16) * mm, "end": v(16.44, -2.26) * mm});
            skArc(sketch, "E222.29.6", {"start": v(17.91, -3.21) * mm, "mid": v(18.03, -3.3) * mm, "end": v(18.15, -3.4) * mm});
            skLineSegment(sketch, "E222.29.7", {"start": v(5.27, -19.1) * mm, "end": v(18.15, -3.4) * mm});
            skArc(sketch, "E222.29.8", {"start": v(17.72, -2.18) * mm, "mid": v(17.92, -2.42) * mm, "end": v(17.97, -2.72) * mm});
            skPoint(sketch, "E222.29.9", {"position": v(16.96, -3.33) * mm});
            skArc(sketch, "E222.29.10", {"start": v(17.17, -3.02) * mm, "mid": v(17.58, -3.3) * mm, "end": v(17.97, -3.62) * mm, "construction": true});
            skArc(sketch, "E222.29.11", {"start": v(16.96, -3.33) * mm, "mid": v(3.07, -6.45) * mm, "end": v(6.87, -20.16) * mm});
            skPoint(sketch, "E222.29.12", {"position": v(17.17, -3.02) * mm});
            skArc(sketch, "E222.29.13", {"start": v(16.7, -2.4) * mm, "mid": v(16.57, -2.33) * mm, "end": v(16.44, -2.26) * mm});
            skArc(sketch, "E222.29.14", {"start": v(17.87, -3.03) * mm, "mid": v(17.86, -3.13) * mm, "end": v(17.91, -3.21) * mm});
            skArc(sketch, "E222.29.15", {"start": v(16.89, -2.37) * mm, "mid": v(16.8, -2.42) * mm, "end": v(16.7, -2.4) * mm});
            skArc(sketch, "E222.30.0", {"start": v(15.2, -1.25) * mm, "mid": v(15.1, -1.36) * mm, "end": v(15, -1.5) * mm});
            skArc(sketch, "E222.30.1", {"start": v(15.79, -1.15) * mm, "mid": v(15.48, -1.11) * mm, "end": v(15.2, -1.25) * mm});
            skArc(sketch, "E222.30.2", {"start": v(15.26, -2.42) * mm, "mid": v(20.38, -15.7) * mm, "end": v(6.87, -20.16) * mm});
            skPoint(sketch, "E222.30.3", {"position": v(15.5, -1.84) * mm});
            skArc(sketch, "E222.30.4", {"start": v(16.13, -1.63) * mm, "mid": v(16.13, -1.79) * mm, "end": v(16.1, -1.95) * mm});
            skLineSegment(sketch, "E222.30.5", {"start": v(8.65, -20.9) * mm, "end": v(14.54, -1.47) * mm});
            skArc(sketch, "E222.30.6", {"start": v(16.17, -2.12) * mm, "mid": v(16.3, -2.19) * mm, "end": v(16.44, -2.26) * mm});
            skLineSegment(sketch, "E222.30.7", {"start": v(6.87, -20.16) * mm, "end": v(16.44, -2.26) * mm});
            skArc(sketch, "E222.30.8", {"start": v(15.79, -1.15) * mm, "mid": v(16.03, -1.34) * mm, "end": v(16.13, -1.63) * mm});
            skPoint(sketch, "E222.30.9", {"position": v(15.26, -2.42) * mm});
            skArc(sketch, "E222.30.10", {"start": v(15.4, -2.08) * mm, "mid": v(15.86, -2.28) * mm, "end": v(16.3, -2.5) * mm, "construction": true});
            skArc(sketch, "E222.30.11", {"start": v(15.26, -2.42) * mm, "mid": v(2.25, -8.2) * mm, "end": v(8.65, -20.9) * mm});
            skPoint(sketch, "E222.30.12", {"position": v(15.4, -2.08) * mm});
            skArc(sketch, "E222.30.13", {"start": v(14.83, -1.56) * mm, "mid": v(14.68, -1.52) * mm, "end": v(14.54, -1.47) * mm});
            skArc(sketch, "E222.30.14", {"start": v(16.1, -1.95) * mm, "mid": v(16.1, -2.05) * mm, "end": v(16.17, -2.12) * mm});
            skArc(sketch, "E222.30.15", {"start": v(15, -1.5) * mm, "mid": v(14.93, -1.56) * mm, "end": v(14.83, -1.56) * mm});
            skArc(sketch, "E222.31.0", {"start": v(13.14, -0.72) * mm, "mid": v(13.05, -0.86) * mm, "end": v(12.98, -1) * mm});
            skArc(sketch, "E222.31.1", {"start": v(13.69, -0.51) * mm, "mid": v(13.38, -0.54) * mm, "end": v(13.14, -0.72) * mm});
            skArc(sketch, "E222.31.2", {"start": v(13.42, -1.86) * mm, "mid": v(21.03, -13.89) * mm, "end": v(8.65, -20.9) * mm});
            skPoint(sketch, "E222.31.3", {"position": v(13.54, -1.25) * mm});
            skArc(sketch, "E222.31.4", {"start": v(14.11, -0.91) * mm, "mid": v(14.14, -1.07) * mm, "end": v(14.14, -1.23) * mm});
            skArc(sketch, "E222.31.6", {"start": v(14.26, -1.39) * mm, "mid": v(14.4, -1.43) * mm, "end": v(14.54, -1.47) * mm});
            skLineSegment(sketch, "E222.31.7", {"start": v(8.65, -20.9) * mm, "end": v(14.54, -1.47) * mm});
            skArc(sketch, "E222.31.8", {"start": v(13.69, -0.51) * mm, "mid": v(13.96, -0.65) * mm, "end": v(14.11, -0.91) * mm});
            skPoint(sketch, "E222.31.9", {"position": v(13.42, -1.86) * mm});
            skArc(sketch, "E222.31.10", {"start": v(13.49, -1.5) * mm, "mid": v(13.98, -1.6) * mm, "end": v(14.46, -1.74) * mm, "construction": true});
            skArc(sketch, "E222.31.11", {"start": v(13.42, -1.86) * mm, "mid": v(1.78, -10.06) * mm, "end": v(10.54, -21.28) * mm});
            skPoint(sketch, "E222.31.12", {"position": v(13.49, -1.5) * mm});
            skArc(sketch, "E222.31.13", {"start": v(12.82, -1.1) * mm, "mid": v(12.68, -1.09) * mm, "end": v(12.53, -1.07) * mm});
            skArc(sketch, "E222.31.14", {"start": v(14.14, -1.23) * mm, "mid": v(14.17, -1.33) * mm, "end": v(14.26, -1.39) * mm});
            skArc(sketch, "E222.31.15", {"start": v(12.98, -1) * mm, "mid": v(12.92, -1.08) * mm, "end": v(12.82, -1.1) * mm});
            skArc(sketch, "E223.0", {"start": v(4.25, -18.75) * mm, "mid": v(18.75, -18.75) * mm, "end": v(18.75, -4.25) * mm});
            skLineSegment(sketch, "E224", {"start": v(4.25, -18.75) * mm, "end": v(18.75, -4.25) * mm, "construction": true});
            skSolve(sketch);
        }
        {
            var Q0;
            Q0=qSketchRegion(id+"F34",true);
            extrude(context, id + "F35", {"entities" : qUnion([Q0]), "operationType" : NewBodyOperationType.REMOVE, "endBound" : BoundingType.SYMMETRIC, "oppositeDirection" : true, "depth" : 6.5 * mm});
        }
        {
            var Q0;
            {var subQ0=sQuery(id+"F0.wireOp",EDGE,"E28");var subQ1=sQuery(id+"F0.wireOp",EDGE,"E27");var subQ2=sQuery(id+"F0.wireOp",EDGE,"E26");var subQ3=sQuery(id+"F0.wireOp",EDGE,"E24");var subQ4=sQuery(id+"F0.wireOp",EDGE,"E23");Q0=makeQuery(id+"F2.boolean.opBoolean","MERGE",FACE,{"derivedFrom":[makeQuery(id+"F1.opExtrude","CAP_FACE",FACE,{"disambiguationData":[OSD([sQuery(id+"F0.wireOp",EDGE,"E0.right"),sQuery(id+"F0.wireOp",EDGE,"E4"),sQuery(id+"F0.wireOp",EDGE,"E9"),sQuery(id+"F0.wireOp",EDGE,"E11.MirrorC"),sQuery(id+"F0.wireOp",EDGE,"E13.MirrorC"),sQuery(id+"F0.wireOp",EDGE,"E14.MirrorC"),sQuery(id+"F0.wireOp",EDGE,"E15"),sQuery(id+"F0.wireOp",EDGE,"E17.MirrorC"),sQuery(id+"F0.wireOp",EDGE,"E18.MirrorC"),sQuery(id+"F0.wireOp",EDGE,"E20.MirrorC"),sQuery(id+"F0.wireOp",EDGE,"E21"),sQuery(id+"F0.wireOp",EDGE,"E22"),subQ4,subQ3,sQuery(id+"F0.wireOp",EDGE,"E25"),subQ2,subQ1,subQ0,sQuery(id+"F0.wireOp",EDGE,"E30.0"),sQuery(id+"F0.wireOp",EDGE,"E30.1"),sQuery(id+"F0.wireOp",EDGE,"E30.2")])],"isStart":true}),makeQuery(id+"F2.opExtrude","CAP_FACE",FACE,{"disambiguationData":[OSD([subQ4,subQ3,subQ2,subQ1,subQ0,sQuery(id+"F0.wireOp",EDGE,"E31"),sQuery(id+"F0.wireOp",EDGE,"E32"),sQuery(id+"F0.wireOp",EDGE,"E33"),sQuery(id+"F0.wireOp",EDGE,"E34"),sQuery(id+"F0.wireOp",EDGE,"E35"),sQuery(id+"F0.wireOp",EDGE,"E39"),sQuery(id+"F0.wireOp",EDGE,"E41"),sQuery(id+"F0.wireOp",EDGE,"E43"),sQuery(id+"F0.wireOp",EDGE,"E44"),sQuery(id+"F0.wireOp",EDGE,"E45"),sQuery(id+"F0.wireOp",EDGE,"E46")])],"isStart":true})]});}
            var Q1;
            Q1=sQuery(id+"F10.wireOp",VERTEX,"E105");
            cPlane(context, id + "F36", {"entities" : qUnion([Q0, Q1]), "cplaneType" : CPlaneType.PLANE_POINT, "offset" : 150 * mm, "width" : 150 * mm, "height" : 150 * mm});
        }
        {
            var Q0;
            Q0=qCreatedBy(id+"F36.planeOp",FACE);
            var sketch = newSketch(context, id + "F37", { "sketchPlane" : qUnion([Q0])});
            skLineSegment(sketch, "E225", {"start": v(11.5, -0.3) * mm, "end": v(11.5, -1.68) * mm, "construction": true});
            skArc(sketch, "E226", {"start": v(11.5, -0.3) * mm, "mid": v(11.8, -0.38) * mm, "end": v(12, -0.6) * mm});
            skArc(sketch, "E227", {"start": v(12, -0.6) * mm, "mid": v(12.06, -0.76) * mm, "end": v(12.1, -0.92) * mm});
            skArc(sketch, "E228", {"start": v(12.1, -0.92) * mm, "mid": v(12.14, -1) * mm, "end": v(12.23, -1.05) * mm});
            skPoint(sketch, "E229", {"position": v(11.5, -1.68) * mm});
            skPoint(sketch, "E230", {"position": v(11.5, -1.05) * mm});
            skPoint(sketch, "E231", {"position": v(11.5, -1.3) * mm});
            skArc(sketch, "E232", {"start": v(11.5, -1.3) * mm, "mid": v(12, -1.31) * mm, "end": v(12.5, -1.35) * mm, "construction": true});
            skLineSegment(sketch, "E233", {"start": v(12.46, -1.72) * mm, "end": v(12.53, -1.07) * mm});
            skArc(sketch, "E234", {"start": v(12.23, -1.05) * mm, "mid": v(12.38, -1.06) * mm, "end": v(12.53, -1.07) * mm});
            skArc(sketch, "E235", {"start": v(11.5, -1.68) * mm, "mid": v(11.98, -1.69) * mm, "end": v(12.46, -1.72) * mm});
            skArc(sketch, "E236.MirrorCS", {"start": v(11.5, -0.3) * mm, "mid": v(11.2, -0.38) * mm, "end": v(11, -0.6) * mm});
            skArc(sketch, "E237.MirrorCS", {"start": v(11, -0.6) * mm, "mid": v(10.94, -0.76) * mm, "end": v(10.9, -0.92) * mm});
            skArc(sketch, "E238.MirrorCS", {"start": v(10.9, -0.92) * mm, "mid": v(10.86, -1) * mm, "end": v(10.77, -1.05) * mm});
            skArc(sketch, "E239.MirrorCS", {"start": v(10.77, -1.05) * mm, "mid": v(10.62, -1.06) * mm, "end": v(10.47, -1.07) * mm});
            skLineSegment(sketch, "E240.MirrorCS", {"start": v(10.54, -1.72) * mm, "end": v(10.47, -1.07) * mm});
            skArc(sketch, "E241.MirrorCS", {"start": v(11.5, -1.68) * mm, "mid": v(11.02, -1.69) * mm, "end": v(10.54, -1.72) * mm});
            skArc(sketch, "E242.1.0", {"start": v(8.89, -0.91) * mm, "mid": v(8.86, -1.07) * mm, "end": v(8.86, -1.23) * mm});
            skArc(sketch, "E242.1.1", {"start": v(9.31, -0.51) * mm, "mid": v(9.04, -0.65) * mm, "end": v(8.89, -0.91) * mm});
            skArc(sketch, "E242.1.2", {"start": v(9.58, -1.86) * mm, "mid": v(10.06, -1.78) * mm, "end": v(10.54, -1.72) * mm});
            skPoint(sketch, "E242.1.3", {"position": v(9.46, -1.25) * mm});
            skArc(sketch, "E242.1.4", {"start": v(9.86, -0.72) * mm, "mid": v(9.95, -0.86) * mm, "end": v(10.02, -1) * mm});
            skLineSegment(sketch, "E242.1.5", {"start": v(8.65, -2.1) * mm, "end": v(8.46, -1.47) * mm});
            skArc(sketch, "E242.1.6", {"start": v(10.18, -1.1) * mm, "mid": v(10.32, -1.09) * mm, "end": v(10.47, -1.07) * mm});
            skArc(sketch, "E242.1.8", {"start": v(9.31, -0.51) * mm, "mid": v(9.62, -0.54) * mm, "end": v(9.86, -0.72) * mm});
            skPoint(sketch, "E242.1.9", {"position": v(9.58, -1.86) * mm});
            skArc(sketch, "E242.1.10", {"start": v(9.51, -1.5) * mm, "mid": v(10, -1.41) * mm, "end": v(10.5, -1.35) * mm, "construction": true});
            skArc(sketch, "E242.1.11", {"start": v(9.58, -1.86) * mm, "mid": v(9.11, -1.97) * mm, "end": v(8.65, -2.1) * mm});
            skPoint(sketch, "E242.1.12", {"position": v(9.51, -1.5) * mm});
            skArc(sketch, "E242.1.13", {"start": v(8.74, -1.39) * mm, "mid": v(8.6, -1.43) * mm, "end": v(8.46, -1.47) * mm});
            skArc(sketch, "E242.1.14", {"start": v(10.02, -1) * mm, "mid": v(10.08, -1.08) * mm, "end": v(10.18, -1.1) * mm});
            skArc(sketch, "E242.1.15", {"start": v(8.86, -1.23) * mm, "mid": v(8.83, -1.33) * mm, "end": v(8.74, -1.39) * mm});
            skArc(sketch, "E242.2.0", {"start": v(6.87, -1.63) * mm, "mid": v(6.87, -1.79) * mm, "end": v(6.9, -1.95) * mm});
            skArc(sketch, "E242.2.1", {"start": v(7.21, -1.15) * mm, "mid": v(6.97, -1.34) * mm, "end": v(6.87, -1.63) * mm});
            skArc(sketch, "E242.2.2", {"start": v(7.74, -2.42) * mm, "mid": v(8.2, -2.25) * mm, "end": v(8.65, -2.1) * mm});
            skPoint(sketch, "E242.2.3", {"position": v(7.5, -1.84) * mm});
            skArc(sketch, "E242.2.4", {"start": v(7.8, -1.25) * mm, "mid": v(7.9, -1.36) * mm, "end": v(8, -1.5) * mm});
            skLineSegment(sketch, "E242.2.5", {"start": v(6.87, -2.84) * mm, "end": v(6.56, -2.26) * mm});
            skArc(sketch, "E242.2.6", {"start": v(8.17, -1.56) * mm, "mid": v(8.32, -1.52) * mm, "end": v(8.46, -1.47) * mm});
            skLineSegment(sketch, "E242.2.7", {"start": v(8.65, -2.1) * mm, "end": v(8.46, -1.47) * mm});
            skArc(sketch, "E242.2.8", {"start": v(7.21, -1.15) * mm, "mid": v(7.52, -1.11) * mm, "end": v(7.8, -1.25) * mm});
            skPoint(sketch, "E242.2.9", {"position": v(7.74, -2.42) * mm});
            skArc(sketch, "E242.2.10", {"start": v(7.6, -2.08) * mm, "mid": v(8.06, -1.9) * mm, "end": v(8.54, -1.74) * mm, "construction": true});
            skArc(sketch, "E242.2.11", {"start": v(7.74, -2.42) * mm, "mid": v(7.3, -2.62) * mm, "end": v(6.87, -2.84) * mm});
            skPoint(sketch, "E242.2.12", {"position": v(7.6, -2.08) * mm});
            skArc(sketch, "E242.2.13", {"start": v(6.83, -2.12) * mm, "mid": v(6.7, -2.19) * mm, "end": v(6.56, -2.26) * mm});
            skArc(sketch, "E242.2.14", {"start": v(8, -1.5) * mm, "mid": v(8.07, -1.56) * mm, "end": v(8.17, -1.56) * mm});
            skArc(sketch, "E242.2.15", {"start": v(6.9, -1.95) * mm, "mid": v(6.9, -2.05) * mm, "end": v(6.83, -2.12) * mm});
            skArc(sketch, "E242.3.0", {"start": v(5.03, -2.72) * mm, "mid": v(5.07, -2.88) * mm, "end": v(5.13, -3.03) * mm});
            skArc(sketch, "E242.3.1", {"start": v(5.28, -2.18) * mm, "mid": v(5.08, -2.42) * mm, "end": v(5.03, -2.72) * mm});
            skArc(sketch, "E242.3.2", {"start": v(6.04, -3.33) * mm, "mid": v(6.45, -3.07) * mm, "end": v(6.87, -2.84) * mm});
            skPoint(sketch, "E242.3.3", {"position": v(5.7, -2.8) * mm});
            skArc(sketch, "E242.3.4", {"start": v(5.86, -2.17) * mm, "mid": v(6, -2.26) * mm, "end": v(6.11, -2.37) * mm});
            skLineSegment(sketch, "E242.3.5", {"start": v(5.27, -3.9) * mm, "end": v(4.85, -3.4) * mm});
            skArc(sketch, "E242.3.6", {"start": v(6.3, -2.4) * mm, "mid": v(6.43, -2.33) * mm, "end": v(6.56, -2.26) * mm});
            skLineSegment(sketch, "E242.3.7", {"start": v(6.87, -2.84) * mm, "end": v(6.56, -2.26) * mm});
            skArc(sketch, "E242.3.8", {"start": v(5.28, -2.18) * mm, "mid": v(5.57, -2.1) * mm, "end": v(5.86, -2.17) * mm});
            skPoint(sketch, "E242.3.9", {"position": v(6.04, -3.33) * mm});
            skArc(sketch, "E242.3.10", {"start": v(5.83, -3.02) * mm, "mid": v(6.26, -2.75) * mm, "end": v(6.7, -2.5) * mm, "construction": true});
            skArc(sketch, "E242.3.11", {"start": v(6.04, -3.33) * mm, "mid": v(5.65, -3.6) * mm, "end": v(5.27, -3.9) * mm});
            skPoint(sketch, "E242.3.12", {"position": v(5.83, -3.02) * mm});
            skArc(sketch, "E242.3.13", {"start": v(5.09, -3.21) * mm, "mid": v(4.97, -3.3) * mm, "end": v(4.85, -3.4) * mm});
            skArc(sketch, "E242.3.14", {"start": v(6.11, -2.37) * mm, "mid": v(6.2, -2.42) * mm, "end": v(6.3, -2.4) * mm});
            skArc(sketch, "E242.3.15", {"start": v(5.13, -3.03) * mm, "mid": v(5.14, -3.13) * mm, "end": v(5.09, -3.21) * mm});
            skArc(sketch, "E242.4.0", {"start": v(3.45, -4.15) * mm, "mid": v(3.5, -4.3) * mm, "end": v(3.6, -4.43) * mm});
            skArc(sketch, "E242.4.1", {"start": v(3.58, -3.58) * mm, "mid": v(3.43, -3.85) * mm, "end": v(3.45, -4.15) * mm});
            skArc(sketch, "E242.4.2", {"start": v(4.55, -4.55) * mm, "mid": v(4.9, -4.22) * mm, "end": v(5.27, -3.9) * mm});
            skPoint(sketch, "E242.4.3", {"position": v(4.1, -4.1) * mm});
            skArc(sketch, "E242.4.4", {"start": v(4.15, -3.45) * mm, "mid": v(4.3, -3.5) * mm, "end": v(4.43, -3.6) * mm});
            skLineSegment(sketch, "E242.4.5", {"start": v(3.9, -5.27) * mm, "end": v(3.4, -4.85) * mm});
            skArc(sketch, "E242.4.6", {"start": v(4.62, -3.6) * mm, "mid": v(4.74, -3.5) * mm, "end": v(4.85, -3.4) * mm});
            skLineSegment(sketch, "E242.4.7", {"start": v(5.27, -3.9) * mm, "end": v(4.85, -3.4) * mm});
            skArc(sketch, "E242.4.8", {"start": v(3.58, -3.58) * mm, "mid": v(3.85, -3.43) * mm, "end": v(4.15, -3.45) * mm});
            skPoint(sketch, "E242.4.9", {"position": v(4.55, -4.55) * mm});
            skArc(sketch, "E242.4.10", {"start": v(4.29, -4.29) * mm, "mid": v(4.65, -3.94) * mm, "end": v(5.03, -3.62) * mm, "construction": true});
            skArc(sketch, "E242.4.11", {"start": v(4.55, -4.55) * mm, "mid": v(4.22, -4.9) * mm, "end": v(3.9, -5.27) * mm});
            skPoint(sketch, "E242.4.12", {"position": v(4.29, -4.29) * mm});
            skArc(sketch, "E242.4.13", {"start": v(3.6, -4.62) * mm, "mid": v(3.5, -4.74) * mm, "end": v(3.4, -4.85) * mm});
            skArc(sketch, "E242.4.14", {"start": v(4.43, -3.6) * mm, "mid": v(4.53, -3.63) * mm, "end": v(4.62, -3.6) * mm});
            skArc(sketch, "E242.4.15", {"start": v(3.6, -4.43) * mm, "mid": v(3.63, -4.53) * mm, "end": v(3.6, -4.62) * mm});
            skArc(sketch, "E242.5.0", {"start": v(2.17, -5.86) * mm, "mid": v(2.26, -6) * mm, "end": v(2.37, -6.11) * mm});
            skArc(sketch, "E242.5.1", {"start": v(2.18, -5.28) * mm, "mid": v(2.1, -5.57) * mm, "end": v(2.17, -5.86) * mm});
            skArc(sketch, "E242.5.2", {"start": v(3.33, -6.04) * mm, "mid": v(3.6, -5.65) * mm, "end": v(3.9, -5.27) * mm});
            skPoint(sketch, "E242.5.3", {"position": v(2.8, -5.7) * mm});
            skArc(sketch, "E242.5.4", {"start": v(2.72, -5.03) * mm, "mid": v(2.88, -5.07) * mm, "end": v(3.03, -5.13) * mm});
            skLineSegment(sketch, "E242.5.5", {"start": v(2.84, -6.87) * mm, "end": v(2.26, -6.56) * mm});
            skArc(sketch, "E242.5.6", {"start": v(3.21, -5.09) * mm, "mid": v(3.3, -4.97) * mm, "end": v(3.4, -4.85) * mm});
            skLineSegment(sketch, "E242.5.7", {"start": v(3.9, -5.27) * mm, "end": v(3.4, -4.85) * mm});
            skArc(sketch, "E242.5.8", {"start": v(2.18, -5.28) * mm, "mid": v(2.42, -5.08) * mm, "end": v(2.72, -5.03) * mm});
            skPoint(sketch, "E242.5.9", {"position": v(3.33, -6.04) * mm});
            skArc(sketch, "E242.5.10", {"start": v(3.02, -5.83) * mm, "mid": v(3.3, -5.42) * mm, "end": v(3.62, -5.03) * mm, "construction": true});
            skArc(sketch, "E242.5.11", {"start": v(3.33, -6.04) * mm, "mid": v(3.07, -6.45) * mm, "end": v(2.84, -6.87) * mm});
            skPoint(sketch, "E242.5.12", {"position": v(3.02, -5.83) * mm});
            skArc(sketch, "E242.5.13", {"start": v(2.4, -6.3) * mm, "mid": v(2.33, -6.43) * mm, "end": v(2.26, -6.56) * mm});
            skArc(sketch, "E242.5.14", {"start": v(3.03, -5.13) * mm, "mid": v(3.13, -5.14) * mm, "end": v(3.21, -5.09) * mm});
            skArc(sketch, "E242.5.15", {"start": v(2.37, -6.11) * mm, "mid": v(2.42, -6.2) * mm, "end": v(2.4, -6.3) * mm});
            skArc(sketch, "E242.6.0", {"start": v(1.25, -7.8) * mm, "mid": v(1.36, -7.9) * mm, "end": v(1.5, -8) * mm});
            skArc(sketch, "E242.6.1", {"start": v(1.15, -7.21) * mm, "mid": v(1.11, -7.52) * mm, "end": v(1.25, -7.8) * mm});
            skArc(sketch, "E242.6.2", {"start": v(2.42, -7.74) * mm, "mid": v(2.62, -7.3) * mm, "end": v(2.84, -6.87) * mm});
            skPoint(sketch, "E242.6.3", {"position": v(1.84, -7.5) * mm});
            skArc(sketch, "E242.6.4", {"start": v(1.63, -6.87) * mm, "mid": v(1.79, -6.87) * mm, "end": v(1.95, -6.9) * mm});
            skLineSegment(sketch, "E242.6.5", {"start": v(2.1, -8.65) * mm, "end": v(1.47, -8.46) * mm});
            skArc(sketch, "E242.6.6", {"start": v(2.12, -6.83) * mm, "mid": v(2.19, -6.7) * mm, "end": v(2.26, -6.56) * mm});
            skLineSegment(sketch, "E242.6.7", {"start": v(2.84, -6.87) * mm, "end": v(2.26, -6.56) * mm});
            skArc(sketch, "E242.6.8", {"start": v(1.15, -7.21) * mm, "mid": v(1.34, -6.97) * mm, "end": v(1.63, -6.87) * mm});
            skPoint(sketch, "E242.6.9", {"position": v(2.42, -7.74) * mm});
            skArc(sketch, "E242.6.10", {"start": v(2.08, -7.6) * mm, "mid": v(2.28, -7.14) * mm, "end": v(2.5, -6.7) * mm, "construction": true});
            skArc(sketch, "E242.6.11", {"start": v(2.42, -7.74) * mm, "mid": v(2.25, -8.2) * mm, "end": v(2.1, -8.65) * mm});
            skPoint(sketch, "E242.6.12", {"position": v(2.08, -7.6) * mm});
            skArc(sketch, "E242.6.13", {"start": v(1.56, -8.17) * mm, "mid": v(1.52, -8.32) * mm, "end": v(1.47, -8.46) * mm});
            skArc(sketch, "E242.6.14", {"start": v(1.95, -6.9) * mm, "mid": v(2.05, -6.9) * mm, "end": v(2.12, -6.83) * mm});
            skArc(sketch, "E242.6.15", {"start": v(1.5, -8) * mm, "mid": v(1.56, -8.07) * mm, "end": v(1.56, -8.17) * mm});
            skArc(sketch, "E242.7.0", {"start": v(0.72, -9.86) * mm, "mid": v(0.86, -9.95) * mm, "end": v(1, -10.02) * mm});
            skArc(sketch, "E242.7.1", {"start": v(0.51, -9.31) * mm, "mid": v(0.54, -9.62) * mm, "end": v(0.72, -9.86) * mm});
            skArc(sketch, "E242.7.2", {"start": v(1.86, -9.58) * mm, "mid": v(1.97, -9.11) * mm, "end": v(2.1, -8.65) * mm});
            skPoint(sketch, "E242.7.3", {"position": v(1.25, -9.46) * mm});
            skArc(sketch, "E242.7.4", {"start": v(0.91, -8.89) * mm, "mid": v(1.07, -8.86) * mm, "end": v(1.23, -8.86) * mm});
            skLineSegment(sketch, "E242.7.5", {"start": v(1.72, -10.54) * mm, "end": v(1.07, -10.47) * mm});
            skArc(sketch, "E242.7.6", {"start": v(1.39, -8.74) * mm, "mid": v(1.43, -8.6) * mm, "end": v(1.47, -8.46) * mm});
            skLineSegment(sketch, "E242.7.7", {"start": v(2.1, -8.65) * mm, "end": v(1.47, -8.46) * mm});
            skArc(sketch, "E242.7.8", {"start": v(0.51, -9.31) * mm, "mid": v(0.65, -9.04) * mm, "end": v(0.91, -8.89) * mm});
            skPoint(sketch, "E242.7.9", {"position": v(1.86, -9.58) * mm});
            skArc(sketch, "E242.7.10", {"start": v(1.5, -9.51) * mm, "mid": v(1.6, -9.02) * mm, "end": v(1.74, -8.54) * mm, "construction": true});
            skArc(sketch, "E242.7.11", {"start": v(1.86, -9.58) * mm, "mid": v(1.78, -10.06) * mm, "end": v(1.72, -10.54) * mm});
            skPoint(sketch, "E242.7.12", {"position": v(1.5, -9.51) * mm});
            skArc(sketch, "E242.7.13", {"start": v(1.1, -10.18) * mm, "mid": v(1.09, -10.32) * mm, "end": v(1.07, -10.47) * mm});
            skArc(sketch, "E242.7.14", {"start": v(1.23, -8.86) * mm, "mid": v(1.33, -8.83) * mm, "end": v(1.39, -8.74) * mm});
            skArc(sketch, "E242.7.15", {"start": v(1, -10.02) * mm, "mid": v(1.08, -10.08) * mm, "end": v(1.1, -10.18) * mm});
            skArc(sketch, "E242.8.0", {"start": v(0.6, -12) * mm, "mid": v(0.76, -12.06) * mm, "end": v(0.92, -12.1) * mm});
            skArc(sketch, "E242.8.1", {"start": v(0.3, -11.5) * mm, "mid": v(0.38, -11.8) * mm, "end": v(0.6, -12) * mm});
            skArc(sketch, "E242.8.2", {"start": v(1.68, -11.5) * mm, "mid": v(1.69, -11.02) * mm, "end": v(1.72, -10.54) * mm});
            skPoint(sketch, "E242.8.3", {"position": v(1.05, -11.5) * mm});
            skArc(sketch, "E242.8.4", {"start": v(0.6, -11) * mm, "mid": v(0.76, -10.94) * mm, "end": v(0.92, -10.9) * mm});
            skLineSegment(sketch, "E242.8.5", {"start": v(1.72, -12.46) * mm, "end": v(1.07, -12.53) * mm});
            skArc(sketch, "E242.8.6", {"start": v(1.05, -10.77) * mm, "mid": v(1.06, -10.62) * mm, "end": v(1.07, -10.47) * mm});
            skLineSegment(sketch, "E242.8.7", {"start": v(1.72, -10.54) * mm, "end": v(1.07, -10.47) * mm});
            skArc(sketch, "E242.8.8", {"start": v(0.3, -11.5) * mm, "mid": v(0.38, -11.2) * mm, "end": v(0.6, -11) * mm});
            skPoint(sketch, "E242.8.9", {"position": v(1.68, -11.5) * mm});
            skArc(sketch, "E242.8.10", {"start": v(1.3, -11.5) * mm, "mid": v(1.31, -11) * mm, "end": v(1.35, -10.5) * mm, "construction": true});
            skArc(sketch, "E242.8.11", {"start": v(1.68, -11.5) * mm, "mid": v(1.69, -11.98) * mm, "end": v(1.72, -12.46) * mm});
            skPoint(sketch, "E242.8.12", {"position": v(1.3, -11.5) * mm});
            skArc(sketch, "E242.8.13", {"start": v(1.05, -12.23) * mm, "mid": v(1.06, -12.38) * mm, "end": v(1.07, -12.53) * mm});
            skArc(sketch, "E242.8.14", {"start": v(0.92, -10.9) * mm, "mid": v(1, -10.86) * mm, "end": v(1.05, -10.77) * mm});
            skArc(sketch, "E242.8.15", {"start": v(0.92, -12.1) * mm, "mid": v(1, -12.14) * mm, "end": v(1.05, -12.23) * mm});
            skArc(sketch, "E242.9.0", {"start": v(0.91, -14.11) * mm, "mid": v(1.07, -14.14) * mm, "end": v(1.23, -14.14) * mm});
            skArc(sketch, "E242.9.1", {"start": v(0.51, -13.69) * mm, "mid": v(0.65, -13.96) * mm, "end": v(0.91, -14.11) * mm});
            skArc(sketch, "E242.9.2", {"start": v(1.86, -13.42) * mm, "mid": v(1.78, -12.94) * mm, "end": v(1.72, -12.46) * mm});
            skPoint(sketch, "E242.9.3", {"position": v(1.25, -13.54) * mm});
            skArc(sketch, "E242.9.4", {"start": v(0.72, -13.14) * mm, "mid": v(0.86, -13.05) * mm, "end": v(1, -12.98) * mm});
            skLineSegment(sketch, "E242.9.5", {"start": v(2.1, -14.35) * mm, "end": v(1.47, -14.54) * mm});
            skArc(sketch, "E242.9.6", {"start": v(1.1, -12.82) * mm, "mid": v(1.09, -12.68) * mm, "end": v(1.07, -12.53) * mm});
            skLineSegment(sketch, "E242.9.7", {"start": v(1.72, -12.46) * mm, "end": v(1.07, -12.53) * mm});
            skArc(sketch, "E242.9.8", {"start": v(0.51, -13.69) * mm, "mid": v(0.54, -13.38) * mm, "end": v(0.72, -13.14) * mm});
            skPoint(sketch, "E242.9.9", {"position": v(1.86, -13.42) * mm});
            skArc(sketch, "E242.9.10", {"start": v(1.5, -13.49) * mm, "mid": v(1.41, -13) * mm, "end": v(1.35, -12.5) * mm, "construction": true});
            skArc(sketch, "E242.9.11", {"start": v(1.86, -13.42) * mm, "mid": v(1.97, -13.89) * mm, "end": v(2.1, -14.35) * mm});
            skPoint(sketch, "E242.9.12", {"position": v(1.5, -13.49) * mm});
            skArc(sketch, "E242.9.13", {"start": v(1.39, -14.26) * mm, "mid": v(1.43, -14.4) * mm, "end": v(1.47, -14.54) * mm});
            skArc(sketch, "E242.9.14", {"start": v(1, -12.98) * mm, "mid": v(1.08, -12.92) * mm, "end": v(1.1, -12.82) * mm});
            skArc(sketch, "E242.9.15", {"start": v(1.23, -14.14) * mm, "mid": v(1.33, -14.17) * mm, "end": v(1.39, -14.26) * mm});
            skArc(sketch, "E242.10.0", {"start": v(1.63, -16.13) * mm, "mid": v(1.79, -16.13) * mm, "end": v(1.95, -16.1) * mm});
            skArc(sketch, "E242.10.1", {"start": v(1.15, -15.79) * mm, "mid": v(1.34, -16.03) * mm, "end": v(1.63, -16.13) * mm});
            skArc(sketch, "E242.10.2", {"start": v(2.42, -15.26) * mm, "mid": v(2.25, -14.8) * mm, "end": v(2.1, -14.35) * mm});
            skPoint(sketch, "E242.10.3", {"position": v(1.84, -15.5) * mm});
            skArc(sketch, "E242.10.4", {"start": v(1.25, -15.2) * mm, "mid": v(1.36, -15.1) * mm, "end": v(1.5, -15) * mm});
            skLineSegment(sketch, "E242.10.5", {"start": v(2.84, -16.13) * mm, "end": v(2.26, -16.44) * mm});
            skArc(sketch, "E242.10.6", {"start": v(1.56, -14.83) * mm, "mid": v(1.52, -14.68) * mm, "end": v(1.47, -14.54) * mm});
            skLineSegment(sketch, "E242.10.7", {"start": v(2.1, -14.35) * mm, "end": v(1.47, -14.54) * mm});
            skArc(sketch, "E242.10.8", {"start": v(1.15, -15.79) * mm, "mid": v(1.11, -15.48) * mm, "end": v(1.25, -15.2) * mm});
            skPoint(sketch, "E242.10.9", {"position": v(2.42, -15.26) * mm});
            skArc(sketch, "E242.10.10", {"start": v(2.08, -15.4) * mm, "mid": v(1.9, -14.94) * mm, "end": v(1.74, -14.46) * mm, "construction": true});
            skArc(sketch, "E242.10.11", {"start": v(2.42, -15.26) * mm, "mid": v(2.62, -15.7) * mm, "end": v(2.84, -16.13) * mm});
            skPoint(sketch, "E242.10.12", {"position": v(2.08, -15.4) * mm});
            skArc(sketch, "E242.10.13", {"start": v(2.12, -16.17) * mm, "mid": v(2.19, -16.3) * mm, "end": v(2.26, -16.44) * mm});
            skArc(sketch, "E242.10.14", {"start": v(1.5, -15) * mm, "mid": v(1.56, -14.93) * mm, "end": v(1.56, -14.83) * mm});
            skArc(sketch, "E242.10.15", {"start": v(1.95, -16.1) * mm, "mid": v(2.05, -16.1) * mm, "end": v(2.12, -16.17) * mm});
            skArc(sketch, "E242.11.0", {"start": v(2.72, -17.97) * mm, "mid": v(2.88, -17.93) * mm, "end": v(3.03, -17.87) * mm});
            skArc(sketch, "E242.11.1", {"start": v(2.18, -17.72) * mm, "mid": v(2.42, -17.92) * mm, "end": v(2.72, -17.97) * mm});
            skArc(sketch, "E242.11.2", {"start": v(3.33, -16.96) * mm, "mid": v(3.07, -16.55) * mm, "end": v(2.84, -16.13) * mm});
            skPoint(sketch, "E242.11.3", {"position": v(2.8, -17.3) * mm});
            skArc(sketch, "E242.11.4", {"start": v(2.17, -17.14) * mm, "mid": v(2.26, -17) * mm, "end": v(2.37, -16.89) * mm});
            skLineSegment(sketch, "E242.11.5", {"start": v(3.9, -17.73) * mm, "end": v(3.4, -18.15) * mm});
            skArc(sketch, "E242.11.6", {"start": v(2.4, -16.7) * mm, "mid": v(2.33, -16.57) * mm, "end": v(2.26, -16.44) * mm});
            skLineSegment(sketch, "E242.11.7", {"start": v(2.84, -16.13) * mm, "end": v(2.26, -16.44) * mm});
            skArc(sketch, "E242.11.8", {"start": v(2.18, -17.72) * mm, "mid": v(2.1, -17.43) * mm, "end": v(2.17, -17.14) * mm});
            skPoint(sketch, "E242.11.9", {"position": v(3.33, -16.96) * mm});
            skArc(sketch, "E242.11.10", {"start": v(3.02, -17.17) * mm, "mid": v(2.75, -16.74) * mm, "end": v(2.5, -16.3) * mm, "construction": true});
            skArc(sketch, "E242.11.11", {"start": v(3.33, -16.96) * mm, "mid": v(3.6, -17.35) * mm, "end": v(3.9, -17.73) * mm});
            skPoint(sketch, "E242.11.12", {"position": v(3.02, -17.17) * mm});
            skArc(sketch, "E242.11.13", {"start": v(3.21, -17.91) * mm, "mid": v(3.3, -18.03) * mm, "end": v(3.4, -18.15) * mm});
            skArc(sketch, "E242.11.14", {"start": v(2.37, -16.89) * mm, "mid": v(2.42, -16.8) * mm, "end": v(2.4, -16.7) * mm});
            skArc(sketch, "E242.11.15", {"start": v(3.03, -17.87) * mm, "mid": v(3.13, -17.86) * mm, "end": v(3.21, -17.91) * mm});
            skArc(sketch, "E242.12.0", {"start": v(4.15, -19.55) * mm, "mid": v(4.3, -19.5) * mm, "end": v(4.43, -19.4) * mm});
            skArc(sketch, "E242.12.1", {"start": v(3.58, -19.42) * mm, "mid": v(3.85, -19.57) * mm, "end": v(4.15, -19.55) * mm});
            skArc(sketch, "E242.12.2", {"start": v(4.55, -18.45) * mm, "mid": v(4.22, -18.1) * mm, "end": v(3.9, -17.73) * mm});
            skPoint(sketch, "E242.12.3", {"position": v(4.1, -18.9) * mm});
            skArc(sketch, "E242.12.4", {"start": v(3.45, -18.85) * mm, "mid": v(3.5, -18.7) * mm, "end": v(3.6, -18.57) * mm});
            skLineSegment(sketch, "E242.12.5", {"start": v(5.27, -19.1) * mm, "end": v(4.85, -19.6) * mm});
            skArc(sketch, "E242.12.6", {"start": v(3.6, -18.38) * mm, "mid": v(3.5, -18.26) * mm, "end": v(3.4, -18.15) * mm});
            skLineSegment(sketch, "E242.12.7", {"start": v(3.9, -17.73) * mm, "end": v(3.4, -18.15) * mm});
            skArc(sketch, "E242.12.8", {"start": v(3.58, -19.42) * mm, "mid": v(3.43, -19.15) * mm, "end": v(3.45, -18.85) * mm});
            skPoint(sketch, "E242.12.9", {"position": v(4.55, -18.45) * mm});
            skArc(sketch, "E242.12.10", {"start": v(4.29, -18.71) * mm, "mid": v(3.94, -18.35) * mm, "end": v(3.62, -17.97) * mm, "construction": true});
            skArc(sketch, "E242.12.11", {"start": v(4.55, -18.45) * mm, "mid": v(4.9, -18.78) * mm, "end": v(5.27, -19.1) * mm});
            skPoint(sketch, "E242.12.12", {"position": v(4.29, -18.71) * mm});
            skArc(sketch, "E242.12.13", {"start": v(4.62, -19.4) * mm, "mid": v(4.74, -19.5) * mm, "end": v(4.85, -19.6) * mm});
            skArc(sketch, "E242.12.14", {"start": v(3.6, -18.57) * mm, "mid": v(3.63, -18.47) * mm, "end": v(3.6, -18.38) * mm});
            skArc(sketch, "E242.12.15", {"start": v(4.43, -19.4) * mm, "mid": v(4.53, -19.37) * mm, "end": v(4.62, -19.4) * mm});
            skArc(sketch, "E242.13.0", {"start": v(5.86, -20.83) * mm, "mid": v(6, -20.74) * mm, "end": v(6.11, -20.63) * mm});
            skArc(sketch, "E242.13.1", {"start": v(5.28, -20.82) * mm, "mid": v(5.57, -20.9) * mm, "end": v(5.86, -20.83) * mm});
            skArc(sketch, "E242.13.2", {"start": v(6.04, -19.67) * mm, "mid": v(5.65, -19.4) * mm, "end": v(5.27, -19.1) * mm});
            skPoint(sketch, "E242.13.3", {"position": v(5.7, -20.2) * mm});
            skArc(sketch, "E242.13.4", {"start": v(5.03, -20.28) * mm, "mid": v(5.07, -20.12) * mm, "end": v(5.13, -19.97) * mm});
            skLineSegment(sketch, "E242.13.5", {"start": v(6.87, -20.16) * mm, "end": v(6.56, -20.74) * mm});
            skArc(sketch, "E242.13.6", {"start": v(5.09, -19.79) * mm, "mid": v(4.97, -19.7) * mm, "end": v(4.85, -19.6) * mm});
            skLineSegment(sketch, "E242.13.7", {"start": v(5.27, -19.1) * mm, "end": v(4.85, -19.6) * mm});
            skArc(sketch, "E242.13.8", {"start": v(5.28, -20.82) * mm, "mid": v(5.08, -20.58) * mm, "end": v(5.03, -20.28) * mm});
            skPoint(sketch, "E242.13.9", {"position": v(6.04, -19.67) * mm});
            skArc(sketch, "E242.13.10", {"start": v(5.83, -19.98) * mm, "mid": v(5.42, -19.7) * mm, "end": v(5.03, -19.38) * mm, "construction": true});
            skArc(sketch, "E242.13.11", {"start": v(6.04, -19.67) * mm, "mid": v(6.45, -19.93) * mm, "end": v(6.87, -20.16) * mm});
            skPoint(sketch, "E242.13.12", {"position": v(5.83, -19.98) * mm});
            skArc(sketch, "E242.13.13", {"start": v(6.3, -20.6) * mm, "mid": v(6.43, -20.67) * mm, "end": v(6.56, -20.74) * mm});
            skArc(sketch, "E242.13.14", {"start": v(5.13, -19.97) * mm, "mid": v(5.14, -19.87) * mm, "end": v(5.09, -19.79) * mm});
            skArc(sketch, "E242.13.15", {"start": v(6.11, -20.63) * mm, "mid": v(6.2, -20.58) * mm, "end": v(6.3, -20.6) * mm});
            skArc(sketch, "E242.14.0", {"start": v(7.8, -21.75) * mm, "mid": v(7.9, -21.64) * mm, "end": v(8, -21.5) * mm});
            skArc(sketch, "E242.14.1", {"start": v(7.21, -21.85) * mm, "mid": v(7.52, -21.89) * mm, "end": v(7.8, -21.75) * mm});
            skArc(sketch, "E242.14.2", {"start": v(7.74, -20.58) * mm, "mid": v(7.3, -20.38) * mm, "end": v(6.87, -20.16) * mm});
            skPoint(sketch, "E242.14.3", {"position": v(7.5, -21.16) * mm});
            skArc(sketch, "E242.14.4", {"start": v(6.87, -21.37) * mm, "mid": v(6.87, -21.21) * mm, "end": v(6.9, -21.05) * mm});
            skLineSegment(sketch, "E242.14.5", {"start": v(8.65, -20.9) * mm, "end": v(8.46, -21.53) * mm});
            skArc(sketch, "E242.14.6", {"start": v(6.83, -20.88) * mm, "mid": v(6.7, -20.81) * mm, "end": v(6.56, -20.74) * mm});
            skLineSegment(sketch, "E242.14.7", {"start": v(6.87, -20.16) * mm, "end": v(6.56, -20.74) * mm});
            skArc(sketch, "E242.14.8", {"start": v(7.21, -21.85) * mm, "mid": v(6.97, -21.66) * mm, "end": v(6.87, -21.37) * mm});
            skPoint(sketch, "E242.14.9", {"position": v(7.74, -20.58) * mm});
            skArc(sketch, "E242.14.10", {"start": v(7.6, -20.92) * mm, "mid": v(7.14, -20.72) * mm, "end": v(6.7, -20.5) * mm, "construction": true});
            skArc(sketch, "E242.14.11", {"start": v(7.74, -20.58) * mm, "mid": v(8.2, -20.75) * mm, "end": v(8.65, -20.9) * mm});
            skPoint(sketch, "E242.14.12", {"position": v(7.6, -20.92) * mm});
            skArc(sketch, "E242.14.13", {"start": v(8.17, -21.44) * mm, "mid": v(8.32, -21.48) * mm, "end": v(8.46, -21.53) * mm});
            skArc(sketch, "E242.14.14", {"start": v(6.9, -21.05) * mm, "mid": v(6.9, -20.95) * mm, "end": v(6.83, -20.88) * mm});
            skArc(sketch, "E242.14.15", {"start": v(8, -21.5) * mm, "mid": v(8.07, -21.44) * mm, "end": v(8.17, -21.44) * mm});
            skArc(sketch, "E242.15.0", {"start": v(9.86, -22.28) * mm, "mid": v(9.95, -22.14) * mm, "end": v(10.02, -22) * mm});
            skArc(sketch, "E242.15.1", {"start": v(9.31, -22.49) * mm, "mid": v(9.62, -22.46) * mm, "end": v(9.86, -22.28) * mm});
            skArc(sketch, "E242.15.2", {"start": v(9.58, -21.14) * mm, "mid": v(9.11, -21.03) * mm, "end": v(8.65, -20.9) * mm});
            skPoint(sketch, "E242.15.3", {"position": v(9.46, -21.75) * mm});
            skArc(sketch, "E242.15.4", {"start": v(8.89, -22.09) * mm, "mid": v(8.86, -21.93) * mm, "end": v(8.86, -21.77) * mm});
            skLineSegment(sketch, "E242.15.5", {"start": v(10.54, -21.28) * mm, "end": v(10.47, -21.93) * mm});
            skArc(sketch, "E242.15.6", {"start": v(8.74, -21.61) * mm, "mid": v(8.6, -21.57) * mm, "end": v(8.46, -21.53) * mm});
            skLineSegment(sketch, "E242.15.7", {"start": v(8.65, -20.9) * mm, "end": v(8.46, -21.53) * mm});
            skArc(sketch, "E242.15.8", {"start": v(9.31, -22.49) * mm, "mid": v(9.04, -22.35) * mm, "end": v(8.89, -22.09) * mm});
            skPoint(sketch, "E242.15.9", {"position": v(9.58, -21.14) * mm});
            skArc(sketch, "E242.15.10", {"start": v(9.51, -21.5) * mm, "mid": v(9.02, -21.4) * mm, "end": v(8.54, -21.26) * mm, "construction": true});
            skArc(sketch, "E242.15.11", {"start": v(9.58, -21.14) * mm, "mid": v(10.06, -21.22) * mm, "end": v(10.54, -21.28) * mm});
            skPoint(sketch, "E242.15.12", {"position": v(9.51, -21.5) * mm});
            skArc(sketch, "E242.15.13", {"start": v(10.18, -21.9) * mm, "mid": v(10.32, -21.91) * mm, "end": v(10.47, -21.93) * mm});
            skArc(sketch, "E242.15.14", {"start": v(8.86, -21.77) * mm, "mid": v(8.83, -21.67) * mm, "end": v(8.74, -21.61) * mm});
            skArc(sketch, "E242.15.15", {"start": v(10.02, -22) * mm, "mid": v(10.08, -21.92) * mm, "end": v(10.18, -21.9) * mm});
            skArc(sketch, "E242.16.0", {"start": v(12, -22.4) * mm, "mid": v(12.06, -22.24) * mm, "end": v(12.1, -22.08) * mm});
            skArc(sketch, "E242.16.1", {"start": v(11.5, -22.7) * mm, "mid": v(11.8, -22.62) * mm, "end": v(12, -22.4) * mm});
            skArc(sketch, "E242.16.2", {"start": v(11.5, -21.32) * mm, "mid": v(11.02, -21.31) * mm, "end": v(10.54, -21.28) * mm});
            skPoint(sketch, "E242.16.3", {"position": v(11.5, -21.95) * mm});
            skArc(sketch, "E242.16.4", {"start": v(11, -22.4) * mm, "mid": v(10.94, -22.24) * mm, "end": v(10.9, -22.08) * mm});
            skLineSegment(sketch, "E242.16.5", {"start": v(12.46, -21.28) * mm, "end": v(12.53, -21.93) * mm});
            skArc(sketch, "E242.16.6", {"start": v(10.77, -21.95) * mm, "mid": v(10.62, -21.94) * mm, "end": v(10.47, -21.93) * mm});
            skLineSegment(sketch, "E242.16.7", {"start": v(10.54, -21.28) * mm, "end": v(10.47, -21.93) * mm});
            skArc(sketch, "E242.16.8", {"start": v(11.5, -22.7) * mm, "mid": v(11.2, -22.62) * mm, "end": v(11, -22.4) * mm});
            skPoint(sketch, "E242.16.9", {"position": v(11.5, -21.32) * mm});
            skArc(sketch, "E242.16.10", {"start": v(11.5, -21.7) * mm, "mid": v(11, -21.69) * mm, "end": v(10.5, -21.65) * mm, "construction": true});
            skArc(sketch, "E242.16.11", {"start": v(11.5, -21.32) * mm, "mid": v(11.98, -21.31) * mm, "end": v(12.46, -21.28) * mm});
            skPoint(sketch, "E242.16.12", {"position": v(11.5, -21.7) * mm});
            skArc(sketch, "E242.16.13", {"start": v(12.23, -21.95) * mm, "mid": v(12.38, -21.94) * mm, "end": v(12.53, -21.93) * mm});
            skArc(sketch, "E242.16.14", {"start": v(10.9, -22.08) * mm, "mid": v(10.86, -22) * mm, "end": v(10.77, -21.95) * mm});
            skArc(sketch, "E242.16.15", {"start": v(12.1, -22.08) * mm, "mid": v(12.14, -22) * mm, "end": v(12.23, -21.95) * mm});
            skArc(sketch, "E242.17.0", {"start": v(14.11, -22.09) * mm, "mid": v(14.14, -21.93) * mm, "end": v(14.14, -21.77) * mm});
            skArc(sketch, "E242.17.1", {"start": v(13.69, -22.49) * mm, "mid": v(13.96, -22.35) * mm, "end": v(14.11, -22.09) * mm});
            skArc(sketch, "E242.17.2", {"start": v(13.42, -21.14) * mm, "mid": v(12.94, -21.22) * mm, "end": v(12.46, -21.28) * mm});
            skPoint(sketch, "E242.17.3", {"position": v(13.54, -21.75) * mm});
            skArc(sketch, "E242.17.4", {"start": v(13.14, -22.28) * mm, "mid": v(13.05, -22.14) * mm, "end": v(12.98, -22) * mm});
            skLineSegment(sketch, "E242.17.5", {"start": v(14.35, -20.9) * mm, "end": v(14.54, -21.53) * mm});
            skArc(sketch, "E242.17.6", {"start": v(12.82, -21.9) * mm, "mid": v(12.68, -21.91) * mm, "end": v(12.53, -21.93) * mm});
            skLineSegment(sketch, "E242.17.7", {"start": v(12.46, -21.28) * mm, "end": v(12.53, -21.93) * mm});
            skArc(sketch, "E242.17.8", {"start": v(13.69, -22.49) * mm, "mid": v(13.38, -22.46) * mm, "end": v(13.14, -22.28) * mm});
            skPoint(sketch, "E242.17.9", {"position": v(13.42, -21.14) * mm});
            skArc(sketch, "E242.17.10", {"start": v(13.49, -21.5) * mm, "mid": v(13, -21.59) * mm, "end": v(12.5, -21.65) * mm, "construction": true});
            skArc(sketch, "E242.17.11", {"start": v(13.42, -21.14) * mm, "mid": v(13.89, -21.03) * mm, "end": v(14.35, -20.9) * mm});
            skPoint(sketch, "E242.17.12", {"position": v(13.49, -21.5) * mm});
            skArc(sketch, "E242.17.13", {"start": v(14.26, -21.61) * mm, "mid": v(14.4, -21.57) * mm, "end": v(14.54, -21.53) * mm});
            skArc(sketch, "E242.17.14", {"start": v(12.98, -22) * mm, "mid": v(12.92, -21.92) * mm, "end": v(12.82, -21.9) * mm});
            skArc(sketch, "E242.17.15", {"start": v(14.14, -21.77) * mm, "mid": v(14.17, -21.67) * mm, "end": v(14.26, -21.61) * mm});
            skArc(sketch, "E242.18.0", {"start": v(16.13, -21.37) * mm, "mid": v(16.13, -21.21) * mm, "end": v(16.1, -21.05) * mm});
            skArc(sketch, "E242.18.1", {"start": v(15.79, -21.85) * mm, "mid": v(16.03, -21.66) * mm, "end": v(16.13, -21.37) * mm});
            skArc(sketch, "E242.18.2", {"start": v(15.26, -20.58) * mm, "mid": v(14.8, -20.75) * mm, "end": v(14.35, -20.9) * mm});
            skPoint(sketch, "E242.18.3", {"position": v(15.5, -21.16) * mm});
            skArc(sketch, "E242.18.4", {"start": v(15.2, -21.75) * mm, "mid": v(15.1, -21.64) * mm, "end": v(15, -21.5) * mm});
            skLineSegment(sketch, "E242.18.5", {"start": v(16.13, -20.16) * mm, "end": v(16.44, -20.74) * mm});
            skArc(sketch, "E242.18.6", {"start": v(14.83, -21.44) * mm, "mid": v(14.68, -21.48) * mm, "end": v(14.54, -21.53) * mm});
            skLineSegment(sketch, "E242.18.7", {"start": v(14.35, -20.9) * mm, "end": v(14.54, -21.53) * mm});
            skArc(sketch, "E242.18.8", {"start": v(15.79, -21.85) * mm, "mid": v(15.48, -21.89) * mm, "end": v(15.2, -21.75) * mm});
            skPoint(sketch, "E242.18.9", {"position": v(15.26, -20.58) * mm});
            skArc(sketch, "E242.18.10", {"start": v(15.4, -20.92) * mm, "mid": v(14.94, -21.1) * mm, "end": v(14.46, -21.26) * mm, "construction": true});
            skArc(sketch, "E242.18.11", {"start": v(15.26, -20.58) * mm, "mid": v(15.7, -20.38) * mm, "end": v(16.13, -20.16) * mm});
            skPoint(sketch, "E242.18.12", {"position": v(15.4, -20.92) * mm});
            skArc(sketch, "E242.18.13", {"start": v(16.17, -20.88) * mm, "mid": v(16.3, -20.81) * mm, "end": v(16.44, -20.74) * mm});
            skArc(sketch, "E242.18.14", {"start": v(15, -21.5) * mm, "mid": v(14.93, -21.44) * mm, "end": v(14.83, -21.44) * mm});
            skArc(sketch, "E242.18.15", {"start": v(16.1, -21.05) * mm, "mid": v(16.1, -20.95) * mm, "end": v(16.17, -20.88) * mm});
            skArc(sketch, "E242.19.0", {"start": v(17.97, -20.28) * mm, "mid": v(17.93, -20.12) * mm, "end": v(17.87, -19.97) * mm});
            skArc(sketch, "E242.19.1", {"start": v(17.72, -20.82) * mm, "mid": v(17.92, -20.58) * mm, "end": v(17.97, -20.28) * mm});
            skArc(sketch, "E242.19.2", {"start": v(16.96, -19.67) * mm, "mid": v(16.55, -19.93) * mm, "end": v(16.13, -20.16) * mm});
            skPoint(sketch, "E242.19.3", {"position": v(17.3, -20.2) * mm});
            skArc(sketch, "E242.19.4", {"start": v(17.14, -20.83) * mm, "mid": v(17, -20.74) * mm, "end": v(16.89, -20.63) * mm});
            skLineSegment(sketch, "E242.19.5", {"start": v(17.73, -19.1) * mm, "end": v(18.15, -19.6) * mm});
            skArc(sketch, "E242.19.6", {"start": v(16.7, -20.6) * mm, "mid": v(16.57, -20.67) * mm, "end": v(16.44, -20.74) * mm});
            skLineSegment(sketch, "E242.19.7", {"start": v(16.13, -20.16) * mm, "end": v(16.44, -20.74) * mm});
            skArc(sketch, "E242.19.8", {"start": v(17.72, -20.82) * mm, "mid": v(17.43, -20.9) * mm, "end": v(17.14, -20.83) * mm});
            skPoint(sketch, "E242.19.9", {"position": v(16.96, -19.67) * mm});
            skArc(sketch, "E242.19.10", {"start": v(17.17, -19.98) * mm, "mid": v(16.74, -20.25) * mm, "end": v(16.3, -20.5) * mm, "construction": true});
            skArc(sketch, "E242.19.11", {"start": v(16.96, -19.67) * mm, "mid": v(17.35, -19.4) * mm, "end": v(17.73, -19.1) * mm});
            skPoint(sketch, "E242.19.12", {"position": v(17.17, -19.98) * mm});
            skArc(sketch, "E242.19.13", {"start": v(17.91, -19.79) * mm, "mid": v(18.03, -19.7) * mm, "end": v(18.15, -19.6) * mm});
            skArc(sketch, "E242.19.14", {"start": v(16.89, -20.63) * mm, "mid": v(16.8, -20.58) * mm, "end": v(16.7, -20.6) * mm});
            skArc(sketch, "E242.19.15", {"start": v(17.87, -19.97) * mm, "mid": v(17.86, -19.87) * mm, "end": v(17.91, -19.79) * mm});
            skArc(sketch, "E242.20.0", {"start": v(19.55, -18.85) * mm, "mid": v(19.5, -18.7) * mm, "end": v(19.4, -18.57) * mm});
            skArc(sketch, "E242.20.1", {"start": v(19.42, -19.42) * mm, "mid": v(19.57, -19.15) * mm, "end": v(19.55, -18.85) * mm});
            skArc(sketch, "E242.20.2", {"start": v(18.45, -18.45) * mm, "mid": v(18.1, -18.78) * mm, "end": v(17.73, -19.1) * mm});
            skPoint(sketch, "E242.20.3", {"position": v(18.9, -18.9) * mm});
            skArc(sketch, "E242.20.4", {"start": v(18.85, -19.55) * mm, "mid": v(18.7, -19.5) * mm, "end": v(18.57, -19.4) * mm});
            skLineSegment(sketch, "E242.20.5", {"start": v(19.1, -17.73) * mm, "end": v(19.6, -18.15) * mm});
            skArc(sketch, "E242.20.6", {"start": v(18.38, -19.4) * mm, "mid": v(18.26, -19.5) * mm, "end": v(18.15, -19.6) * mm});
            skLineSegment(sketch, "E242.20.7", {"start": v(17.73, -19.1) * mm, "end": v(18.15, -19.6) * mm});
            skArc(sketch, "E242.20.8", {"start": v(19.42, -19.42) * mm, "mid": v(19.15, -19.57) * mm, "end": v(18.85, -19.55) * mm});
            skPoint(sketch, "E242.20.9", {"position": v(18.45, -18.45) * mm});
            skArc(sketch, "E242.20.10", {"start": v(18.71, -18.71) * mm, "mid": v(18.35, -19.06) * mm, "end": v(17.97, -19.38) * mm, "construction": true});
            skArc(sketch, "E242.20.11", {"start": v(18.45, -18.45) * mm, "mid": v(18.78, -18.1) * mm, "end": v(19.1, -17.73) * mm});
            skPoint(sketch, "E242.20.12", {"position": v(18.71, -18.71) * mm});
            skArc(sketch, "E242.20.13", {"start": v(19.4, -18.38) * mm, "mid": v(19.5, -18.26) * mm, "end": v(19.6, -18.15) * mm});
            skArc(sketch, "E242.20.14", {"start": v(18.57, -19.4) * mm, "mid": v(18.47, -19.37) * mm, "end": v(18.38, -19.4) * mm});
            skArc(sketch, "E242.20.15", {"start": v(19.4, -18.57) * mm, "mid": v(19.37, -18.47) * mm, "end": v(19.4, -18.38) * mm});
            skArc(sketch, "E242.21.0", {"start": v(20.83, -17.14) * mm, "mid": v(20.74, -17) * mm, "end": v(20.63, -16.89) * mm});
            skArc(sketch, "E242.21.1", {"start": v(20.82, -17.72) * mm, "mid": v(20.9, -17.43) * mm, "end": v(20.83, -17.14) * mm});
            skArc(sketch, "E242.21.2", {"start": v(19.67, -16.96) * mm, "mid": v(19.4, -17.35) * mm, "end": v(19.1, -17.73) * mm});
            skPoint(sketch, "E242.21.3", {"position": v(20.2, -17.3) * mm});
            skArc(sketch, "E242.21.4", {"start": v(20.28, -17.97) * mm, "mid": v(20.12, -17.93) * mm, "end": v(19.97, -17.87) * mm});
            skLineSegment(sketch, "E242.21.5", {"start": v(20.16, -16.13) * mm, "end": v(20.74, -16.44) * mm});
            skArc(sketch, "E242.21.6", {"start": v(19.79, -17.91) * mm, "mid": v(19.7, -18.03) * mm, "end": v(19.6, -18.15) * mm});
            skLineSegment(sketch, "E242.21.7", {"start": v(19.1, -17.73) * mm, "end": v(19.6, -18.15) * mm});
            skArc(sketch, "E242.21.8", {"start": v(20.82, -17.72) * mm, "mid": v(20.58, -17.92) * mm, "end": v(20.28, -17.97) * mm});
            skPoint(sketch, "E242.21.9", {"position": v(19.67, -16.96) * mm});
            skArc(sketch, "E242.21.10", {"start": v(19.98, -17.17) * mm, "mid": v(19.7, -17.58) * mm, "end": v(19.38, -17.97) * mm, "construction": true});
            skArc(sketch, "E242.21.11", {"start": v(19.67, -16.96) * mm, "mid": v(19.93, -16.55) * mm, "end": v(20.16, -16.13) * mm});
            skPoint(sketch, "E242.21.12", {"position": v(19.98, -17.17) * mm});
            skArc(sketch, "E242.21.13", {"start": v(20.6, -16.7) * mm, "mid": v(20.67, -16.57) * mm, "end": v(20.74, -16.44) * mm});
            skArc(sketch, "E242.21.14", {"start": v(19.97, -17.87) * mm, "mid": v(19.87, -17.86) * mm, "end": v(19.79, -17.91) * mm});
            skArc(sketch, "E242.21.15", {"start": v(20.63, -16.89) * mm, "mid": v(20.58, -16.8) * mm, "end": v(20.6, -16.7) * mm});
            skArc(sketch, "E242.22.0", {"start": v(21.75, -15.2) * mm, "mid": v(21.64, -15.1) * mm, "end": v(21.5, -15) * mm});
            skArc(sketch, "E242.22.1", {"start": v(21.85, -15.79) * mm, "mid": v(21.89, -15.48) * mm, "end": v(21.75, -15.2) * mm});
            skArc(sketch, "E242.22.2", {"start": v(20.58, -15.26) * mm, "mid": v(20.38, -15.7) * mm, "end": v(20.16, -16.13) * mm});
            skPoint(sketch, "E242.22.3", {"position": v(21.16, -15.5) * mm});
            skArc(sketch, "E242.22.4", {"start": v(21.37, -16.13) * mm, "mid": v(21.21, -16.13) * mm, "end": v(21.05, -16.1) * mm});
            skLineSegment(sketch, "E242.22.5", {"start": v(20.9, -14.35) * mm, "end": v(21.53, -14.54) * mm});
            skArc(sketch, "E242.22.6", {"start": v(20.88, -16.17) * mm, "mid": v(20.81, -16.3) * mm, "end": v(20.74, -16.44) * mm});
            skLineSegment(sketch, "E242.22.7", {"start": v(20.16, -16.13) * mm, "end": v(20.74, -16.44) * mm});
            skArc(sketch, "E242.22.8", {"start": v(21.85, -15.79) * mm, "mid": v(21.66, -16.03) * mm, "end": v(21.37, -16.13) * mm});
            skPoint(sketch, "E242.22.9", {"position": v(20.58, -15.26) * mm});
            skArc(sketch, "E242.22.10", {"start": v(20.92, -15.4) * mm, "mid": v(20.72, -15.86) * mm, "end": v(20.5, -16.3) * mm, "construction": true});
            skArc(sketch, "E242.22.11", {"start": v(20.58, -15.26) * mm, "mid": v(20.75, -14.8) * mm, "end": v(20.9, -14.35) * mm});
            skPoint(sketch, "E242.22.12", {"position": v(20.92, -15.4) * mm});
            skArc(sketch, "E242.22.13", {"start": v(21.44, -14.83) * mm, "mid": v(21.48, -14.68) * mm, "end": v(21.53, -14.54) * mm});
            skArc(sketch, "E242.22.14", {"start": v(21.05, -16.1) * mm, "mid": v(20.95, -16.1) * mm, "end": v(20.88, -16.17) * mm});
            skArc(sketch, "E242.22.15", {"start": v(21.5, -15) * mm, "mid": v(21.44, -14.93) * mm, "end": v(21.44, -14.83) * mm});
            skArc(sketch, "E242.23.0", {"start": v(22.28, -13.14) * mm, "mid": v(22.14, -13.05) * mm, "end": v(22, -12.98) * mm});
            skArc(sketch, "E242.23.1", {"start": v(22.49, -13.69) * mm, "mid": v(22.46, -13.38) * mm, "end": v(22.28, -13.14) * mm});
            skArc(sketch, "E242.23.2", {"start": v(21.14, -13.42) * mm, "mid": v(21.03, -13.89) * mm, "end": v(20.9, -14.35) * mm});
            skPoint(sketch, "E242.23.3", {"position": v(21.75, -13.54) * mm});
            skArc(sketch, "E242.23.4", {"start": v(22.09, -14.11) * mm, "mid": v(21.93, -14.14) * mm, "end": v(21.77, -14.14) * mm});
            skLineSegment(sketch, "E242.23.5", {"start": v(21.28, -12.46) * mm, "end": v(21.93, -12.53) * mm});
            skArc(sketch, "E242.23.6", {"start": v(21.61, -14.26) * mm, "mid": v(21.57, -14.4) * mm, "end": v(21.53, -14.54) * mm});
            skLineSegment(sketch, "E242.23.7", {"start": v(20.9, -14.35) * mm, "end": v(21.53, -14.54) * mm});
            skArc(sketch, "E242.23.8", {"start": v(22.49, -13.69) * mm, "mid": v(22.35, -13.96) * mm, "end": v(22.09, -14.11) * mm});
            skPoint(sketch, "E242.23.9", {"position": v(21.14, -13.42) * mm});
            skArc(sketch, "E242.23.10", {"start": v(21.5, -13.49) * mm, "mid": v(21.4, -13.98) * mm, "end": v(21.26, -14.46) * mm, "construction": true});
            skArc(sketch, "E242.23.11", {"start": v(21.14, -13.42) * mm, "mid": v(21.22, -12.94) * mm, "end": v(21.28, -12.46) * mm});
            skPoint(sketch, "E242.23.12", {"position": v(21.5, -13.49) * mm});
            skArc(sketch, "E242.23.13", {"start": v(21.9, -12.82) * mm, "mid": v(21.91, -12.68) * mm, "end": v(21.93, -12.53) * mm});
            skArc(sketch, "E242.23.14", {"start": v(21.77, -14.14) * mm, "mid": v(21.67, -14.17) * mm, "end": v(21.61, -14.26) * mm});
            skArc(sketch, "E242.23.15", {"start": v(22, -12.98) * mm, "mid": v(21.92, -12.92) * mm, "end": v(21.9, -12.82) * mm});
            skArc(sketch, "E242.24.0", {"start": v(22.4, -11) * mm, "mid": v(22.24, -10.94) * mm, "end": v(22.08, -10.9) * mm});
            skArc(sketch, "E242.24.1", {"start": v(22.7, -11.5) * mm, "mid": v(22.62, -11.2) * mm, "end": v(22.4, -11) * mm});
            skArc(sketch, "E242.24.2", {"start": v(21.32, -11.5) * mm, "mid": v(21.31, -11.98) * mm, "end": v(21.28, -12.46) * mm});
            skPoint(sketch, "E242.24.3", {"position": v(21.95, -11.5) * mm});
            skArc(sketch, "E242.24.4", {"start": v(22.4, -12) * mm, "mid": v(22.24, -12.06) * mm, "end": v(22.08, -12.1) * mm});
            skLineSegment(sketch, "E242.24.5", {"start": v(21.28, -10.54) * mm, "end": v(21.93, -10.47) * mm});
            skArc(sketch, "E242.24.6", {"start": v(21.95, -12.23) * mm, "mid": v(21.94, -12.38) * mm, "end": v(21.93, -12.53) * mm});
            skLineSegment(sketch, "E242.24.7", {"start": v(21.28, -12.46) * mm, "end": v(21.93, -12.53) * mm});
            skArc(sketch, "E242.24.8", {"start": v(22.7, -11.5) * mm, "mid": v(22.62, -11.8) * mm, "end": v(22.4, -12) * mm});
            skPoint(sketch, "E242.24.9", {"position": v(21.32, -11.5) * mm});
            skArc(sketch, "E242.24.10", {"start": v(21.7, -11.5) * mm, "mid": v(21.69, -12) * mm, "end": v(21.65, -12.5) * mm, "construction": true});
            skArc(sketch, "E242.24.11", {"start": v(21.32, -11.5) * mm, "mid": v(21.31, -11.02) * mm, "end": v(21.28, -10.54) * mm});
            skPoint(sketch, "E242.24.12", {"position": v(21.7, -11.5) * mm});
            skArc(sketch, "E242.24.13", {"start": v(21.95, -10.77) * mm, "mid": v(21.94, -10.62) * mm, "end": v(21.93, -10.47) * mm});
            skArc(sketch, "E242.24.14", {"start": v(22.08, -12.1) * mm, "mid": v(22, -12.14) * mm, "end": v(21.95, -12.23) * mm});
            skArc(sketch, "E242.24.15", {"start": v(22.08, -10.9) * mm, "mid": v(22, -10.86) * mm, "end": v(21.95, -10.77) * mm});
            skArc(sketch, "E242.25.0", {"start": v(22.09, -8.89) * mm, "mid": v(21.93, -8.86) * mm, "end": v(21.77, -8.86) * mm});
            skArc(sketch, "E242.25.1", {"start": v(22.49, -9.31) * mm, "mid": v(22.35, -9.04) * mm, "end": v(22.09, -8.89) * mm});
            skArc(sketch, "E242.25.2", {"start": v(21.14, -9.58) * mm, "mid": v(21.22, -10.06) * mm, "end": v(21.28, -10.54) * mm});
            skPoint(sketch, "E242.25.3", {"position": v(21.75, -9.46) * mm});
            skArc(sketch, "E242.25.4", {"start": v(22.28, -9.86) * mm, "mid": v(22.14, -9.95) * mm, "end": v(22, -10.02) * mm});
            skLineSegment(sketch, "E242.25.5", {"start": v(20.9, -8.65) * mm, "end": v(21.53, -8.46) * mm});
            skArc(sketch, "E242.25.6", {"start": v(21.9, -10.18) * mm, "mid": v(21.91, -10.32) * mm, "end": v(21.93, -10.47) * mm});
            skLineSegment(sketch, "E242.25.7", {"start": v(21.28, -10.54) * mm, "end": v(21.93, -10.47) * mm});
            skArc(sketch, "E242.25.8", {"start": v(22.49, -9.31) * mm, "mid": v(22.46, -9.62) * mm, "end": v(22.28, -9.86) * mm});
            skPoint(sketch, "E242.25.9", {"position": v(21.14, -9.58) * mm});
            skArc(sketch, "E242.25.10", {"start": v(21.5, -9.51) * mm, "mid": v(21.59, -10) * mm, "end": v(21.65, -10.5) * mm, "construction": true});
            skArc(sketch, "E242.25.11", {"start": v(21.14, -9.58) * mm, "mid": v(21.03, -9.11) * mm, "end": v(20.9, -8.65) * mm});
            skPoint(sketch, "E242.25.12", {"position": v(21.5, -9.51) * mm});
            skArc(sketch, "E242.25.13", {"start": v(21.61, -8.74) * mm, "mid": v(21.57, -8.6) * mm, "end": v(21.53, -8.46) * mm});
            skArc(sketch, "E242.25.14", {"start": v(22, -10.02) * mm, "mid": v(21.92, -10.08) * mm, "end": v(21.9, -10.18) * mm});
            skArc(sketch, "E242.25.15", {"start": v(21.77, -8.86) * mm, "mid": v(21.67, -8.83) * mm, "end": v(21.61, -8.74) * mm});
            skArc(sketch, "E242.26.0", {"start": v(21.37, -6.87) * mm, "mid": v(21.21, -6.87) * mm, "end": v(21.05, -6.9) * mm});
            skArc(sketch, "E242.26.1", {"start": v(21.85, -7.21) * mm, "mid": v(21.66, -6.97) * mm, "end": v(21.37, -6.87) * mm});
            skArc(sketch, "E242.26.2", {"start": v(20.58, -7.74) * mm, "mid": v(20.75, -8.2) * mm, "end": v(20.9, -8.65) * mm});
            skPoint(sketch, "E242.26.3", {"position": v(21.16, -7.5) * mm});
            skArc(sketch, "E242.26.4", {"start": v(21.75, -7.8) * mm, "mid": v(21.64, -7.9) * mm, "end": v(21.5, -8) * mm});
            skLineSegment(sketch, "E242.26.5", {"start": v(20.16, -6.87) * mm, "end": v(20.74, -6.56) * mm});
            skArc(sketch, "E242.26.6", {"start": v(21.44, -8.17) * mm, "mid": v(21.48, -8.32) * mm, "end": v(21.53, -8.46) * mm});
            skLineSegment(sketch, "E242.26.7", {"start": v(20.9, -8.65) * mm, "end": v(21.53, -8.46) * mm});
            skArc(sketch, "E242.26.8", {"start": v(21.85, -7.21) * mm, "mid": v(21.89, -7.52) * mm, "end": v(21.75, -7.8) * mm});
            skPoint(sketch, "E242.26.9", {"position": v(20.58, -7.74) * mm});
            skArc(sketch, "E242.26.10", {"start": v(20.92, -7.6) * mm, "mid": v(21.1, -8.06) * mm, "end": v(21.26, -8.54) * mm, "construction": true});
            skArc(sketch, "E242.26.11", {"start": v(20.58, -7.74) * mm, "mid": v(20.38, -7.3) * mm, "end": v(20.16, -6.87) * mm});
            skPoint(sketch, "E242.26.12", {"position": v(20.92, -7.6) * mm});
            skArc(sketch, "E242.26.13", {"start": v(20.88, -6.83) * mm, "mid": v(20.81, -6.7) * mm, "end": v(20.74, -6.56) * mm});
            skArc(sketch, "E242.26.14", {"start": v(21.5, -8) * mm, "mid": v(21.44, -8.07) * mm, "end": v(21.44, -8.17) * mm});
            skArc(sketch, "E242.26.15", {"start": v(21.05, -6.9) * mm, "mid": v(20.95, -6.9) * mm, "end": v(20.88, -6.83) * mm});
            skArc(sketch, "E242.27.0", {"start": v(20.28, -5.03) * mm, "mid": v(20.12, -5.07) * mm, "end": v(19.97, -5.13) * mm});
            skArc(sketch, "E242.27.1", {"start": v(20.82, -5.28) * mm, "mid": v(20.58, -5.08) * mm, "end": v(20.28, -5.03) * mm});
            skArc(sketch, "E242.27.2", {"start": v(19.67, -6.04) * mm, "mid": v(19.93, -6.45) * mm, "end": v(20.16, -6.87) * mm});
            skPoint(sketch, "E242.27.3", {"position": v(20.2, -5.7) * mm});
            skArc(sketch, "E242.27.4", {"start": v(20.83, -5.86) * mm, "mid": v(20.74, -6) * mm, "end": v(20.63, -6.11) * mm});
            skLineSegment(sketch, "E242.27.5", {"start": v(19.1, -5.27) * mm, "end": v(19.6, -4.85) * mm});
            skArc(sketch, "E242.27.6", {"start": v(20.6, -6.3) * mm, "mid": v(20.67, -6.43) * mm, "end": v(20.74, -6.56) * mm});
            skLineSegment(sketch, "E242.27.7", {"start": v(20.16, -6.87) * mm, "end": v(20.74, -6.56) * mm});
            skArc(sketch, "E242.27.8", {"start": v(20.82, -5.28) * mm, "mid": v(20.9, -5.57) * mm, "end": v(20.83, -5.86) * mm});
            skPoint(sketch, "E242.27.9", {"position": v(19.67, -6.04) * mm});
            skArc(sketch, "E242.27.10", {"start": v(19.98, -5.83) * mm, "mid": v(20.25, -6.26) * mm, "end": v(20.5, -6.7) * mm, "construction": true});
            skArc(sketch, "E242.27.11", {"start": v(19.67, -6.04) * mm, "mid": v(19.4, -5.65) * mm, "end": v(19.1, -5.27) * mm});
            skPoint(sketch, "E242.27.12", {"position": v(19.98, -5.83) * mm});
            skArc(sketch, "E242.27.13", {"start": v(19.79, -5.09) * mm, "mid": v(19.7, -4.97) * mm, "end": v(19.6, -4.85) * mm});
            skArc(sketch, "E242.27.14", {"start": v(20.63, -6.11) * mm, "mid": v(20.58, -6.2) * mm, "end": v(20.6, -6.3) * mm});
            skArc(sketch, "E242.27.15", {"start": v(19.97, -5.13) * mm, "mid": v(19.87, -5.14) * mm, "end": v(19.79, -5.09) * mm});
            skArc(sketch, "E242.28.0", {"start": v(18.85, -3.45) * mm, "mid": v(18.7, -3.5) * mm, "end": v(18.57, -3.6) * mm});
            skArc(sketch, "E242.28.1", {"start": v(19.42, -3.58) * mm, "mid": v(19.15, -3.43) * mm, "end": v(18.85, -3.45) * mm});
            skArc(sketch, "E242.28.2", {"start": v(18.45, -4.55) * mm, "mid": v(18.78, -4.9) * mm, "end": v(19.1, -5.27) * mm});
            skPoint(sketch, "E242.28.3", {"position": v(18.9, -4.1) * mm});
            skArc(sketch, "E242.28.4", {"start": v(19.55, -4.15) * mm, "mid": v(19.5, -4.3) * mm, "end": v(19.4, -4.43) * mm});
            skLineSegment(sketch, "E242.28.5", {"start": v(17.73, -3.9) * mm, "end": v(18.15, -3.4) * mm});
            skArc(sketch, "E242.28.6", {"start": v(19.4, -4.62) * mm, "mid": v(19.5, -4.74) * mm, "end": v(19.6, -4.85) * mm});
            skLineSegment(sketch, "E242.28.7", {"start": v(19.1, -5.27) * mm, "end": v(19.6, -4.85) * mm});
            skArc(sketch, "E242.28.8", {"start": v(19.42, -3.58) * mm, "mid": v(19.57, -3.85) * mm, "end": v(19.55, -4.15) * mm});
            skPoint(sketch, "E242.28.9", {"position": v(18.45, -4.55) * mm});
            skArc(sketch, "E242.28.10", {"start": v(18.71, -4.29) * mm, "mid": v(19.06, -4.65) * mm, "end": v(19.38, -5.03) * mm, "construction": true});
            skArc(sketch, "E242.28.11", {"start": v(18.45, -4.55) * mm, "mid": v(18.1, -4.22) * mm, "end": v(17.73, -3.9) * mm});
            skPoint(sketch, "E242.28.12", {"position": v(18.71, -4.29) * mm});
            skArc(sketch, "E242.28.13", {"start": v(18.38, -3.6) * mm, "mid": v(18.26, -3.5) * mm, "end": v(18.15, -3.4) * mm});
            skArc(sketch, "E242.28.14", {"start": v(19.4, -4.43) * mm, "mid": v(19.37, -4.53) * mm, "end": v(19.4, -4.62) * mm});
            skArc(sketch, "E242.28.15", {"start": v(18.57, -3.6) * mm, "mid": v(18.47, -3.63) * mm, "end": v(18.38, -3.6) * mm});
            skArc(sketch, "E242.29.0", {"start": v(17.14, -2.17) * mm, "mid": v(17, -2.26) * mm, "end": v(16.89, -2.37) * mm});
            skArc(sketch, "E242.29.1", {"start": v(17.72, -2.18) * mm, "mid": v(17.43, -2.1) * mm, "end": v(17.14, -2.17) * mm});
            skArc(sketch, "E242.29.2", {"start": v(16.96, -3.33) * mm, "mid": v(17.35, -3.6) * mm, "end": v(17.73, -3.9) * mm});
            skPoint(sketch, "E242.29.3", {"position": v(17.3, -2.8) * mm});
            skArc(sketch, "E242.29.4", {"start": v(17.97, -2.72) * mm, "mid": v(17.93, -2.88) * mm, "end": v(17.87, -3.03) * mm});
            skLineSegment(sketch, "E242.29.5", {"start": v(16.13, -2.84) * mm, "end": v(16.44, -2.26) * mm});
            skArc(sketch, "E242.29.6", {"start": v(17.91, -3.21) * mm, "mid": v(18.03, -3.3) * mm, "end": v(18.15, -3.4) * mm});
            skLineSegment(sketch, "E242.29.7", {"start": v(17.73, -3.9) * mm, "end": v(18.15, -3.4) * mm});
            skArc(sketch, "E242.29.8", {"start": v(17.72, -2.18) * mm, "mid": v(17.92, -2.42) * mm, "end": v(17.97, -2.72) * mm});
            skPoint(sketch, "E242.29.9", {"position": v(16.96, -3.33) * mm});
            skArc(sketch, "E242.29.10", {"start": v(17.17, -3.02) * mm, "mid": v(17.58, -3.3) * mm, "end": v(17.97, -3.62) * mm, "construction": true});
            skArc(sketch, "E242.29.11", {"start": v(16.96, -3.33) * mm, "mid": v(16.55, -3.07) * mm, "end": v(16.13, -2.84) * mm});
            skPoint(sketch, "E242.29.12", {"position": v(17.17, -3.02) * mm});
            skArc(sketch, "E242.29.13", {"start": v(16.7, -2.4) * mm, "mid": v(16.57, -2.33) * mm, "end": v(16.44, -2.26) * mm});
            skArc(sketch, "E242.29.14", {"start": v(17.87, -3.03) * mm, "mid": v(17.86, -3.13) * mm, "end": v(17.91, -3.21) * mm});
            skArc(sketch, "E242.29.15", {"start": v(16.89, -2.37) * mm, "mid": v(16.8, -2.42) * mm, "end": v(16.7, -2.4) * mm});
            skArc(sketch, "E242.30.0", {"start": v(15.2, -1.25) * mm, "mid": v(15.1, -1.36) * mm, "end": v(15, -1.5) * mm});
            skArc(sketch, "E242.30.1", {"start": v(15.79, -1.15) * mm, "mid": v(15.48, -1.11) * mm, "end": v(15.2, -1.25) * mm});
            skArc(sketch, "E242.30.2", {"start": v(15.26, -2.42) * mm, "mid": v(15.7, -2.62) * mm, "end": v(16.13, -2.84) * mm});
            skPoint(sketch, "E242.30.3", {"position": v(15.5, -1.84) * mm});
            skArc(sketch, "E242.30.4", {"start": v(16.13, -1.63) * mm, "mid": v(16.13, -1.79) * mm, "end": v(16.1, -1.95) * mm});
            skLineSegment(sketch, "E242.30.5", {"start": v(14.35, -2.1) * mm, "end": v(14.54, -1.47) * mm});
            skArc(sketch, "E242.30.6", {"start": v(16.17, -2.12) * mm, "mid": v(16.3, -2.19) * mm, "end": v(16.44, -2.26) * mm});
            skLineSegment(sketch, "E242.30.7", {"start": v(16.13, -2.84) * mm, "end": v(16.44, -2.26) * mm});
            skArc(sketch, "E242.30.8", {"start": v(15.79, -1.15) * mm, "mid": v(16.03, -1.34) * mm, "end": v(16.13, -1.63) * mm});
            skPoint(sketch, "E242.30.9", {"position": v(15.26, -2.42) * mm});
            skArc(sketch, "E242.30.10", {"start": v(15.4, -2.08) * mm, "mid": v(15.86, -2.28) * mm, "end": v(16.3, -2.5) * mm, "construction": true});
            skArc(sketch, "E242.30.11", {"start": v(15.26, -2.42) * mm, "mid": v(14.8, -2.25) * mm, "end": v(14.35, -2.1) * mm});
            skPoint(sketch, "E242.30.12", {"position": v(15.4, -2.08) * mm});
            skArc(sketch, "E242.30.13", {"start": v(14.83, -1.56) * mm, "mid": v(14.68, -1.52) * mm, "end": v(14.54, -1.47) * mm});
            skArc(sketch, "E242.30.14", {"start": v(16.1, -1.95) * mm, "mid": v(16.1, -2.05) * mm, "end": v(16.17, -2.12) * mm});
            skArc(sketch, "E242.30.15", {"start": v(15, -1.5) * mm, "mid": v(14.93, -1.56) * mm, "end": v(14.83, -1.56) * mm});
            skArc(sketch, "E242.31.0", {"start": v(13.14, -0.72) * mm, "mid": v(13.05, -0.86) * mm, "end": v(12.98, -1) * mm});
            skArc(sketch, "E242.31.1", {"start": v(13.69, -0.51) * mm, "mid": v(13.38, -0.54) * mm, "end": v(13.14, -0.72) * mm});
            skArc(sketch, "E242.31.2", {"start": v(13.42, -1.86) * mm, "mid": v(13.89, -1.97) * mm, "end": v(14.35, -2.1) * mm});
            skPoint(sketch, "E242.31.3", {"position": v(13.54, -1.25) * mm});
            skArc(sketch, "E242.31.4", {"start": v(14.11, -0.91) * mm, "mid": v(14.14, -1.07) * mm, "end": v(14.14, -1.23) * mm});
            skArc(sketch, "E242.31.6", {"start": v(14.26, -1.39) * mm, "mid": v(14.4, -1.43) * mm, "end": v(14.54, -1.47) * mm});
            skLineSegment(sketch, "E242.31.7", {"start": v(14.35, -2.1) * mm, "end": v(14.54, -1.47) * mm});
            skArc(sketch, "E242.31.8", {"start": v(13.69, -0.51) * mm, "mid": v(13.96, -0.65) * mm, "end": v(14.11, -0.91) * mm});
            skPoint(sketch, "E242.31.9", {"position": v(13.42, -1.86) * mm});
            skArc(sketch, "E242.31.10", {"start": v(13.49, -1.5) * mm, "mid": v(13.98, -1.6) * mm, "end": v(14.46, -1.74) * mm, "construction": true});
            skArc(sketch, "E242.31.11", {"start": v(13.42, -1.86) * mm, "mid": v(12.94, -1.78) * mm, "end": v(12.46, -1.72) * mm});
            skPoint(sketch, "E242.31.12", {"position": v(13.49, -1.5) * mm});
            skArc(sketch, "E242.31.13", {"start": v(12.82, -1.1) * mm, "mid": v(12.68, -1.09) * mm, "end": v(12.53, -1.07) * mm});
            skArc(sketch, "E242.31.14", {"start": v(14.14, -1.23) * mm, "mid": v(14.17, -1.33) * mm, "end": v(14.26, -1.39) * mm});
            skArc(sketch, "E242.31.15", {"start": v(12.98, -1) * mm, "mid": v(12.92, -1.08) * mm, "end": v(12.82, -1.1) * mm});
            skArc(sketch, "E243.0", {"start": v(4.25, -18.75) * mm, "mid": v(18.75, -18.75) * mm, "end": v(18.75, -4.25) * mm});
            skSolve(sketch);
        }
        {
            var Q0;
            Q0=qSketchRegion(id+"F37",true);
            extrude(context, id + "F38", {"entities" : qUnion([Q0]), "operationType" : NewBodyOperationType.REMOVE, "endBound" : BoundingType.SYMMETRIC, "oppositeDirection" : true, "depth" : 6.5 * mm});
        }
        {
            var Q0;
            Q0=qCreatedBy(makeId("Top.planeOp"),FACE);
            var sketch = newSketch(context, id + "F39", { "sketchPlane" : qUnion([Q0])});
            skLineSegment(sketch, "E244.bottom", {"start": v(-46.89, -45.69) * mm, "end": v(-10.89, -45.69) * mm});
            skLineSegment(sketch, "E244.top", {"start": v(-46.89, -11.69) * mm, "end": v(-10.89, -11.69) * mm});
            skLineSegment(sketch, "E244.left", {"start": v(-46.89, -45.69) * mm, "end": v(-46.89, -11.69) * mm});
            skLineSegment(sketch, "E244.right", {"start": v(-10.89, -45.69) * mm, "end": v(-10.89, -11.69) * mm});
            skLineSegment(sketch, "E245", {"start": v(-46.89, -28.69) * mm, "end": v(-10.89, -28.69) * mm, "construction": true});
            skLineSegment(sketch, "E246", {"start": v(-28.89, -45.69) * mm, "end": v(-28.89, -11.69) * mm, "construction": true});
            skCircle(sketch, "E247", {"center": v(-42.89, -41.69) * mm, "radius": 1.55 * mm});
            skCircle(sketch, "E248.MirrorC", {"center": v(-42.89, -15.69) * mm, "radius": 1.55 * mm});
            skCircle(sketch, "E249.MirrorC", {"center": v(-14.89, -41.69) * mm, "radius": 1.55 * mm});
            skCircle(sketch, "E250.MirrorC", {"center": v(-14.89, -15.69) * mm, "radius": 1.55 * mm});
            skPoint(sketch, "E251", {"position": v(-36.89, -28.69) * mm});
            skPoint(sketch, "E252.MirrorP", {"position": v(-20.89, -28.69) * mm});
            skSolve(sketch);
        }
        {
            var Q0;
            Q0=qSketchRegion(id+"F39",true);
            extrude(context, id + "F40", {"entities" : qUnion([Q0]), "depth" : 15 * mm});
        }
        {
            var Q0;
            Q0=makeQuery(id+"F40.opExtrude","SWEPT_FACE",FACE,{"disambiguationData":[OSD([sQuery(id+"F39.wireOp",EDGE,"E244.right")])]});
            var sketch = newSketch(context, id + "F41", { "sketchPlane" : qUnion([Q0])});
            skPoint(sketch, "E253", {"position": v(-28.69, 15) * mm});
            skArc(sketch, "E254", {"start": v(-38.94, 15) * mm, "mid": v(-28.69, 4.75) * mm, "end": v(-18.44, 15) * mm});
            skLineSegment(sketch, "E255", {"start": v(-38.94, 15) * mm, "end": v(-18.44, 15) * mm});
            skSolve(sketch);
        }
        {
            var Q0;
            Q0=qSketchRegion(id+"F41",true);
            var Q1;
            Q1=makeQuery(id+"F40.opExtrude","SWEPT_FACE",FACE,{"disambiguationData":[OSD([sQuery(id+"F39.wireOp",EDGE,"E244.left")])]});
            extrude(context, id + "F42", {"entities" : qUnion([Q0]), "operationType" : NewBodyOperationType.REMOVE, "endBound" : BoundingType.UP_TO_SURFACE, "oppositeDirection" : true, "endBoundEntityFace" : qUnion([Q1]), "depth" : 25 * mm});
        }
        {
            var Q0;
            Q0=makeQuery(id+"F40.opExtrude","SWEPT_FACE",FACE,{"disambiguationData":[OSD([sQuery(id+"F39.wireOp",EDGE,"E244.right")])]});
            var Q1;
            Q1=sQuery(id+"F39.wireOp",VERTEX,"E252.MirrorP");
            cPlane(context, id + "F43", {"entities" : qUnion([Q0, Q1]), "cplaneType" : CPlaneType.PLANE_POINT, "offset" : 150 * mm, "width" : 150 * mm, "height" : 150 * mm});
        }
        {
            var Q0;
            Q0=qCreatedBy(id+"F43.planeOp",FACE);
            var sketch = newSketch(context, id + "F44", { "sketchPlane" : qUnion([Q0])});
            skLineSegment(sketch, "E256", {"start": v(-28.69, 26.2) * mm, "end": v(-28.69, 24.82) * mm, "construction": true});
            skArc(sketch, "E257", {"start": v(-28.69, 26.2) * mm, "mid": v(-28.4, 26.12) * mm, "end": v(-28.19, 25.9) * mm});
            skArc(sketch, "E258", {"start": v(-28.19, 25.9) * mm, "mid": v(-28.13, 25.74) * mm, "end": v(-28.1, 25.58) * mm});
            skArc(sketch, "E259", {"start": v(-28.1, 25.58) * mm, "mid": v(-28.05, 25.5) * mm, "end": v(-27.96, 25.45) * mm});
            skPoint(sketch, "E260", {"position": v(-28.69, 24.82) * mm});
            skPoint(sketch, "E261", {"position": v(-28.69, 25.45) * mm});
            skPoint(sketch, "E262", {"position": v(-28.69, 25.2) * mm});
            skArc(sketch, "E263", {"start": v(-28.69, 25.2) * mm, "mid": v(-28.19, 25.19) * mm, "end": v(-27.69, 25.15) * mm, "construction": true});
            skLineSegment(sketch, "E264", {"start": v(-27.73, 24.78) * mm, "end": v(-27.66, 25.43) * mm});
            skArc(sketch, "E265", {"start": v(-27.96, 25.45) * mm, "mid": v(-27.8, 25.44) * mm, "end": v(-27.66, 25.43) * mm});
            skArc(sketch, "E266", {"start": v(-28.69, 24.82) * mm, "mid": v(-28.2, 24.81) * mm, "end": v(-27.73, 24.78) * mm});
            skArc(sketch, "E267.MirrorCS", {"start": v(-28.69, 26.2) * mm, "mid": v(-28.98, 26.12) * mm, "end": v(-29.19, 25.9) * mm});
            skArc(sketch, "E268.MirrorCS", {"start": v(-29.19, 25.9) * mm, "mid": v(-29.25, 25.74) * mm, "end": v(-29.28, 25.58) * mm});
            skArc(sketch, "E269.MirrorCS", {"start": v(-29.28, 25.58) * mm, "mid": v(-29.33, 25.5) * mm, "end": v(-29.42, 25.45) * mm});
            skArc(sketch, "E270.MirrorCS", {"start": v(-29.42, 25.45) * mm, "mid": v(-29.57, 25.44) * mm, "end": v(-29.72, 25.43) * mm});
            skLineSegment(sketch, "E271.MirrorCS", {"start": v(-29.65, 24.78) * mm, "end": v(-29.72, 25.43) * mm});
            skArc(sketch, "E272.MirrorCS", {"start": v(-28.69, 24.82) * mm, "mid": v(-29.17, 24.81) * mm, "end": v(-29.65, 24.78) * mm});
            skArc(sketch, "E273.1.0", {"start": v(-31.3, 25.59) * mm, "mid": v(-31.33, 25.43) * mm, "end": v(-31.33, 25.27) * mm});
            skArc(sketch, "E273.1.1", {"start": v(-30.87, 25.99) * mm, "mid": v(-31.15, 25.85) * mm, "end": v(-31.3, 25.59) * mm});
            skArc(sketch, "E273.1.2", {"start": v(-30.6, 24.64) * mm, "mid": v(-30.13, 24.72) * mm, "end": v(-29.65, 24.78) * mm});
            skPoint(sketch, "E273.1.3", {"position": v(-30.73, 25.25) * mm});
            skArc(sketch, "E273.1.4", {"start": v(-30.32, 25.78) * mm, "mid": v(-30.24, 25.64) * mm, "end": v(-30.17, 25.5) * mm});
            skLineSegment(sketch, "E273.1.5", {"start": v(-31.54, 24.4) * mm, "end": v(-31.73, 25.03) * mm});
            skArc(sketch, "E273.1.6", {"start": v(-30.01, 25.4) * mm, "mid": v(-29.86, 25.41) * mm, "end": v(-29.72, 25.43) * mm});
            skArc(sketch, "E273.1.8", {"start": v(-30.87, 25.99) * mm, "mid": v(-30.57, 25.96) * mm, "end": v(-30.32, 25.78) * mm});
            skPoint(sketch, "E273.1.9", {"position": v(-30.6, 24.64) * mm});
            skArc(sketch, "E273.1.10", {"start": v(-30.68, 25) * mm, "mid": v(-30.19, 25.09) * mm, "end": v(-29.69, 25.15) * mm, "construction": true});
            skArc(sketch, "E273.1.11", {"start": v(-30.6, 24.64) * mm, "mid": v(-31.08, 24.53) * mm, "end": v(-31.54, 24.4) * mm});
            skPoint(sketch, "E273.1.12", {"position": v(-30.68, 25) * mm});
            skArc(sketch, "E273.1.13", {"start": v(-31.44, 25.11) * mm, "mid": v(-31.59, 25.07) * mm, "end": v(-31.73, 25.03) * mm});
            skArc(sketch, "E273.1.14", {"start": v(-30.17, 25.5) * mm, "mid": v(-30.11, 25.42) * mm, "end": v(-30.01, 25.4) * mm});
            skArc(sketch, "E273.1.15", {"start": v(-31.33, 25.27) * mm, "mid": v(-31.36, 25.17) * mm, "end": v(-31.44, 25.11) * mm});
            skArc(sketch, "E273.2.0", {"start": v(-33.32, 24.87) * mm, "mid": v(-33.31, 24.71) * mm, "end": v(-33.29, 24.55) * mm});
            skArc(sketch, "E273.2.1", {"start": v(-32.98, 25.35) * mm, "mid": v(-33.22, 25.16) * mm, "end": v(-33.32, 24.87) * mm});
            skArc(sketch, "E273.2.2", {"start": v(-32.45, 24.08) * mm, "mid": v(-32, 24.25) * mm, "end": v(-31.54, 24.4) * mm});
            skPoint(sketch, "E273.2.3", {"position": v(-32.69, 24.66) * mm});
            skArc(sketch, "E273.2.4", {"start": v(-32.4, 25.25) * mm, "mid": v(-32.28, 25.14) * mm, "end": v(-32.2, 25) * mm});
            skLineSegment(sketch, "E273.2.5", {"start": v(-33.32, 23.66) * mm, "end": v(-33.63, 24.24) * mm});
            skArc(sketch, "E273.2.6", {"start": v(-32.01, 24.94) * mm, "mid": v(-31.87, 24.98) * mm, "end": v(-31.73, 25.03) * mm});
            skLineSegment(sketch, "E273.2.7", {"start": v(-31.54, 24.4) * mm, "end": v(-31.73, 25.03) * mm});
            skArc(sketch, "E273.2.8", {"start": v(-32.98, 25.35) * mm, "mid": v(-32.67, 25.39) * mm, "end": v(-32.4, 25.25) * mm});
            skPoint(sketch, "E273.2.9", {"position": v(-32.45, 24.08) * mm});
            skArc(sketch, "E273.2.10", {"start": v(-32.6, 24.42) * mm, "mid": v(-32.12, 24.6) * mm, "end": v(-31.65, 24.76) * mm, "construction": true});
            skArc(sketch, "E273.2.11", {"start": v(-32.45, 24.08) * mm, "mid": v(-32.89, 23.88) * mm, "end": v(-33.32, 23.66) * mm});
            skPoint(sketch, "E273.2.12", {"position": v(-32.6, 24.42) * mm});
            skArc(sketch, "E273.2.13", {"start": v(-33.36, 24.38) * mm, "mid": v(-33.5, 24.31) * mm, "end": v(-33.63, 24.24) * mm});
            skArc(sketch, "E273.2.14", {"start": v(-32.2, 25) * mm, "mid": v(-32.12, 24.94) * mm, "end": v(-32.01, 24.94) * mm});
            skArc(sketch, "E273.2.15", {"start": v(-33.29, 24.55) * mm, "mid": v(-33.3, 24.45) * mm, "end": v(-33.36, 24.38) * mm});
            skArc(sketch, "E273.3.0", {"start": v(-35.15, 23.78) * mm, "mid": v(-35.12, 23.62) * mm, "end": v(-35.06, 23.47) * mm});
            skArc(sketch, "E273.3.1", {"start": v(-34.91, 24.32) * mm, "mid": v(-35.11, 24.08) * mm, "end": v(-35.15, 23.78) * mm});
            skArc(sketch, "E273.3.2", {"start": v(-34.15, 23.17) * mm, "mid": v(-33.74, 23.43) * mm, "end": v(-33.32, 23.66) * mm});
            skPoint(sketch, "E273.3.3", {"position": v(-34.5, 23.7) * mm});
            skArc(sketch, "E273.3.4", {"start": v(-34.33, 24.33) * mm, "mid": v(-34.2, 24.24) * mm, "end": v(-34.08, 24.13) * mm});
            skLineSegment(sketch, "E273.3.5", {"start": v(-34.92, 22.6) * mm, "end": v(-35.34, 23.1) * mm});
            skArc(sketch, "E273.3.6", {"start": v(-33.89, 24.1) * mm, "mid": v(-33.76, 24.17) * mm, "end": v(-33.63, 24.24) * mm});
            skLineSegment(sketch, "E273.3.7", {"start": v(-33.32, 23.66) * mm, "end": v(-33.63, 24.24) * mm});
            skArc(sketch, "E273.3.8", {"start": v(-34.91, 24.32) * mm, "mid": v(-34.62, 24.4) * mm, "end": v(-34.33, 24.33) * mm});
            skPoint(sketch, "E273.3.9", {"position": v(-34.15, 23.17) * mm});
            skArc(sketch, "E273.3.10", {"start": v(-34.36, 23.48) * mm, "mid": v(-33.93, 23.75) * mm, "end": v(-33.5, 24) * mm, "construction": true});
            skArc(sketch, "E273.3.11", {"start": v(-34.15, 23.17) * mm, "mid": v(-34.54, 22.9) * mm, "end": v(-34.92, 22.6) * mm});
            skPoint(sketch, "E273.3.12", {"position": v(-34.36, 23.48) * mm});
            skArc(sketch, "E273.3.13", {"start": v(-35.1, 23.29) * mm, "mid": v(-35.22, 23.2) * mm, "end": v(-35.34, 23.1) * mm});
            skArc(sketch, "E273.3.14", {"start": v(-34.08, 24.13) * mm, "mid": v(-33.99, 24.08) * mm, "end": v(-33.89, 24.1) * mm});
            skArc(sketch, "E273.3.15", {"start": v(-35.06, 23.47) * mm, "mid": v(-35.05, 23.37) * mm, "end": v(-35.1, 23.29) * mm});
            skArc(sketch, "E273.4.0", {"start": v(-36.74, 22.35) * mm, "mid": v(-36.68, 22.2) * mm, "end": v(-36.6, 22.07) * mm});
            skArc(sketch, "E273.4.1", {"start": v(-36.61, 22.92) * mm, "mid": v(-36.76, 22.65) * mm, "end": v(-36.74, 22.35) * mm});
            skArc(sketch, "E273.4.2", {"start": v(-35.64, 21.95) * mm, "mid": v(-35.29, 22.28) * mm, "end": v(-34.92, 22.6) * mm});
            skPoint(sketch, "E273.4.3", {"position": v(-36.08, 22.4) * mm});
            skArc(sketch, "E273.4.4", {"start": v(-36.04, 23.05) * mm, "mid": v(-35.89, 23) * mm, "end": v(-35.75, 22.9) * mm});
            skLineSegment(sketch, "E273.4.5", {"start": v(-36.28, 21.23) * mm, "end": v(-36.79, 21.65) * mm});
            skArc(sketch, "E273.4.6", {"start": v(-35.56, 22.9) * mm, "mid": v(-35.45, 23) * mm, "end": v(-35.34, 23.1) * mm});
            skLineSegment(sketch, "E273.4.7", {"start": v(-34.92, 22.6) * mm, "end": v(-35.34, 23.1) * mm});
            skArc(sketch, "E273.4.8", {"start": v(-36.61, 22.92) * mm, "mid": v(-36.34, 23.07) * mm, "end": v(-36.04, 23.05) * mm});
            skPoint(sketch, "E273.4.9", {"position": v(-35.64, 21.95) * mm});
            skArc(sketch, "E273.4.10", {"start": v(-35.9, 22.21) * mm, "mid": v(-35.54, 22.56) * mm, "end": v(-35.16, 22.88) * mm, "construction": true});
            skArc(sketch, "E273.4.11", {"start": v(-35.64, 21.95) * mm, "mid": v(-35.97, 21.6) * mm, "end": v(-36.28, 21.23) * mm});
            skPoint(sketch, "E273.4.12", {"position": v(-35.9, 22.21) * mm});
            skArc(sketch, "E273.4.13", {"start": v(-36.6, 21.88) * mm, "mid": v(-36.7, 21.76) * mm, "end": v(-36.79, 21.65) * mm});
            skArc(sketch, "E273.4.14", {"start": v(-35.75, 22.9) * mm, "mid": v(-35.66, 22.87) * mm, "end": v(-35.56, 22.9) * mm});
            skArc(sketch, "E273.4.15", {"start": v(-36.6, 22.07) * mm, "mid": v(-36.56, 21.97) * mm, "end": v(-36.6, 21.88) * mm});
            skArc(sketch, "E273.5.0", {"start": v(-38.02, 20.64) * mm, "mid": v(-37.93, 20.5) * mm, "end": v(-37.82, 20.39) * mm});
            skArc(sketch, "E273.5.1", {"start": v(-38, 21.22) * mm, "mid": v(-38.1, 20.93) * mm, "end": v(-38.02, 20.64) * mm});
            skArc(sketch, "E273.5.2", {"start": v(-36.86, 20.46) * mm, "mid": v(-36.58, 20.85) * mm, "end": v(-36.28, 21.23) * mm});
            skPoint(sketch, "E273.5.3", {"position": v(-37.38, 20.8) * mm});
            skArc(sketch, "E273.5.4", {"start": v(-37.47, 21.47) * mm, "mid": v(-37.31, 21.43) * mm, "end": v(-37.16, 21.37) * mm});
            skLineSegment(sketch, "E273.5.5", {"start": v(-37.35, 19.63) * mm, "end": v(-37.93, 19.94) * mm});
            skArc(sketch, "E273.5.6", {"start": v(-36.98, 21.41) * mm, "mid": v(-36.88, 21.53) * mm, "end": v(-36.79, 21.65) * mm});
            skLineSegment(sketch, "E273.5.7", {"start": v(-36.28, 21.23) * mm, "end": v(-36.79, 21.65) * mm});
            skArc(sketch, "E273.5.8", {"start": v(-38, 21.22) * mm, "mid": v(-37.77, 21.42) * mm, "end": v(-37.47, 21.47) * mm});
            skPoint(sketch, "E273.5.9", {"position": v(-36.86, 20.46) * mm});
            skArc(sketch, "E273.5.10", {"start": v(-37.17, 20.67) * mm, "mid": v(-36.88, 21.08) * mm, "end": v(-36.57, 21.47) * mm, "construction": true});
            skArc(sketch, "E273.5.11", {"start": v(-36.86, 20.46) * mm, "mid": v(-37.11, 20.05) * mm, "end": v(-37.35, 19.63) * mm});
            skPoint(sketch, "E273.5.12", {"position": v(-37.17, 20.67) * mm});
            skArc(sketch, "E273.5.13", {"start": v(-37.79, 20.2) * mm, "mid": v(-37.86, 20.07) * mm, "end": v(-37.93, 19.94) * mm});
            skArc(sketch, "E273.5.14", {"start": v(-37.16, 21.37) * mm, "mid": v(-37.06, 21.36) * mm, "end": v(-36.98, 21.41) * mm});
            skArc(sketch, "E273.5.15", {"start": v(-37.82, 20.39) * mm, "mid": v(-37.77, 20.3) * mm, "end": v(-37.79, 20.2) * mm});
            skArc(sketch, "E273.6.0", {"start": v(-38.94, 18.7) * mm, "mid": v(-38.83, 18.6) * mm, "end": v(-38.7, 18.5) * mm});
            skArc(sketch, "E273.6.1", {"start": v(-39.04, 19.29) * mm, "mid": v(-39.07, 18.98) * mm, "end": v(-38.94, 18.7) * mm});
            skArc(sketch, "E273.6.2", {"start": v(-37.76, 18.76) * mm, "mid": v(-37.57, 19.2) * mm, "end": v(-37.35, 19.63) * mm});
            skPoint(sketch, "E273.6.3", {"position": v(-38.35, 19) * mm});
            skArc(sketch, "E273.6.4", {"start": v(-38.56, 19.63) * mm, "mid": v(-38.4, 19.63) * mm, "end": v(-38.24, 19.6) * mm});
            skLineSegment(sketch, "E273.6.5", {"start": v(-38.09, 17.85) * mm, "end": v(-38.72, 18.04) * mm});
            skArc(sketch, "E273.6.6", {"start": v(-38.07, 19.67) * mm, "mid": v(-38, 19.8) * mm, "end": v(-37.93, 19.94) * mm});
            skLineSegment(sketch, "E273.6.7", {"start": v(-37.35, 19.63) * mm, "end": v(-37.93, 19.94) * mm});
            skArc(sketch, "E273.6.8", {"start": v(-39.04, 19.29) * mm, "mid": v(-38.85, 19.53) * mm, "end": v(-38.56, 19.63) * mm});
            skPoint(sketch, "E273.6.9", {"position": v(-37.76, 18.76) * mm});
            skArc(sketch, "E273.6.10", {"start": v(-38.11, 18.9) * mm, "mid": v(-37.9, 19.36) * mm, "end": v(-37.68, 19.8) * mm, "construction": true});
            skArc(sketch, "E273.6.11", {"start": v(-37.76, 18.76) * mm, "mid": v(-37.94, 18.3) * mm, "end": v(-38.09, 17.85) * mm});
            skPoint(sketch, "E273.6.12", {"position": v(-38.11, 18.9) * mm});
            skArc(sketch, "E273.6.13", {"start": v(-38.63, 18.33) * mm, "mid": v(-38.67, 18.18) * mm, "end": v(-38.72, 18.04) * mm});
            skArc(sketch, "E273.6.14", {"start": v(-38.24, 19.6) * mm, "mid": v(-38.14, 19.6) * mm, "end": v(-38.07, 19.67) * mm});
            skArc(sketch, "E273.6.15", {"start": v(-38.7, 18.5) * mm, "mid": v(-38.63, 18.43) * mm, "end": v(-38.63, 18.33) * mm});
            skArc(sketch, "E273.7.0", {"start": v(-39.47, 16.64) * mm, "mid": v(-39.33, 16.55) * mm, "end": v(-39.18, 16.48) * mm});
            skArc(sketch, "E273.7.1", {"start": v(-39.68, 17.19) * mm, "mid": v(-39.65, 16.88) * mm, "end": v(-39.47, 16.64) * mm});
            skArc(sketch, "E273.7.2", {"start": v(-38.32, 16.92) * mm, "mid": v(-38.22, 17.39) * mm, "end": v(-38.09, 17.85) * mm});
            skPoint(sketch, "E273.7.3", {"position": v(-38.94, 17.04) * mm});
            skArc(sketch, "E273.7.4", {"start": v(-39.27, 17.61) * mm, "mid": v(-39.12, 17.64) * mm, "end": v(-38.95, 17.64) * mm});
            skLineSegment(sketch, "E273.7.5", {"start": v(-38.47, 15.96) * mm, "end": v(-39.12, 16.03) * mm});
            skArc(sketch, "E273.7.6", {"start": v(-38.8, 17.76) * mm, "mid": v(-38.76, 17.9) * mm, "end": v(-38.72, 18.04) * mm});
            skLineSegment(sketch, "E273.7.7", {"start": v(-38.09, 17.85) * mm, "end": v(-38.72, 18.04) * mm});
            skArc(sketch, "E273.7.8", {"start": v(-39.68, 17.19) * mm, "mid": v(-39.54, 17.46) * mm, "end": v(-39.27, 17.61) * mm});
            skPoint(sketch, "E273.7.9", {"position": v(-38.32, 16.92) * mm});
            skArc(sketch, "E273.7.10", {"start": v(-38.7, 16.99) * mm, "mid": v(-38.58, 17.48) * mm, "end": v(-38.45, 17.96) * mm, "construction": true});
            skArc(sketch, "E273.7.11", {"start": v(-38.32, 16.92) * mm, "mid": v(-38.4, 16.44) * mm, "end": v(-38.47, 15.96) * mm});
            skPoint(sketch, "E273.7.12", {"position": v(-38.7, 16.99) * mm});
            skArc(sketch, "E273.7.13", {"start": v(-39.08, 16.32) * mm, "mid": v(-39.1, 16.18) * mm, "end": v(-39.12, 16.03) * mm});
            skArc(sketch, "E273.7.14", {"start": v(-38.95, 17.64) * mm, "mid": v(-38.86, 17.67) * mm, "end": v(-38.8, 17.76) * mm});
            skArc(sketch, "E273.7.15", {"start": v(-39.18, 16.48) * mm, "mid": v(-39.1, 16.42) * mm, "end": v(-39.08, 16.32) * mm});
            skArc(sketch, "E273.8.0", {"start": v(-39.58, 14.5) * mm, "mid": v(-39.43, 14.44) * mm, "end": v(-39.27, 14.4) * mm});
            skArc(sketch, "E273.8.1", {"start": v(-39.9, 15) * mm, "mid": v(-39.8, 14.7) * mm, "end": v(-39.58, 14.5) * mm});
            skArc(sketch, "E273.8.2", {"start": v(-38.51, 15) * mm, "mid": v(-38.5, 15.48) * mm, "end": v(-38.47, 15.96) * mm});
            skPoint(sketch, "E273.8.3", {"position": v(-39.14, 15) * mm});
            skArc(sketch, "E273.8.4", {"start": v(-39.58, 15.5) * mm, "mid": v(-39.43, 15.56) * mm, "end": v(-39.27, 15.6) * mm});
            skLineSegment(sketch, "E273.8.5", {"start": v(-38.47, 14.04) * mm, "end": v(-39.12, 13.97) * mm});
            skArc(sketch, "E273.8.6", {"start": v(-39.14, 15.73) * mm, "mid": v(-39.13, 15.88) * mm, "end": v(-39.12, 16.03) * mm});
            skLineSegment(sketch, "E273.8.7", {"start": v(-38.47, 15.96) * mm, "end": v(-39.12, 16.03) * mm});
            skArc(sketch, "E273.8.8", {"start": v(-39.9, 15) * mm, "mid": v(-39.8, 15.3) * mm, "end": v(-39.58, 15.5) * mm});
            skPoint(sketch, "E273.8.9", {"position": v(-38.51, 15) * mm});
            skArc(sketch, "E273.8.10", {"start": v(-38.89, 15) * mm, "mid": v(-38.88, 15.5) * mm, "end": v(-38.84, 16) * mm, "construction": true});
            skArc(sketch, "E273.8.11", {"start": v(-38.51, 15) * mm, "mid": v(-38.5, 14.52) * mm, "end": v(-38.47, 14.04) * mm});
            skPoint(sketch, "E273.8.12", {"position": v(-38.89, 15) * mm});
            skArc(sketch, "E273.8.13", {"start": v(-39.14, 14.27) * mm, "mid": v(-39.13, 14.12) * mm, "end": v(-39.12, 13.97) * mm});
            skArc(sketch, "E273.8.14", {"start": v(-39.27, 15.6) * mm, "mid": v(-39.18, 15.64) * mm, "end": v(-39.14, 15.73) * mm});
            skArc(sketch, "E273.8.15", {"start": v(-39.27, 14.4) * mm, "mid": v(-39.18, 14.36) * mm, "end": v(-39.14, 14.27) * mm});
            skArc(sketch, "E273.9.0", {"start": v(-39.27, 12.39) * mm, "mid": v(-39.12, 12.36) * mm, "end": v(-38.95, 12.36) * mm});
            skArc(sketch, "E273.9.1", {"start": v(-39.68, 12.81) * mm, "mid": v(-39.54, 12.54) * mm, "end": v(-39.27, 12.39) * mm});
            skArc(sketch, "E273.9.2", {"start": v(-38.32, 13.08) * mm, "mid": v(-38.4, 13.56) * mm, "end": v(-38.47, 14.04) * mm});
            skPoint(sketch, "E273.9.3", {"position": v(-38.94, 12.96) * mm});
            skArc(sketch, "E273.9.4", {"start": v(-39.47, 13.36) * mm, "mid": v(-39.33, 13.45) * mm, "end": v(-39.18, 13.52) * mm});
            skLineSegment(sketch, "E273.9.5", {"start": v(-38.09, 12.15) * mm, "end": v(-38.72, 11.96) * mm});
            skArc(sketch, "E273.9.6", {"start": v(-39.08, 13.68) * mm, "mid": v(-39.1, 13.82) * mm, "end": v(-39.12, 13.97) * mm});
            skLineSegment(sketch, "E273.9.7", {"start": v(-38.47, 14.04) * mm, "end": v(-39.12, 13.97) * mm});
            skArc(sketch, "E273.9.8", {"start": v(-39.68, 12.81) * mm, "mid": v(-39.65, 13.12) * mm, "end": v(-39.47, 13.36) * mm});
            skPoint(sketch, "E273.9.9", {"position": v(-38.32, 13.08) * mm});
            skArc(sketch, "E273.9.10", {"start": v(-38.7, 13.01) * mm, "mid": v(-38.78, 13.5) * mm, "end": v(-38.84, 14) * mm, "construction": true});
            skArc(sketch, "E273.9.11", {"start": v(-38.32, 13.08) * mm, "mid": v(-38.22, 12.61) * mm, "end": v(-38.09, 12.15) * mm});
            skPoint(sketch, "E273.9.12", {"position": v(-38.7, 13.01) * mm});
            skArc(sketch, "E273.9.13", {"start": v(-38.8, 12.24) * mm, "mid": v(-38.76, 12.1) * mm, "end": v(-38.72, 11.96) * mm});
            skArc(sketch, "E273.9.14", {"start": v(-39.18, 13.52) * mm, "mid": v(-39.1, 13.58) * mm, "end": v(-39.08, 13.68) * mm});
            skArc(sketch, "E273.9.15", {"start": v(-38.95, 12.36) * mm, "mid": v(-38.86, 12.33) * mm, "end": v(-38.8, 12.24) * mm});
            skArc(sketch, "E273.10.0", {"start": v(-38.56, 10.37) * mm, "mid": v(-38.4, 10.37) * mm, "end": v(-38.24, 10.4) * mm});
            skArc(sketch, "E273.10.1", {"start": v(-39.04, 10.71) * mm, "mid": v(-38.85, 10.47) * mm, "end": v(-38.56, 10.37) * mm});
            skArc(sketch, "E273.10.2", {"start": v(-37.76, 11.24) * mm, "mid": v(-37.94, 11.7) * mm, "end": v(-38.09, 12.15) * mm});
            skPoint(sketch, "E273.10.3", {"position": v(-38.35, 11) * mm});
            skArc(sketch, "E273.10.4", {"start": v(-38.94, 11.3) * mm, "mid": v(-38.83, 11.4) * mm, "end": v(-38.7, 11.5) * mm});
            skLineSegment(sketch, "E273.10.5", {"start": v(-37.35, 10.37) * mm, "end": v(-37.93, 10.06) * mm});
            skArc(sketch, "E273.10.6", {"start": v(-38.63, 11.67) * mm, "mid": v(-38.67, 11.82) * mm, "end": v(-38.72, 11.96) * mm});
            skLineSegment(sketch, "E273.10.7", {"start": v(-38.09, 12.15) * mm, "end": v(-38.72, 11.96) * mm});
            skArc(sketch, "E273.10.8", {"start": v(-39.04, 10.71) * mm, "mid": v(-39.07, 11.02) * mm, "end": v(-38.94, 11.3) * mm});
            skPoint(sketch, "E273.10.9", {"position": v(-37.76, 11.24) * mm});
            skArc(sketch, "E273.10.10", {"start": v(-38.11, 11.1) * mm, "mid": v(-38.3, 11.56) * mm, "end": v(-38.45, 12.04) * mm, "construction": true});
            skArc(sketch, "E273.10.11", {"start": v(-37.76, 11.24) * mm, "mid": v(-37.57, 10.8) * mm, "end": v(-37.35, 10.37) * mm});
            skPoint(sketch, "E273.10.12", {"position": v(-38.11, 11.1) * mm});
            skArc(sketch, "E273.10.13", {"start": v(-38.07, 10.33) * mm, "mid": v(-38, 10.2) * mm, "end": v(-37.93, 10.06) * mm});
            skArc(sketch, "E273.10.14", {"start": v(-38.7, 11.5) * mm, "mid": v(-38.63, 11.57) * mm, "end": v(-38.63, 11.67) * mm});
            skArc(sketch, "E273.10.15", {"start": v(-38.24, 10.4) * mm, "mid": v(-38.14, 10.4) * mm, "end": v(-38.07, 10.33) * mm});
            skArc(sketch, "E273.11.0", {"start": v(-37.47, 8.53) * mm, "mid": v(-37.31, 8.57) * mm, "end": v(-37.16, 8.63) * mm});
            skArc(sketch, "E273.11.1", {"start": v(-38, 8.78) * mm, "mid": v(-37.77, 8.58) * mm, "end": v(-37.47, 8.53) * mm});
            skArc(sketch, "E273.11.2", {"start": v(-36.86, 9.54) * mm, "mid": v(-37.11, 9.95) * mm, "end": v(-37.35, 10.37) * mm});
            skPoint(sketch, "E273.11.3", {"position": v(-37.38, 9.2) * mm});
            skArc(sketch, "E273.11.4", {"start": v(-38.02, 9.36) * mm, "mid": v(-37.93, 9.5) * mm, "end": v(-37.82, 9.61) * mm});
            skLineSegment(sketch, "E273.11.5", {"start": v(-36.28, 8.77) * mm, "end": v(-36.79, 8.35) * mm});
            skArc(sketch, "E273.11.6", {"start": v(-37.79, 9.8) * mm, "mid": v(-37.86, 9.93) * mm, "end": v(-37.93, 10.06) * mm});
            skLineSegment(sketch, "E273.11.7", {"start": v(-37.35, 10.37) * mm, "end": v(-37.93, 10.06) * mm});
            skArc(sketch, "E273.11.8", {"start": v(-38, 8.78) * mm, "mid": v(-38.1, 9.07) * mm, "end": v(-38.02, 9.36) * mm});
            skPoint(sketch, "E273.11.9", {"position": v(-36.86, 9.54) * mm});
            skArc(sketch, "E273.11.10", {"start": v(-37.17, 9.33) * mm, "mid": v(-37.44, 9.76) * mm, "end": v(-37.68, 10.2) * mm, "construction": true});
            skArc(sketch, "E273.11.11", {"start": v(-36.86, 9.54) * mm, "mid": v(-36.58, 9.15) * mm, "end": v(-36.28, 8.77) * mm});
            skPoint(sketch, "E273.11.12", {"position": v(-37.17, 9.33) * mm});
            skArc(sketch, "E273.11.13", {"start": v(-36.98, 8.59) * mm, "mid": v(-36.88, 8.47) * mm, "end": v(-36.79, 8.35) * mm});
            skArc(sketch, "E273.11.14", {"start": v(-37.82, 9.61) * mm, "mid": v(-37.77, 9.7) * mm, "end": v(-37.79, 9.8) * mm});
            skArc(sketch, "E273.11.15", {"start": v(-37.16, 8.63) * mm, "mid": v(-37.06, 8.64) * mm, "end": v(-36.98, 8.59) * mm});
            skArc(sketch, "E273.12.0", {"start": v(-36.04, 6.95) * mm, "mid": v(-35.89, 7) * mm, "end": v(-35.75, 7.1) * mm});
            skArc(sketch, "E273.12.1", {"start": v(-36.61, 7.08) * mm, "mid": v(-36.34, 6.93) * mm, "end": v(-36.04, 6.95) * mm});
            skArc(sketch, "E273.12.2", {"start": v(-35.64, 8.05) * mm, "mid": v(-35.97, 8.4) * mm, "end": v(-36.28, 8.77) * mm});
            skPoint(sketch, "E273.12.3", {"position": v(-36.08, 7.6) * mm});
            skArc(sketch, "E273.12.4", {"start": v(-36.74, 7.65) * mm, "mid": v(-36.68, 7.8) * mm, "end": v(-36.6, 7.93) * mm});
            skLineSegment(sketch, "E273.12.5", {"start": v(-34.92, 7.4) * mm, "end": v(-35.34, 6.9) * mm});
            skArc(sketch, "E273.12.6", {"start": v(-36.6, 8.12) * mm, "mid": v(-36.7, 8.24) * mm, "end": v(-36.79, 8.35) * mm});
            skLineSegment(sketch, "E273.12.7", {"start": v(-36.28, 8.77) * mm, "end": v(-36.79, 8.35) * mm});
            skArc(sketch, "E273.12.8", {"start": v(-36.61, 7.08) * mm, "mid": v(-36.76, 7.35) * mm, "end": v(-36.74, 7.65) * mm});
            skPoint(sketch, "E273.12.9", {"position": v(-35.64, 8.05) * mm});
            skArc(sketch, "E273.12.10", {"start": v(-35.9, 7.79) * mm, "mid": v(-36.25, 8.15) * mm, "end": v(-36.57, 8.53) * mm, "construction": true});
            skArc(sketch, "E273.12.11", {"start": v(-35.64, 8.05) * mm, "mid": v(-35.29, 7.72) * mm, "end": v(-34.92, 7.4) * mm});
            skPoint(sketch, "E273.12.12", {"position": v(-35.9, 7.79) * mm});
            skArc(sketch, "E273.12.13", {"start": v(-35.56, 7.1) * mm, "mid": v(-35.45, 7) * mm, "end": v(-35.34, 6.9) * mm});
            skArc(sketch, "E273.12.14", {"start": v(-36.6, 7.93) * mm, "mid": v(-36.56, 8.03) * mm, "end": v(-36.6, 8.12) * mm});
            skArc(sketch, "E273.12.15", {"start": v(-35.75, 7.1) * mm, "mid": v(-35.66, 7.13) * mm, "end": v(-35.56, 7.1) * mm});
            skArc(sketch, "E273.13.0", {"start": v(-34.33, 5.67) * mm, "mid": v(-34.2, 5.76) * mm, "end": v(-34.08, 5.87) * mm});
            skArc(sketch, "E273.13.1", {"start": v(-34.91, 5.68) * mm, "mid": v(-34.62, 5.6) * mm, "end": v(-34.33, 5.67) * mm});
            skArc(sketch, "E273.13.2", {"start": v(-34.15, 6.83) * mm, "mid": v(-34.54, 7.1) * mm, "end": v(-34.92, 7.4) * mm});
            skPoint(sketch, "E273.13.3", {"position": v(-34.5, 6.3) * mm});
            skArc(sketch, "E273.13.4", {"start": v(-35.15, 6.22) * mm, "mid": v(-35.12, 6.38) * mm, "end": v(-35.06, 6.53) * mm});
            skLineSegment(sketch, "E273.13.5", {"start": v(-33.32, 6.34) * mm, "end": v(-33.63, 5.76) * mm});
            skArc(sketch, "E273.13.6", {"start": v(-35.1, 6.71) * mm, "mid": v(-35.22, 6.8) * mm, "end": v(-35.34, 6.9) * mm});
            skLineSegment(sketch, "E273.13.7", {"start": v(-34.92, 7.4) * mm, "end": v(-35.34, 6.9) * mm});
            skArc(sketch, "E273.13.8", {"start": v(-34.91, 5.68) * mm, "mid": v(-35.11, 5.92) * mm, "end": v(-35.15, 6.22) * mm});
            skPoint(sketch, "E273.13.9", {"position": v(-34.15, 6.83) * mm});
            skArc(sketch, "E273.13.10", {"start": v(-34.36, 6.52) * mm, "mid": v(-34.76, 6.8) * mm, "end": v(-35.16, 7.12) * mm, "construction": true});
            skArc(sketch, "E273.13.11", {"start": v(-34.15, 6.83) * mm, "mid": v(-33.74, 6.57) * mm, "end": v(-33.32, 6.34) * mm});
            skPoint(sketch, "E273.13.12", {"position": v(-34.36, 6.52) * mm});
            skArc(sketch, "E273.13.13", {"start": v(-33.89, 5.9) * mm, "mid": v(-33.76, 5.83) * mm, "end": v(-33.63, 5.76) * mm});
            skArc(sketch, "E273.13.14", {"start": v(-35.06, 6.53) * mm, "mid": v(-35.05, 6.63) * mm, "end": v(-35.1, 6.71) * mm});
            skArc(sketch, "E273.13.15", {"start": v(-34.08, 5.87) * mm, "mid": v(-33.99, 5.92) * mm, "end": v(-33.89, 5.9) * mm});
            skArc(sketch, "E273.14.0", {"start": v(-32.4, 4.75) * mm, "mid": v(-32.28, 4.86) * mm, "end": v(-32.2, 5) * mm});
            skArc(sketch, "E273.14.1", {"start": v(-32.98, 4.65) * mm, "mid": v(-32.67, 4.61) * mm, "end": v(-32.4, 4.75) * mm});
            skArc(sketch, "E273.14.2", {"start": v(-32.45, 5.92) * mm, "mid": v(-32.89, 6.12) * mm, "end": v(-33.32, 6.34) * mm});
            skPoint(sketch, "E273.14.3", {"position": v(-32.69, 5.34) * mm});
            skArc(sketch, "E273.14.4", {"start": v(-33.32, 5.13) * mm, "mid": v(-33.31, 5.29) * mm, "end": v(-33.29, 5.45) * mm});
            skLineSegment(sketch, "E273.14.5", {"start": v(-31.54, 5.6) * mm, "end": v(-31.73, 4.97) * mm});
            skArc(sketch, "E273.14.6", {"start": v(-33.36, 5.62) * mm, "mid": v(-33.5, 5.69) * mm, "end": v(-33.63, 5.76) * mm});
            skLineSegment(sketch, "E273.14.7", {"start": v(-33.32, 6.34) * mm, "end": v(-33.63, 5.76) * mm});
            skArc(sketch, "E273.14.8", {"start": v(-32.98, 4.65) * mm, "mid": v(-33.22, 4.84) * mm, "end": v(-33.32, 5.13) * mm});
            skPoint(sketch, "E273.14.9", {"position": v(-32.45, 5.92) * mm});
            skArc(sketch, "E273.14.10", {"start": v(-32.6, 5.58) * mm, "mid": v(-33.05, 5.78) * mm, "end": v(-33.5, 6) * mm, "construction": true});
            skArc(sketch, "E273.14.11", {"start": v(-32.45, 5.92) * mm, "mid": v(-32, 5.75) * mm, "end": v(-31.54, 5.6) * mm});
            skPoint(sketch, "E273.14.12", {"position": v(-32.6, 5.58) * mm});
            skArc(sketch, "E273.14.13", {"start": v(-32.01, 5.06) * mm, "mid": v(-31.87, 5.02) * mm, "end": v(-31.73, 4.97) * mm});
            skArc(sketch, "E273.14.14", {"start": v(-33.29, 5.45) * mm, "mid": v(-33.3, 5.55) * mm, "end": v(-33.36, 5.62) * mm});
            skArc(sketch, "E273.14.15", {"start": v(-32.2, 5) * mm, "mid": v(-32.12, 5.06) * mm, "end": v(-32.01, 5.06) * mm});
            skArc(sketch, "E273.15.0", {"start": v(-30.32, 4.22) * mm, "mid": v(-30.24, 4.36) * mm, "end": v(-30.17, 4.5) * mm});
            skArc(sketch, "E273.15.1", {"start": v(-30.87, 4.01) * mm, "mid": v(-30.57, 4.04) * mm, "end": v(-30.32, 4.22) * mm});
            skArc(sketch, "E273.15.2", {"start": v(-30.6, 5.36) * mm, "mid": v(-31.08, 5.47) * mm, "end": v(-31.54, 5.6) * mm});
            skPoint(sketch, "E273.15.3", {"position": v(-30.73, 4.75) * mm});
            skArc(sketch, "E273.15.4", {"start": v(-31.3, 4.41) * mm, "mid": v(-31.33, 4.57) * mm, "end": v(-31.33, 4.73) * mm});
            skLineSegment(sketch, "E273.15.5", {"start": v(-29.65, 5.22) * mm, "end": v(-29.72, 4.57) * mm});
            skArc(sketch, "E273.15.6", {"start": v(-31.44, 4.89) * mm, "mid": v(-31.59, 4.93) * mm, "end": v(-31.73, 4.97) * mm});
            skLineSegment(sketch, "E273.15.7", {"start": v(-31.54, 5.6) * mm, "end": v(-31.73, 4.97) * mm});
            skArc(sketch, "E273.15.8", {"start": v(-30.87, 4.01) * mm, "mid": v(-31.15, 4.15) * mm, "end": v(-31.3, 4.41) * mm});
            skPoint(sketch, "E273.15.9", {"position": v(-30.6, 5.36) * mm});
            skArc(sketch, "E273.15.10", {"start": v(-30.68, 5) * mm, "mid": v(-31.17, 5.1) * mm, "end": v(-31.65, 5.24) * mm, "construction": true});
            skArc(sketch, "E273.15.11", {"start": v(-30.6, 5.36) * mm, "mid": v(-30.13, 5.28) * mm, "end": v(-29.65, 5.22) * mm});
            skPoint(sketch, "E273.15.12", {"position": v(-30.68, 5) * mm});
            skArc(sketch, "E273.15.13", {"start": v(-30.01, 4.6) * mm, "mid": v(-29.86, 4.59) * mm, "end": v(-29.72, 4.57) * mm});
            skArc(sketch, "E273.15.14", {"start": v(-31.33, 4.73) * mm, "mid": v(-31.36, 4.83) * mm, "end": v(-31.44, 4.89) * mm});
            skArc(sketch, "E273.15.15", {"start": v(-30.17, 4.5) * mm, "mid": v(-30.11, 4.58) * mm, "end": v(-30.01, 4.6) * mm});
            skArc(sketch, "E273.16.0", {"start": v(-28.19, 4.1) * mm, "mid": v(-28.13, 4.26) * mm, "end": v(-28.1, 4.42) * mm});
            skArc(sketch, "E273.16.1", {"start": v(-28.69, 3.8) * mm, "mid": v(-28.4, 3.88) * mm, "end": v(-28.19, 4.1) * mm});
            skArc(sketch, "E273.16.2", {"start": v(-28.69, 5.18) * mm, "mid": v(-29.17, 5.19) * mm, "end": v(-29.65, 5.22) * mm});
            skPoint(sketch, "E273.16.3", {"position": v(-28.69, 4.55) * mm});
            skArc(sketch, "E273.16.4", {"start": v(-29.19, 4.1) * mm, "mid": v(-29.25, 4.26) * mm, "end": v(-29.28, 4.42) * mm});
            skLineSegment(sketch, "E273.16.5", {"start": v(-27.73, 5.22) * mm, "end": v(-27.66, 4.57) * mm});
            skArc(sketch, "E273.16.6", {"start": v(-29.42, 4.55) * mm, "mid": v(-29.57, 4.56) * mm, "end": v(-29.72, 4.57) * mm});
            skLineSegment(sketch, "E273.16.7", {"start": v(-29.65, 5.22) * mm, "end": v(-29.72, 4.57) * mm});
            skArc(sketch, "E273.16.8", {"start": v(-28.69, 3.8) * mm, "mid": v(-28.98, 3.88) * mm, "end": v(-29.19, 4.1) * mm});
            skPoint(sketch, "E273.16.9", {"position": v(-28.69, 5.18) * mm});
            skArc(sketch, "E273.16.10", {"start": v(-28.69, 4.8) * mm, "mid": v(-29.19, 4.81) * mm, "end": v(-29.69, 4.85) * mm, "construction": true});
            skArc(sketch, "E273.16.11", {"start": v(-28.69, 5.18) * mm, "mid": v(-28.2, 5.19) * mm, "end": v(-27.73, 5.22) * mm});
            skPoint(sketch, "E273.16.12", {"position": v(-28.69, 4.8) * mm});
            skArc(sketch, "E273.16.13", {"start": v(-27.96, 4.55) * mm, "mid": v(-27.8, 4.56) * mm, "end": v(-27.66, 4.57) * mm});
            skArc(sketch, "E273.16.14", {"start": v(-29.28, 4.42) * mm, "mid": v(-29.33, 4.5) * mm, "end": v(-29.42, 4.55) * mm});
            skArc(sketch, "E273.16.15", {"start": v(-28.1, 4.42) * mm, "mid": v(-28.05, 4.5) * mm, "end": v(-27.96, 4.55) * mm});
            skArc(sketch, "E273.17.0", {"start": v(-26.07, 4.41) * mm, "mid": v(-26.05, 4.57) * mm, "end": v(-26.04, 4.73) * mm});
            skArc(sketch, "E273.17.1", {"start": v(-26.5, 4.01) * mm, "mid": v(-26.23, 4.15) * mm, "end": v(-26.07, 4.41) * mm});
            skArc(sketch, "E273.17.2", {"start": v(-26.77, 5.36) * mm, "mid": v(-27.25, 5.28) * mm, "end": v(-27.73, 5.22) * mm});
            skPoint(sketch, "E273.17.3", {"position": v(-26.65, 4.75) * mm});
            skArc(sketch, "E273.17.4", {"start": v(-27.05, 4.22) * mm, "mid": v(-27.14, 4.36) * mm, "end": v(-27.2, 4.5) * mm});
            skLineSegment(sketch, "E273.17.5", {"start": v(-25.84, 5.6) * mm, "end": v(-25.65, 4.97) * mm});
            skArc(sketch, "E273.17.6", {"start": v(-27.36, 4.6) * mm, "mid": v(-27.51, 4.59) * mm, "end": v(-27.66, 4.57) * mm});
            skLineSegment(sketch, "E273.17.7", {"start": v(-27.73, 5.22) * mm, "end": v(-27.66, 4.57) * mm});
            skArc(sketch, "E273.17.8", {"start": v(-26.5, 4.01) * mm, "mid": v(-26.8, 4.04) * mm, "end": v(-27.05, 4.22) * mm});
            skPoint(sketch, "E273.17.9", {"position": v(-26.77, 5.36) * mm});
            skArc(sketch, "E273.17.10", {"start": v(-26.7, 5) * mm, "mid": v(-27.2, 4.91) * mm, "end": v(-27.69, 4.85) * mm, "construction": true});
            skArc(sketch, "E273.17.11", {"start": v(-26.77, 5.36) * mm, "mid": v(-26.3, 5.47) * mm, "end": v(-25.84, 5.6) * mm});
            skPoint(sketch, "E273.17.12", {"position": v(-26.7, 5) * mm});
            skArc(sketch, "E273.17.13", {"start": v(-25.93, 4.89) * mm, "mid": v(-25.79, 4.93) * mm, "end": v(-25.65, 4.97) * mm});
            skArc(sketch, "E273.17.14", {"start": v(-27.2, 4.5) * mm, "mid": v(-27.27, 4.58) * mm, "end": v(-27.36, 4.6) * mm});
            skArc(sketch, "E273.17.15", {"start": v(-26.04, 4.73) * mm, "mid": v(-26.02, 4.83) * mm, "end": v(-25.93, 4.89) * mm});
            skArc(sketch, "E273.18.0", {"start": v(-24.06, 5.13) * mm, "mid": v(-24.06, 5.29) * mm, "end": v(-24.1, 5.45) * mm});
            skArc(sketch, "E273.18.1", {"start": v(-24.4, 4.65) * mm, "mid": v(-24.16, 4.84) * mm, "end": v(-24.06, 5.13) * mm});
            skArc(sketch, "E273.18.2", {"start": v(-24.93, 5.92) * mm, "mid": v(-25.38, 5.75) * mm, "end": v(-25.84, 5.6) * mm});
            skPoint(sketch, "E273.18.3", {"position": v(-24.69, 5.34) * mm});
            skArc(sketch, "E273.18.4", {"start": v(-24.98, 4.75) * mm, "mid": v(-25.1, 4.86) * mm, "end": v(-25.18, 5) * mm});
            skLineSegment(sketch, "E273.18.5", {"start": v(-24.06, 6.34) * mm, "end": v(-23.75, 5.76) * mm});
            skArc(sketch, "E273.18.6", {"start": v(-25.36, 5.06) * mm, "mid": v(-25.5, 5.02) * mm, "end": v(-25.65, 4.97) * mm});
            skLineSegment(sketch, "E273.18.7", {"start": v(-25.84, 5.6) * mm, "end": v(-25.65, 4.97) * mm});
            skArc(sketch, "E273.18.8", {"start": v(-24.4, 4.65) * mm, "mid": v(-24.7, 4.61) * mm, "end": v(-24.98, 4.75) * mm});
            skPoint(sketch, "E273.18.9", {"position": v(-24.93, 5.92) * mm});
            skArc(sketch, "E273.18.10", {"start": v(-24.79, 5.58) * mm, "mid": v(-25.25, 5.4) * mm, "end": v(-25.73, 5.24) * mm, "construction": true});
            skArc(sketch, "E273.18.11", {"start": v(-24.93, 5.92) * mm, "mid": v(-24.49, 6.12) * mm, "end": v(-24.06, 6.34) * mm});
            skPoint(sketch, "E273.18.12", {"position": v(-24.79, 5.58) * mm});
            skArc(sketch, "E273.18.13", {"start": v(-24.01, 5.62) * mm, "mid": v(-23.88, 5.69) * mm, "end": v(-23.75, 5.76) * mm});
            skArc(sketch, "E273.18.14", {"start": v(-25.18, 5) * mm, "mid": v(-25.26, 5.06) * mm, "end": v(-25.36, 5.06) * mm});
            skArc(sketch, "E273.18.15", {"start": v(-24.1, 5.45) * mm, "mid": v(-24.08, 5.55) * mm, "end": v(-24.01, 5.62) * mm});
            skArc(sketch, "E273.19.0", {"start": v(-22.22, 6.22) * mm, "mid": v(-22.26, 6.38) * mm, "end": v(-22.32, 6.53) * mm});
            skArc(sketch, "E273.19.1", {"start": v(-22.46, 5.68) * mm, "mid": v(-22.27, 5.92) * mm, "end": v(-22.22, 6.22) * mm});
            skArc(sketch, "E273.19.2", {"start": v(-23.23, 6.83) * mm, "mid": v(-23.64, 6.57) * mm, "end": v(-24.06, 6.34) * mm});
            skPoint(sketch, "E273.19.3", {"position": v(-22.88, 6.3) * mm});
            skArc(sketch, "E273.19.4", {"start": v(-23.05, 5.67) * mm, "mid": v(-23.18, 5.76) * mm, "end": v(-23.3, 5.87) * mm});
            skLineSegment(sketch, "E273.19.5", {"start": v(-22.46, 7.4) * mm, "end": v(-22.04, 6.9) * mm});
            skArc(sketch, "E273.19.6", {"start": v(-23.49, 5.9) * mm, "mid": v(-23.62, 5.83) * mm, "end": v(-23.75, 5.76) * mm});
            skLineSegment(sketch, "E273.19.7", {"start": v(-24.06, 6.34) * mm, "end": v(-23.75, 5.76) * mm});
            skArc(sketch, "E273.19.8", {"start": v(-22.46, 5.68) * mm, "mid": v(-22.76, 5.6) * mm, "end": v(-23.05, 5.67) * mm});
            skPoint(sketch, "E273.19.9", {"position": v(-23.23, 6.83) * mm});
            skArc(sketch, "E273.19.10", {"start": v(-23.02, 6.52) * mm, "mid": v(-23.44, 6.25) * mm, "end": v(-23.88, 6) * mm, "construction": true});
            skArc(sketch, "E273.19.11", {"start": v(-23.23, 6.83) * mm, "mid": v(-22.84, 7.1) * mm, "end": v(-22.46, 7.4) * mm});
            skPoint(sketch, "E273.19.12", {"position": v(-23.02, 6.52) * mm});
            skArc(sketch, "E273.19.13", {"start": v(-22.27, 6.71) * mm, "mid": v(-22.16, 6.8) * mm, "end": v(-22.04, 6.9) * mm});
            skArc(sketch, "E273.19.14", {"start": v(-23.3, 5.87) * mm, "mid": v(-23.39, 5.92) * mm, "end": v(-23.49, 5.9) * mm});
            skArc(sketch, "E273.19.15", {"start": v(-22.32, 6.53) * mm, "mid": v(-22.33, 6.63) * mm, "end": v(-22.27, 6.71) * mm});
            skArc(sketch, "E273.20.0", {"start": v(-20.63, 7.65) * mm, "mid": v(-20.7, 7.8) * mm, "end": v(-20.79, 7.93) * mm});
            skArc(sketch, "E273.20.1", {"start": v(-20.77, 7.08) * mm, "mid": v(-20.62, 7.35) * mm, "end": v(-20.63, 7.65) * mm});
            skArc(sketch, "E273.20.2", {"start": v(-21.74, 8.05) * mm, "mid": v(-22.1, 7.72) * mm, "end": v(-22.46, 7.4) * mm});
            skPoint(sketch, "E273.20.3", {"position": v(-21.3, 7.6) * mm});
            skArc(sketch, "E273.20.4", {"start": v(-21.34, 6.95) * mm, "mid": v(-21.49, 7) * mm, "end": v(-21.62, 7.1) * mm});
            skLineSegment(sketch, "E273.20.5", {"start": v(-21.1, 8.77) * mm, "end": v(-20.59, 8.35) * mm});
            skArc(sketch, "E273.20.6", {"start": v(-21.81, 7.1) * mm, "mid": v(-21.93, 7) * mm, "end": v(-22.04, 6.9) * mm});
            skLineSegment(sketch, "E273.20.7", {"start": v(-22.46, 7.4) * mm, "end": v(-22.04, 6.9) * mm});
            skArc(sketch, "E273.20.8", {"start": v(-20.77, 7.08) * mm, "mid": v(-21.03, 6.93) * mm, "end": v(-21.34, 6.95) * mm});
            skPoint(sketch, "E273.20.9", {"position": v(-21.74, 8.05) * mm});
            skArc(sketch, "E273.20.10", {"start": v(-21.48, 7.79) * mm, "mid": v(-21.84, 7.44) * mm, "end": v(-22.22, 7.12) * mm, "construction": true});
            skArc(sketch, "E273.20.11", {"start": v(-21.74, 8.05) * mm, "mid": v(-21.4, 8.4) * mm, "end": v(-21.1, 8.77) * mm});
            skPoint(sketch, "E273.20.12", {"position": v(-21.48, 7.79) * mm});
            skArc(sketch, "E273.20.13", {"start": v(-20.78, 8.12) * mm, "mid": v(-20.68, 8.24) * mm, "end": v(-20.59, 8.35) * mm});
            skArc(sketch, "E273.20.14", {"start": v(-21.62, 7.1) * mm, "mid": v(-21.72, 7.13) * mm, "end": v(-21.81, 7.1) * mm});
            skArc(sketch, "E273.20.15", {"start": v(-20.79, 7.93) * mm, "mid": v(-20.82, 8.03) * mm, "end": v(-20.78, 8.12) * mm});
            skArc(sketch, "E273.21.0", {"start": v(-19.35, 9.36) * mm, "mid": v(-19.45, 9.5) * mm, "end": v(-19.56, 9.61) * mm});
            skArc(sketch, "E273.21.1", {"start": v(-19.37, 8.78) * mm, "mid": v(-19.28, 9.07) * mm, "end": v(-19.35, 9.36) * mm});
            skArc(sketch, "E273.21.2", {"start": v(-20.52, 9.54) * mm, "mid": v(-20.8, 9.15) * mm, "end": v(-21.1, 8.77) * mm});
            skPoint(sketch, "E273.21.3", {"position": v(-20, 9.2) * mm});
            skArc(sketch, "E273.21.4", {"start": v(-19.9, 8.53) * mm, "mid": v(-20.07, 8.57) * mm, "end": v(-20.22, 8.63) * mm});
            skLineSegment(sketch, "E273.21.5", {"start": v(-20.02, 10.37) * mm, "end": v(-19.45, 10.06) * mm});
            skArc(sketch, "E273.21.6", {"start": v(-20.4, 8.59) * mm, "mid": v(-20.5, 8.47) * mm, "end": v(-20.59, 8.35) * mm});
            skLineSegment(sketch, "E273.21.7", {"start": v(-21.1, 8.77) * mm, "end": v(-20.59, 8.35) * mm});
            skArc(sketch, "E273.21.8", {"start": v(-19.37, 8.78) * mm, "mid": v(-19.6, 8.58) * mm, "end": v(-19.9, 8.53) * mm});
            skPoint(sketch, "E273.21.9", {"position": v(-20.52, 9.54) * mm});
            skArc(sketch, "E273.21.10", {"start": v(-20.2, 9.33) * mm, "mid": v(-20.5, 8.92) * mm, "end": v(-20.8, 8.53) * mm, "construction": true});
            skArc(sketch, "E273.21.11", {"start": v(-20.52, 9.54) * mm, "mid": v(-20.26, 9.95) * mm, "end": v(-20.02, 10.37) * mm});
            skPoint(sketch, "E273.21.12", {"position": v(-20.2, 9.33) * mm});
            skArc(sketch, "E273.21.13", {"start": v(-19.6, 9.8) * mm, "mid": v(-19.52, 9.93) * mm, "end": v(-19.45, 10.06) * mm});
            skArc(sketch, "E273.21.14", {"start": v(-20.22, 8.63) * mm, "mid": v(-20.32, 8.64) * mm, "end": v(-20.4, 8.59) * mm});
            skArc(sketch, "E273.21.15", {"start": v(-19.56, 9.61) * mm, "mid": v(-19.6, 9.7) * mm, "end": v(-19.6, 9.8) * mm});
            skArc(sketch, "E273.22.0", {"start": v(-18.43, 11.3) * mm, "mid": v(-18.55, 11.4) * mm, "end": v(-18.68, 11.5) * mm});
            skArc(sketch, "E273.22.1", {"start": v(-18.34, 10.71) * mm, "mid": v(-18.3, 11.02) * mm, "end": v(-18.43, 11.3) * mm});
            skArc(sketch, "E273.22.2", {"start": v(-19.61, 11.24) * mm, "mid": v(-19.8, 10.8) * mm, "end": v(-20.02, 10.37) * mm});
            skPoint(sketch, "E273.22.3", {"position": v(-19.03, 11) * mm});
            skArc(sketch, "E273.22.4", {"start": v(-18.82, 10.37) * mm, "mid": v(-18.98, 10.37) * mm, "end": v(-19.14, 10.4) * mm});
            skLineSegment(sketch, "E273.22.5", {"start": v(-19.29, 12.15) * mm, "end": v(-18.66, 11.96) * mm});
            skArc(sketch, "E273.22.6", {"start": v(-19.3, 10.33) * mm, "mid": v(-19.38, 10.2) * mm, "end": v(-19.45, 10.06) * mm});
            skLineSegment(sketch, "E273.22.7", {"start": v(-20.02, 10.37) * mm, "end": v(-19.45, 10.06) * mm});
            skArc(sketch, "E273.22.8", {"start": v(-18.34, 10.71) * mm, "mid": v(-18.53, 10.47) * mm, "end": v(-18.82, 10.37) * mm});
            skPoint(sketch, "E273.22.9", {"position": v(-19.61, 11.24) * mm});
            skArc(sketch, "E273.22.10", {"start": v(-19.26, 11.1) * mm, "mid": v(-19.47, 10.64) * mm, "end": v(-19.7, 10.2) * mm, "construction": true});
            skArc(sketch, "E273.22.11", {"start": v(-19.61, 11.24) * mm, "mid": v(-19.44, 11.7) * mm, "end": v(-19.29, 12.15) * mm});
            skPoint(sketch, "E273.22.12", {"position": v(-19.26, 11.1) * mm});
            skArc(sketch, "E273.22.13", {"start": v(-18.75, 11.67) * mm, "mid": v(-18.7, 11.82) * mm, "end": v(-18.66, 11.96) * mm});
            skArc(sketch, "E273.22.14", {"start": v(-19.14, 10.4) * mm, "mid": v(-19.24, 10.4) * mm, "end": v(-19.3, 10.33) * mm});
            skArc(sketch, "E273.22.15", {"start": v(-18.68, 11.5) * mm, "mid": v(-18.75, 11.57) * mm, "end": v(-18.75, 11.67) * mm});
            skArc(sketch, "E273.23.0", {"start": v(-17.9, 13.36) * mm, "mid": v(-18.04, 13.45) * mm, "end": v(-18.2, 13.52) * mm});
            skArc(sketch, "E273.23.1", {"start": v(-17.7, 12.81) * mm, "mid": v(-17.73, 13.12) * mm, "end": v(-17.9, 13.36) * mm});
            skArc(sketch, "E273.23.2", {"start": v(-19.05, 13.08) * mm, "mid": v(-19.16, 12.61) * mm, "end": v(-19.29, 12.15) * mm});
            skPoint(sketch, "E273.23.3", {"position": v(-18.44, 12.96) * mm});
            skArc(sketch, "E273.23.4", {"start": v(-18.1, 12.39) * mm, "mid": v(-18.26, 12.36) * mm, "end": v(-18.42, 12.36) * mm});
            skLineSegment(sketch, "E273.23.5", {"start": v(-18.91, 14.04) * mm, "end": v(-18.26, 13.97) * mm});
            skArc(sketch, "E273.23.6", {"start": v(-18.58, 12.24) * mm, "mid": v(-18.62, 12.1) * mm, "end": v(-18.66, 11.96) * mm});
            skLineSegment(sketch, "E273.23.7", {"start": v(-19.29, 12.15) * mm, "end": v(-18.66, 11.96) * mm});
            skArc(sketch, "E273.23.8", {"start": v(-17.7, 12.81) * mm, "mid": v(-17.84, 12.54) * mm, "end": v(-18.1, 12.39) * mm});
            skPoint(sketch, "E273.23.9", {"position": v(-19.05, 13.08) * mm});
            skArc(sketch, "E273.23.10", {"start": v(-18.68, 13.01) * mm, "mid": v(-18.8, 12.52) * mm, "end": v(-18.93, 12.04) * mm, "construction": true});
            skArc(sketch, "E273.23.11", {"start": v(-19.05, 13.08) * mm, "mid": v(-18.97, 13.56) * mm, "end": v(-18.91, 14.04) * mm});
            skPoint(sketch, "E273.23.12", {"position": v(-18.68, 13.01) * mm});
            skArc(sketch, "E273.23.13", {"start": v(-18.3, 13.68) * mm, "mid": v(-18.28, 13.82) * mm, "end": v(-18.26, 13.97) * mm});
            skArc(sketch, "E273.23.14", {"start": v(-18.42, 12.36) * mm, "mid": v(-18.52, 12.33) * mm, "end": v(-18.58, 12.24) * mm});
            skArc(sketch, "E273.23.15", {"start": v(-18.2, 13.52) * mm, "mid": v(-18.27, 13.58) * mm, "end": v(-18.3, 13.68) * mm});
            skArc(sketch, "E273.24.0", {"start": v(-17.8, 15.5) * mm, "mid": v(-17.95, 15.56) * mm, "end": v(-18.1, 15.6) * mm});
            skArc(sketch, "E273.24.1", {"start": v(-17.48, 15) * mm, "mid": v(-17.57, 15.3) * mm, "end": v(-17.8, 15.5) * mm});
            skArc(sketch, "E273.24.2", {"start": v(-18.86, 15) * mm, "mid": v(-18.88, 14.52) * mm, "end": v(-18.91, 14.04) * mm});
            skPoint(sketch, "E273.24.3", {"position": v(-18.23, 15) * mm});
            skArc(sketch, "E273.24.4", {"start": v(-17.8, 14.5) * mm, "mid": v(-17.95, 14.44) * mm, "end": v(-18.1, 14.4) * mm});
            skLineSegment(sketch, "E273.24.5", {"start": v(-18.91, 15.96) * mm, "end": v(-18.26, 16.03) * mm});
            skArc(sketch, "E273.24.6", {"start": v(-18.23, 14.27) * mm, "mid": v(-18.25, 14.12) * mm, "end": v(-18.26, 13.97) * mm});
            skLineSegment(sketch, "E273.24.7", {"start": v(-18.91, 14.04) * mm, "end": v(-18.26, 13.97) * mm});
            skArc(sketch, "E273.24.8", {"start": v(-17.48, 15) * mm, "mid": v(-17.57, 14.7) * mm, "end": v(-17.8, 14.5) * mm});
            skPoint(sketch, "E273.24.9", {"position": v(-18.86, 15) * mm});
            skArc(sketch, "E273.24.10", {"start": v(-18.49, 15) * mm, "mid": v(-18.5, 14.5) * mm, "end": v(-18.54, 14) * mm, "construction": true});
            skArc(sketch, "E273.24.11", {"start": v(-18.86, 15) * mm, "mid": v(-18.88, 15.48) * mm, "end": v(-18.91, 15.96) * mm});
            skPoint(sketch, "E273.24.12", {"position": v(-18.49, 15) * mm});
            skArc(sketch, "E273.24.13", {"start": v(-18.23, 15.73) * mm, "mid": v(-18.25, 15.88) * mm, "end": v(-18.26, 16.03) * mm});
            skArc(sketch, "E273.24.14", {"start": v(-18.1, 14.4) * mm, "mid": v(-18.2, 14.36) * mm, "end": v(-18.23, 14.27) * mm});
            skArc(sketch, "E273.24.15", {"start": v(-18.1, 15.6) * mm, "mid": v(-18.2, 15.64) * mm, "end": v(-18.23, 15.73) * mm});
            skArc(sketch, "E273.25.0", {"start": v(-18.1, 17.61) * mm, "mid": v(-18.26, 17.64) * mm, "end": v(-18.42, 17.64) * mm});
            skArc(sketch, "E273.25.1", {"start": v(-17.7, 17.19) * mm, "mid": v(-17.84, 17.46) * mm, "end": v(-18.1, 17.61) * mm});
            skArc(sketch, "E273.25.2", {"start": v(-19.05, 16.92) * mm, "mid": v(-18.97, 16.44) * mm, "end": v(-18.91, 15.96) * mm});
            skPoint(sketch, "E273.25.3", {"position": v(-18.44, 17.04) * mm});
            skArc(sketch, "E273.25.4", {"start": v(-17.9, 16.64) * mm, "mid": v(-18.04, 16.55) * mm, "end": v(-18.2, 16.48) * mm});
            skLineSegment(sketch, "E273.25.5", {"start": v(-19.29, 17.85) * mm, "end": v(-18.66, 18.04) * mm});
            skArc(sketch, "E273.25.6", {"start": v(-18.3, 16.32) * mm, "mid": v(-18.28, 16.18) * mm, "end": v(-18.26, 16.03) * mm});
            skLineSegment(sketch, "E273.25.7", {"start": v(-18.91, 15.96) * mm, "end": v(-18.26, 16.03) * mm});
            skArc(sketch, "E273.25.8", {"start": v(-17.7, 17.19) * mm, "mid": v(-17.73, 16.88) * mm, "end": v(-17.9, 16.64) * mm});
            skPoint(sketch, "E273.25.9", {"position": v(-19.05, 16.92) * mm});
            skArc(sketch, "E273.25.10", {"start": v(-18.68, 16.99) * mm, "mid": v(-18.6, 16.5) * mm, "end": v(-18.54, 16) * mm, "construction": true});
            skArc(sketch, "E273.25.11", {"start": v(-19.05, 16.92) * mm, "mid": v(-19.16, 17.39) * mm, "end": v(-19.29, 17.85) * mm});
            skPoint(sketch, "E273.25.12", {"position": v(-18.68, 16.99) * mm});
            skArc(sketch, "E273.25.13", {"start": v(-18.58, 17.76) * mm, "mid": v(-18.62, 17.9) * mm, "end": v(-18.66, 18.04) * mm});
            skArc(sketch, "E273.25.14", {"start": v(-18.2, 16.48) * mm, "mid": v(-18.27, 16.42) * mm, "end": v(-18.3, 16.32) * mm});
            skArc(sketch, "E273.25.15", {"start": v(-18.42, 17.64) * mm, "mid": v(-18.52, 17.67) * mm, "end": v(-18.58, 17.76) * mm});
            skArc(sketch, "E273.26.0", {"start": v(-18.82, 19.63) * mm, "mid": v(-18.98, 19.63) * mm, "end": v(-19.14, 19.6) * mm});
            skArc(sketch, "E273.26.1", {"start": v(-18.34, 19.29) * mm, "mid": v(-18.53, 19.53) * mm, "end": v(-18.82, 19.63) * mm});
            skArc(sketch, "E273.26.2", {"start": v(-19.61, 18.76) * mm, "mid": v(-19.44, 18.3) * mm, "end": v(-19.29, 17.85) * mm});
            skPoint(sketch, "E273.26.3", {"position": v(-19.03, 19) * mm});
            skArc(sketch, "E273.26.4", {"start": v(-18.43, 18.7) * mm, "mid": v(-18.55, 18.6) * mm, "end": v(-18.68, 18.5) * mm});
            skLineSegment(sketch, "E273.26.5", {"start": v(-20.02, 19.63) * mm, "end": v(-19.45, 19.94) * mm});
            skArc(sketch, "E273.26.6", {"start": v(-18.75, 18.33) * mm, "mid": v(-18.7, 18.18) * mm, "end": v(-18.66, 18.04) * mm});
            skLineSegment(sketch, "E273.26.7", {"start": v(-19.29, 17.85) * mm, "end": v(-18.66, 18.04) * mm});
            skArc(sketch, "E273.26.8", {"start": v(-18.34, 19.29) * mm, "mid": v(-18.3, 18.98) * mm, "end": v(-18.43, 18.7) * mm});
            skPoint(sketch, "E273.26.9", {"position": v(-19.61, 18.76) * mm});
            skArc(sketch, "E273.26.10", {"start": v(-19.26, 18.9) * mm, "mid": v(-19.08, 18.44) * mm, "end": v(-18.93, 17.96) * mm, "construction": true});
            skArc(sketch, "E273.26.11", {"start": v(-19.61, 18.76) * mm, "mid": v(-19.8, 19.2) * mm, "end": v(-20.02, 19.63) * mm});
            skPoint(sketch, "E273.26.12", {"position": v(-19.26, 18.9) * mm});
            skArc(sketch, "E273.26.13", {"start": v(-19.3, 19.67) * mm, "mid": v(-19.38, 19.8) * mm, "end": v(-19.45, 19.94) * mm});
            skArc(sketch, "E273.26.14", {"start": v(-18.68, 18.5) * mm, "mid": v(-18.75, 18.43) * mm, "end": v(-18.75, 18.33) * mm});
            skArc(sketch, "E273.26.15", {"start": v(-19.14, 19.6) * mm, "mid": v(-19.24, 19.6) * mm, "end": v(-19.3, 19.67) * mm});
            skArc(sketch, "E273.27.0", {"start": v(-19.9, 21.47) * mm, "mid": v(-20.07, 21.43) * mm, "end": v(-20.22, 21.37) * mm});
            skArc(sketch, "E273.27.1", {"start": v(-19.37, 21.22) * mm, "mid": v(-19.6, 21.42) * mm, "end": v(-19.9, 21.47) * mm});
            skArc(sketch, "E273.27.2", {"start": v(-20.52, 20.46) * mm, "mid": v(-20.26, 20.05) * mm, "end": v(-20.02, 19.63) * mm});
            skPoint(sketch, "E273.27.3", {"position": v(-20, 20.8) * mm});
            skArc(sketch, "E273.27.4", {"start": v(-19.35, 20.64) * mm, "mid": v(-19.45, 20.5) * mm, "end": v(-19.56, 20.39) * mm});
            skLineSegment(sketch, "E273.27.5", {"start": v(-21.1, 21.23) * mm, "end": v(-20.59, 21.65) * mm});
            skArc(sketch, "E273.27.6", {"start": v(-19.6, 20.2) * mm, "mid": v(-19.52, 20.07) * mm, "end": v(-19.45, 19.94) * mm});
            skLineSegment(sketch, "E273.27.7", {"start": v(-20.02, 19.63) * mm, "end": v(-19.45, 19.94) * mm});
            skArc(sketch, "E273.27.8", {"start": v(-19.37, 21.22) * mm, "mid": v(-19.28, 20.93) * mm, "end": v(-19.35, 20.64) * mm});
            skPoint(sketch, "E273.27.9", {"position": v(-20.52, 20.46) * mm});
            skArc(sketch, "E273.27.10", {"start": v(-20.2, 20.67) * mm, "mid": v(-19.94, 20.24) * mm, "end": v(-19.7, 19.8) * mm, "construction": true});
            skArc(sketch, "E273.27.11", {"start": v(-20.52, 20.46) * mm, "mid": v(-20.8, 20.85) * mm, "end": v(-21.1, 21.23) * mm});
            skPoint(sketch, "E273.27.12", {"position": v(-20.2, 20.67) * mm});
            skArc(sketch, "E273.27.13", {"start": v(-20.4, 21.41) * mm, "mid": v(-20.5, 21.53) * mm, "end": v(-20.59, 21.65) * mm});
            skArc(sketch, "E273.27.14", {"start": v(-19.56, 20.39) * mm, "mid": v(-19.6, 20.3) * mm, "end": v(-19.6, 20.2) * mm});
            skArc(sketch, "E273.27.15", {"start": v(-20.22, 21.37) * mm, "mid": v(-20.32, 21.36) * mm, "end": v(-20.4, 21.41) * mm});
            skArc(sketch, "E273.28.0", {"start": v(-21.34, 23.05) * mm, "mid": v(-21.49, 23) * mm, "end": v(-21.62, 22.9) * mm});
            skArc(sketch, "E273.28.1", {"start": v(-20.77, 22.92) * mm, "mid": v(-21.03, 23.07) * mm, "end": v(-21.34, 23.05) * mm});
            skArc(sketch, "E273.28.2", {"start": v(-21.74, 21.95) * mm, "mid": v(-21.4, 21.6) * mm, "end": v(-21.1, 21.23) * mm});
            skPoint(sketch, "E273.28.3", {"position": v(-21.3, 22.4) * mm});
            skArc(sketch, "E273.28.4", {"start": v(-20.63, 22.35) * mm, "mid": v(-20.7, 22.2) * mm, "end": v(-20.79, 22.07) * mm});
            skLineSegment(sketch, "E273.28.5", {"start": v(-22.46, 22.6) * mm, "end": v(-22.04, 23.1) * mm});
            skArc(sketch, "E273.28.6", {"start": v(-20.78, 21.88) * mm, "mid": v(-20.68, 21.76) * mm, "end": v(-20.59, 21.65) * mm});
            skLineSegment(sketch, "E273.28.7", {"start": v(-21.1, 21.23) * mm, "end": v(-20.59, 21.65) * mm});
            skArc(sketch, "E273.28.8", {"start": v(-20.77, 22.92) * mm, "mid": v(-20.62, 22.65) * mm, "end": v(-20.63, 22.35) * mm});
            skPoint(sketch, "E273.28.9", {"position": v(-21.74, 21.95) * mm});
            skArc(sketch, "E273.28.10", {"start": v(-21.48, 22.21) * mm, "mid": v(-21.13, 21.85) * mm, "end": v(-20.8, 21.47) * mm, "construction": true});
            skArc(sketch, "E273.28.11", {"start": v(-21.74, 21.95) * mm, "mid": v(-22.1, 22.28) * mm, "end": v(-22.46, 22.6) * mm});
            skPoint(sketch, "E273.28.12", {"position": v(-21.48, 22.21) * mm});
            skArc(sketch, "E273.28.13", {"start": v(-21.81, 22.9) * mm, "mid": v(-21.93, 23) * mm, "end": v(-22.04, 23.1) * mm});
            skArc(sketch, "E273.28.14", {"start": v(-20.79, 22.07) * mm, "mid": v(-20.82, 21.97) * mm, "end": v(-20.78, 21.88) * mm});
            skArc(sketch, "E273.28.15", {"start": v(-21.62, 22.9) * mm, "mid": v(-21.72, 22.87) * mm, "end": v(-21.81, 22.9) * mm});
            skArc(sketch, "E273.29.0", {"start": v(-23.05, 24.33) * mm, "mid": v(-23.18, 24.24) * mm, "end": v(-23.3, 24.13) * mm});
            skArc(sketch, "E273.29.1", {"start": v(-22.46, 24.32) * mm, "mid": v(-22.76, 24.4) * mm, "end": v(-23.05, 24.33) * mm});
            skArc(sketch, "E273.29.2", {"start": v(-23.23, 23.17) * mm, "mid": v(-22.84, 22.9) * mm, "end": v(-22.46, 22.6) * mm});
            skPoint(sketch, "E273.29.3", {"position": v(-22.88, 23.7) * mm});
            skArc(sketch, "E273.29.4", {"start": v(-22.22, 23.78) * mm, "mid": v(-22.26, 23.62) * mm, "end": v(-22.32, 23.47) * mm});
            skLineSegment(sketch, "E273.29.5", {"start": v(-24.06, 23.66) * mm, "end": v(-23.75, 24.24) * mm});
            skArc(sketch, "E273.29.6", {"start": v(-22.27, 23.29) * mm, "mid": v(-22.16, 23.2) * mm, "end": v(-22.04, 23.1) * mm});
            skLineSegment(sketch, "E273.29.7", {"start": v(-22.46, 22.6) * mm, "end": v(-22.04, 23.1) * mm});
            skArc(sketch, "E273.29.8", {"start": v(-22.46, 24.32) * mm, "mid": v(-22.27, 24.08) * mm, "end": v(-22.22, 23.78) * mm});
            skPoint(sketch, "E273.29.9", {"position": v(-23.23, 23.17) * mm});
            skArc(sketch, "E273.29.10", {"start": v(-23.02, 23.48) * mm, "mid": v(-22.61, 23.2) * mm, "end": v(-22.22, 22.88) * mm, "construction": true});
            skArc(sketch, "E273.29.11", {"start": v(-23.23, 23.17) * mm, "mid": v(-23.64, 23.43) * mm, "end": v(-24.06, 23.66) * mm});
            skPoint(sketch, "E273.29.12", {"position": v(-23.02, 23.48) * mm});
            skArc(sketch, "E273.29.13", {"start": v(-23.49, 24.1) * mm, "mid": v(-23.62, 24.17) * mm, "end": v(-23.75, 24.24) * mm});
            skArc(sketch, "E273.29.14", {"start": v(-22.32, 23.47) * mm, "mid": v(-22.33, 23.37) * mm, "end": v(-22.27, 23.29) * mm});
            skArc(sketch, "E273.29.15", {"start": v(-23.3, 24.13) * mm, "mid": v(-23.39, 24.08) * mm, "end": v(-23.49, 24.1) * mm});
            skArc(sketch, "E273.30.0", {"start": v(-24.98, 25.25) * mm, "mid": v(-25.1, 25.14) * mm, "end": v(-25.18, 25) * mm});
            skArc(sketch, "E273.30.1", {"start": v(-24.4, 25.35) * mm, "mid": v(-24.7, 25.39) * mm, "end": v(-24.98, 25.25) * mm});
            skArc(sketch, "E273.30.2", {"start": v(-24.93, 24.08) * mm, "mid": v(-24.49, 23.88) * mm, "end": v(-24.06, 23.66) * mm});
            skPoint(sketch, "E273.30.3", {"position": v(-24.69, 24.66) * mm});
            skArc(sketch, "E273.30.4", {"start": v(-24.06, 24.87) * mm, "mid": v(-24.06, 24.71) * mm, "end": v(-24.1, 24.55) * mm});
            skLineSegment(sketch, "E273.30.5", {"start": v(-25.84, 24.4) * mm, "end": v(-25.65, 25.03) * mm});
            skArc(sketch, "E273.30.6", {"start": v(-24.01, 24.38) * mm, "mid": v(-23.88, 24.31) * mm, "end": v(-23.75, 24.24) * mm});
            skLineSegment(sketch, "E273.30.7", {"start": v(-24.06, 23.66) * mm, "end": v(-23.75, 24.24) * mm});
            skArc(sketch, "E273.30.8", {"start": v(-24.4, 25.35) * mm, "mid": v(-24.16, 25.16) * mm, "end": v(-24.06, 24.87) * mm});
            skPoint(sketch, "E273.30.9", {"position": v(-24.93, 24.08) * mm});
            skArc(sketch, "E273.30.10", {"start": v(-24.79, 24.42) * mm, "mid": v(-24.33, 24.22) * mm, "end": v(-23.88, 24) * mm, "construction": true});
            skArc(sketch, "E273.30.11", {"start": v(-24.93, 24.08) * mm, "mid": v(-25.38, 24.25) * mm, "end": v(-25.84, 24.4) * mm});
            skPoint(sketch, "E273.30.12", {"position": v(-24.79, 24.42) * mm});
            skArc(sketch, "E273.30.13", {"start": v(-25.36, 24.94) * mm, "mid": v(-25.5, 24.98) * mm, "end": v(-25.65, 25.03) * mm});
            skArc(sketch, "E273.30.14", {"start": v(-24.1, 24.55) * mm, "mid": v(-24.08, 24.45) * mm, "end": v(-24.01, 24.38) * mm});
            skArc(sketch, "E273.30.15", {"start": v(-25.18, 25) * mm, "mid": v(-25.26, 24.94) * mm, "end": v(-25.36, 24.94) * mm});
            skArc(sketch, "E273.31.0", {"start": v(-27.05, 25.78) * mm, "mid": v(-27.14, 25.64) * mm, "end": v(-27.2, 25.5) * mm});
            skArc(sketch, "E273.31.1", {"start": v(-26.5, 25.99) * mm, "mid": v(-26.8, 25.96) * mm, "end": v(-27.05, 25.78) * mm});
            skArc(sketch, "E273.31.2", {"start": v(-26.77, 24.64) * mm, "mid": v(-26.3, 24.53) * mm, "end": v(-25.84, 24.4) * mm});
            skPoint(sketch, "E273.31.3", {"position": v(-26.65, 25.25) * mm});
            skArc(sketch, "E273.31.4", {"start": v(-26.07, 25.59) * mm, "mid": v(-26.05, 25.43) * mm, "end": v(-26.04, 25.27) * mm});
            skArc(sketch, "E273.31.6", {"start": v(-25.93, 25.11) * mm, "mid": v(-25.79, 25.07) * mm, "end": v(-25.65, 25.03) * mm});
            skLineSegment(sketch, "E273.31.7", {"start": v(-25.84, 24.4) * mm, "end": v(-25.65, 25.03) * mm});
            skArc(sketch, "E273.31.8", {"start": v(-26.5, 25.99) * mm, "mid": v(-26.23, 25.85) * mm, "end": v(-26.07, 25.59) * mm});
            skPoint(sketch, "E273.31.9", {"position": v(-26.77, 24.64) * mm});
            skArc(sketch, "E273.31.10", {"start": v(-26.7, 25) * mm, "mid": v(-26.2, 24.9) * mm, "end": v(-25.73, 24.76) * mm, "construction": true});
            skArc(sketch, "E273.31.11", {"start": v(-26.77, 24.64) * mm, "mid": v(-27.25, 24.72) * mm, "end": v(-27.73, 24.78) * mm});
            skPoint(sketch, "E273.31.12", {"position": v(-26.7, 25) * mm});
            skArc(sketch, "E273.31.13", {"start": v(-27.36, 25.4) * mm, "mid": v(-27.51, 25.41) * mm, "end": v(-27.66, 25.43) * mm});
            skArc(sketch, "E273.31.14", {"start": v(-26.04, 25.27) * mm, "mid": v(-26.02, 25.17) * mm, "end": v(-25.93, 25.11) * mm});
            skArc(sketch, "E273.31.15", {"start": v(-27.2, 25.5) * mm, "mid": v(-27.27, 25.42) * mm, "end": v(-27.36, 25.4) * mm});
            skArc(sketch, "E274.0", {"start": v(-38.94, 15) * mm, "mid": v(-28.69, 4.75) * mm, "end": v(-18.44, 15) * mm});
            skSolve(sketch);
        }
        {
            var Q0;
            Q0=qSketchRegion(id+"F44",true);
            extrude(context, id + "F45", {"entities" : qUnion([Q0]), "operationType" : NewBodyOperationType.REMOVE, "endBound" : BoundingType.SYMMETRIC, "oppositeDirection" : true, "depth" : 6.5 * mm});
        }
        {
            var Q0;
            Q0=makeQuery(id+"F40.opExtrude","SWEPT_FACE",FACE,{"disambiguationData":[OSD([sQuery(id+"F39.wireOp",EDGE,"E244.right")])]});
            var Q1;
            Q1=sQuery(id+"F39.wireOp",VERTEX,"E251");
            cPlane(context, id + "F46", {"entities" : qUnion([Q0, Q1]), "cplaneType" : CPlaneType.PLANE_POINT, "offset" : 150 * mm, "width" : 150 * mm, "height" : 150 * mm});
        }
        {
            var Q0;
            Q0=qCreatedBy(id+"F46.planeOp",FACE);
            var sketch = newSketch(context, id + "F47", { "sketchPlane" : qUnion([Q0])});
            skLineSegment(sketch, "E275", {"start": v(-28.69, 26.2) * mm, "end": v(-28.69, 24.82) * mm, "construction": true});
            skArc(sketch, "E276", {"start": v(-28.69, 26.2) * mm, "mid": v(-28.4, 26.12) * mm, "end": v(-28.19, 25.9) * mm});
            skArc(sketch, "E277", {"start": v(-28.19, 25.9) * mm, "mid": v(-28.13, 25.74) * mm, "end": v(-28.1, 25.58) * mm});
            skArc(sketch, "E278", {"start": v(-28.1, 25.58) * mm, "mid": v(-28.05, 25.5) * mm, "end": v(-27.96, 25.45) * mm});
            skPoint(sketch, "E279", {"position": v(-28.69, 24.82) * mm});
            skPoint(sketch, "E280", {"position": v(-28.69, 25.45) * mm});
            skPoint(sketch, "E281", {"position": v(-28.69, 25.2) * mm});
            skArc(sketch, "E282", {"start": v(-28.69, 25.2) * mm, "mid": v(-28.19, 25.19) * mm, "end": v(-27.69, 25.15) * mm, "construction": true});
            skLineSegment(sketch, "E283", {"start": v(-27.73, 24.78) * mm, "end": v(-27.66, 25.43) * mm});
            skArc(sketch, "E284", {"start": v(-27.96, 25.45) * mm, "mid": v(-27.8, 25.44) * mm, "end": v(-27.66, 25.43) * mm});
            skArc(sketch, "E285", {"start": v(-28.69, 24.82) * mm, "mid": v(-28.2, 24.81) * mm, "end": v(-27.73, 24.78) * mm});
            skArc(sketch, "E286.MirrorCS", {"start": v(-28.69, 26.2) * mm, "mid": v(-28.98, 26.12) * mm, "end": v(-29.19, 25.9) * mm});
            skArc(sketch, "E287.MirrorCS", {"start": v(-29.19, 25.9) * mm, "mid": v(-29.25, 25.74) * mm, "end": v(-29.28, 25.58) * mm});
            skArc(sketch, "E288.MirrorCS", {"start": v(-29.28, 25.58) * mm, "mid": v(-29.33, 25.5) * mm, "end": v(-29.42, 25.45) * mm});
            skArc(sketch, "E289.MirrorCS", {"start": v(-29.42, 25.45) * mm, "mid": v(-29.57, 25.44) * mm, "end": v(-29.72, 25.43) * mm});
            skLineSegment(sketch, "E290.MirrorCS", {"start": v(-29.65, 24.78) * mm, "end": v(-29.72, 25.43) * mm});
            skArc(sketch, "E291.MirrorCS", {"start": v(-28.69, 24.82) * mm, "mid": v(-29.17, 24.81) * mm, "end": v(-29.65, 24.78) * mm});
            skArc(sketch, "E292.1.0", {"start": v(-31.3, 25.59) * mm, "mid": v(-31.33, 25.43) * mm, "end": v(-31.33, 25.27) * mm});
            skArc(sketch, "E292.1.1", {"start": v(-30.87, 25.99) * mm, "mid": v(-31.15, 25.85) * mm, "end": v(-31.3, 25.59) * mm});
            skArc(sketch, "E292.1.2", {"start": v(-30.6, 24.64) * mm, "mid": v(-30.13, 24.72) * mm, "end": v(-29.65, 24.78) * mm});
            skPoint(sketch, "E292.1.3", {"position": v(-30.73, 25.25) * mm});
            skArc(sketch, "E292.1.4", {"start": v(-30.32, 25.78) * mm, "mid": v(-30.24, 25.64) * mm, "end": v(-30.17, 25.5) * mm});
            skLineSegment(sketch, "E292.1.5", {"start": v(-31.54, 24.4) * mm, "end": v(-31.73, 25.03) * mm});
            skArc(sketch, "E292.1.6", {"start": v(-30.01, 25.4) * mm, "mid": v(-29.86, 25.41) * mm, "end": v(-29.72, 25.43) * mm});
            skArc(sketch, "E292.1.8", {"start": v(-30.87, 25.99) * mm, "mid": v(-30.57, 25.96) * mm, "end": v(-30.32, 25.78) * mm});
            skPoint(sketch, "E292.1.9", {"position": v(-30.6, 24.64) * mm});
            skArc(sketch, "E292.1.10", {"start": v(-30.68, 25) * mm, "mid": v(-30.19, 25.09) * mm, "end": v(-29.69, 25.15) * mm, "construction": true});
            skArc(sketch, "E292.1.11", {"start": v(-30.6, 24.64) * mm, "mid": v(-31.08, 24.53) * mm, "end": v(-31.54, 24.4) * mm});
            skPoint(sketch, "E292.1.12", {"position": v(-30.68, 25) * mm});
            skArc(sketch, "E292.1.13", {"start": v(-31.44, 25.11) * mm, "mid": v(-31.59, 25.07) * mm, "end": v(-31.73, 25.03) * mm});
            skArc(sketch, "E292.1.14", {"start": v(-30.17, 25.5) * mm, "mid": v(-30.11, 25.42) * mm, "end": v(-30.01, 25.4) * mm});
            skArc(sketch, "E292.1.15", {"start": v(-31.33, 25.27) * mm, "mid": v(-31.36, 25.17) * mm, "end": v(-31.44, 25.11) * mm});
            skArc(sketch, "E292.2.0", {"start": v(-33.32, 24.87) * mm, "mid": v(-33.31, 24.71) * mm, "end": v(-33.29, 24.55) * mm});
            skArc(sketch, "E292.2.1", {"start": v(-32.98, 25.35) * mm, "mid": v(-33.22, 25.16) * mm, "end": v(-33.32, 24.87) * mm});
            skArc(sketch, "E292.2.2", {"start": v(-32.45, 24.08) * mm, "mid": v(-32, 24.25) * mm, "end": v(-31.54, 24.4) * mm});
            skPoint(sketch, "E292.2.3", {"position": v(-32.69, 24.66) * mm});
            skArc(sketch, "E292.2.4", {"start": v(-32.4, 25.25) * mm, "mid": v(-32.28, 25.14) * mm, "end": v(-32.2, 25) * mm});
            skLineSegment(sketch, "E292.2.5", {"start": v(-33.32, 23.66) * mm, "end": v(-33.63, 24.24) * mm});
            skArc(sketch, "E292.2.6", {"start": v(-32.01, 24.94) * mm, "mid": v(-31.87, 24.98) * mm, "end": v(-31.73, 25.03) * mm});
            skLineSegment(sketch, "E292.2.7", {"start": v(-31.54, 24.4) * mm, "end": v(-31.73, 25.03) * mm});
            skArc(sketch, "E292.2.8", {"start": v(-32.98, 25.35) * mm, "mid": v(-32.67, 25.39) * mm, "end": v(-32.4, 25.25) * mm});
            skPoint(sketch, "E292.2.9", {"position": v(-32.45, 24.08) * mm});
            skArc(sketch, "E292.2.10", {"start": v(-32.6, 24.42) * mm, "mid": v(-32.12, 24.6) * mm, "end": v(-31.65, 24.76) * mm, "construction": true});
            skArc(sketch, "E292.2.11", {"start": v(-32.45, 24.08) * mm, "mid": v(-32.89, 23.88) * mm, "end": v(-33.32, 23.66) * mm});
            skPoint(sketch, "E292.2.12", {"position": v(-32.6, 24.42) * mm});
            skArc(sketch, "E292.2.13", {"start": v(-33.36, 24.38) * mm, "mid": v(-33.5, 24.31) * mm, "end": v(-33.63, 24.24) * mm});
            skArc(sketch, "E292.2.14", {"start": v(-32.2, 25) * mm, "mid": v(-32.12, 24.94) * mm, "end": v(-32.01, 24.94) * mm});
            skArc(sketch, "E292.2.15", {"start": v(-33.29, 24.55) * mm, "mid": v(-33.3, 24.45) * mm, "end": v(-33.36, 24.38) * mm});
            skArc(sketch, "E292.3.0", {"start": v(-35.15, 23.78) * mm, "mid": v(-35.12, 23.62) * mm, "end": v(-35.06, 23.47) * mm});
            skArc(sketch, "E292.3.1", {"start": v(-34.91, 24.32) * mm, "mid": v(-35.11, 24.08) * mm, "end": v(-35.15, 23.78) * mm});
            skArc(sketch, "E292.3.2", {"start": v(-34.15, 23.17) * mm, "mid": v(-33.74, 23.43) * mm, "end": v(-33.32, 23.66) * mm});
            skPoint(sketch, "E292.3.3", {"position": v(-34.5, 23.7) * mm});
            skArc(sketch, "E292.3.4", {"start": v(-34.33, 24.33) * mm, "mid": v(-34.2, 24.24) * mm, "end": v(-34.08, 24.13) * mm});
            skLineSegment(sketch, "E292.3.5", {"start": v(-34.92, 22.6) * mm, "end": v(-35.34, 23.1) * mm});
            skArc(sketch, "E292.3.6", {"start": v(-33.89, 24.1) * mm, "mid": v(-33.76, 24.17) * mm, "end": v(-33.63, 24.24) * mm});
            skLineSegment(sketch, "E292.3.7", {"start": v(-33.32, 23.66) * mm, "end": v(-33.63, 24.24) * mm});
            skArc(sketch, "E292.3.8", {"start": v(-34.91, 24.32) * mm, "mid": v(-34.62, 24.4) * mm, "end": v(-34.33, 24.33) * mm});
            skPoint(sketch, "E292.3.9", {"position": v(-34.15, 23.17) * mm});
            skArc(sketch, "E292.3.10", {"start": v(-34.36, 23.48) * mm, "mid": v(-33.93, 23.75) * mm, "end": v(-33.5, 24) * mm, "construction": true});
            skArc(sketch, "E292.3.11", {"start": v(-34.15, 23.17) * mm, "mid": v(-34.54, 22.9) * mm, "end": v(-34.92, 22.6) * mm});
            skPoint(sketch, "E292.3.12", {"position": v(-34.36, 23.48) * mm});
            skArc(sketch, "E292.3.13", {"start": v(-35.1, 23.29) * mm, "mid": v(-35.22, 23.2) * mm, "end": v(-35.34, 23.1) * mm});
            skArc(sketch, "E292.3.14", {"start": v(-34.08, 24.13) * mm, "mid": v(-33.99, 24.08) * mm, "end": v(-33.89, 24.1) * mm});
            skArc(sketch, "E292.3.15", {"start": v(-35.06, 23.47) * mm, "mid": v(-35.05, 23.37) * mm, "end": v(-35.1, 23.29) * mm});
            skArc(sketch, "E292.4.0", {"start": v(-36.74, 22.35) * mm, "mid": v(-36.68, 22.2) * mm, "end": v(-36.6, 22.07) * mm});
            skArc(sketch, "E292.4.1", {"start": v(-36.61, 22.92) * mm, "mid": v(-36.76, 22.65) * mm, "end": v(-36.74, 22.35) * mm});
            skArc(sketch, "E292.4.2", {"start": v(-35.64, 21.95) * mm, "mid": v(-35.29, 22.28) * mm, "end": v(-34.92, 22.6) * mm});
            skPoint(sketch, "E292.4.3", {"position": v(-36.08, 22.4) * mm});
            skArc(sketch, "E292.4.4", {"start": v(-36.04, 23.05) * mm, "mid": v(-35.89, 23) * mm, "end": v(-35.75, 22.9) * mm});
            skLineSegment(sketch, "E292.4.5", {"start": v(-36.28, 21.23) * mm, "end": v(-36.79, 21.65) * mm});
            skArc(sketch, "E292.4.6", {"start": v(-35.56, 22.9) * mm, "mid": v(-35.45, 23) * mm, "end": v(-35.34, 23.1) * mm});
            skLineSegment(sketch, "E292.4.7", {"start": v(-34.92, 22.6) * mm, "end": v(-35.34, 23.1) * mm});
            skArc(sketch, "E292.4.8", {"start": v(-36.61, 22.92) * mm, "mid": v(-36.34, 23.07) * mm, "end": v(-36.04, 23.05) * mm});
            skPoint(sketch, "E292.4.9", {"position": v(-35.64, 21.95) * mm});
            skArc(sketch, "E292.4.10", {"start": v(-35.9, 22.21) * mm, "mid": v(-35.54, 22.56) * mm, "end": v(-35.16, 22.88) * mm, "construction": true});
            skArc(sketch, "E292.4.11", {"start": v(-35.64, 21.95) * mm, "mid": v(-35.97, 21.6) * mm, "end": v(-36.28, 21.23) * mm});
            skPoint(sketch, "E292.4.12", {"position": v(-35.9, 22.21) * mm});
            skArc(sketch, "E292.4.13", {"start": v(-36.6, 21.88) * mm, "mid": v(-36.7, 21.76) * mm, "end": v(-36.79, 21.65) * mm});
            skArc(sketch, "E292.4.14", {"start": v(-35.75, 22.9) * mm, "mid": v(-35.66, 22.87) * mm, "end": v(-35.56, 22.9) * mm});
            skArc(sketch, "E292.4.15", {"start": v(-36.6, 22.07) * mm, "mid": v(-36.56, 21.97) * mm, "end": v(-36.6, 21.88) * mm});
            skArc(sketch, "E292.5.0", {"start": v(-38.02, 20.64) * mm, "mid": v(-37.93, 20.5) * mm, "end": v(-37.82, 20.39) * mm});
            skArc(sketch, "E292.5.1", {"start": v(-38, 21.22) * mm, "mid": v(-38.1, 20.93) * mm, "end": v(-38.02, 20.64) * mm});
            skArc(sketch, "E292.5.2", {"start": v(-36.86, 20.46) * mm, "mid": v(-36.58, 20.85) * mm, "end": v(-36.28, 21.23) * mm});
            skPoint(sketch, "E292.5.3", {"position": v(-37.38, 20.8) * mm});
            skArc(sketch, "E292.5.4", {"start": v(-37.47, 21.47) * mm, "mid": v(-37.31, 21.43) * mm, "end": v(-37.16, 21.37) * mm});
            skLineSegment(sketch, "E292.5.5", {"start": v(-37.35, 19.63) * mm, "end": v(-37.93, 19.94) * mm});
            skArc(sketch, "E292.5.6", {"start": v(-36.98, 21.41) * mm, "mid": v(-36.88, 21.53) * mm, "end": v(-36.79, 21.65) * mm});
            skLineSegment(sketch, "E292.5.7", {"start": v(-36.28, 21.23) * mm, "end": v(-36.79, 21.65) * mm});
            skArc(sketch, "E292.5.8", {"start": v(-38, 21.22) * mm, "mid": v(-37.77, 21.42) * mm, "end": v(-37.47, 21.47) * mm});
            skPoint(sketch, "E292.5.9", {"position": v(-36.86, 20.46) * mm});
            skArc(sketch, "E292.5.10", {"start": v(-37.17, 20.67) * mm, "mid": v(-36.88, 21.08) * mm, "end": v(-36.57, 21.47) * mm, "construction": true});
            skArc(sketch, "E292.5.11", {"start": v(-36.86, 20.46) * mm, "mid": v(-37.11, 20.05) * mm, "end": v(-37.35, 19.63) * mm});
            skPoint(sketch, "E292.5.12", {"position": v(-37.17, 20.67) * mm});
            skArc(sketch, "E292.5.13", {"start": v(-37.79, 20.2) * mm, "mid": v(-37.86, 20.07) * mm, "end": v(-37.93, 19.94) * mm});
            skArc(sketch, "E292.5.14", {"start": v(-37.16, 21.37) * mm, "mid": v(-37.06, 21.36) * mm, "end": v(-36.98, 21.41) * mm});
            skArc(sketch, "E292.5.15", {"start": v(-37.82, 20.39) * mm, "mid": v(-37.77, 20.3) * mm, "end": v(-37.79, 20.2) * mm});
            skArc(sketch, "E292.6.0", {"start": v(-38.94, 18.7) * mm, "mid": v(-38.83, 18.6) * mm, "end": v(-38.7, 18.5) * mm});
            skArc(sketch, "E292.6.1", {"start": v(-39.04, 19.29) * mm, "mid": v(-39.07, 18.98) * mm, "end": v(-38.94, 18.7) * mm});
            skArc(sketch, "E292.6.2", {"start": v(-37.76, 18.76) * mm, "mid": v(-37.57, 19.2) * mm, "end": v(-37.35, 19.63) * mm});
            skPoint(sketch, "E292.6.3", {"position": v(-38.35, 19) * mm});
            skArc(sketch, "E292.6.4", {"start": v(-38.56, 19.63) * mm, "mid": v(-38.4, 19.63) * mm, "end": v(-38.24, 19.6) * mm});
            skLineSegment(sketch, "E292.6.5", {"start": v(-38.09, 17.85) * mm, "end": v(-38.72, 18.04) * mm});
            skArc(sketch, "E292.6.6", {"start": v(-38.07, 19.67) * mm, "mid": v(-38, 19.8) * mm, "end": v(-37.93, 19.94) * mm});
            skLineSegment(sketch, "E292.6.7", {"start": v(-37.35, 19.63) * mm, "end": v(-37.93, 19.94) * mm});
            skArc(sketch, "E292.6.8", {"start": v(-39.04, 19.29) * mm, "mid": v(-38.85, 19.53) * mm, "end": v(-38.56, 19.63) * mm});
            skPoint(sketch, "E292.6.9", {"position": v(-37.76, 18.76) * mm});
            skArc(sketch, "E292.6.10", {"start": v(-38.11, 18.9) * mm, "mid": v(-37.9, 19.36) * mm, "end": v(-37.68, 19.8) * mm, "construction": true});
            skArc(sketch, "E292.6.11", {"start": v(-37.76, 18.76) * mm, "mid": v(-37.94, 18.3) * mm, "end": v(-38.09, 17.85) * mm});
            skPoint(sketch, "E292.6.12", {"position": v(-38.11, 18.9) * mm});
            skArc(sketch, "E292.6.13", {"start": v(-38.63, 18.33) * mm, "mid": v(-38.67, 18.18) * mm, "end": v(-38.72, 18.04) * mm});
            skArc(sketch, "E292.6.14", {"start": v(-38.24, 19.6) * mm, "mid": v(-38.14, 19.6) * mm, "end": v(-38.07, 19.67) * mm});
            skArc(sketch, "E292.6.15", {"start": v(-38.7, 18.5) * mm, "mid": v(-38.63, 18.43) * mm, "end": v(-38.63, 18.33) * mm});
            skArc(sketch, "E292.7.0", {"start": v(-39.47, 16.64) * mm, "mid": v(-39.33, 16.55) * mm, "end": v(-39.18, 16.48) * mm});
            skArc(sketch, "E292.7.1", {"start": v(-39.68, 17.19) * mm, "mid": v(-39.65, 16.88) * mm, "end": v(-39.47, 16.64) * mm});
            skArc(sketch, "E292.7.2", {"start": v(-38.32, 16.92) * mm, "mid": v(-38.22, 17.39) * mm, "end": v(-38.09, 17.85) * mm});
            skPoint(sketch, "E292.7.3", {"position": v(-38.94, 17.04) * mm});
            skArc(sketch, "E292.7.4", {"start": v(-39.27, 17.61) * mm, "mid": v(-39.12, 17.64) * mm, "end": v(-38.95, 17.64) * mm});
            skLineSegment(sketch, "E292.7.5", {"start": v(-38.47, 15.96) * mm, "end": v(-39.12, 16.03) * mm});
            skArc(sketch, "E292.7.6", {"start": v(-38.8, 17.76) * mm, "mid": v(-38.76, 17.9) * mm, "end": v(-38.72, 18.04) * mm});
            skLineSegment(sketch, "E292.7.7", {"start": v(-38.09, 17.85) * mm, "end": v(-38.72, 18.04) * mm});
            skArc(sketch, "E292.7.8", {"start": v(-39.68, 17.19) * mm, "mid": v(-39.54, 17.46) * mm, "end": v(-39.27, 17.61) * mm});
            skPoint(sketch, "E292.7.9", {"position": v(-38.32, 16.92) * mm});
            skArc(sketch, "E292.7.10", {"start": v(-38.7, 16.99) * mm, "mid": v(-38.58, 17.48) * mm, "end": v(-38.45, 17.96) * mm, "construction": true});
            skArc(sketch, "E292.7.11", {"start": v(-38.32, 16.92) * mm, "mid": v(-38.4, 16.44) * mm, "end": v(-38.47, 15.96) * mm});
            skPoint(sketch, "E292.7.12", {"position": v(-38.7, 16.99) * mm});
            skArc(sketch, "E292.7.13", {"start": v(-39.08, 16.32) * mm, "mid": v(-39.1, 16.18) * mm, "end": v(-39.12, 16.03) * mm});
            skArc(sketch, "E292.7.14", {"start": v(-38.95, 17.64) * mm, "mid": v(-38.86, 17.67) * mm, "end": v(-38.8, 17.76) * mm});
            skArc(sketch, "E292.7.15", {"start": v(-39.18, 16.48) * mm, "mid": v(-39.1, 16.42) * mm, "end": v(-39.08, 16.32) * mm});
            skArc(sketch, "E292.8.0", {"start": v(-39.58, 14.5) * mm, "mid": v(-39.43, 14.44) * mm, "end": v(-39.27, 14.4) * mm});
            skArc(sketch, "E292.8.1", {"start": v(-39.9, 15) * mm, "mid": v(-39.8, 14.7) * mm, "end": v(-39.58, 14.5) * mm});
            skArc(sketch, "E292.8.2", {"start": v(-38.51, 15) * mm, "mid": v(-38.5, 15.48) * mm, "end": v(-38.47, 15.96) * mm});
            skPoint(sketch, "E292.8.3", {"position": v(-39.14, 15) * mm});
            skArc(sketch, "E292.8.4", {"start": v(-39.58, 15.5) * mm, "mid": v(-39.43, 15.56) * mm, "end": v(-39.27, 15.6) * mm});
            skLineSegment(sketch, "E292.8.5", {"start": v(-38.47, 14.04) * mm, "end": v(-39.12, 13.97) * mm});
            skArc(sketch, "E292.8.6", {"start": v(-39.14, 15.73) * mm, "mid": v(-39.13, 15.88) * mm, "end": v(-39.12, 16.03) * mm});
            skLineSegment(sketch, "E292.8.7", {"start": v(-38.47, 15.96) * mm, "end": v(-39.12, 16.03) * mm});
            skArc(sketch, "E292.8.8", {"start": v(-39.9, 15) * mm, "mid": v(-39.8, 15.3) * mm, "end": v(-39.58, 15.5) * mm});
            skPoint(sketch, "E292.8.9", {"position": v(-38.51, 15) * mm});
            skArc(sketch, "E292.8.10", {"start": v(-38.89, 15) * mm, "mid": v(-38.88, 15.5) * mm, "end": v(-38.84, 16) * mm, "construction": true});
            skArc(sketch, "E292.8.11", {"start": v(-38.51, 15) * mm, "mid": v(-38.5, 14.52) * mm, "end": v(-38.47, 14.04) * mm});
            skPoint(sketch, "E292.8.12", {"position": v(-38.89, 15) * mm});
            skArc(sketch, "E292.8.13", {"start": v(-39.14, 14.27) * mm, "mid": v(-39.13, 14.12) * mm, "end": v(-39.12, 13.97) * mm});
            skArc(sketch, "E292.8.14", {"start": v(-39.27, 15.6) * mm, "mid": v(-39.18, 15.64) * mm, "end": v(-39.14, 15.73) * mm});
            skArc(sketch, "E292.8.15", {"start": v(-39.27, 14.4) * mm, "mid": v(-39.18, 14.36) * mm, "end": v(-39.14, 14.27) * mm});
            skArc(sketch, "E292.9.0", {"start": v(-39.27, 12.39) * mm, "mid": v(-39.12, 12.36) * mm, "end": v(-38.95, 12.36) * mm});
            skArc(sketch, "E292.9.1", {"start": v(-39.68, 12.81) * mm, "mid": v(-39.54, 12.54) * mm, "end": v(-39.27, 12.39) * mm});
            skArc(sketch, "E292.9.2", {"start": v(-38.32, 13.08) * mm, "mid": v(-38.4, 13.56) * mm, "end": v(-38.47, 14.04) * mm});
            skPoint(sketch, "E292.9.3", {"position": v(-38.94, 12.96) * mm});
            skArc(sketch, "E292.9.4", {"start": v(-39.47, 13.36) * mm, "mid": v(-39.33, 13.45) * mm, "end": v(-39.18, 13.52) * mm});
            skLineSegment(sketch, "E292.9.5", {"start": v(-38.09, 12.15) * mm, "end": v(-38.72, 11.96) * mm});
            skArc(sketch, "E292.9.6", {"start": v(-39.08, 13.68) * mm, "mid": v(-39.1, 13.82) * mm, "end": v(-39.12, 13.97) * mm});
            skLineSegment(sketch, "E292.9.7", {"start": v(-38.47, 14.04) * mm, "end": v(-39.12, 13.97) * mm});
            skArc(sketch, "E292.9.8", {"start": v(-39.68, 12.81) * mm, "mid": v(-39.65, 13.12) * mm, "end": v(-39.47, 13.36) * mm});
            skPoint(sketch, "E292.9.9", {"position": v(-38.32, 13.08) * mm});
            skArc(sketch, "E292.9.10", {"start": v(-38.7, 13.01) * mm, "mid": v(-38.78, 13.5) * mm, "end": v(-38.84, 14) * mm, "construction": true});
            skArc(sketch, "E292.9.11", {"start": v(-38.32, 13.08) * mm, "mid": v(-38.22, 12.61) * mm, "end": v(-38.09, 12.15) * mm});
            skPoint(sketch, "E292.9.12", {"position": v(-38.7, 13.01) * mm});
            skArc(sketch, "E292.9.13", {"start": v(-38.8, 12.24) * mm, "mid": v(-38.76, 12.1) * mm, "end": v(-38.72, 11.96) * mm});
            skArc(sketch, "E292.9.14", {"start": v(-39.18, 13.52) * mm, "mid": v(-39.1, 13.58) * mm, "end": v(-39.08, 13.68) * mm});
            skArc(sketch, "E292.9.15", {"start": v(-38.95, 12.36) * mm, "mid": v(-38.86, 12.33) * mm, "end": v(-38.8, 12.24) * mm});
            skArc(sketch, "E292.10.0", {"start": v(-38.56, 10.37) * mm, "mid": v(-38.4, 10.37) * mm, "end": v(-38.24, 10.4) * mm});
            skArc(sketch, "E292.10.1", {"start": v(-39.04, 10.71) * mm, "mid": v(-38.85, 10.47) * mm, "end": v(-38.56, 10.37) * mm});
            skArc(sketch, "E292.10.2", {"start": v(-37.76, 11.24) * mm, "mid": v(-37.94, 11.7) * mm, "end": v(-38.09, 12.15) * mm});
            skPoint(sketch, "E292.10.3", {"position": v(-38.35, 11) * mm});
            skArc(sketch, "E292.10.4", {"start": v(-38.94, 11.3) * mm, "mid": v(-38.83, 11.4) * mm, "end": v(-38.7, 11.5) * mm});
            skLineSegment(sketch, "E292.10.5", {"start": v(-37.35, 10.37) * mm, "end": v(-37.93, 10.06) * mm});
            skArc(sketch, "E292.10.6", {"start": v(-38.63, 11.67) * mm, "mid": v(-38.67, 11.82) * mm, "end": v(-38.72, 11.96) * mm});
            skLineSegment(sketch, "E292.10.7", {"start": v(-38.09, 12.15) * mm, "end": v(-38.72, 11.96) * mm});
            skArc(sketch, "E292.10.8", {"start": v(-39.04, 10.71) * mm, "mid": v(-39.07, 11.02) * mm, "end": v(-38.94, 11.3) * mm});
            skPoint(sketch, "E292.10.9", {"position": v(-37.76, 11.24) * mm});
            skArc(sketch, "E292.10.10", {"start": v(-38.11, 11.1) * mm, "mid": v(-38.3, 11.56) * mm, "end": v(-38.45, 12.04) * mm, "construction": true});
            skArc(sketch, "E292.10.11", {"start": v(-37.76, 11.24) * mm, "mid": v(-37.57, 10.8) * mm, "end": v(-37.35, 10.37) * mm});
            skPoint(sketch, "E292.10.12", {"position": v(-38.11, 11.1) * mm});
            skArc(sketch, "E292.10.13", {"start": v(-38.07, 10.33) * mm, "mid": v(-38, 10.2) * mm, "end": v(-37.93, 10.06) * mm});
            skArc(sketch, "E292.10.14", {"start": v(-38.7, 11.5) * mm, "mid": v(-38.63, 11.57) * mm, "end": v(-38.63, 11.67) * mm});
            skArc(sketch, "E292.10.15", {"start": v(-38.24, 10.4) * mm, "mid": v(-38.14, 10.4) * mm, "end": v(-38.07, 10.33) * mm});
            skArc(sketch, "E292.11.0", {"start": v(-37.47, 8.53) * mm, "mid": v(-37.31, 8.57) * mm, "end": v(-37.16, 8.63) * mm});
            skArc(sketch, "E292.11.1", {"start": v(-38, 8.78) * mm, "mid": v(-37.77, 8.58) * mm, "end": v(-37.47, 8.53) * mm});
            skArc(sketch, "E292.11.2", {"start": v(-36.86, 9.54) * mm, "mid": v(-37.11, 9.95) * mm, "end": v(-37.35, 10.37) * mm});
            skPoint(sketch, "E292.11.3", {"position": v(-37.38, 9.2) * mm});
            skArc(sketch, "E292.11.4", {"start": v(-38.02, 9.36) * mm, "mid": v(-37.93, 9.5) * mm, "end": v(-37.82, 9.61) * mm});
            skLineSegment(sketch, "E292.11.5", {"start": v(-36.28, 8.77) * mm, "end": v(-36.79, 8.35) * mm});
            skArc(sketch, "E292.11.6", {"start": v(-37.79, 9.8) * mm, "mid": v(-37.86, 9.93) * mm, "end": v(-37.93, 10.06) * mm});
            skLineSegment(sketch, "E292.11.7", {"start": v(-37.35, 10.37) * mm, "end": v(-37.93, 10.06) * mm});
            skArc(sketch, "E292.11.8", {"start": v(-38, 8.78) * mm, "mid": v(-38.1, 9.07) * mm, "end": v(-38.02, 9.36) * mm});
            skPoint(sketch, "E292.11.9", {"position": v(-36.86, 9.54) * mm});
            skArc(sketch, "E292.11.10", {"start": v(-37.17, 9.33) * mm, "mid": v(-37.44, 9.76) * mm, "end": v(-37.68, 10.2) * mm, "construction": true});
            skArc(sketch, "E292.11.11", {"start": v(-36.86, 9.54) * mm, "mid": v(-36.58, 9.15) * mm, "end": v(-36.28, 8.77) * mm});
            skPoint(sketch, "E292.11.12", {"position": v(-37.17, 9.33) * mm});
            skArc(sketch, "E292.11.13", {"start": v(-36.98, 8.59) * mm, "mid": v(-36.88, 8.47) * mm, "end": v(-36.79, 8.35) * mm});
            skArc(sketch, "E292.11.14", {"start": v(-37.82, 9.61) * mm, "mid": v(-37.77, 9.7) * mm, "end": v(-37.79, 9.8) * mm});
            skArc(sketch, "E292.11.15", {"start": v(-37.16, 8.63) * mm, "mid": v(-37.06, 8.64) * mm, "end": v(-36.98, 8.59) * mm});
            skArc(sketch, "E292.12.0", {"start": v(-36.04, 6.95) * mm, "mid": v(-35.89, 7) * mm, "end": v(-35.75, 7.1) * mm});
            skArc(sketch, "E292.12.1", {"start": v(-36.61, 7.08) * mm, "mid": v(-36.34, 6.93) * mm, "end": v(-36.04, 6.95) * mm});
            skArc(sketch, "E292.12.2", {"start": v(-35.64, 8.05) * mm, "mid": v(-35.97, 8.4) * mm, "end": v(-36.28, 8.77) * mm});
            skPoint(sketch, "E292.12.3", {"position": v(-36.08, 7.6) * mm});
            skArc(sketch, "E292.12.4", {"start": v(-36.74, 7.65) * mm, "mid": v(-36.68, 7.8) * mm, "end": v(-36.6, 7.93) * mm});
            skLineSegment(sketch, "E292.12.5", {"start": v(-34.92, 7.4) * mm, "end": v(-35.34, 6.9) * mm});
            skArc(sketch, "E292.12.6", {"start": v(-36.6, 8.12) * mm, "mid": v(-36.7, 8.24) * mm, "end": v(-36.79, 8.35) * mm});
            skLineSegment(sketch, "E292.12.7", {"start": v(-36.28, 8.77) * mm, "end": v(-36.79, 8.35) * mm});
            skArc(sketch, "E292.12.8", {"start": v(-36.61, 7.08) * mm, "mid": v(-36.76, 7.35) * mm, "end": v(-36.74, 7.65) * mm});
            skPoint(sketch, "E292.12.9", {"position": v(-35.64, 8.05) * mm});
            skArc(sketch, "E292.12.10", {"start": v(-35.9, 7.79) * mm, "mid": v(-36.25, 8.15) * mm, "end": v(-36.57, 8.53) * mm, "construction": true});
            skArc(sketch, "E292.12.11", {"start": v(-35.64, 8.05) * mm, "mid": v(-35.29, 7.72) * mm, "end": v(-34.92, 7.4) * mm});
            skPoint(sketch, "E292.12.12", {"position": v(-35.9, 7.79) * mm});
            skArc(sketch, "E292.12.13", {"start": v(-35.56, 7.1) * mm, "mid": v(-35.45, 7) * mm, "end": v(-35.34, 6.9) * mm});
            skArc(sketch, "E292.12.14", {"start": v(-36.6, 7.93) * mm, "mid": v(-36.56, 8.03) * mm, "end": v(-36.6, 8.12) * mm});
            skArc(sketch, "E292.12.15", {"start": v(-35.75, 7.1) * mm, "mid": v(-35.66, 7.13) * mm, "end": v(-35.56, 7.1) * mm});
            skArc(sketch, "E292.13.0", {"start": v(-34.33, 5.67) * mm, "mid": v(-34.2, 5.76) * mm, "end": v(-34.08, 5.87) * mm});
            skArc(sketch, "E292.13.1", {"start": v(-34.91, 5.68) * mm, "mid": v(-34.62, 5.6) * mm, "end": v(-34.33, 5.67) * mm});
            skArc(sketch, "E292.13.2", {"start": v(-34.15, 6.83) * mm, "mid": v(-34.54, 7.1) * mm, "end": v(-34.92, 7.4) * mm});
            skPoint(sketch, "E292.13.3", {"position": v(-34.5, 6.3) * mm});
            skArc(sketch, "E292.13.4", {"start": v(-35.15, 6.22) * mm, "mid": v(-35.12, 6.38) * mm, "end": v(-35.06, 6.53) * mm});
            skLineSegment(sketch, "E292.13.5", {"start": v(-33.32, 6.34) * mm, "end": v(-33.63, 5.76) * mm});
            skArc(sketch, "E292.13.6", {"start": v(-35.1, 6.71) * mm, "mid": v(-35.22, 6.8) * mm, "end": v(-35.34, 6.9) * mm});
            skLineSegment(sketch, "E292.13.7", {"start": v(-34.92, 7.4) * mm, "end": v(-35.34, 6.9) * mm});
            skArc(sketch, "E292.13.8", {"start": v(-34.91, 5.68) * mm, "mid": v(-35.11, 5.92) * mm, "end": v(-35.15, 6.22) * mm});
            skPoint(sketch, "E292.13.9", {"position": v(-34.15, 6.83) * mm});
            skArc(sketch, "E292.13.10", {"start": v(-34.36, 6.52) * mm, "mid": v(-34.76, 6.8) * mm, "end": v(-35.16, 7.12) * mm, "construction": true});
            skArc(sketch, "E292.13.11", {"start": v(-34.15, 6.83) * mm, "mid": v(-33.74, 6.57) * mm, "end": v(-33.32, 6.34) * mm});
            skPoint(sketch, "E292.13.12", {"position": v(-34.36, 6.52) * mm});
            skArc(sketch, "E292.13.13", {"start": v(-33.89, 5.9) * mm, "mid": v(-33.76, 5.83) * mm, "end": v(-33.63, 5.76) * mm});
            skArc(sketch, "E292.13.14", {"start": v(-35.06, 6.53) * mm, "mid": v(-35.05, 6.63) * mm, "end": v(-35.1, 6.71) * mm});
            skArc(sketch, "E292.13.15", {"start": v(-34.08, 5.87) * mm, "mid": v(-33.99, 5.92) * mm, "end": v(-33.89, 5.9) * mm});
            skArc(sketch, "E292.14.0", {"start": v(-32.4, 4.75) * mm, "mid": v(-32.28, 4.86) * mm, "end": v(-32.2, 5) * mm});
            skArc(sketch, "E292.14.1", {"start": v(-32.98, 4.65) * mm, "mid": v(-32.67, 4.61) * mm, "end": v(-32.4, 4.75) * mm});
            skArc(sketch, "E292.14.2", {"start": v(-32.45, 5.92) * mm, "mid": v(-32.89, 6.12) * mm, "end": v(-33.32, 6.34) * mm});
            skPoint(sketch, "E292.14.3", {"position": v(-32.69, 5.34) * mm});
            skArc(sketch, "E292.14.4", {"start": v(-33.32, 5.13) * mm, "mid": v(-33.31, 5.29) * mm, "end": v(-33.29, 5.45) * mm});
            skLineSegment(sketch, "E292.14.5", {"start": v(-31.54, 5.6) * mm, "end": v(-31.73, 4.97) * mm});
            skArc(sketch, "E292.14.6", {"start": v(-33.36, 5.62) * mm, "mid": v(-33.5, 5.69) * mm, "end": v(-33.63, 5.76) * mm});
            skLineSegment(sketch, "E292.14.7", {"start": v(-33.32, 6.34) * mm, "end": v(-33.63, 5.76) * mm});
            skArc(sketch, "E292.14.8", {"start": v(-32.98, 4.65) * mm, "mid": v(-33.22, 4.84) * mm, "end": v(-33.32, 5.13) * mm});
            skPoint(sketch, "E292.14.9", {"position": v(-32.45, 5.92) * mm});
            skArc(sketch, "E292.14.10", {"start": v(-32.6, 5.58) * mm, "mid": v(-33.05, 5.78) * mm, "end": v(-33.5, 6) * mm, "construction": true});
            skArc(sketch, "E292.14.11", {"start": v(-32.45, 5.92) * mm, "mid": v(-32, 5.75) * mm, "end": v(-31.54, 5.6) * mm});
            skPoint(sketch, "E292.14.12", {"position": v(-32.6, 5.58) * mm});
            skArc(sketch, "E292.14.13", {"start": v(-32.01, 5.06) * mm, "mid": v(-31.87, 5.02) * mm, "end": v(-31.73, 4.97) * mm});
            skArc(sketch, "E292.14.14", {"start": v(-33.29, 5.45) * mm, "mid": v(-33.3, 5.55) * mm, "end": v(-33.36, 5.62) * mm});
            skArc(sketch, "E292.14.15", {"start": v(-32.2, 5) * mm, "mid": v(-32.12, 5.06) * mm, "end": v(-32.01, 5.06) * mm});
            skArc(sketch, "E292.15.0", {"start": v(-30.32, 4.22) * mm, "mid": v(-30.24, 4.36) * mm, "end": v(-30.17, 4.5) * mm});
            skArc(sketch, "E292.15.1", {"start": v(-30.87, 4.01) * mm, "mid": v(-30.57, 4.04) * mm, "end": v(-30.32, 4.22) * mm});
            skArc(sketch, "E292.15.2", {"start": v(-30.6, 5.36) * mm, "mid": v(-31.08, 5.47) * mm, "end": v(-31.54, 5.6) * mm});
            skPoint(sketch, "E292.15.3", {"position": v(-30.73, 4.75) * mm});
            skArc(sketch, "E292.15.4", {"start": v(-31.3, 4.41) * mm, "mid": v(-31.33, 4.57) * mm, "end": v(-31.33, 4.73) * mm});
            skLineSegment(sketch, "E292.15.5", {"start": v(-29.65, 5.22) * mm, "end": v(-29.72, 4.57) * mm});
            skArc(sketch, "E292.15.6", {"start": v(-31.44, 4.89) * mm, "mid": v(-31.59, 4.93) * mm, "end": v(-31.73, 4.97) * mm});
            skLineSegment(sketch, "E292.15.7", {"start": v(-31.54, 5.6) * mm, "end": v(-31.73, 4.97) * mm});
            skArc(sketch, "E292.15.8", {"start": v(-30.87, 4.01) * mm, "mid": v(-31.15, 4.15) * mm, "end": v(-31.3, 4.41) * mm});
            skPoint(sketch, "E292.15.9", {"position": v(-30.6, 5.36) * mm});
            skArc(sketch, "E292.15.10", {"start": v(-30.68, 5) * mm, "mid": v(-31.17, 5.1) * mm, "end": v(-31.65, 5.24) * mm, "construction": true});
            skArc(sketch, "E292.15.11", {"start": v(-30.6, 5.36) * mm, "mid": v(-30.13, 5.28) * mm, "end": v(-29.65, 5.22) * mm});
            skPoint(sketch, "E292.15.12", {"position": v(-30.68, 5) * mm});
            skArc(sketch, "E292.15.13", {"start": v(-30.01, 4.6) * mm, "mid": v(-29.86, 4.59) * mm, "end": v(-29.72, 4.57) * mm});
            skArc(sketch, "E292.15.14", {"start": v(-31.33, 4.73) * mm, "mid": v(-31.36, 4.83) * mm, "end": v(-31.44, 4.89) * mm});
            skArc(sketch, "E292.15.15", {"start": v(-30.17, 4.5) * mm, "mid": v(-30.11, 4.58) * mm, "end": v(-30.01, 4.6) * mm});
            skArc(sketch, "E292.16.0", {"start": v(-28.19, 4.1) * mm, "mid": v(-28.13, 4.26) * mm, "end": v(-28.1, 4.42) * mm});
            skArc(sketch, "E292.16.1", {"start": v(-28.69, 3.8) * mm, "mid": v(-28.4, 3.88) * mm, "end": v(-28.19, 4.1) * mm});
            skArc(sketch, "E292.16.2", {"start": v(-28.69, 5.18) * mm, "mid": v(-29.17, 5.19) * mm, "end": v(-29.65, 5.22) * mm});
            skPoint(sketch, "E292.16.3", {"position": v(-28.69, 4.55) * mm});
            skArc(sketch, "E292.16.4", {"start": v(-29.19, 4.1) * mm, "mid": v(-29.25, 4.26) * mm, "end": v(-29.28, 4.42) * mm});
            skLineSegment(sketch, "E292.16.5", {"start": v(-27.73, 5.22) * mm, "end": v(-27.66, 4.57) * mm});
            skArc(sketch, "E292.16.6", {"start": v(-29.42, 4.55) * mm, "mid": v(-29.57, 4.56) * mm, "end": v(-29.72, 4.57) * mm});
            skLineSegment(sketch, "E292.16.7", {"start": v(-29.65, 5.22) * mm, "end": v(-29.72, 4.57) * mm});
            skArc(sketch, "E292.16.8", {"start": v(-28.69, 3.8) * mm, "mid": v(-28.98, 3.88) * mm, "end": v(-29.19, 4.1) * mm});
            skPoint(sketch, "E292.16.9", {"position": v(-28.69, 5.18) * mm});
            skArc(sketch, "E292.16.10", {"start": v(-28.69, 4.8) * mm, "mid": v(-29.19, 4.81) * mm, "end": v(-29.69, 4.85) * mm, "construction": true});
            skArc(sketch, "E292.16.11", {"start": v(-28.69, 5.18) * mm, "mid": v(-28.2, 5.19) * mm, "end": v(-27.73, 5.22) * mm});
            skPoint(sketch, "E292.16.12", {"position": v(-28.69, 4.8) * mm});
            skArc(sketch, "E292.16.13", {"start": v(-27.96, 4.55) * mm, "mid": v(-27.8, 4.56) * mm, "end": v(-27.66, 4.57) * mm});
            skArc(sketch, "E292.16.14", {"start": v(-29.28, 4.42) * mm, "mid": v(-29.33, 4.5) * mm, "end": v(-29.42, 4.55) * mm});
            skArc(sketch, "E292.16.15", {"start": v(-28.1, 4.42) * mm, "mid": v(-28.05, 4.5) * mm, "end": v(-27.96, 4.55) * mm});
            skArc(sketch, "E292.17.0", {"start": v(-26.07, 4.41) * mm, "mid": v(-26.05, 4.57) * mm, "end": v(-26.04, 4.73) * mm});
            skArc(sketch, "E292.17.1", {"start": v(-26.5, 4.01) * mm, "mid": v(-26.23, 4.15) * mm, "end": v(-26.07, 4.41) * mm});
            skArc(sketch, "E292.17.2", {"start": v(-26.77, 5.36) * mm, "mid": v(-27.25, 5.28) * mm, "end": v(-27.73, 5.22) * mm});
            skPoint(sketch, "E292.17.3", {"position": v(-26.65, 4.75) * mm});
            skArc(sketch, "E292.17.4", {"start": v(-27.05, 4.22) * mm, "mid": v(-27.14, 4.36) * mm, "end": v(-27.2, 4.5) * mm});
            skLineSegment(sketch, "E292.17.5", {"start": v(-25.84, 5.6) * mm, "end": v(-25.65, 4.97) * mm});
            skArc(sketch, "E292.17.6", {"start": v(-27.36, 4.6) * mm, "mid": v(-27.51, 4.59) * mm, "end": v(-27.66, 4.57) * mm});
            skLineSegment(sketch, "E292.17.7", {"start": v(-27.73, 5.22) * mm, "end": v(-27.66, 4.57) * mm});
            skArc(sketch, "E292.17.8", {"start": v(-26.5, 4.01) * mm, "mid": v(-26.8, 4.04) * mm, "end": v(-27.05, 4.22) * mm});
            skPoint(sketch, "E292.17.9", {"position": v(-26.77, 5.36) * mm});
            skArc(sketch, "E292.17.10", {"start": v(-26.7, 5) * mm, "mid": v(-27.2, 4.91) * mm, "end": v(-27.69, 4.85) * mm, "construction": true});
            skArc(sketch, "E292.17.11", {"start": v(-26.77, 5.36) * mm, "mid": v(-26.3, 5.47) * mm, "end": v(-25.84, 5.6) * mm});
            skPoint(sketch, "E292.17.12", {"position": v(-26.7, 5) * mm});
            skArc(sketch, "E292.17.13", {"start": v(-25.93, 4.89) * mm, "mid": v(-25.79, 4.93) * mm, "end": v(-25.65, 4.97) * mm});
            skArc(sketch, "E292.17.14", {"start": v(-27.2, 4.5) * mm, "mid": v(-27.27, 4.58) * mm, "end": v(-27.36, 4.6) * mm});
            skArc(sketch, "E292.17.15", {"start": v(-26.04, 4.73) * mm, "mid": v(-26.02, 4.83) * mm, "end": v(-25.93, 4.89) * mm});
            skArc(sketch, "E292.18.0", {"start": v(-24.06, 5.13) * mm, "mid": v(-24.06, 5.29) * mm, "end": v(-24.1, 5.45) * mm});
            skArc(sketch, "E292.18.1", {"start": v(-24.4, 4.65) * mm, "mid": v(-24.16, 4.84) * mm, "end": v(-24.06, 5.13) * mm});
            skArc(sketch, "E292.18.2", {"start": v(-24.93, 5.92) * mm, "mid": v(-25.38, 5.75) * mm, "end": v(-25.84, 5.6) * mm});
            skPoint(sketch, "E292.18.3", {"position": v(-24.69, 5.34) * mm});
            skArc(sketch, "E292.18.4", {"start": v(-24.98, 4.75) * mm, "mid": v(-25.1, 4.86) * mm, "end": v(-25.18, 5) * mm});
            skLineSegment(sketch, "E292.18.5", {"start": v(-24.06, 6.34) * mm, "end": v(-23.75, 5.76) * mm});
            skArc(sketch, "E292.18.6", {"start": v(-25.36, 5.06) * mm, "mid": v(-25.5, 5.02) * mm, "end": v(-25.65, 4.97) * mm});
            skLineSegment(sketch, "E292.18.7", {"start": v(-25.84, 5.6) * mm, "end": v(-25.65, 4.97) * mm});
            skArc(sketch, "E292.18.8", {"start": v(-24.4, 4.65) * mm, "mid": v(-24.7, 4.61) * mm, "end": v(-24.98, 4.75) * mm});
            skPoint(sketch, "E292.18.9", {"position": v(-24.93, 5.92) * mm});
            skArc(sketch, "E292.18.10", {"start": v(-24.79, 5.58) * mm, "mid": v(-25.25, 5.4) * mm, "end": v(-25.73, 5.24) * mm, "construction": true});
            skArc(sketch, "E292.18.11", {"start": v(-24.93, 5.92) * mm, "mid": v(-24.49, 6.12) * mm, "end": v(-24.06, 6.34) * mm});
            skPoint(sketch, "E292.18.12", {"position": v(-24.79, 5.58) * mm});
            skArc(sketch, "E292.18.13", {"start": v(-24.01, 5.62) * mm, "mid": v(-23.88, 5.69) * mm, "end": v(-23.75, 5.76) * mm});
            skArc(sketch, "E292.18.14", {"start": v(-25.18, 5) * mm, "mid": v(-25.26, 5.06) * mm, "end": v(-25.36, 5.06) * mm});
            skArc(sketch, "E292.18.15", {"start": v(-24.1, 5.45) * mm, "mid": v(-24.08, 5.55) * mm, "end": v(-24.01, 5.62) * mm});
            skArc(sketch, "E292.19.0", {"start": v(-22.22, 6.22) * mm, "mid": v(-22.26, 6.38) * mm, "end": v(-22.32, 6.53) * mm});
            skArc(sketch, "E292.19.1", {"start": v(-22.46, 5.68) * mm, "mid": v(-22.27, 5.92) * mm, "end": v(-22.22, 6.22) * mm});
            skArc(sketch, "E292.19.2", {"start": v(-23.23, 6.83) * mm, "mid": v(-23.64, 6.57) * mm, "end": v(-24.06, 6.34) * mm});
            skPoint(sketch, "E292.19.3", {"position": v(-22.88, 6.3) * mm});
            skArc(sketch, "E292.19.4", {"start": v(-23.05, 5.67) * mm, "mid": v(-23.18, 5.76) * mm, "end": v(-23.3, 5.87) * mm});
            skLineSegment(sketch, "E292.19.5", {"start": v(-22.46, 7.4) * mm, "end": v(-22.04, 6.9) * mm});
            skArc(sketch, "E292.19.6", {"start": v(-23.49, 5.9) * mm, "mid": v(-23.62, 5.83) * mm, "end": v(-23.75, 5.76) * mm});
            skLineSegment(sketch, "E292.19.7", {"start": v(-24.06, 6.34) * mm, "end": v(-23.75, 5.76) * mm});
            skArc(sketch, "E292.19.8", {"start": v(-22.46, 5.68) * mm, "mid": v(-22.76, 5.6) * mm, "end": v(-23.05, 5.67) * mm});
            skPoint(sketch, "E292.19.9", {"position": v(-23.23, 6.83) * mm});
            skArc(sketch, "E292.19.10", {"start": v(-23.02, 6.52) * mm, "mid": v(-23.44, 6.25) * mm, "end": v(-23.88, 6) * mm, "construction": true});
            skArc(sketch, "E292.19.11", {"start": v(-23.23, 6.83) * mm, "mid": v(-22.84, 7.1) * mm, "end": v(-22.46, 7.4) * mm});
            skPoint(sketch, "E292.19.12", {"position": v(-23.02, 6.52) * mm});
            skArc(sketch, "E292.19.13", {"start": v(-22.27, 6.71) * mm, "mid": v(-22.16, 6.8) * mm, "end": v(-22.04, 6.9) * mm});
            skArc(sketch, "E292.19.14", {"start": v(-23.3, 5.87) * mm, "mid": v(-23.39, 5.92) * mm, "end": v(-23.49, 5.9) * mm});
            skArc(sketch, "E292.19.15", {"start": v(-22.32, 6.53) * mm, "mid": v(-22.33, 6.63) * mm, "end": v(-22.27, 6.71) * mm});
            skArc(sketch, "E292.20.0", {"start": v(-20.63, 7.65) * mm, "mid": v(-20.7, 7.8) * mm, "end": v(-20.79, 7.93) * mm});
            skArc(sketch, "E292.20.1", {"start": v(-20.77, 7.08) * mm, "mid": v(-20.62, 7.35) * mm, "end": v(-20.63, 7.65) * mm});
            skArc(sketch, "E292.20.2", {"start": v(-21.74, 8.05) * mm, "mid": v(-22.1, 7.72) * mm, "end": v(-22.46, 7.4) * mm});
            skPoint(sketch, "E292.20.3", {"position": v(-21.3, 7.6) * mm});
            skArc(sketch, "E292.20.4", {"start": v(-21.34, 6.95) * mm, "mid": v(-21.49, 7) * mm, "end": v(-21.62, 7.1) * mm});
            skLineSegment(sketch, "E292.20.5", {"start": v(-21.1, 8.77) * mm, "end": v(-20.59, 8.35) * mm});
            skArc(sketch, "E292.20.6", {"start": v(-21.81, 7.1) * mm, "mid": v(-21.93, 7) * mm, "end": v(-22.04, 6.9) * mm});
            skLineSegment(sketch, "E292.20.7", {"start": v(-22.46, 7.4) * mm, "end": v(-22.04, 6.9) * mm});
            skArc(sketch, "E292.20.8", {"start": v(-20.77, 7.08) * mm, "mid": v(-21.03, 6.93) * mm, "end": v(-21.34, 6.95) * mm});
            skPoint(sketch, "E292.20.9", {"position": v(-21.74, 8.05) * mm});
            skArc(sketch, "E292.20.10", {"start": v(-21.48, 7.79) * mm, "mid": v(-21.84, 7.44) * mm, "end": v(-22.22, 7.12) * mm, "construction": true});
            skArc(sketch, "E292.20.11", {"start": v(-21.74, 8.05) * mm, "mid": v(-21.4, 8.4) * mm, "end": v(-21.1, 8.77) * mm});
            skPoint(sketch, "E292.20.12", {"position": v(-21.48, 7.79) * mm});
            skArc(sketch, "E292.20.13", {"start": v(-20.78, 8.12) * mm, "mid": v(-20.68, 8.24) * mm, "end": v(-20.59, 8.35) * mm});
            skArc(sketch, "E292.20.14", {"start": v(-21.62, 7.1) * mm, "mid": v(-21.72, 7.13) * mm, "end": v(-21.81, 7.1) * mm});
            skArc(sketch, "E292.20.15", {"start": v(-20.79, 7.93) * mm, "mid": v(-20.82, 8.03) * mm, "end": v(-20.78, 8.12) * mm});
            skArc(sketch, "E292.21.0", {"start": v(-19.35, 9.36) * mm, "mid": v(-19.45, 9.5) * mm, "end": v(-19.56, 9.61) * mm});
            skArc(sketch, "E292.21.1", {"start": v(-19.37, 8.78) * mm, "mid": v(-19.28, 9.07) * mm, "end": v(-19.35, 9.36) * mm});
            skArc(sketch, "E292.21.2", {"start": v(-20.52, 9.54) * mm, "mid": v(-20.8, 9.15) * mm, "end": v(-21.1, 8.77) * mm});
            skPoint(sketch, "E292.21.3", {"position": v(-20, 9.2) * mm});
            skArc(sketch, "E292.21.4", {"start": v(-19.9, 8.53) * mm, "mid": v(-20.07, 8.57) * mm, "end": v(-20.22, 8.63) * mm});
            skLineSegment(sketch, "E292.21.5", {"start": v(-20.02, 10.37) * mm, "end": v(-19.45, 10.06) * mm});
            skArc(sketch, "E292.21.6", {"start": v(-20.4, 8.59) * mm, "mid": v(-20.5, 8.47) * mm, "end": v(-20.59, 8.35) * mm});
            skLineSegment(sketch, "E292.21.7", {"start": v(-21.1, 8.77) * mm, "end": v(-20.59, 8.35) * mm});
            skArc(sketch, "E292.21.8", {"start": v(-19.37, 8.78) * mm, "mid": v(-19.6, 8.58) * mm, "end": v(-19.9, 8.53) * mm});
            skPoint(sketch, "E292.21.9", {"position": v(-20.52, 9.54) * mm});
            skArc(sketch, "E292.21.10", {"start": v(-20.2, 9.33) * mm, "mid": v(-20.5, 8.92) * mm, "end": v(-20.8, 8.53) * mm, "construction": true});
            skArc(sketch, "E292.21.11", {"start": v(-20.52, 9.54) * mm, "mid": v(-20.26, 9.95) * mm, "end": v(-20.02, 10.37) * mm});
            skPoint(sketch, "E292.21.12", {"position": v(-20.2, 9.33) * mm});
            skArc(sketch, "E292.21.13", {"start": v(-19.6, 9.8) * mm, "mid": v(-19.52, 9.93) * mm, "end": v(-19.45, 10.06) * mm});
            skArc(sketch, "E292.21.14", {"start": v(-20.22, 8.63) * mm, "mid": v(-20.32, 8.64) * mm, "end": v(-20.4, 8.59) * mm});
            skArc(sketch, "E292.21.15", {"start": v(-19.56, 9.61) * mm, "mid": v(-19.6, 9.7) * mm, "end": v(-19.6, 9.8) * mm});
            skArc(sketch, "E292.22.0", {"start": v(-18.43, 11.3) * mm, "mid": v(-18.55, 11.4) * mm, "end": v(-18.68, 11.5) * mm});
            skArc(sketch, "E292.22.1", {"start": v(-18.34, 10.71) * mm, "mid": v(-18.3, 11.02) * mm, "end": v(-18.43, 11.3) * mm});
            skArc(sketch, "E292.22.2", {"start": v(-19.61, 11.24) * mm, "mid": v(-19.8, 10.8) * mm, "end": v(-20.02, 10.37) * mm});
            skPoint(sketch, "E292.22.3", {"position": v(-19.03, 11) * mm});
            skArc(sketch, "E292.22.4", {"start": v(-18.82, 10.37) * mm, "mid": v(-18.98, 10.37) * mm, "end": v(-19.14, 10.4) * mm});
            skLineSegment(sketch, "E292.22.5", {"start": v(-19.29, 12.15) * mm, "end": v(-18.66, 11.96) * mm});
            skArc(sketch, "E292.22.6", {"start": v(-19.3, 10.33) * mm, "mid": v(-19.38, 10.2) * mm, "end": v(-19.45, 10.06) * mm});
            skLineSegment(sketch, "E292.22.7", {"start": v(-20.02, 10.37) * mm, "end": v(-19.45, 10.06) * mm});
            skArc(sketch, "E292.22.8", {"start": v(-18.34, 10.71) * mm, "mid": v(-18.53, 10.47) * mm, "end": v(-18.82, 10.37) * mm});
            skPoint(sketch, "E292.22.9", {"position": v(-19.61, 11.24) * mm});
            skArc(sketch, "E292.22.10", {"start": v(-19.26, 11.1) * mm, "mid": v(-19.47, 10.64) * mm, "end": v(-19.7, 10.2) * mm, "construction": true});
            skArc(sketch, "E292.22.11", {"start": v(-19.61, 11.24) * mm, "mid": v(-19.44, 11.7) * mm, "end": v(-19.29, 12.15) * mm});
            skPoint(sketch, "E292.22.12", {"position": v(-19.26, 11.1) * mm});
            skArc(sketch, "E292.22.13", {"start": v(-18.75, 11.67) * mm, "mid": v(-18.7, 11.82) * mm, "end": v(-18.66, 11.96) * mm});
            skArc(sketch, "E292.22.14", {"start": v(-19.14, 10.4) * mm, "mid": v(-19.24, 10.4) * mm, "end": v(-19.3, 10.33) * mm});
            skArc(sketch, "E292.22.15", {"start": v(-18.68, 11.5) * mm, "mid": v(-18.75, 11.57) * mm, "end": v(-18.75, 11.67) * mm});
            skArc(sketch, "E292.23.0", {"start": v(-17.9, 13.36) * mm, "mid": v(-18.04, 13.45) * mm, "end": v(-18.2, 13.52) * mm});
            skArc(sketch, "E292.23.1", {"start": v(-17.7, 12.81) * mm, "mid": v(-17.73, 13.12) * mm, "end": v(-17.9, 13.36) * mm});
            skArc(sketch, "E292.23.2", {"start": v(-19.05, 13.08) * mm, "mid": v(-19.16, 12.61) * mm, "end": v(-19.29, 12.15) * mm});
            skPoint(sketch, "E292.23.3", {"position": v(-18.44, 12.96) * mm});
            skArc(sketch, "E292.23.4", {"start": v(-18.1, 12.39) * mm, "mid": v(-18.26, 12.36) * mm, "end": v(-18.42, 12.36) * mm});
            skLineSegment(sketch, "E292.23.5", {"start": v(-18.91, 14.04) * mm, "end": v(-18.26, 13.97) * mm});
            skArc(sketch, "E292.23.6", {"start": v(-18.58, 12.24) * mm, "mid": v(-18.62, 12.1) * mm, "end": v(-18.66, 11.96) * mm});
            skLineSegment(sketch, "E292.23.7", {"start": v(-19.29, 12.15) * mm, "end": v(-18.66, 11.96) * mm});
            skArc(sketch, "E292.23.8", {"start": v(-17.7, 12.81) * mm, "mid": v(-17.84, 12.54) * mm, "end": v(-18.1, 12.39) * mm});
            skPoint(sketch, "E292.23.9", {"position": v(-19.05, 13.08) * mm});
            skArc(sketch, "E292.23.10", {"start": v(-18.68, 13.01) * mm, "mid": v(-18.8, 12.52) * mm, "end": v(-18.93, 12.04) * mm, "construction": true});
            skArc(sketch, "E292.23.11", {"start": v(-19.05, 13.08) * mm, "mid": v(-18.97, 13.56) * mm, "end": v(-18.91, 14.04) * mm});
            skPoint(sketch, "E292.23.12", {"position": v(-18.68, 13.01) * mm});
            skArc(sketch, "E292.23.13", {"start": v(-18.3, 13.68) * mm, "mid": v(-18.28, 13.82) * mm, "end": v(-18.26, 13.97) * mm});
            skArc(sketch, "E292.23.14", {"start": v(-18.42, 12.36) * mm, "mid": v(-18.52, 12.33) * mm, "end": v(-18.58, 12.24) * mm});
            skArc(sketch, "E292.23.15", {"start": v(-18.2, 13.52) * mm, "mid": v(-18.27, 13.58) * mm, "end": v(-18.3, 13.68) * mm});
            skArc(sketch, "E292.24.0", {"start": v(-17.8, 15.5) * mm, "mid": v(-17.95, 15.56) * mm, "end": v(-18.1, 15.6) * mm});
            skArc(sketch, "E292.24.1", {"start": v(-17.48, 15) * mm, "mid": v(-17.57, 15.3) * mm, "end": v(-17.8, 15.5) * mm});
            skArc(sketch, "E292.24.2", {"start": v(-18.86, 15) * mm, "mid": v(-18.88, 14.52) * mm, "end": v(-18.91, 14.04) * mm});
            skPoint(sketch, "E292.24.3", {"position": v(-18.23, 15) * mm});
            skArc(sketch, "E292.24.4", {"start": v(-17.8, 14.5) * mm, "mid": v(-17.95, 14.44) * mm, "end": v(-18.1, 14.4) * mm});
            skLineSegment(sketch, "E292.24.5", {"start": v(-18.91, 15.96) * mm, "end": v(-18.26, 16.03) * mm});
            skArc(sketch, "E292.24.6", {"start": v(-18.23, 14.27) * mm, "mid": v(-18.25, 14.12) * mm, "end": v(-18.26, 13.97) * mm});
            skLineSegment(sketch, "E292.24.7", {"start": v(-18.91, 14.04) * mm, "end": v(-18.26, 13.97) * mm});
            skArc(sketch, "E292.24.8", {"start": v(-17.48, 15) * mm, "mid": v(-17.57, 14.7) * mm, "end": v(-17.8, 14.5) * mm});
            skPoint(sketch, "E292.24.9", {"position": v(-18.86, 15) * mm});
            skArc(sketch, "E292.24.10", {"start": v(-18.49, 15) * mm, "mid": v(-18.5, 14.5) * mm, "end": v(-18.54, 14) * mm, "construction": true});
            skArc(sketch, "E292.24.11", {"start": v(-18.86, 15) * mm, "mid": v(-18.88, 15.48) * mm, "end": v(-18.91, 15.96) * mm});
            skPoint(sketch, "E292.24.12", {"position": v(-18.49, 15) * mm});
            skArc(sketch, "E292.24.13", {"start": v(-18.23, 15.73) * mm, "mid": v(-18.25, 15.88) * mm, "end": v(-18.26, 16.03) * mm});
            skArc(sketch, "E292.24.14", {"start": v(-18.1, 14.4) * mm, "mid": v(-18.2, 14.36) * mm, "end": v(-18.23, 14.27) * mm});
            skArc(sketch, "E292.24.15", {"start": v(-18.1, 15.6) * mm, "mid": v(-18.2, 15.64) * mm, "end": v(-18.23, 15.73) * mm});
            skArc(sketch, "E292.25.0", {"start": v(-18.1, 17.61) * mm, "mid": v(-18.26, 17.64) * mm, "end": v(-18.42, 17.64) * mm});
            skArc(sketch, "E292.25.1", {"start": v(-17.7, 17.19) * mm, "mid": v(-17.84, 17.46) * mm, "end": v(-18.1, 17.61) * mm});
            skArc(sketch, "E292.25.2", {"start": v(-19.05, 16.92) * mm, "mid": v(-18.97, 16.44) * mm, "end": v(-18.91, 15.96) * mm});
            skPoint(sketch, "E292.25.3", {"position": v(-18.44, 17.04) * mm});
            skArc(sketch, "E292.25.4", {"start": v(-17.9, 16.64) * mm, "mid": v(-18.04, 16.55) * mm, "end": v(-18.2, 16.48) * mm});
            skLineSegment(sketch, "E292.25.5", {"start": v(-19.29, 17.85) * mm, "end": v(-18.66, 18.04) * mm});
            skArc(sketch, "E292.25.6", {"start": v(-18.3, 16.32) * mm, "mid": v(-18.28, 16.18) * mm, "end": v(-18.26, 16.03) * mm});
            skLineSegment(sketch, "E292.25.7", {"start": v(-18.91, 15.96) * mm, "end": v(-18.26, 16.03) * mm});
            skArc(sketch, "E292.25.8", {"start": v(-17.7, 17.19) * mm, "mid": v(-17.73, 16.88) * mm, "end": v(-17.9, 16.64) * mm});
            skPoint(sketch, "E292.25.9", {"position": v(-19.05, 16.92) * mm});
            skArc(sketch, "E292.25.10", {"start": v(-18.68, 16.99) * mm, "mid": v(-18.6, 16.5) * mm, "end": v(-18.54, 16) * mm, "construction": true});
            skArc(sketch, "E292.25.11", {"start": v(-19.05, 16.92) * mm, "mid": v(-19.16, 17.39) * mm, "end": v(-19.29, 17.85) * mm});
            skPoint(sketch, "E292.25.12", {"position": v(-18.68, 16.99) * mm});
            skArc(sketch, "E292.25.13", {"start": v(-18.58, 17.76) * mm, "mid": v(-18.62, 17.9) * mm, "end": v(-18.66, 18.04) * mm});
            skArc(sketch, "E292.25.14", {"start": v(-18.2, 16.48) * mm, "mid": v(-18.27, 16.42) * mm, "end": v(-18.3, 16.32) * mm});
            skArc(sketch, "E292.25.15", {"start": v(-18.42, 17.64) * mm, "mid": v(-18.52, 17.67) * mm, "end": v(-18.58, 17.76) * mm});
            skArc(sketch, "E292.26.0", {"start": v(-18.82, 19.63) * mm, "mid": v(-18.98, 19.63) * mm, "end": v(-19.14, 19.6) * mm});
            skArc(sketch, "E292.26.1", {"start": v(-18.34, 19.29) * mm, "mid": v(-18.53, 19.53) * mm, "end": v(-18.82, 19.63) * mm});
            skArc(sketch, "E292.26.2", {"start": v(-19.61, 18.76) * mm, "mid": v(-19.44, 18.3) * mm, "end": v(-19.29, 17.85) * mm});
            skPoint(sketch, "E292.26.3", {"position": v(-19.03, 19) * mm});
            skArc(sketch, "E292.26.4", {"start": v(-18.43, 18.7) * mm, "mid": v(-18.55, 18.6) * mm, "end": v(-18.68, 18.5) * mm});
            skLineSegment(sketch, "E292.26.5", {"start": v(-20.02, 19.63) * mm, "end": v(-19.45, 19.94) * mm});
            skArc(sketch, "E292.26.6", {"start": v(-18.75, 18.33) * mm, "mid": v(-18.7, 18.18) * mm, "end": v(-18.66, 18.04) * mm});
            skLineSegment(sketch, "E292.26.7", {"start": v(-19.29, 17.85) * mm, "end": v(-18.66, 18.04) * mm});
            skArc(sketch, "E292.26.8", {"start": v(-18.34, 19.29) * mm, "mid": v(-18.3, 18.98) * mm, "end": v(-18.43, 18.7) * mm});
            skPoint(sketch, "E292.26.9", {"position": v(-19.61, 18.76) * mm});
            skArc(sketch, "E292.26.10", {"start": v(-19.26, 18.9) * mm, "mid": v(-19.08, 18.44) * mm, "end": v(-18.93, 17.96) * mm, "construction": true});
            skArc(sketch, "E292.26.11", {"start": v(-19.61, 18.76) * mm, "mid": v(-19.8, 19.2) * mm, "end": v(-20.02, 19.63) * mm});
            skPoint(sketch, "E292.26.12", {"position": v(-19.26, 18.9) * mm});
            skArc(sketch, "E292.26.13", {"start": v(-19.3, 19.67) * mm, "mid": v(-19.38, 19.8) * mm, "end": v(-19.45, 19.94) * mm});
            skArc(sketch, "E292.26.14", {"start": v(-18.68, 18.5) * mm, "mid": v(-18.75, 18.43) * mm, "end": v(-18.75, 18.33) * mm});
            skArc(sketch, "E292.26.15", {"start": v(-19.14, 19.6) * mm, "mid": v(-19.24, 19.6) * mm, "end": v(-19.3, 19.67) * mm});
            skArc(sketch, "E292.27.0", {"start": v(-19.9, 21.47) * mm, "mid": v(-20.07, 21.43) * mm, "end": v(-20.22, 21.37) * mm});
            skArc(sketch, "E292.27.1", {"start": v(-19.37, 21.22) * mm, "mid": v(-19.6, 21.42) * mm, "end": v(-19.9, 21.47) * mm});
            skArc(sketch, "E292.27.2", {"start": v(-20.52, 20.46) * mm, "mid": v(-20.26, 20.05) * mm, "end": v(-20.02, 19.63) * mm});
            skPoint(sketch, "E292.27.3", {"position": v(-20, 20.8) * mm});
            skArc(sketch, "E292.27.4", {"start": v(-19.35, 20.64) * mm, "mid": v(-19.45, 20.5) * mm, "end": v(-19.56, 20.39) * mm});
            skLineSegment(sketch, "E292.27.5", {"start": v(-21.1, 21.23) * mm, "end": v(-20.59, 21.65) * mm});
            skArc(sketch, "E292.27.6", {"start": v(-19.6, 20.2) * mm, "mid": v(-19.52, 20.07) * mm, "end": v(-19.45, 19.94) * mm});
            skLineSegment(sketch, "E292.27.7", {"start": v(-20.02, 19.63) * mm, "end": v(-19.45, 19.94) * mm});
            skArc(sketch, "E292.27.8", {"start": v(-19.37, 21.22) * mm, "mid": v(-19.28, 20.93) * mm, "end": v(-19.35, 20.64) * mm});
            skPoint(sketch, "E292.27.9", {"position": v(-20.52, 20.46) * mm});
            skArc(sketch, "E292.27.10", {"start": v(-20.2, 20.67) * mm, "mid": v(-19.94, 20.24) * mm, "end": v(-19.7, 19.8) * mm, "construction": true});
            skArc(sketch, "E292.27.11", {"start": v(-20.52, 20.46) * mm, "mid": v(-20.8, 20.85) * mm, "end": v(-21.1, 21.23) * mm});
            skPoint(sketch, "E292.27.12", {"position": v(-20.2, 20.67) * mm});
            skArc(sketch, "E292.27.13", {"start": v(-20.4, 21.41) * mm, "mid": v(-20.5, 21.53) * mm, "end": v(-20.59, 21.65) * mm});
            skArc(sketch, "E292.27.14", {"start": v(-19.56, 20.39) * mm, "mid": v(-19.6, 20.3) * mm, "end": v(-19.6, 20.2) * mm});
            skArc(sketch, "E292.27.15", {"start": v(-20.22, 21.37) * mm, "mid": v(-20.32, 21.36) * mm, "end": v(-20.4, 21.41) * mm});
            skArc(sketch, "E292.28.0", {"start": v(-21.34, 23.05) * mm, "mid": v(-21.49, 23) * mm, "end": v(-21.62, 22.9) * mm});
            skArc(sketch, "E292.28.1", {"start": v(-20.77, 22.92) * mm, "mid": v(-21.03, 23.07) * mm, "end": v(-21.34, 23.05) * mm});
            skArc(sketch, "E292.28.2", {"start": v(-21.74, 21.95) * mm, "mid": v(-21.4, 21.6) * mm, "end": v(-21.1, 21.23) * mm});
            skPoint(sketch, "E292.28.3", {"position": v(-21.3, 22.4) * mm});
            skArc(sketch, "E292.28.4", {"start": v(-20.63, 22.35) * mm, "mid": v(-20.7, 22.2) * mm, "end": v(-20.79, 22.07) * mm});
            skLineSegment(sketch, "E292.28.5", {"start": v(-22.46, 22.6) * mm, "end": v(-22.04, 23.1) * mm});
            skArc(sketch, "E292.28.6", {"start": v(-20.78, 21.88) * mm, "mid": v(-20.68, 21.76) * mm, "end": v(-20.59, 21.65) * mm});
            skLineSegment(sketch, "E292.28.7", {"start": v(-21.1, 21.23) * mm, "end": v(-20.59, 21.65) * mm});
            skArc(sketch, "E292.28.8", {"start": v(-20.77, 22.92) * mm, "mid": v(-20.62, 22.65) * mm, "end": v(-20.63, 22.35) * mm});
            skPoint(sketch, "E292.28.9", {"position": v(-21.74, 21.95) * mm});
            skArc(sketch, "E292.28.10", {"start": v(-21.48, 22.21) * mm, "mid": v(-21.13, 21.85) * mm, "end": v(-20.8, 21.47) * mm, "construction": true});
            skArc(sketch, "E292.28.11", {"start": v(-21.74, 21.95) * mm, "mid": v(-22.1, 22.28) * mm, "end": v(-22.46, 22.6) * mm});
            skPoint(sketch, "E292.28.12", {"position": v(-21.48, 22.21) * mm});
            skArc(sketch, "E292.28.13", {"start": v(-21.81, 22.9) * mm, "mid": v(-21.93, 23) * mm, "end": v(-22.04, 23.1) * mm});
            skArc(sketch, "E292.28.14", {"start": v(-20.79, 22.07) * mm, "mid": v(-20.82, 21.97) * mm, "end": v(-20.78, 21.88) * mm});
            skArc(sketch, "E292.28.15", {"start": v(-21.62, 22.9) * mm, "mid": v(-21.72, 22.87) * mm, "end": v(-21.81, 22.9) * mm});
            skArc(sketch, "E292.29.0", {"start": v(-23.05, 24.33) * mm, "mid": v(-23.18, 24.24) * mm, "end": v(-23.3, 24.13) * mm});
            skArc(sketch, "E292.29.1", {"start": v(-22.46, 24.32) * mm, "mid": v(-22.76, 24.4) * mm, "end": v(-23.05, 24.33) * mm});
            skArc(sketch, "E292.29.2", {"start": v(-23.23, 23.17) * mm, "mid": v(-22.84, 22.9) * mm, "end": v(-22.46, 22.6) * mm});
            skPoint(sketch, "E292.29.3", {"position": v(-22.88, 23.7) * mm});
            skArc(sketch, "E292.29.4", {"start": v(-22.22, 23.78) * mm, "mid": v(-22.26, 23.62) * mm, "end": v(-22.32, 23.47) * mm});
            skLineSegment(sketch, "E292.29.5", {"start": v(-24.06, 23.66) * mm, "end": v(-23.75, 24.24) * mm});
            skArc(sketch, "E292.29.6", {"start": v(-22.27, 23.29) * mm, "mid": v(-22.16, 23.2) * mm, "end": v(-22.04, 23.1) * mm});
            skLineSegment(sketch, "E292.29.7", {"start": v(-22.46, 22.6) * mm, "end": v(-22.04, 23.1) * mm});
            skArc(sketch, "E292.29.8", {"start": v(-22.46, 24.32) * mm, "mid": v(-22.27, 24.08) * mm, "end": v(-22.22, 23.78) * mm});
            skPoint(sketch, "E292.29.9", {"position": v(-23.23, 23.17) * mm});
            skArc(sketch, "E292.29.10", {"start": v(-23.02, 23.48) * mm, "mid": v(-22.61, 23.2) * mm, "end": v(-22.22, 22.88) * mm, "construction": true});
            skArc(sketch, "E292.29.11", {"start": v(-23.23, 23.17) * mm, "mid": v(-23.64, 23.43) * mm, "end": v(-24.06, 23.66) * mm});
            skPoint(sketch, "E292.29.12", {"position": v(-23.02, 23.48) * mm});
            skArc(sketch, "E292.29.13", {"start": v(-23.49, 24.1) * mm, "mid": v(-23.62, 24.17) * mm, "end": v(-23.75, 24.24) * mm});
            skArc(sketch, "E292.29.14", {"start": v(-22.32, 23.47) * mm, "mid": v(-22.33, 23.37) * mm, "end": v(-22.27, 23.29) * mm});
            skArc(sketch, "E292.29.15", {"start": v(-23.3, 24.13) * mm, "mid": v(-23.39, 24.08) * mm, "end": v(-23.49, 24.1) * mm});
            skArc(sketch, "E292.30.0", {"start": v(-24.98, 25.25) * mm, "mid": v(-25.1, 25.14) * mm, "end": v(-25.18, 25) * mm});
            skArc(sketch, "E292.30.1", {"start": v(-24.4, 25.35) * mm, "mid": v(-24.7, 25.39) * mm, "end": v(-24.98, 25.25) * mm});
            skArc(sketch, "E292.30.2", {"start": v(-24.93, 24.08) * mm, "mid": v(-24.49, 23.88) * mm, "end": v(-24.06, 23.66) * mm});
            skPoint(sketch, "E292.30.3", {"position": v(-24.69, 24.66) * mm});
            skArc(sketch, "E292.30.4", {"start": v(-24.06, 24.87) * mm, "mid": v(-24.06, 24.71) * mm, "end": v(-24.1, 24.55) * mm});
            skLineSegment(sketch, "E292.30.5", {"start": v(-25.84, 24.4) * mm, "end": v(-25.65, 25.03) * mm});
            skArc(sketch, "E292.30.6", {"start": v(-24.01, 24.38) * mm, "mid": v(-23.88, 24.31) * mm, "end": v(-23.75, 24.24) * mm});
            skLineSegment(sketch, "E292.30.7", {"start": v(-24.06, 23.66) * mm, "end": v(-23.75, 24.24) * mm});
            skArc(sketch, "E292.30.8", {"start": v(-24.4, 25.35) * mm, "mid": v(-24.16, 25.16) * mm, "end": v(-24.06, 24.87) * mm});
            skPoint(sketch, "E292.30.9", {"position": v(-24.93, 24.08) * mm});
            skArc(sketch, "E292.30.10", {"start": v(-24.79, 24.42) * mm, "mid": v(-24.33, 24.22) * mm, "end": v(-23.88, 24) * mm, "construction": true});
            skArc(sketch, "E292.30.11", {"start": v(-24.93, 24.08) * mm, "mid": v(-25.38, 24.25) * mm, "end": v(-25.84, 24.4) * mm});
            skPoint(sketch, "E292.30.12", {"position": v(-24.79, 24.42) * mm});
            skArc(sketch, "E292.30.13", {"start": v(-25.36, 24.94) * mm, "mid": v(-25.5, 24.98) * mm, "end": v(-25.65, 25.03) * mm});
            skArc(sketch, "E292.30.14", {"start": v(-24.1, 24.55) * mm, "mid": v(-24.08, 24.45) * mm, "end": v(-24.01, 24.38) * mm});
            skArc(sketch, "E292.30.15", {"start": v(-25.18, 25) * mm, "mid": v(-25.26, 24.94) * mm, "end": v(-25.36, 24.94) * mm});
            skArc(sketch, "E292.31.0", {"start": v(-27.05, 25.78) * mm, "mid": v(-27.14, 25.64) * mm, "end": v(-27.2, 25.5) * mm});
            skArc(sketch, "E292.31.1", {"start": v(-26.5, 25.99) * mm, "mid": v(-26.8, 25.96) * mm, "end": v(-27.05, 25.78) * mm});
            skArc(sketch, "E292.31.2", {"start": v(-26.77, 24.64) * mm, "mid": v(-26.3, 24.53) * mm, "end": v(-25.84, 24.4) * mm});
            skPoint(sketch, "E292.31.3", {"position": v(-26.65, 25.25) * mm});
            skArc(sketch, "E292.31.4", {"start": v(-26.07, 25.59) * mm, "mid": v(-26.05, 25.43) * mm, "end": v(-26.04, 25.27) * mm});
            skArc(sketch, "E292.31.6", {"start": v(-25.93, 25.11) * mm, "mid": v(-25.79, 25.07) * mm, "end": v(-25.65, 25.03) * mm});
            skLineSegment(sketch, "E292.31.7", {"start": v(-25.84, 24.4) * mm, "end": v(-25.65, 25.03) * mm});
            skArc(sketch, "E292.31.8", {"start": v(-26.5, 25.99) * mm, "mid": v(-26.23, 25.85) * mm, "end": v(-26.07, 25.59) * mm});
            skPoint(sketch, "E292.31.9", {"position": v(-26.77, 24.64) * mm});
            skArc(sketch, "E292.31.10", {"start": v(-26.7, 25) * mm, "mid": v(-26.2, 24.9) * mm, "end": v(-25.73, 24.76) * mm, "construction": true});
            skArc(sketch, "E292.31.11", {"start": v(-26.77, 24.64) * mm, "mid": v(-27.25, 24.72) * mm, "end": v(-27.73, 24.78) * mm});
            skPoint(sketch, "E292.31.12", {"position": v(-26.7, 25) * mm});
            skArc(sketch, "E292.31.13", {"start": v(-27.36, 25.4) * mm, "mid": v(-27.51, 25.41) * mm, "end": v(-27.66, 25.43) * mm});
            skArc(sketch, "E292.31.14", {"start": v(-26.04, 25.27) * mm, "mid": v(-26.02, 25.17) * mm, "end": v(-25.93, 25.11) * mm});
            skArc(sketch, "E292.31.15", {"start": v(-27.2, 25.5) * mm, "mid": v(-27.27, 25.42) * mm, "end": v(-27.36, 25.4) * mm});
            skArc(sketch, "E293.0", {"start": v(-38.94, 15) * mm, "mid": v(-28.69, 4.75) * mm, "end": v(-18.44, 15) * mm});
            skSolve(sketch);
        }
        {
            var Q0;
            Q0=qSketchRegion(id+"F47",true);
            extrude(context, id + "F48", {"entities" : qUnion([Q0]), "operationType" : NewBodyOperationType.REMOVE, "endBound" : BoundingType.SYMMETRIC, "oppositeDirection" : true, "depth" : 6.5 * mm});
        }
    });
